# Revit family: STWS_приток
name_source: partatom
category: Воздухораспределители
revit_build: Autodesk Revit 2014 (Build: 20130308_1515(x64)
units: mm (PartAtom-declared; Revit-internal decimal feet)

## types (2484) — shared parameters
A = 52 мм
URL = http://inplast.ru
margins = 10 мм
Изготовитель = INPLAST-SMAY
Описание = Двухрядная решетка с горизонтальными направляющими

## per-type parameters (varying)
| type | Aef | C | C' | D | D' | n1 | n2 | Материал | Тип крепежа |
| STWS-100х100-SL | 0.006 м² | 100 мм | 95 мм | 100 мм | 95 мм | 10 | 10 | Сталь_RAL9016 (INPLAST) | саморезы |
| STWS-125х100-SL | 0.008 м² | 125 мм | 120 мм | 100 мм | 95 мм | 10 | 13 | Сталь_RAL9016 (INPLAST) | саморезы |
| STWS-125х125-SL | 0.009 м² | 125 мм | 120 мм | 125 мм | 120 мм | 13 | 13 | Сталь_RAL9016 (INPLAST) | саморезы |
| STWS-150х100-SL | 0.009 м² | 150 мм | 145 мм | 100 мм | 95 мм | 10 | 15 | Сталь_RAL9016 (INPLAST) | саморезы |
| STWS-150х125-SL | 0.011 м² | 150 мм | 145 мм | 125 мм | 120 мм | 13 | 15 | Сталь_RAL9016 (INPLAST) | саморезы |
| STWS-150х150-SL | 0.014 м² | 150 мм | 145 мм | 150 мм | 145 мм | 15 | 15 | Сталь_RAL9016 (INPLAST) | саморезы |
| STWS-200х100-SL | 0.012 м² | 200 мм | 195 мм | 100 мм | 95 мм | 10 | 20 | Сталь_RAL9016 (INPLAST) | саморезы |
| STWS-200х125-SL | 0.015 м² | 200 мм | 195 мм | 125 мм | 120 мм | 13 | 20 | Сталь_RAL9016 (INPLAST) | саморезы |
| STWS-200х150-SL | 0.018 м² | 200 мм | 195 мм | 150 мм | 145 мм | 15 | 20 | Сталь_RAL9016 (INPLAST) | саморезы |
| STWS-200х200-SL | 0.024 м² | 200 мм | 195 мм | 200 мм | 195 мм | 20 | 20 | Сталь_RAL9016 (INPLAST) | саморезы |
| STWS-225х100-SL | 0.014 м² | 225 мм | 220 мм | 100 мм | 95 мм | 10 | 23 | Сталь_RAL9016 (INPLAST) | саморезы |
| STWS-225х125-SL | 0.017 м² | 225 мм | 220 мм | 125 мм | 120 мм | 13 | 23 | Сталь_RAL9016 (INPLAST) | саморезы |
| STWS-225х150-SL | 0.020 м² | 225 мм | 220 мм | 150 мм | 145 мм | 15 | 23 | Сталь_RAL9016 (INPLAST) | саморезы |
| STWS-225х200-SL | 0.027 м² | 225 мм | 220 мм | 200 мм | 195 мм | 20 | 23 | Сталь_RAL9016 (INPLAST) | саморезы |
| STWS-225х225-SL | 0.030 м² | 225 мм | 220 мм | 225 мм | 220 мм | 23 | 23 | Сталь_RAL9016 (INPLAST) | саморезы |
| STWS-250х100-SL | 0.015 м² | 250 мм | 245 мм | 100 мм | 95 мм | 10 | 25 | Сталь_RAL9016 (INPLAST) | саморезы |
| STWS-250х125-SL | 0.019 м² | 250 мм | 245 мм | 125 мм | 120 мм | 13 | 25 | Сталь_RAL9016 (INPLAST) | саморезы |
| STWS-250х150-SL | 0.023 м² | 250 мм | 245 мм | 150 мм | 145 мм | 15 | 25 | Сталь_RAL9016 (INPLAST) | саморезы |
| STWS-250х200-SL | 0.030 м² | 250 мм | 245 мм | 200 мм | 195 мм | 20 | 25 | Сталь_RAL9016 (INPLAST) | саморезы |
| STWS-250х225-SL | 0.034 м² | 250 мм | 245 мм | 225 мм | 220 мм | 23 | 25 | Сталь_RAL9016 (INPLAST) | саморезы |
| STWS-250х250-SL | 0.038 м² | 250 мм | 245 мм | 250 мм | 245 мм | 25 | 25 | Сталь_RAL9016 (INPLAST) | саморезы |
| STWS-300х100-SL | 0.018 м² | 300 мм | 295 мм | 100 мм | 95 мм | 10 | 30 | Сталь_RAL9016 (INPLAST) | саморезы |
| STWS-300х125-SL | 0.023 м² | 300 мм | 295 мм | 125 мм | 120 мм | 13 | 30 | Сталь_RAL9016 (INPLAST) | саморезы |
| STWS-300х150-SL | 0.027 м² | 300 мм | 295 мм | 150 мм | 145 мм | 15 | 30 | Сталь_RAL9016 (INPLAST) | саморезы |
| STWS-300х200-SL | 0.036 м² | 300 мм | 295 мм | 200 мм | 195 мм | 20 | 30 | Сталь_RAL9016 (INPLAST) | саморезы |
| STWS-300х225-SL | 0.041 м² | 300 мм | 295 мм | 225 мм | 220 мм | 23 | 30 | Сталь_RAL9016 (INPLAST) | саморезы |
| STWS-300х250-SL | 0.045 м² | 300 мм | 295 мм | 250 мм | 245 мм | 25 | 30 | Сталь_RAL9016 (INPLAST) | саморезы |
| STWS-300х300-SL | 0.054 м² | 300 мм | 295 мм | 300 мм | 295 мм | 30 | 30 | Сталь_RAL9016 (INPLAST) | саморезы |
| STWS-325х100-SL | 0.020 м² | 325 мм | 320 мм | 100 мм | 95 мм | 10 | 33 | Сталь_RAL9016 (INPLAST) | саморезы |
| STWS-325х125-SL | 0.024 м² | 325 мм | 320 мм | 125 мм | 120 мм | 13 | 33 | Сталь_RAL9016 (INPLAST) | саморезы |
| STWS-325х150-SL | 0.029 м² | 325 мм | 320 мм | 150 мм | 145 мм | 15 | 33 | Сталь_RAL9016 (INPLAST) | саморезы |
| STWS-325х200-SL | 0.039 м² | 325 мм | 320 мм | 200 мм | 195 мм | 20 | 33 | Сталь_RAL9016 (INPLAST) | саморезы |
| STWS-325х225-SL | 0.044 м² | 325 мм | 320 мм | 225 мм | 220 мм | 23 | 33 | Сталь_RAL9016 (INPLAST) | саморезы |
| STWS-325х250-SL | 0.049 м² | 325 мм | 320 мм | 250 мм | 245 мм | 25 | 33 | Сталь_RAL9016 (INPLAST) | саморезы |
| STWS-325х300-SL | 0.059 м² | 325 мм | 320 мм | 300 мм | 295 мм | 30 | 33 | Сталь_RAL9016 (INPLAST) | саморезы |
| STWS-325х325-SL | 0.064 м² | 325 мм | 320 мм | 325 мм | 320 мм | 33 | 33 | Сталь_RAL9016 (INPLAST) | саморезы |
| STWS-350х100-SL | 0.021 м² | 350 мм | 345 мм | 100 мм | 95 мм | 10 | 35 | Сталь_RAL9016 (INPLAST) | саморезы |
| STWS-350х125-SL | 0.026 м² | 350 мм | 345 мм | 125 мм | 120 мм | 13 | 35 | Сталь_RAL9016 (INPLAST) | саморезы |
| STWS-350х150-SL | 0.032 м² | 350 мм | 345 мм | 150 мм | 145 мм | 15 | 35 | Сталь_RAL9016 (INPLAST) | саморезы |
| STWS-350х200-SL | 0.042 м² | 350 мм | 345 мм | 200 мм | 195 мм | 20 | 35 | Сталь_RAL9016 (INPLAST) | саморезы |
| STWS-350х225-SL | 0.047 м² | 350 мм | 345 мм | 225 мм | 220 мм | 23 | 35 | Сталь_RAL9016 (INPLAST) | саморезы |
| STWS-350х250-SL | 0.053 м² | 350 мм | 345 мм | 250 мм | 245 мм | 25 | 35 | Сталь_RAL9016 (INPLAST) | саморезы |
| STWS-350х300-SL | 0.063 м² | 350 мм | 345 мм | 300 мм | 295 мм | 30 | 35 | Сталь_RAL9016 (INPLAST) | саморезы |
| STWS-350х325-SL | 0.068 м² | 350 мм | 345 мм | 325 мм | 320 мм | 33 | 35 | Сталь_RAL9016 (INPLAST) | саморезы |
| STWS-350х350-SL | 0.074 м² | 350 мм | 345 мм | 350 мм | 345 мм | 35 | 35 | Сталь_RAL9016 (INPLAST) | саморезы |
| STWS-400х100-SL | 0.024 м² | 400 мм | 395 мм | 100 мм | 95 мм | 10 | 40 | Сталь_RAL9016 (INPLAST) | саморезы |
| STWS-400х125-SL | 0.030 м² | 400 мм | 395 мм | 125 мм | 120 мм | 13 | 40 | Сталь_RAL9016 (INPLAST) | саморезы |
| STWS-400х150-SL | 0.036 м² | 400 мм | 395 мм | 150 мм | 145 мм | 15 | 40 | Сталь_RAL9016 (INPLAST) | саморезы |
| STWS-400х200-SL | 0.048 м² | 400 мм | 395 мм | 200 мм | 195 мм | 20 | 40 | Сталь_RAL9016 (INPLAST) | саморезы |
| STWS-400х225-SL | 0.054 м² | 400 мм | 395 мм | 225 мм | 220 мм | 23 | 40 | Сталь_RAL9016 (INPLAST) | саморезы |
| STWS-400х250-SL | 0.060 м² | 400 мм | 395 мм | 250 мм | 245 мм | 25 | 40 | Сталь_RAL9016 (INPLAST) | саморезы |
| STWS-400х300-SL | 0.072 м² | 400 мм | 395 мм | 300 мм | 295 мм | 30 | 40 | Сталь_RAL9016 (INPLAST) | саморезы |
| STWS-400х325-SL | 0.078 м² | 400 мм | 395 мм | 325 мм | 320 мм | 33 | 40 | Сталь_RAL9016 (INPLAST) | саморезы |
| STWS-400х350-SL | 0.084 м² | 400 мм | 395 мм | 350 мм | 345 мм | 35 | 40 | Сталь_RAL9016 (INPLAST) | саморезы |
| STWS-400х400-SL | 0.096 м² | 400 мм | 395 мм | 400 мм | 395 мм | 40 | 40 | Сталь_RAL9016 (INPLAST) | саморезы |
| STWS-425х100-SL | 0.026 м² | 425 мм | 420 мм | 100 мм | 95 мм | 10 | 43 | Сталь_RAL9016 (INPLAST) | саморезы |
| STWS-425х125-SL | 0.032 м² | 425 мм | 420 мм | 125 мм | 120 мм | 13 | 43 | Сталь_RAL9016 (INPLAST) | саморезы |
| STWS-425х150-SL | 0.038 м² | 425 мм | 420 мм | 150 мм | 145 мм | 15 | 43 | Сталь_RAL9016 (INPLAST) | саморезы |
| STWS-425х200-SL | 0.051 м² | 425 мм | 420 мм | 200 мм | 195 мм | 20 | 43 | Сталь_RAL9016 (INPLAST) | саморезы |
| STWS-425х225-SL | 0.058 м² | 425 мм | 420 мм | 225 мм | 220 мм | 23 | 43 | Сталь_RAL9016 (INPLAST) | саморезы |
| STWS-425х250-SL | 0.064 м² | 425 мм | 420 мм | 250 мм | 245 мм | 25 | 43 | Сталь_RAL9016 (INPLAST) | саморезы |
| STWS-425х300-SL | 0.077 м² | 425 мм | 420 мм | 300 мм | 295 мм | 30 | 43 | Сталь_RAL9016 (INPLAST) | саморезы |
| STWS-425х325-SL | 0.083 м² | 425 мм | 420 мм | 325 мм | 320 мм | 33 | 43 | Сталь_RAL9016 (INPLAST) | саморезы |
| STWS-425х350-SL | 0.089 м² | 425 мм | 420 мм | 350 мм | 345 мм | 35 | 43 | Сталь_RAL9016 (INPLAST) | саморезы |
| STWS-425х400-SL | 0.102 м² | 425 мм | 420 мм | 400 мм | 395 мм | 40 | 43 | Сталь_RAL9016 (INPLAST) | саморезы |
| STWS-425х425-SL | 0.109 м² | 425 мм | 420 мм | 425 мм | 420 мм | 43 | 43 | Сталь_RAL9016 (INPLAST) | саморезы |
| STWS-450х100-SL | 0.027 м² | 450 мм | 445 мм | 100 мм | 95 мм | 10 | 45 | Сталь_RAL9016 (INPLAST) | саморезы |
| STWS-450х125-SL | 0.034 м² | 450 мм | 445 мм | 125 мм | 120 мм | 13 | 45 | Сталь_RAL9016 (INPLAST) | саморезы |
| STWS-450х150-SL | 0.041 м² | 450 мм | 445 мм | 150 мм | 145 мм | 15 | 45 | Сталь_RAL9016 (INPLAST) | саморезы |
| STWS-450х200-SL | 0.054 м² | 450 мм | 445 мм | 200 мм | 195 мм | 20 | 45 | Сталь_RAL9016 (INPLAST) | саморезы |
| STWS-450х225-SL | 0.061 м² | 450 мм | 445 мм | 225 мм | 220 мм | 23 | 45 | Сталь_RAL9016 (INPLAST) | саморезы |
| STWS-450х250-SL | 0.068 м² | 450 мм | 445 мм | 250 мм | 245 мм | 25 | 45 | Сталь_RAL9016 (INPLAST) | саморезы |
| STWS-450х300-SL | 0.081 м² | 450 мм | 445 мм | 300 мм | 295 мм | 30 | 45 | Сталь_RAL9016 (INPLAST) | саморезы |
| STWS-450х325-SL | 0.088 м² | 450 мм | 445 мм | 325 мм | 320 мм | 33 | 45 | Сталь_RAL9016 (INPLAST) | саморезы |
| STWS-450х350-SL | 0.095 м² | 450 мм | 445 мм | 350 мм | 345 мм | 35 | 45 | Сталь_RAL9016 (INPLAST) | саморезы |
| STWS-450х400-SL | 0.108 м² | 450 мм | 445 мм | 400 мм | 395 мм | 40 | 45 | Сталь_RAL9016 (INPLAST) | саморезы |
| STWS-450х425-SL | 0.115 м² | 450 мм | 445 мм | 425 мм | 420 мм | 43 | 45 | Сталь_RAL9016 (INPLAST) | саморезы |
| STWS-450х450-SL | 0.122 м² | 450 мм | 445 мм | 450 мм | 445 мм | 45 | 45 | Сталь_RAL9016 (INPLAST) | саморезы |
| STWS-500х100-SL | 0.030 м² | 500 мм | 495 мм | 100 мм | 95 мм | 10 | 50 | Сталь_RAL9016 (INPLAST) | саморезы |
| STWS-500х125-SL | 0.038 м² | 500 мм | 495 мм | 125 мм | 120 мм | 13 | 50 | Сталь_RAL9016 (INPLAST) | саморезы |
| STWS-500х150-SL | 0.045 м² | 500 мм | 495 мм | 150 мм | 145 мм | 15 | 50 | Сталь_RAL9016 (INPLAST) | саморезы |
| STWS-500х200-SL | 0.060 м² | 500 мм | 495 мм | 200 мм | 195 мм | 20 | 50 | Сталь_RAL9016 (INPLAST) | саморезы |
| STWS-500х225-SL | 0.068 м² | 500 мм | 495 мм | 225 мм | 220 мм | 23 | 50 | Сталь_RAL9016 (INPLAST) | саморезы |
| STWS-500х250-SL | 0.075 м² | 500 мм | 495 мм | 250 мм | 245 мм | 25 | 50 | Сталь_RAL9016 (INPLAST) | саморезы |
| STWS-500х300-SL | 0.090 м² | 500 мм | 495 мм | 300 мм | 295 мм | 30 | 50 | Сталь_RAL9016 (INPLAST) | саморезы |
| STWS-500х325-SL | 0.098 м² | 500 мм | 495 мм | 325 мм | 320 мм | 33 | 50 | Сталь_RAL9016 (INPLAST) | саморезы |
| STWS-500х350-SL | 0.105 м² | 500 мм | 495 мм | 350 мм | 345 мм | 35 | 50 | Сталь_RAL9016 (INPLAST) | саморезы |
| STWS-500х400-SL | 0.120 м² | 500 мм | 495 мм | 400 мм | 395 мм | 40 | 50 | Сталь_RAL9016 (INPLAST) | саморезы |
| STWS-500х425-SL | 0.128 м² | 500 мм | 495 мм | 425 мм | 420 мм | 43 | 50 | Сталь_RAL9016 (INPLAST) | саморезы |
| STWS-500х450-SL | 0.135 м² | 500 мм | 495 мм | 450 мм | 445 мм | 45 | 50 | Сталь_RAL9016 (INPLAST) | саморезы |
| STWS-500х500-SL | 0.150 м² | 500 мм | 495 мм | 500 мм | 495 мм | 50 | 50 | Сталь_RAL9016 (INPLAST) | саморезы |
| STWS-525х100-SL | 0.032 м² | 525 мм | 520 мм | 100 мм | 95 мм | 10 | 53 | Сталь_RAL9016 (INPLAST) | саморезы |
| STWS-525х125-SL | 0.039 м² | 525 мм | 520 мм | 125 мм | 120 мм | 13 | 53 | Сталь_RAL9016 (INPLAST) | саморезы |
| STWS-525х150-SL | 0.047 м² | 525 мм | 520 мм | 150 мм | 145 мм | 15 | 53 | Сталь_RAL9016 (INPLAST) | саморезы |
| STWS-525х200-SL | 0.063 м² | 525 мм | 520 мм | 200 мм | 195 мм | 20 | 53 | Сталь_RAL9016 (INPLAST) | саморезы |
| STWS-525х225-SL | 0.071 м² | 525 мм | 520 мм | 225 мм | 220 мм | 23 | 53 | Сталь_RAL9016 (INPLAST) | саморезы |
| STWS-525х250-SL | 0.079 м² | 525 мм | 520 мм | 250 мм | 245 мм | 25 | 53 | Сталь_RAL9016 (INPLAST) | саморезы |
| STWS-525х300-SL | 0.095 м² | 525 мм | 520 мм | 300 мм | 295 мм | 30 | 53 | Сталь_RAL9016 (INPLAST) | саморезы |
| STWS-525х325-SL | 0.103 м² | 525 мм | 520 мм | 325 мм | 320 мм | 33 | 53 | Сталь_RAL9016 (INPLAST) | саморезы |
| STWS-525х350-SL | 0.111 м² | 525 мм | 520 мм | 350 мм | 345 мм | 35 | 53 | Сталь_RAL9016 (INPLAST) | саморезы |
| STWS-525х400-SL | 0.126 м² | 525 мм | 520 мм | 400 мм | 395 мм | 40 | 53 | Сталь_RAL9016 (INPLAST) | саморезы |
| STWS-525х425-SL | 0.134 м² | 525 мм | 520 мм | 425 мм | 420 мм | 43 | 53 | Сталь_RAL9016 (INPLAST) | саморезы |
| STWS-525х450-SL | 0.142 м² | 525 мм | 520 мм | 450 мм | 445 мм | 45 | 53 | Сталь_RAL9016 (INPLAST) | саморезы |
| STWS-525х500-SL | 0.158 м² | 525 мм | 520 мм | 500 мм | 495 мм | 50 | 53 | Сталь_RAL9016 (INPLAST) | саморезы |
| STWS-525х525-SL | 0.166 м² | 525 мм | 520 мм | 525 мм | 520 мм | 53 | 53 | Сталь_RAL9016 (INPLAST) | саморезы |
| STWS-550х100-SL | 0.033 м² | 550 мм | 545 мм | 100 мм | 95 мм | 10 | 55 | Сталь_RAL9016 (INPLAST) | саморезы |
| STWS-550х125-SL | 0.041 м² | 550 мм | 545 мм | 125 мм | 120 мм | 13 | 55 | Сталь_RAL9016 (INPLAST) | саморезы |
| STWS-550х150-SL | 0.050 м² | 550 мм | 545 мм | 150 мм | 145 мм | 15 | 55 | Сталь_RAL9016 (INPLAST) | саморезы |
| STWS-550х200-SL | 0.066 м² | 550 мм | 545 мм | 200 мм | 195 мм | 20 | 55 | Сталь_RAL9016 (INPLAST) | саморезы |
| STWS-550х225-SL | 0.074 м² | 550 мм | 545 мм | 225 мм | 220 мм | 23 | 55 | Сталь_RAL9016 (INPLAST) | саморезы |
| STWS-550х250-SL | 0.083 м² | 550 мм | 545 мм | 250 мм | 245 мм | 25 | 55 | Сталь_RAL9016 (INPLAST) | саморезы |
| STWS-550х300-SL | 0.099 м² | 550 мм | 545 мм | 300 мм | 295 мм | 30 | 55 | Сталь_RAL9016 (INPLAST) | саморезы |
| STWS-550х325-SL | 0.108 м² | 550 мм | 545 мм | 325 мм | 320 мм | 33 | 55 | Сталь_RAL9016 (INPLAST) | саморезы |
| STWS-550х350-SL | 0.116 м² | 550 мм | 545 мм | 350 мм | 345 мм | 35 | 55 | Сталь_RAL9016 (INPLAST) | саморезы |
| STWS-550х400-SL | 0.132 м² | 550 мм | 545 мм | 400 мм | 395 мм | 40 | 55 | Сталь_RAL9016 (INPLAST) | саморезы |
| STWS-550х425-SL | 0.141 м² | 550 мм | 545 мм | 425 мм | 420 мм | 43 | 55 | Сталь_RAL9016 (INPLAST) | саморезы |
| STWS-550х450-SL | 0.149 м² | 550 мм | 545 мм | 450 мм | 445 мм | 45 | 55 | Сталь_RAL9016 (INPLAST) | саморезы |
| STWS-550х500-SL | 0.165 м² | 550 мм | 545 мм | 500 мм | 495 мм | 50 | 55 | Сталь_RAL9016 (INPLAST) | саморезы |
| STWS-550х525-SL | 0.174 м² | 550 мм | 545 мм | 525 мм | 520 мм | 53 | 55 | Сталь_RAL9016 (INPLAST) | саморезы |
| STWS-550х550-SL | 0.182 м² | 550 мм | 545 мм | 550 мм | 545 мм | 55 | 55 | Сталь_RAL9016 (INPLAST) | саморезы |
| STWS-600х100-SL | 0.036 м² | 600 мм | 595 мм | 100 мм | 95 мм | 10 | 60 | Сталь_RAL9016 (INPLAST) | саморезы |
| STWS-600х125-SL | 0.045 м² | 600 мм | 595 мм | 125 мм | 120 мм | 13 | 60 | Сталь_RAL9016 (INPLAST) | саморезы |
| STWS-600х150-SL | 0.054 м² | 600 мм | 595 мм | 150 мм | 145 мм | 15 | 60 | Сталь_RAL9016 (INPLAST) | саморезы |
| STWS-600х200-SL | 0.072 м² | 600 мм | 595 мм | 200 мм | 195 мм | 20 | 60 | Сталь_RAL9016 (INPLAST) | саморезы |
| STWS-600х225-SL | 0.081 м² | 600 мм | 595 мм | 225 мм | 220 мм | 23 | 60 | Сталь_RAL9016 (INPLAST) | саморезы |
| STWS-600х250-SL | 0.090 м² | 600 мм | 595 мм | 250 мм | 245 мм | 25 | 60 | Сталь_RAL9016 (INPLAST) | саморезы |
| STWS-600х300-SL | 0.108 м² | 600 мм | 595 мм | 300 мм | 295 мм | 30 | 60 | Сталь_RAL9016 (INPLAST) | саморезы |
| STWS-600х325-SL | 0.117 м² | 600 мм | 595 мм | 325 мм | 320 мм | 33 | 60 | Сталь_RAL9016 (INPLAST) | саморезы |
| STWS-600х350-SL | 0.126 м² | 600 мм | 595 мм | 350 мм | 345 мм | 35 | 60 | Сталь_RAL9016 (INPLAST) | саморезы |
| STWS-600х400-SL | 0.144 м² | 600 мм | 595 мм | 400 мм | 395 мм | 40 | 60 | Сталь_RAL9016 (INPLAST) | саморезы |
| STWS-600х425-SL | 0.153 м² | 600 мм | 595 мм | 425 мм | 420 мм | 43 | 60 | Сталь_RAL9016 (INPLAST) | саморезы |
| STWS-600х450-SL | 0.162 м² | 600 мм | 595 мм | 450 мм | 445 мм | 45 | 60 | Сталь_RAL9016 (INPLAST) | саморезы |
| STWS-600х500-SL | 0.180 м² | 600 мм | 595 мм | 500 мм | 495 мм | 50 | 60 | Сталь_RAL9016 (INPLAST) | саморезы |
| STWS-600х525-SL | 0.190 м² | 600 мм | 595 мм | 525 мм | 520 мм | 53 | 60 | Сталь_RAL9016 (INPLAST) | саморезы |
| STWS-600х550-SL | 0.199 м² | 600 мм | 595 мм | 550 мм | 545 мм | 55 | 60 | Сталь_RAL9016 (INPLAST) | саморезы |
| STWS-600х600-SL | 0.217 м² | 600 мм | 595 мм | 600 мм | 595 мм | 60 | 60 | Сталь_RAL9016 (INPLAST) | саморезы |
| STWS-625х100-SL | 0.038 м² | 625 мм | 620 мм | 100 мм | 95 мм | 10 | 63 | Сталь_RAL9016 (INPLAST) | саморезы |
| STWS-625х125-SL | 0.047 м² | 625 мм | 620 мм | 125 мм | 120 мм | 13 | 63 | Сталь_RAL9016 (INPLAST) | саморезы |
| STWS-625х150-SL | 0.056 м² | 625 мм | 620 мм | 150 мм | 145 мм | 15 | 63 | Сталь_RAL9016 (INPLAST) | саморезы |
| STWS-625х200-SL | 0.075 м² | 625 мм | 620 мм | 200 мм | 195 мм | 20 | 63 | Сталь_RAL9016 (INPLAST) | саморезы |
| STWS-625х225-SL | 0.085 м² | 625 мм | 620 мм | 225 мм | 220 мм | 23 | 63 | Сталь_RAL9016 (INPLAST) | саморезы |
| STWS-625х250-SL | 0.094 м² | 625 мм | 620 мм | 250 мм | 245 мм | 25 | 63 | Сталь_RAL9016 (INPLAST) | саморезы |
| STWS-625х300-SL | 0.113 м² | 625 мм | 620 мм | 300 мм | 295 мм | 30 | 63 | Сталь_RAL9016 (INPLAST) | саморезы |
| STWS-625х325-SL | 0.122 м² | 625 мм | 620 мм | 325 мм | 320 мм | 33 | 63 | Сталь_RAL9016 (INPLAST) | саморезы |
| STWS-625х350-SL | 0.132 м² | 625 мм | 620 мм | 350 мм | 345 мм | 35 | 63 | Сталь_RAL9016 (INPLAST) | саморезы |
| STWS-625х400-SL | 0.150 м² | 625 мм | 620 мм | 400 мм | 395 мм | 40 | 63 | Сталь_RAL9016 (INPLAST) | саморезы |
| STWS-625х425-SL | 0.160 м² | 625 мм | 620 мм | 425 мм | 420 мм | 43 | 63 | Сталь_RAL9016 (INPLAST) | саморезы |
| STWS-625х450-SL | 0.169 м² | 625 мм | 620 мм | 450 мм | 445 мм | 45 | 63 | Сталь_RAL9016 (INPLAST) | саморезы |
| STWS-625х500-SL | 0.188 м² | 625 мм | 620 мм | 500 мм | 495 мм | 50 | 63 | Сталь_RAL9016 (INPLAST) | саморезы |
| STWS-625х525-SL | 0.197 м² | 625 мм | 620 мм | 525 мм | 520 мм | 53 | 63 | Сталь_RAL9016 (INPLAST) | саморезы |
| STWS-625х550-SL | 0.207 м² | 625 мм | 620 мм | 550 мм | 545 мм | 55 | 63 | Сталь_RAL9016 (INPLAST) | саморезы |
| STWS-625х600-SL | 0.226 м² | 625 мм | 620 мм | 600 мм | 595 мм | 60 | 63 | Сталь_RAL9016 (INPLAST) | саморезы |
| STWS-625х625-SL | 0.235 м² | 625 мм | 620 мм | 625 мм | 620 мм | 63 | 63 | Сталь_RAL9016 (INPLAST) | саморезы |
| STWS-650х100-SL | 0.039 м² | 650 мм | 645 мм | 100 мм | 95 мм | 10 | 65 | Сталь_RAL9016 (INPLAST) | саморезы |
| STWS-650х125-SL | 0.049 м² | 650 мм | 645 мм | 125 мм | 120 мм | 13 | 65 | Сталь_RAL9016 (INPLAST) | саморезы |
| STWS-650х150-SL | 0.059 м² | 650 мм | 645 мм | 150 мм | 145 мм | 15 | 65 | Сталь_RAL9016 (INPLAST) | саморезы |
| STWS-650х200-SL | 0.078 м² | 650 мм | 645 мм | 200 мм | 195 мм | 20 | 65 | Сталь_RAL9016 (INPLAST) | саморезы |
| STWS-650х225-SL | 0.088 м² | 650 мм | 645 мм | 225 мм | 220 мм | 23 | 65 | Сталь_RAL9016 (INPLAST) | саморезы |
| STWS-650х250-SL | 0.098 м² | 650 мм | 645 мм | 250 мм | 245 мм | 25 | 65 | Сталь_RAL9016 (INPLAST) | саморезы |
| STWS-650х300-SL | 0.117 м² | 650 мм | 645 мм | 300 мм | 295 мм | 30 | 65 | Сталь_RAL9016 (INPLAST) | саморезы |
| STWS-650х325-SL | 0.127 м² | 650 мм | 645 мм | 325 мм | 320 мм | 33 | 65 | Сталь_RAL9016 (INPLAST) | саморезы |
| STWS-650х350-SL | 0.137 м² | 650 мм | 645 мм | 350 мм | 345 мм | 35 | 65 | Сталь_RAL9016 (INPLAST) | саморезы |
| STWS-650х400-SL | 0.156 м² | 650 мм | 645 мм | 400 мм | 395 мм | 40 | 65 | Сталь_RAL9016 (INPLAST) | саморезы |
| STWS-650х425-SL | 0.166 м² | 650 мм | 645 мм | 425 мм | 420 мм | 43 | 65 | Сталь_RAL9016 (INPLAST) | саморезы |
| STWS-650х450-SL | 0.176 м² | 650 мм | 645 мм | 450 мм | 445 мм | 45 | 65 | Сталь_RAL9016 (INPLAST) | саморезы |
| STWS-650х500-SL | 0.196 м² | 650 мм | 645 мм | 500 мм | 495 мм | 50 | 65 | Сталь_RAL9016 (INPLAST) | саморезы |
| STWS-650х525-SL | 0.205 м² | 650 мм | 645 мм | 525 мм | 520 мм | 53 | 65 | Сталь_RAL9016 (INPLAST) | саморезы |
| STWS-650х550-SL | 0.215 м² | 650 мм | 645 мм | 550 мм | 545 мм | 55 | 65 | Сталь_RAL9016 (INPLAST) | саморезы |
| STWS-650х600-SL | 0.235 м² | 650 мм | 645 мм | 600 мм | 595 мм | 60 | 65 | Сталь_RAL9016 (INPLAST) | саморезы |
| STWS-650х625-SL | 0.244 м² | 650 мм | 645 мм | 625 мм | 620 мм | 63 | 65 | Сталь_RAL9016 (INPLAST) | саморезы |
| STWS-650х650-SL | 0.254 м² | 650 мм | 645 мм | 650 мм | 645 мм | 65 | 65 | Сталь_RAL9016 (INPLAST) | саморезы |
| STWS-700х100-SL | 0.042 м² | 700 мм | 695 мм | 100 мм | 95 мм | 10 | 70 | Сталь_RAL9016 (INPLAST) | саморезы |
| STWS-700х125-SL | 0.053 м² | 700 мм | 695 мм | 125 мм | 120 мм | 13 | 70 | Сталь_RAL9016 (INPLAST) | саморезы |
| STWS-700х150-SL | 0.063 м² | 700 мм | 695 мм | 150 мм | 145 мм | 15 | 70 | Сталь_RAL9016 (INPLAST) | саморезы |
| STWS-700х200-SL | 0.084 м² | 700 мм | 695 мм | 200 мм | 195 мм | 20 | 70 | Сталь_RAL9016 (INPLAST) | саморезы |
| STWS-700х225-SL | 0.095 м² | 700 мм | 695 мм | 225 мм | 220 мм | 23 | 70 | Сталь_RAL9016 (INPLAST) | саморезы |
| STWS-700х250-SL | 0.105 м² | 700 мм | 695 мм | 250 мм | 245 мм | 25 | 70 | Сталь_RAL9016 (INPLAST) | саморезы |
| STWS-700х300-SL | 0.126 м² | 700 мм | 695 мм | 300 мм | 295 мм | 30 | 70 | Сталь_RAL9016 (INPLAST) | саморезы |
| STWS-700х325-SL | 0.137 м² | 700 мм | 695 мм | 325 мм | 320 мм | 33 | 70 | Сталь_RAL9016 (INPLAST) | саморезы |
| STWS-700х350-SL | 0.147 м² | 700 мм | 695 мм | 350 мм | 345 мм | 35 | 70 | Сталь_RAL9016 (INPLAST) | саморезы |
| STWS-700х400-SL | 0.168 м² | 700 мм | 695 мм | 400 мм | 395 мм | 40 | 70 | Сталь_RAL9016 (INPLAST) | саморезы |
| STWS-700х425-SL | 0.179 м² | 700 мм | 695 мм | 425 мм | 420 мм | 43 | 70 | Сталь_RAL9016 (INPLAST) | саморезы |
| STWS-700х450-SL | 0.190 м² | 700 мм | 695 мм | 450 мм | 445 мм | 45 | 70 | Сталь_RAL9016 (INPLAST) | саморезы |
| STWS-700х500-SL | 0.211 м² | 700 мм | 695 мм | 500 мм | 495 мм | 50 | 70 | Сталь_RAL9016 (INPLAST) | саморезы |
| STWS-700х525-SL | 0.221 м² | 700 мм | 695 мм | 525 мм | 520 мм | 53 | 70 | Сталь_RAL9016 (INPLAST) | саморезы |
| STWS-700х550-SL | 0.232 м² | 700 мм | 695 мм | 550 мм | 545 мм | 55 | 70 | Сталь_RAL9016 (INPLAST) | саморезы |
| STWS-700х600-SL | 0.253 м² | 700 мм | 695 мм | 600 мм | 595 мм | 60 | 70 | Сталь_RAL9016 (INPLAST) | саморезы |
| STWS-700х625-SL | 0.263 м² | 700 мм | 695 мм | 625 мм | 620 мм | 63 | 70 | Сталь_RAL9016 (INPLAST) | саморезы |
| STWS-700х650-SL | 0.274 м² | 700 мм | 695 мм | 650 мм | 645 мм | 65 | 70 | Сталь_RAL9016 (INPLAST) | саморезы |
| STWS-725х100-SL | 0.044 м² | 725 мм | 720 мм | 100 мм | 95 мм | 10 | 73 | Сталь_RAL9016 (INPLAST) | саморезы |
| STWS-725х125-SL | 0.055 м² | 725 мм | 720 мм | 125 мм | 120 мм | 13 | 73 | Сталь_RAL9016 (INPLAST) | саморезы |
| STWS-725х150-SL | 0.065 м² | 725 мм | 720 мм | 150 мм | 145 мм | 15 | 73 | Сталь_RAL9016 (INPLAST) | саморезы |
| STWS-725х200-SL | 0.087 м² | 725 мм | 720 мм | 200 мм | 195 мм | 20 | 73 | Сталь_RAL9016 (INPLAST) | саморезы |
| STWS-725х225-SL | 0.098 м² | 725 мм | 720 мм | 225 мм | 220 мм | 23 | 73 | Сталь_RAL9016 (INPLAST) | саморезы |
| STWS-725х250-SL | 0.109 м² | 725 мм | 720 мм | 250 мм | 245 мм | 25 | 73 | Сталь_RAL9016 (INPLAST) | саморезы |
| STWS-725х300-SL | 0.131 м² | 725 мм | 720 мм | 300 мм | 295 мм | 30 | 73 | Сталь_RAL9016 (INPLAST) | саморезы |
| STWS-725х325-SL | 0.142 м² | 725 мм | 720 мм | 325 мм | 320 мм | 33 | 73 | Сталь_RAL9016 (INPLAST) | саморезы |
| STWS-725х350-SL | 0.153 м² | 725 мм | 720 мм | 350 мм | 345 мм | 35 | 73 | Сталь_RAL9016 (INPLAST) | саморезы |
| STWS-725х400-SL | 0.174 м² | 725 мм | 720 мм | 400 мм | 395 мм | 40 | 73 | Сталь_RAL9016 (INPLAST) | саморезы |
| STWS-725х425-SL | 0.185 м² | 725 мм | 720 мм | 425 мм | 420 мм | 43 | 73 | Сталь_RAL9016 (INPLAST) | саморезы |
| STWS-725х450-SL | 0.196 м² | 725 мм | 720 мм | 450 мм | 445 мм | 45 | 73 | Сталь_RAL9016 (INPLAST) | саморезы |
| STWS-725х500-SL | 0.218 м² | 725 мм | 720 мм | 500 мм | 495 мм | 50 | 73 | Сталь_RAL9016 (INPLAST) | саморезы |
| STWS-725х525-SL | 0.229 м² | 725 мм | 720 мм | 525 мм | 520 мм | 53 | 73 | Сталь_RAL9016 (INPLAST) | саморезы |
| STWS-725х550-SL | 0.240 м² | 725 мм | 720 мм | 550 мм | 545 мм | 55 | 73 | Сталь_RAL9016 (INPLAST) | саморезы |
| STWS-725х600-SL | 0.262 м² | 725 мм | 720 мм | 600 мм | 595 мм | 60 | 73 | Сталь_RAL9016 (INPLAST) | саморезы |
| STWS-725х625-SL | 0.273 м² | 725 мм | 720 мм | 625 мм | 620 мм | 63 | 73 | Сталь_RAL9016 (INPLAST) | саморезы |
| STWS-725х650-SL | 0.284 м² | 725 мм | 720 мм | 650 мм | 645 мм | 65 | 73 | Сталь_RAL9016 (INPLAST) | саморезы |
| STWS-750х100-SL | 0.045 м² | 750 мм | 745 мм | 100 мм | 95 мм | 10 | 75 | Сталь_RAL9016 (INPLAST) | саморезы |
| STWS-750х125-SL | 0.056 м² | 750 мм | 745 мм | 125 мм | 120 мм | 13 | 75 | Сталь_RAL9016 (INPLAST) | саморезы |
| STWS-750х150-SL | 0.068 м² | 750 мм | 745 мм | 150 мм | 145 мм | 15 | 75 | Сталь_RAL9016 (INPLAST) | саморезы |
| STWS-750х200-SL | 0.090 м² | 750 мм | 745 мм | 200 мм | 195 мм | 20 | 75 | Сталь_RAL9016 (INPLAST) | саморезы |
| STWS-750х225-SL | 0.102 м² | 750 мм | 745 мм | 225 мм | 220 мм | 23 | 75 | Сталь_RAL9016 (INPLAST) | саморезы |
| STWS-750х250-SL | 0.113 м² | 750 мм | 745 мм | 250 мм | 245 мм | 25 | 75 | Сталь_RAL9016 (INPLAST) | саморезы |
| STWS-750х300-SL | 0.135 м² | 750 мм | 745 мм | 300 мм | 295 мм | 30 | 75 | Сталь_RAL9016 (INPLAST) | саморезы |
| STWS-750х325-SL | 0.147 м² | 750 мм | 745 мм | 325 мм | 320 мм | 33 | 75 | Сталь_RAL9016 (INPLAST) | саморезы |
| STWS-750х350-SL | 0.158 м² | 750 мм | 745 мм | 350 мм | 345 мм | 35 | 75 | Сталь_RAL9016 (INPLAST) | саморезы |
| STWS-750х400-SL | 0.180 м² | 750 мм | 745 мм | 400 мм | 395 мм | 40 | 75 | Сталь_RAL9016 (INPLAST) | саморезы |
| STWS-750х425-SL | 0.192 м² | 750 мм | 745 мм | 425 мм | 420 мм | 43 | 75 | Сталь_RAL9016 (INPLAST) | саморезы |
| STWS-750х450-SL | 0.203 м² | 750 мм | 745 мм | 450 мм | 445 мм | 45 | 75 | Сталь_RAL9016 (INPLAST) | саморезы |
| STWS-750х500-SL | 0.226 м² | 750 мм | 745 мм | 500 мм | 495 мм | 50 | 75 | Сталь_RAL9016 (INPLAST) | саморезы |
| STWS-750х525-SL | 0.237 м² | 750 мм | 745 мм | 525 мм | 520 мм | 53 | 75 | Сталь_RAL9016 (INPLAST) | саморезы |
| STWS-750х550-SL | 0.248 м² | 750 мм | 745 мм | 550 мм | 545 мм | 55 | 75 | Сталь_RAL9016 (INPLAST) | саморезы |
| STWS-750х600-SL | 0.271 м² | 750 мм | 745 мм | 600 мм | 595 мм | 60 | 75 | Сталь_RAL9016 (INPLAST) | саморезы |
| STWS-750х625-SL | 0.282 м² | 750 мм | 745 мм | 625 мм | 620 мм | 63 | 75 | Сталь_RAL9016 (INPLAST) | саморезы |
| STWS-750х650-SL | 0.293 м² | 750 мм | 745 мм | 650 мм | 645 мм | 65 | 75 | Сталь_RAL9016 (INPLAST) | саморезы |
| STWS-800х100-SL | 0.048 м² | 800 мм | 795 мм | 100 мм | 95 мм | 10 | 80 | Сталь_RAL9016 (INPLAST) | саморезы |
| STWS-800х125-SL | 0.060 м² | 800 мм | 795 мм | 125 мм | 120 мм | 13 | 80 | Сталь_RAL9016 (INPLAST) | саморезы |
| STWS-800х150-SL | 0.072 м² | 800 мм | 795 мм | 150 мм | 145 мм | 15 | 80 | Сталь_RAL9016 (INPLAST) | саморезы |
| STWS-800х200-SL | 0.096 м² | 800 мм | 795 мм | 200 мм | 195 мм | 20 | 80 | Сталь_RAL9016 (INPLAST) | саморезы |
| STWS-800х225-SL | 0.108 м² | 800 мм | 795 мм | 225 мм | 220 мм | 23 | 80 | Сталь_RAL9016 (INPLAST) | саморезы |
| STWS-800х250-SL | 0.120 м² | 800 мм | 795 мм | 250 мм | 245 мм | 25 | 80 | Сталь_RAL9016 (INPLAST) | саморезы |
| STWS-800х300-SL | 0.144 м² | 800 мм | 795 мм | 300 мм | 295 мм | 30 | 80 | Сталь_RAL9016 (INPLAST) | саморезы |
| STWS-800х325-SL | 0.156 м² | 800 мм | 795 мм | 325 мм | 320 мм | 33 | 80 | Сталь_RAL9016 (INPLAST) | саморезы |
| STWS-800х350-SL | 0.168 м² | 800 мм | 795 мм | 350 мм | 345 мм | 35 | 80 | Сталь_RAL9016 (INPLAST) | саморезы |
| STWS-800х400-SL | 0.193 м² | 800 мм | 795 мм | 400 мм | 395 мм | 40 | 80 | Сталь_RAL9016 (INPLAST) | саморезы |
| STWS-800х425-SL | 0.205 м² | 800 мм | 795 мм | 425 мм | 420 мм | 43 | 80 | Сталь_RAL9016 (INPLAST) | саморезы |
| STWS-800х450-SL | 0.217 м² | 800 мм | 795 мм | 450 мм | 445 мм | 45 | 80 | Сталь_RAL9016 (INPLAST) | саморезы |
| STWS-800х500-SL | 0.241 м² | 800 мм | 795 мм | 500 мм | 495 мм | 50 | 80 | Сталь_RAL9016 (INPLAST) | саморезы |
| STWS-800х525-SL | 0.253 м² | 800 мм | 795 мм | 525 мм | 520 мм | 53 | 80 | Сталь_RAL9016 (INPLAST) | саморезы |
| STWS-800х550-SL | 0.265 м² | 800 мм | 795 мм | 550 мм | 545 мм | 55 | 80 | Сталь_RAL9016 (INPLAST) | саморезы |
| STWS-800х600-SL | 0.289 м² | 800 мм | 795 мм | 600 мм | 595 мм | 60 | 80 | Сталь_RAL9016 (INPLAST) | саморезы |
| STWS-800х625-SL | 0.301 м² | 800 мм | 795 мм | 625 мм | 620 мм | 63 | 80 | Сталь_RAL9016 (INPLAST) | саморезы |
| STWS-800х650-SL | 0.313 м² | 800 мм | 795 мм | 650 мм | 645 мм | 65 | 80 | Сталь_RAL9016 (INPLAST) | саморезы |
| STWS-825х100-SL | 0.050 м² | 825 мм | 820 мм | 100 мм | 95 мм | 10 | 83 | Сталь_RAL9016 (INPLAST) | саморезы |
| STWS-825х125-SL | 0.062 м² | 825 мм | 820 мм | 125 мм | 120 мм | 13 | 83 | Сталь_RAL9016 (INPLAST) | саморезы |
| STWS-825х150-SL | 0.074 м² | 825 мм | 820 мм | 150 мм | 145 мм | 15 | 83 | Сталь_RAL9016 (INPLAST) | саморезы |
| STWS-825х200-SL | 0.099 м² | 825 мм | 820 мм | 200 мм | 195 мм | 20 | 83 | Сталь_RAL9016 (INPLAST) | саморезы |
| STWS-825х225-SL | 0.112 м² | 825 мм | 820 мм | 225 мм | 220 мм | 23 | 83 | Сталь_RAL9016 (INPLAST) | саморезы |
| STWS-825х250-SL | 0.124 м² | 825 мм | 820 мм | 250 мм | 245 мм | 25 | 83 | Сталь_RAL9016 (INPLAST) | саморезы |
| STWS-825х300-SL | 0.149 м² | 825 мм | 820 мм | 300 мм | 295 мм | 30 | 83 | Сталь_RAL9016 (INPLAST) | саморезы |
| STWS-825х325-SL | 0.161 м² | 825 мм | 820 мм | 325 мм | 320 мм | 33 | 83 | Сталь_RAL9016 (INPLAST) | саморезы |
| STWS-825х350-SL | 0.174 м² | 825 мм | 820 мм | 350 мм | 345 мм | 35 | 83 | Сталь_RAL9016 (INPLAST) | саморезы |
| STWS-825х400-SL | 0.199 м² | 825 мм | 820 мм | 400 мм | 395 мм | 40 | 83 | Сталь_RAL9016 (INPLAST) | саморезы |
| STWS-825х425-SL | 0.211 м² | 825 мм | 820 мм | 425 мм | 420 мм | 43 | 83 | Сталь_RAL9016 (INPLAST) | саморезы |
| STWS-825х450-SL | 0.223 м² | 825 мм | 820 мм | 450 мм | 445 мм | 45 | 83 | Сталь_RAL9016 (INPLAST) | саморезы |
| STWS-825х500-SL | 0.248 м² | 825 мм | 820 мм | 500 мм | 495 мм | 50 | 83 | Сталь_RAL9016 (INPLAST) | саморезы |
| STWS-825х525-SL | 0.261 м² | 825 мм | 820 мм | 525 мм | 520 мм | 53 | 83 | Сталь_RAL9016 (INPLAST) | саморезы |
| STWS-825х550-SL | 0.273 м² | 825 мм | 820 мм | 550 мм | 545 мм | 55 | 83 | Сталь_RAL9016 (INPLAST) | саморезы |
| STWS-825х600-SL | 0.298 м² | 825 мм | 820 мм | 600 мм | 595 мм | 60 | 83 | Сталь_RAL9016 (INPLAST) | саморезы |
| STWS-825х625-SL | 0.310 м² | 825 мм | 820 мм | 625 мм | 620 мм | 63 | 83 | Сталь_RAL9016 (INPLAST) | саморезы |
| STWS-825х650-SL | 0.323 м² | 825 мм | 820 мм | 650 мм | 645 мм | 65 | 83 | Сталь_RAL9016 (INPLAST) | саморезы |
| STWS-850х100-SL | 0.051 м² | 850 мм | 845 мм | 100 мм | 95 мм | 10 | 85 | Сталь_RAL9016 (INPLAST) | саморезы |
| STWS-850х125-SL | 0.064 м² | 850 мм | 845 мм | 125 мм | 120 мм | 13 | 85 | Сталь_RAL9016 (INPLAST) | саморезы |
| STWS-850х150-SL | 0.077 м² | 850 мм | 845 мм | 150 мм | 145 мм | 15 | 85 | Сталь_RAL9016 (INPLAST) | саморезы |
| STWS-850х200-SL | 0.102 м² | 850 мм | 845 мм | 200 мм | 195 мм | 20 | 85 | Сталь_RAL9016 (INPLAST) | саморезы |
| STWS-850х225-SL | 0.115 м² | 850 мм | 845 мм | 225 мм | 220 мм | 23 | 85 | Сталь_RAL9016 (INPLAST) | саморезы |
| STWS-850х250-SL | 0.128 м² | 850 мм | 845 мм | 250 мм | 245 мм | 25 | 85 | Сталь_RAL9016 (INPLAST) | саморезы |
| STWS-850х300-SL | 0.153 м² | 850 мм | 845 мм | 300 мм | 295 мм | 30 | 85 | Сталь_RAL9016 (INPLAST) | саморезы |
| STWS-850х325-SL | 0.166 м² | 850 мм | 845 мм | 325 мм | 320 мм | 33 | 85 | Сталь_RAL9016 (INPLAST) | саморезы |
| STWS-850х350-SL | 0.179 м² | 850 мм | 845 мм | 350 мм | 345 мм | 35 | 85 | Сталь_RAL9016 (INPLAST) | саморезы |
| STWS-850х400-SL | 0.205 м² | 850 мм | 845 мм | 400 мм | 395 мм | 40 | 85 | Сталь_RAL9016 (INPLAST) | саморезы |
| STWS-850х425-SL | 0.217 м² | 850 мм | 845 мм | 425 мм | 420 мм | 43 | 85 | Сталь_RAL9016 (INPLAST) | саморезы |
| STWS-850х450-SL | 0.230 м² | 850 мм | 845 мм | 450 мм | 445 мм | 45 | 85 | Сталь_RAL9016 (INPLAST) | саморезы |
| STWS-850х500-SL | 0.256 м² | 850 мм | 845 мм | 500 мм | 495 мм | 50 | 85 | Сталь_RAL9016 (INPLAST) | саморезы |
| STWS-850х525-SL | 0.268 м² | 850 мм | 845 мм | 525 мм | 520 мм | 53 | 85 | Сталь_RAL9016 (INPLAST) | саморезы |
| STWS-850х550-SL | 0.281 м² | 850 мм | 845 мм | 550 мм | 545 мм | 55 | 85 | Сталь_RAL9016 (INPLAST) | саморезы |
| STWS-850х600-SL | 0.307 м² | 850 мм | 845 мм | 600 мм | 595 мм | 60 | 85 | Сталь_RAL9016 (INPLAST) | саморезы |
| STWS-850х625-SL | 0.320 м² | 850 мм | 845 мм | 625 мм | 620 мм | 63 | 85 | Сталь_RAL9016 (INPLAST) | саморезы |
| STWS-850х650-SL | 0.332 м² | 850 мм | 845 мм | 650 мм | 645 мм | 65 | 85 | Сталь_RAL9016 (INPLAST) | саморезы |
| STWS-900х100-SL | 0.054 м² | 900 мм | 895 мм | 100 мм | 95 мм | 10 | 90 | Сталь_RAL9016 (INPLAST) | саморезы |
| STWS-900х125-SL | 0.068 м² | 900 мм | 895 мм | 125 мм | 120 мм | 13 | 90 | Сталь_RAL9016 (INPLAST) | саморезы |
| STWS-900х150-SL | 0.081 м² | 900 мм | 895 мм | 150 мм | 145 мм | 15 | 90 | Сталь_RAL9016 (INPLAST) | саморезы |
| STWS-900х200-SL | 0.108 м² | 900 мм | 895 мм | 200 мм | 195 мм | 20 | 90 | Сталь_RAL9016 (INPLAST) | саморезы |
| STWS-900х225-SL | 0.122 м² | 900 мм | 895 мм | 225 мм | 220 мм | 23 | 90 | Сталь_RAL9016 (INPLAST) | саморезы |
| STWS-900х250-SL | 0.135 м² | 900 мм | 895 мм | 250 мм | 245 мм | 25 | 90 | Сталь_RAL9016 (INPLAST) | саморезы |
| STWS-900х300-SL | 0.162 м² | 900 мм | 895 мм | 300 мм | 295 мм | 30 | 90 | Сталь_RAL9016 (INPLAST) | саморезы |
| STWS-900х325-SL | 0.176 м² | 900 мм | 895 мм | 325 мм | 320 мм | 33 | 90 | Сталь_RAL9016 (INPLAST) | саморезы |
| STWS-900х350-SL | 0.190 м² | 900 мм | 895 мм | 350 мм | 345 мм | 35 | 90 | Сталь_RAL9016 (INPLAST) | саморезы |
| STWS-900х400-SL | 0.217 м² | 900 мм | 895 мм | 400 мм | 395 мм | 40 | 90 | Сталь_RAL9016 (INPLAST) | саморезы |
| STWS-900х425-SL | 0.230 м² | 900 мм | 895 мм | 425 мм | 420 мм | 43 | 90 | Сталь_RAL9016 (INPLAST) | саморезы |
| STWS-900х450-SL | 0.244 м² | 900 мм | 895 мм | 450 мм | 445 мм | 45 | 90 | Сталь_RAL9016 (INPLAST) | саморезы |
| STWS-900х500-SL | 0.271 м² | 900 мм | 895 мм | 500 мм | 495 мм | 50 | 90 | Сталь_RAL9016 (INPLAST) | саморезы |
| STWS-900х525-SL | 0.284 м² | 900 мм | 895 мм | 525 мм | 520 мм | 53 | 90 | Сталь_RAL9016 (INPLAST) | саморезы |
| STWS-900х550-SL | 0.298 м² | 900 мм | 895 мм | 550 мм | 545 мм | 55 | 90 | Сталь_RAL9016 (INPLAST) | саморезы |
| STWS-900х600-SL | 0.325 м² | 900 мм | 895 мм | 600 мм | 595 мм | 60 | 90 | Сталь_RAL9016 (INPLAST) | саморезы |
| STWS-900х625-SL | 0.338 м² | 900 мм | 895 мм | 625 мм | 620 мм | 63 | 90 | Сталь_RAL9016 (INPLAST) | саморезы |
| STWS-900х650-SL | 0.352 м² | 900 мм | 895 мм | 650 мм | 645 мм | 65 | 90 | Сталь_RAL9016 (INPLAST) | саморезы |
| STWS-925х100-SL | 0.056 м² | 925 мм | 920 мм | 100 мм | 95 мм | 10 | 93 | Сталь_RAL9016 (INPLAST) | саморезы |
| STWS-925х125-SL | 0.070 м² | 925 мм | 920 мм | 125 мм | 120 мм | 13 | 93 | Сталь_RAL9016 (INPLAST) | саморезы |
| STWS-925х150-SL | 0.083 м² | 925 мм | 920 мм | 150 мм | 145 мм | 15 | 93 | Сталь_RAL9016 (INPLAST) | саморезы |
| STWS-925х200-SL | 0.111 м² | 925 мм | 920 мм | 200 мм | 195 мм | 20 | 93 | Сталь_RAL9016 (INPLAST) | саморезы |
| STWS-925х225-SL | 0.125 м² | 925 мм | 920 мм | 225 мм | 220 мм | 23 | 93 | Сталь_RAL9016 (INPLAST) | саморезы |
| STWS-925х250-SL | 0.139 м² | 925 мм | 920 мм | 250 мм | 245 мм | 25 | 93 | Сталь_RAL9016 (INPLAST) | саморезы |
| STWS-925х300-SL | 0.167 м² | 925 мм | 920 мм | 300 мм | 295 мм | 30 | 93 | Сталь_RAL9016 (INPLAST) | саморезы |
| STWS-925х325-SL | 0.181 м² | 925 мм | 920 мм | 325 мм | 320 мм | 33 | 93 | Сталь_RAL9016 (INPLAST) | саморезы |
| STWS-925х350-SL | 0.195 м² | 925 мм | 920 мм | 350 мм | 345 мм | 35 | 93 | Сталь_RAL9016 (INPLAST) | саморезы |
| STWS-925х400-SL | 0.223 м² | 925 мм | 920 мм | 400 мм | 395 мм | 40 | 93 | Сталь_RAL9016 (INPLAST) | саморезы |
| STWS-925х425-SL | 0.237 м² | 925 мм | 920 мм | 425 мм | 420 мм | 43 | 93 | Сталь_RAL9016 (INPLAST) | саморезы |
| STWS-925х450-SL | 0.250 м² | 925 мм | 920 мм | 450 мм | 445 мм | 45 | 93 | Сталь_RAL9016 (INPLAST) | саморезы |
| STWS-925х500-SL | 0.278 м² | 925 мм | 920 мм | 500 мм | 495 мм | 50 | 93 | Сталь_RAL9016 (INPLAST) | саморезы |
| STWS-925х525-SL | 0.292 м² | 925 мм | 920 мм | 525 мм | 520 мм | 53 | 93 | Сталь_RAL9016 (INPLAST) | саморезы |
| STWS-925х550-SL | 0.306 м² | 925 мм | 920 мм | 550 мм | 545 мм | 55 | 93 | Сталь_RAL9016 (INPLAST) | саморезы |
| STWS-925х600-SL | 0.334 м² | 925 мм | 920 мм | 600 мм | 595 мм | 60 | 93 | Сталь_RAL9016 (INPLAST) | саморезы |
| STWS-925х625-SL | 0.348 м² | 925 мм | 920 мм | 625 мм | 620 мм | 63 | 93 | Сталь_RAL9016 (INPLAST) | саморезы |
| STWS-925х650-SL | 0.362 м² | 925 мм | 920 мм | 650 мм | 645 мм | 65 | 93 | Сталь_RAL9016 (INPLAST) | саморезы |
| STWS-950х100-SL | 0.057 м² | 950 мм | 945 мм | 100 мм | 95 мм | 10 | 95 | Сталь_RAL9016 (INPLAST) | саморезы |
| STWS-950х125-SL | 0.071 м² | 950 мм | 945 мм | 125 мм | 120 мм | 13 | 95 | Сталь_RAL9016 (INPLAST) | саморезы |
| STWS-950х150-SL | 0.086 м² | 950 мм | 945 мм | 150 мм | 145 мм | 15 | 95 | Сталь_RAL9016 (INPLAST) | саморезы |
| STWS-950х200-SL | 0.114 м² | 950 мм | 945 мм | 200 мм | 195 мм | 20 | 95 | Сталь_RAL9016 (INPLAST) | саморезы |
| STWS-950х225-SL | 0.129 м² | 950 мм | 945 мм | 225 мм | 220 мм | 23 | 95 | Сталь_RAL9016 (INPLAST) | саморезы |
| STWS-950х250-SL | 0.143 м² | 950 мм | 945 мм | 250 мм | 245 мм | 25 | 95 | Сталь_RAL9016 (INPLAST) | саморезы |
| STWS-950х300-SL | 0.171 м² | 950 мм | 945 мм | 300 мм | 295 мм | 30 | 95 | Сталь_RAL9016 (INPLAST) | саморезы |
| STWS-950х325-SL | 0.186 м² | 950 мм | 945 мм | 325 мм | 320 мм | 33 | 95 | Сталь_RAL9016 (INPLAST) | саморезы |
| STWS-950х350-SL | 0.200 м² | 950 мм | 945 мм | 350 мм | 345 мм | 35 | 95 | Сталь_RAL9016 (INPLAST) | саморезы |
| STWS-950х400-SL | 0.229 м² | 950 мм | 945 мм | 400 мм | 395 мм | 40 | 95 | Сталь_RAL9016 (INPLAST) | саморезы |
| STWS-950х425-SL | 0.243 м² | 950 мм | 945 мм | 425 мм | 420 мм | 43 | 95 | Сталь_RAL9016 (INPLAST) | саморезы |
| STWS-950х450-SL | 0.257 м² | 950 мм | 945 мм | 450 мм | 445 мм | 45 | 95 | Сталь_RAL9016 (INPLAST) | саморезы |
| STWS-950х500-SL | 0.286 м² | 950 мм | 945 мм | 500 мм | 495 мм | 50 | 95 | Сталь_RAL9016 (INPLAST) | саморезы |
| STWS-950х525-SL | 0.300 м² | 950 мм | 945 мм | 525 мм | 520 мм | 53 | 95 | Сталь_RAL9016 (INPLAST) | саморезы |
| STWS-950х550-SL | 0.314 м² | 950 мм | 945 мм | 550 мм | 545 мм | 55 | 95 | Сталь_RAL9016 (INPLAST) | саморезы |
| STWS-950х600-SL | 0.343 м² | 950 мм | 945 мм | 600 мм | 595 мм | 60 | 95 | Сталь_RAL9016 (INPLAST) | саморезы |
| STWS-950х625-SL | 0.357 м² | 950 мм | 945 мм | 625 мм | 620 мм | 63 | 95 | Сталь_RAL9016 (INPLAST) | саморезы |
| STWS-950х650-SL | 0.371 м² | 950 мм | 945 мм | 650 мм | 645 мм | 65 | 95 | Сталь_RAL9016 (INPLAST) | саморезы |
| STWS-1000х100-SL | 0.060 м² | 1000 мм | 995 мм | 100 мм | 95 мм | 10 | 100 | Сталь_RAL9016 (INPLAST) | саморезы |
| STWS-1000х125-SL | 0.075 м² | 1000 мм | 995 мм | 125 мм | 120 мм | 13 | 100 | Сталь_RAL9016 (INPLAST) | саморезы |
| STWS-1000х150-SL | 0.090 м² | 1000 мм | 995 мм | 150 мм | 145 мм | 15 | 100 | Сталь_RAL9016 (INPLAST) | саморезы |
| STWS-1000х200-SL | 0.120 м² | 1000 мм | 995 мм | 200 мм | 195 мм | 20 | 100 | Сталь_RAL9016 (INPLAST) | саморезы |
| STWS-1000х225-SL | 0.135 м² | 1000 мм | 995 мм | 225 мм | 220 мм | 23 | 100 | Сталь_RAL9016 (INPLAST) | саморезы |
| STWS-1000х250-SL | 0.150 м² | 1000 мм | 995 мм | 250 мм | 245 мм | 25 | 100 | Сталь_RAL9016 (INPLAST) | саморезы |
| STWS-1000х300-SL | 0.180 м² | 1000 мм | 995 мм | 300 мм | 295 мм | 30 | 100 | Сталь_RAL9016 (INPLAST) | саморезы |
| STWS-1000х325-SL | 0.196 м² | 1000 мм | 995 мм | 325 мм | 320 мм | 33 | 100 | Сталь_RAL9016 (INPLAST) | саморезы |
| STWS-1000х350-SL | 0.211 м² | 1000 мм | 995 мм | 350 мм | 345 мм | 35 | 100 | Сталь_RAL9016 (INPLAST) | саморезы |
| STWS-1000х400-SL | 0.241 м² | 1000 мм | 995 мм | 400 мм | 395 мм | 40 | 100 | Сталь_RAL9016 (INPLAST) | саморезы |
| STWS-1000х425-SL | 0.256 м² | 1000 мм | 995 мм | 425 мм | 420 мм | 43 | 100 | Сталь_RAL9016 (INPLAST) | саморезы |
| STWS-1000х450-SL | 0.271 м² | 1000 мм | 995 мм | 450 мм | 445 мм | 45 | 100 | Сталь_RAL9016 (INPLAST) | саморезы |
| STWS-1000х500-SL | 0.301 м² | 1000 мм | 995 мм | 500 мм | 495 мм | 50 | 100 | Сталь_RAL9016 (INPLAST) | саморезы |
| STWS-1000х525-SL | 0.316 м² | 1000 мм | 995 мм | 525 мм | 520 мм | 53 | 100 | Сталь_RAL9016 (INPLAST) | саморезы |
| STWS-1000х550-SL | 0.331 м² | 1000 мм | 995 мм | 550 мм | 545 мм | 55 | 100 | Сталь_RAL9016 (INPLAST) | саморезы |
| STWS-1000х600-SL | 0.361 м² | 1000 мм | 995 мм | 600 мм | 595 мм | 60 | 100 | Сталь_RAL9016 (INPLAST) | саморезы |
| STWS-1000х625-SL | 0.376 м² | 1000 мм | 995 мм | 625 мм | 620 мм | 63 | 100 | Сталь_RAL9016 (INPLAST) | саморезы |
| STWS-1000х650-SL | 0.391 м² | 1000 мм | 995 мм | 650 мм | 645 мм | 65 | 100 | Сталь_RAL9016 (INPLAST) | саморезы |
| STWS-1025х100-SL | 0.062 м² | 1025 мм | 1020 мм | 100 мм | 95 мм | 10 | 103 | Сталь_RAL9016 (INPLAST) | саморезы |
| STWS-1025х125-SL | 0.077 м² | 1025 мм | 1020 мм | 125 мм | 120 мм | 13 | 103 | Сталь_RAL9016 (INPLAST) | саморезы |
| STWS-1025х150-SL | 0.092 м² | 1025 мм | 1020 мм | 150 мм | 145 мм | 15 | 103 | Сталь_RAL9016 (INPLAST) | саморезы |
| STWS-1025х200-SL | 0.123 м² | 1025 мм | 1020 мм | 200 мм | 195 мм | 20 | 103 | Сталь_RAL9016 (INPLAST) | саморезы |
| STWS-1025х225-SL | 0.139 м² | 1025 мм | 1020 мм | 225 мм | 220 мм | 23 | 103 | Сталь_RAL9016 (INPLAST) | саморезы |
| STWS-1025х250-SL | 0.154 м² | 1025 мм | 1020 мм | 250 мм | 245 мм | 25 | 103 | Сталь_RAL9016 (INPLAST) | саморезы |
| STWS-1025х300-SL | 0.185 м² | 1025 мм | 1020 мм | 300 мм | 295 мм | 30 | 103 | Сталь_RAL9016 (INPLAST) | саморезы |
| STWS-1025х325-SL | 0.200 м² | 1025 мм | 1020 мм | 325 мм | 320 мм | 33 | 103 | Сталь_RAL9016 (INPLAST) | саморезы |
| STWS-1025х350-SL | 0.216 м² | 1025 мм | 1020 мм | 350 мм | 345 мм | 35 | 103 | Сталь_RAL9016 (INPLAST) | саморезы |
| STWS-1025х400-SL | 0.247 м² | 1025 мм | 1020 мм | 400 мм | 395 мм | 40 | 103 | Сталь_RAL9016 (INPLAST) | саморезы |
| STWS-1025х425-SL | 0.262 м² | 1025 мм | 1020 мм | 425 мм | 420 мм | 43 | 103 | Сталь_RAL9016 (INPLAST) | саморезы |
| STWS-1025х450-SL | 0.277 м² | 1025 мм | 1020 мм | 450 мм | 445 мм | 45 | 103 | Сталь_RAL9016 (INPLAST) | саморезы |
| STWS-1025х500-SL | 0.308 м² | 1025 мм | 1020 мм | 500 мм | 495 мм | 50 | 103 | Сталь_RAL9016 (INPLAST) | саморезы |
| STWS-1025х525-SL | 0.324 м² | 1025 мм | 1020 мм | 525 мм | 520 мм | 53 | 103 | Сталь_RAL9016 (INPLAST) | саморезы |
| STWS-1025х550-SL | 0.339 м² | 1025 мм | 1020 мм | 550 мм | 545 мм | 55 | 103 | Сталь_RAL9016 (INPLAST) | саморезы |
| STWS-1025х600-SL | 0.370 м² | 1025 мм | 1020 мм | 600 мм | 595 мм | 60 | 103 | Сталь_RAL9016 (INPLAST) | саморезы |
| STWS-1025х625-SL | 0.385 м² | 1025 мм | 1020 мм | 625 мм | 620 мм | 63 | 103 | Сталь_RAL9016 (INPLAST) | саморезы |
| STWS-1025х650-SL | 0.401 м² | 1025 мм | 1020 мм | 650 мм | 645 мм | 65 | 103 | Сталь_RAL9016 (INPLAST) | саморезы |
| STWS-1050х100-SL | 0.063 м² | 1050 мм | 1045 мм | 100 мм | 95 мм | 10 | 105 | Сталь_RAL9016 (INPLAST) | саморезы |
| STWS-1050х125-SL | 0.079 м² | 1050 мм | 1045 мм | 125 мм | 120 мм | 13 | 105 | Сталь_RAL9016 (INPLAST) | саморезы |
| STWS-1050х150-SL | 0.095 м² | 1050 мм | 1045 мм | 150 мм | 145 мм | 15 | 105 | Сталь_RAL9016 (INPLAST) | саморезы |
| STWS-1050х200-SL | 0.126 м² | 1050 мм | 1045 мм | 200 мм | 195 мм | 20 | 105 | Сталь_RAL9016 (INPLAST) | саморезы |
| STWS-1050х225-SL | 0.142 м² | 1050 мм | 1045 мм | 225 мм | 220 мм | 23 | 105 | Сталь_RAL9016 (INPLAST) | саморезы |
| STWS-1050х250-SL | 0.158 м² | 1050 мм | 1045 мм | 250 мм | 245 мм | 25 | 105 | Сталь_RAL9016 (INPLAST) | саморезы |
| STWS-1050х300-SL | 0.190 м² | 1050 мм | 1045 мм | 300 мм | 295 мм | 30 | 105 | Сталь_RAL9016 (INPLAST) | саморезы |
| STWS-1050х325-SL | 0.205 м² | 1050 мм | 1045 мм | 325 мм | 320 мм | 33 | 105 | Сталь_RAL9016 (INPLAST) | саморезы |
| STWS-1050х350-SL | 0.221 м² | 1050 мм | 1045 мм | 350 мм | 345 мм | 35 | 105 | Сталь_RAL9016 (INPLAST) | саморезы |
| STWS-1050х400-SL | 0.253 м² | 1050 мм | 1045 мм | 400 мм | 395 мм | 40 | 105 | Сталь_RAL9016 (INPLAST) | саморезы |
| STWS-1050х425-SL | 0.268 м² | 1050 мм | 1045 мм | 425 мм | 420 мм | 43 | 105 | Сталь_RAL9016 (INPLAST) | саморезы |
| STWS-1050х450-SL | 0.284 м² | 1050 мм | 1045 мм | 450 мм | 445 мм | 45 | 105 | Сталь_RAL9016 (INPLAST) | саморезы |
| STWS-1050х500-SL | 0.316 м² | 1050 мм | 1045 мм | 500 мм | 495 мм | 50 | 105 | Сталь_RAL9016 (INPLAST) | саморезы |
| STWS-1050х525-SL | 0.332 м² | 1050 мм | 1045 мм | 525 мм | 520 мм | 53 | 105 | Сталь_RAL9016 (INPLAST) | саморезы |
| STWS-1050х550-SL | 0.347 м² | 1050 мм | 1045 мм | 550 мм | 545 мм | 55 | 105 | Сталь_RAL9016 (INPLAST) | саморезы |
| STWS-1050х600-SL | 0.379 м² | 1050 мм | 1045 мм | 600 мм | 595 мм | 60 | 105 | Сталь_RAL9016 (INPLAST) | саморезы |
| STWS-1050х625-SL | 0.395 м² | 1050 мм | 1045 мм | 625 мм | 620 мм | 63 | 105 | Сталь_RAL9016 (INPLAST) | саморезы |
| STWS-1050х650-SL | 0.411 м² | 1050 мм | 1045 мм | 650 мм | 645 мм | 65 | 105 | Сталь_RAL9016 (INPLAST) | саморезы |
| STWS-1100х100-SL | 0.066 м² | 1100 мм | 1095 мм | 100 мм | 95 мм | 10 | 110 | Сталь_RAL9016 (INPLAST) | саморезы |
| STWS-1100х125-SL | 0.083 м² | 1100 мм | 1095 мм | 125 мм | 120 мм | 13 | 110 | Сталь_RAL9016 (INPLAST) | саморезы |
| STWS-1100х150-SL | 0.099 м² | 1100 мм | 1095 мм | 150 мм | 145 мм | 15 | 110 | Сталь_RAL9016 (INPLAST) | саморезы |
| STWS-1100х200-SL | 0.132 м² | 1100 мм | 1095 мм | 200 мм | 195 мм | 20 | 110 | Сталь_RAL9016 (INPLAST) | саморезы |
| STWS-1100х225-SL | 0.149 м² | 1100 мм | 1095 мм | 225 мм | 220 мм | 23 | 110 | Сталь_RAL9016 (INPLAST) | саморезы |
| STWS-1100х250-SL | 0.165 м² | 1100 мм | 1095 мм | 250 мм | 245 мм | 25 | 110 | Сталь_RAL9016 (INPLAST) | саморезы |
| STWS-1100х300-SL | 0.199 м² | 1100 мм | 1095 мм | 300 мм | 295 мм | 30 | 110 | Сталь_RAL9016 (INPLAST) | саморезы |
| STWS-1100х325-SL | 0.215 м² | 1100 мм | 1095 мм | 325 мм | 320 мм | 33 | 110 | Сталь_RAL9016 (INPLAST) | саморезы |
| STWS-1100х350-SL | 0.232 м² | 1100 мм | 1095 мм | 350 мм | 345 мм | 35 | 110 | Сталь_RAL9016 (INPLAST) | саморезы |
| STWS-1100х400-SL | 0.265 м² | 1100 мм | 1095 мм | 400 мм | 395 мм | 40 | 110 | Сталь_RAL9016 (INPLAST) | саморезы |
| STWS-1100х425-SL | 0.281 м² | 1100 мм | 1095 мм | 425 мм | 420 мм | 43 | 110 | Сталь_RAL9016 (INPLAST) | саморезы |
| STWS-1100х450-SL | 0.298 м² | 1100 мм | 1095 мм | 450 мм | 445 мм | 45 | 110 | Сталь_RAL9016 (INPLAST) | саморезы |
| STWS-1100х500-SL | 0.331 м² | 1100 мм | 1095 мм | 500 мм | 495 мм | 50 | 110 | Сталь_RAL9016 (INPLAST) | саморезы |
| STWS-1100х525-SL | 0.347 м² | 1100 мм | 1095 мм | 525 мм | 520 мм | 53 | 110 | Сталь_RAL9016 (INPLAST) | саморезы |
| STWS-1100х550-SL | 0.364 м² | 1100 мм | 1095 мм | 550 мм | 545 мм | 55 | 110 | Сталь_RAL9016 (INPLAST) | саморезы |
| STWS-1100х600-SL | 0.397 м² | 1100 мм | 1095 мм | 600 мм | 595 мм | 60 | 110 | Сталь_RAL9016 (INPLAST) | саморезы |
| STWS-1100х625-SL | 0.414 м² | 1100 мм | 1095 мм | 625 мм | 620 мм | 63 | 110 | Сталь_RAL9016 (INPLAST) | саморезы |
| STWS-1100х650-SL | 0.430 м² | 1100 мм | 1095 мм | 650 мм | 645 мм | 65 | 110 | Сталь_RAL9016 (INPLAST) | саморезы |
| STWS-1125х100-SL | 0.068 м² | 1125 мм | 1120 мм | 100 мм | 95 мм | 10 | 113 | Сталь_RAL9016 (INPLAST) | саморезы |
| STWS-1125х125-SL | 0.085 м² | 1125 мм | 1120 мм | 125 мм | 120 мм | 13 | 113 | Сталь_RAL9016 (INPLAST) | саморезы |
| STWS-1125х150-SL | 0.102 м² | 1125 мм | 1120 мм | 150 мм | 145 мм | 15 | 113 | Сталь_RAL9016 (INPLAST) | саморезы |
| STWS-1125х200-SL | 0.135 м² | 1125 мм | 1120 мм | 200 мм | 195 мм | 20 | 113 | Сталь_RAL9016 (INPLAST) | саморезы |
| STWS-1125х225-SL | 0.152 м² | 1125 мм | 1120 мм | 225 мм | 220 мм | 23 | 113 | Сталь_RAL9016 (INPLAST) | саморезы |
| STWS-1125х250-SL | 0.169 м² | 1125 мм | 1120 мм | 250 мм | 245 мм | 25 | 113 | Сталь_RAL9016 (INPLAST) | саморезы |
| STWS-1125х300-SL | 0.203 м² | 1125 мм | 1120 мм | 300 мм | 295 мм | 30 | 113 | Сталь_RAL9016 (INPLAST) | саморезы |
| STWS-1125х325-SL | 0.220 м² | 1125 мм | 1120 мм | 325 мм | 320 мм | 33 | 113 | Сталь_RAL9016 (INPLAST) | саморезы |
| STWS-1125х350-SL | 0.237 м² | 1125 мм | 1120 мм | 350 мм | 345 мм | 35 | 113 | Сталь_RAL9016 (INPLAST) | саморезы |
| STWS-1125х400-SL | 0.271 м² | 1125 мм | 1120 мм | 400 мм | 395 мм | 40 | 113 | Сталь_RAL9016 (INPLAST) | саморезы |
| STWS-1125х425-SL | 0.288 м² | 1125 мм | 1120 мм | 425 мм | 420 мм | 43 | 113 | Сталь_RAL9016 (INPLAST) | саморезы |
| STWS-1125х450-SL | 0.305 м² | 1125 мм | 1120 мм | 450 мм | 445 мм | 45 | 113 | Сталь_RAL9016 (INPLAST) | саморезы |
| STWS-1125х500-SL | 0.338 м² | 1125 мм | 1120 мм | 500 мм | 495 мм | 50 | 113 | Сталь_RAL9016 (INPLAST) | саморезы |
| STWS-1125х525-SL | 0.355 м² | 1125 мм | 1120 мм | 525 мм | 520 мм | 53 | 113 | Сталь_RAL9016 (INPLAST) | саморезы |
| STWS-1125х550-SL | 0.372 м² | 1125 мм | 1120 мм | 550 мм | 545 мм | 55 | 113 | Сталь_RAL9016 (INPLAST) | саморезы |
| STWS-1125х600-SL | 0.406 м² | 1125 мм | 1120 мм | 600 мм | 595 мм | 60 | 113 | Сталь_RAL9016 (INPLAST) | саморезы |
| STWS-1125х625-SL | 0.423 м² | 1125 мм | 1120 мм | 625 мм | 620 мм | 63 | 113 | Сталь_RAL9016 (INPLAST) | саморезы |
| STWS-1125х650-SL | 0.440 м² | 1125 мм | 1120 мм | 650 мм | 645 мм | 65 | 113 | Сталь_RAL9016 (INPLAST) | саморезы |
| STWS-1150х100-SL | 0.069 м² | 1150 мм | 1145 мм | 100 мм | 95 мм | 10 | 115 | Сталь_RAL9016 (INPLAST) | саморезы |
| STWS-1150х125-SL | 0.086 м² | 1150 мм | 1145 мм | 125 мм | 120 мм | 13 | 115 | Сталь_RAL9016 (INPLAST) | саморезы |
| STWS-1150х150-SL | 0.104 м² | 1150 мм | 1145 мм | 150 мм | 145 мм | 15 | 115 | Сталь_RAL9016 (INPLAST) | саморезы |
| STWS-1150х200-SL | 0.138 м² | 1150 мм | 1145 мм | 200 мм | 195 мм | 20 | 115 | Сталь_RAL9016 (INPLAST) | саморезы |
| STWS-1150х225-SL | 0.156 м² | 1150 мм | 1145 мм | 225 мм | 220 мм | 23 | 115 | Сталь_RAL9016 (INPLAST) | саморезы |
| STWS-1150х250-SL | 0.173 м² | 1150 мм | 1145 мм | 250 мм | 245 мм | 25 | 115 | Сталь_RAL9016 (INPLAST) | саморезы |
| STWS-1150х300-SL | 0.208 м² | 1150 мм | 1145 мм | 300 мм | 295 мм | 30 | 115 | Сталь_RAL9016 (INPLAST) | саморезы |
| STWS-1150х325-SL | 0.225 м² | 1150 мм | 1145 мм | 325 мм | 320 мм | 33 | 115 | Сталь_RAL9016 (INPLAST) | саморезы |
| STWS-1150х350-SL | 0.242 м² | 1150 мм | 1145 мм | 350 мм | 345 мм | 35 | 115 | Сталь_RAL9016 (INPLAST) | саморезы |
| STWS-1150х400-SL | 0.277 м² | 1150 мм | 1145 мм | 400 мм | 395 мм | 40 | 115 | Сталь_RAL9016 (INPLAST) | саморезы |
| STWS-1150х425-SL | 0.294 м² | 1150 мм | 1145 мм | 425 мм | 420 мм | 43 | 115 | Сталь_RAL9016 (INPLAST) | саморезы |
| STWS-1150х450-SL | 0.311 м² | 1150 мм | 1145 мм | 450 мм | 445 мм | 45 | 115 | Сталь_RAL9016 (INPLAST) | саморезы |
| STWS-1150х500-SL | 0.346 м² | 1150 мм | 1145 мм | 500 мм | 495 мм | 50 | 115 | Сталь_RAL9016 (INPLAST) | саморезы |
| STWS-1150х525-SL | 0.363 м² | 1150 мм | 1145 мм | 525 мм | 520 мм | 53 | 115 | Сталь_RAL9016 (INPLAST) | саморезы |
| STWS-1150х550-SL | 0.381 м² | 1150 мм | 1145 мм | 550 мм | 545 мм | 55 | 115 | Сталь_RAL9016 (INPLAST) | саморезы |
| STWS-1150х600-SL | 0.415 м² | 1150 мм | 1145 мм | 600 мм | 595 мм | 60 | 115 | Сталь_RAL9016 (INPLAST) | саморезы |
| STWS-1150х625-SL | 0.432 м² | 1150 мм | 1145 мм | 625 мм | 620 мм | 63 | 115 | Сталь_RAL9016 (INPLAST) | саморезы |
| STWS-1150х650-SL | 0.450 м² | 1150 мм | 1145 мм | 650 мм | 645 мм | 65 | 115 | Сталь_RAL9016 (INPLAST) | саморезы |
| STWS-1200х100-SL | 0.072 м² | 1200 мм | 1195 мм | 100 мм | 95 мм | 10 | 120 | Сталь_RAL9016 (INPLAST) | саморезы |
| STWS-1200х125-SL | 0.090 м² | 1200 мм | 1195 мм | 125 мм | 120 мм | 13 | 120 | Сталь_RAL9016 (INPLAST) | саморезы |
| STWS-1200х150-SL | 0.108 м² | 1200 мм | 1195 мм | 150 мм | 145 мм | 15 | 120 | Сталь_RAL9016 (INPLAST) | саморезы |
| STWS-1200х200-SL | 0.144 м² | 1200 мм | 1195 мм | 200 мм | 195 мм | 20 | 120 | Сталь_RAL9016 (INPLAST) | саморезы |
| STWS-1200х225-SL | 0.162 м² | 1200 мм | 1195 мм | 225 мм | 220 мм | 23 | 120 | Сталь_RAL9016 (INPLAST) | саморезы |
| STWS-1200х250-SL | 0.180 м² | 1200 мм | 1195 мм | 250 мм | 245 мм | 25 | 120 | Сталь_RAL9016 (INPLAST) | саморезы |
| STWS-1200х300-SL | 0.217 м² | 1200 мм | 1195 мм | 300 мм | 295 мм | 30 | 120 | Сталь_RAL9016 (INPLAST) | саморезы |
| STWS-1200х325-SL | 0.235 м² | 1200 мм | 1195 мм | 325 мм | 320 мм | 33 | 120 | Сталь_RAL9016 (INPLAST) | саморезы |
| STWS-1200х350-SL | 0.253 м² | 1200 мм | 1195 мм | 350 мм | 345 мм | 35 | 120 | Сталь_RAL9016 (INPLAST) | саморезы |
| STWS-1200х400-SL | 0.289 м² | 1200 мм | 1195 мм | 400 мм | 395 мм | 40 | 120 | Сталь_RAL9016 (INPLAST) | саморезы |
| STWS-1200х425-SL | 0.307 м² | 1200 мм | 1195 мм | 425 мм | 420 мм | 43 | 120 | Сталь_RAL9016 (INPLAST) | саморезы |
| STWS-1200х450-SL | 0.325 м² | 1200 мм | 1195 мм | 450 мм | 445 мм | 45 | 120 | Сталь_RAL9016 (INPLAST) | саморезы |
| STWS-1200х500-SL | 0.361 м² | 1200 мм | 1195 мм | 500 мм | 495 мм | 50 | 120 | Сталь_RAL9016 (INPLAST) | саморезы |
| STWS-1200х525-SL | 0.379 м² | 1200 мм | 1195 мм | 525 мм | 520 мм | 53 | 120 | Сталь_RAL9016 (INPLAST) | саморезы |
| STWS-1200х550-SL | 0.397 м² | 1200 мм | 1195 мм | 550 мм | 545 мм | 55 | 120 | Сталь_RAL9016 (INPLAST) | саморезы |
| STWS-1200х600-SL | 0.433 м² | 1200 мм | 1195 мм | 600 мм | 595 мм | 60 | 120 | Сталь_RAL9016 (INPLAST) | саморезы |
| STWS-1200х625-SL | 0.451 м² | 1200 мм | 1195 мм | 625 мм | 620 мм | 63 | 120 | Сталь_RAL9016 (INPLAST) | саморезы |
| STWS-1200х650-SL | 0.469 м² | 1200 мм | 1195 мм | 650 мм | 645 мм | 65 | 120 | Сталь_RAL9016 (INPLAST) | саморезы |
| STWS-1225х100-SL | 0.074 м² | 1225 мм | 1220 мм | 100 мм | 95 мм | 10 | 123 | Сталь_RAL9016 (INPLAST) | саморезы |
| STWS-1225х125-SL | 0.092 м² | 1225 мм | 1220 мм | 125 мм | 120 мм | 13 | 123 | Сталь_RAL9016 (INPLAST) | саморезы |
| STWS-1225х150-SL | 0.111 м² | 1225 мм | 1220 мм | 150 мм | 145 мм | 15 | 123 | Сталь_RAL9016 (INPLAST) | саморезы |
| STWS-1225х200-SL | 0.147 м² | 1225 мм | 1220 мм | 200 мм | 195 мм | 20 | 123 | Сталь_RAL9016 (INPLAST) | саморезы |
| STWS-1225х225-SL | 0.166 м² | 1225 мм | 1220 мм | 225 мм | 220 мм | 23 | 123 | Сталь_RAL9016 (INPLAST) | саморезы |
| STWS-1225х250-SL | 0.184 м² | 1225 мм | 1220 мм | 250 мм | 245 мм | 25 | 123 | Сталь_RAL9016 (INPLAST) | саморезы |
| STWS-1225х300-SL | 0.221 м² | 1225 мм | 1220 мм | 300 мм | 295 мм | 30 | 123 | Сталь_RAL9016 (INPLAST) | саморезы |
| STWS-1225х325-SL | 0.240 м² | 1225 мм | 1220 мм | 325 мм | 320 мм | 33 | 123 | Сталь_RAL9016 (INPLAST) | саморезы |
| STWS-1225х350-SL | 0.258 м² | 1225 мм | 1220 мм | 350 мм | 345 мм | 35 | 123 | Сталь_RAL9016 (INPLAST) | саморезы |
| STWS-1225х400-SL | 0.295 м² | 1225 мм | 1220 мм | 400 мм | 395 мм | 40 | 123 | Сталь_RAL9016 (INPLAST) | саморезы |
| STWS-1225х425-SL | 0.313 м² | 1225 мм | 1220 мм | 425 мм | 420 мм | 43 | 123 | Сталь_RAL9016 (INPLAST) | саморезы |
| STWS-1225х450-SL | 0.332 м² | 1225 мм | 1220 мм | 450 мм | 445 мм | 45 | 123 | Сталь_RAL9016 (INPLAST) | саморезы |
| STWS-1225х500-SL | 0.368 м² | 1225 мм | 1220 мм | 500 мм | 495 мм | 50 | 123 | Сталь_RAL9016 (INPLAST) | саморезы |
| STWS-1225х525-SL | 0.387 м² | 1225 мм | 1220 мм | 525 мм | 520 мм | 53 | 123 | Сталь_RAL9016 (INPLAST) | саморезы |
| STWS-1225х550-SL | 0.405 м² | 1225 мм | 1220 мм | 550 мм | 545 мм | 55 | 123 | Сталь_RAL9016 (INPLAST) | саморезы |
| STWS-1225х600-SL | 0.442 м² | 1225 мм | 1220 мм | 600 мм | 595 мм | 60 | 123 | Сталь_RAL9016 (INPLAST) | саморезы |
| STWS-1225х625-SL | 0.461 м² | 1225 мм | 1220 мм | 625 мм | 620 мм | 63 | 123 | Сталь_RAL9016 (INPLAST) | саморезы |
| STWS-1225х650-SL | 0.479 м² | 1225 мм | 1220 мм | 650 мм | 645 мм | 65 | 123 | Сталь_RAL9016 (INPLAST) | саморезы |
| STWS-1250х100-SL | 0.075 м² | 1250 мм | 1245 мм | 100 мм | 95 мм | 10 | 125 | Сталь_RAL9016 (INPLAST) | саморезы |
| STWS-1250х125-SL | 0.094 м² | 1250 мм | 1245 мм | 125 мм | 120 мм | 13 | 125 | Сталь_RAL9016 (INPLAST) | саморезы |
| STWS-1250х150-SL | 0.113 м² | 1250 мм | 1245 мм | 150 мм | 145 мм | 15 | 125 | Сталь_RAL9016 (INPLAST) | саморезы |
| STWS-1250х200-SL | 0.150 м² | 1250 мм | 1245 мм | 200 мм | 195 мм | 20 | 125 | Сталь_RAL9016 (INPLAST) | саморезы |
| STWS-1250х225-SL | 0.169 м² | 1250 мм | 1245 мм | 225 мм | 220 мм | 23 | 125 | Сталь_RAL9016 (INPLAST) | саморезы |
| STWS-1250х250-SL | 0.188 м² | 1250 мм | 1245 мм | 250 мм | 245 мм | 25 | 125 | Сталь_RAL9016 (INPLAST) | саморезы |
| STWS-1250х300-SL | 0.226 м² | 1250 мм | 1245 мм | 300 мм | 295 мм | 30 | 125 | Сталь_RAL9016 (INPLAST) | саморезы |
| STWS-1250х325-SL | 0.244 м² | 1250 мм | 1245 мм | 325 мм | 320 мм | 33 | 125 | Сталь_RAL9016 (INPLAST) | саморезы |
| STWS-1250х350-SL | 0.263 м² | 1250 мм | 1245 мм | 350 мм | 345 мм | 35 | 125 | Сталь_RAL9016 (INPLAST) | саморезы |
| STWS-1250х400-SL | 0.301 м² | 1250 мм | 1245 мм | 400 мм | 395 мм | 40 | 125 | Сталь_RAL9016 (INPLAST) | саморезы |
| STWS-1250х425-SL | 0.320 м² | 1250 мм | 1245 мм | 425 мм | 420 мм | 43 | 125 | Сталь_RAL9016 (INPLAST) | саморезы |
| STWS-1250х450-SL | 0.338 м² | 1250 мм | 1245 мм | 450 мм | 445 мм | 45 | 125 | Сталь_RAL9016 (INPLAST) | саморезы |
| STWS-1250х500-SL | 0.376 м² | 1250 мм | 1245 мм | 500 мм | 495 мм | 50 | 125 | Сталь_RAL9016 (INPLAST) | саморезы |
| STWS-1250х525-SL | 0.395 м² | 1250 мм | 1245 мм | 525 мм | 520 мм | 53 | 125 | Сталь_RAL9016 (INPLAST) | саморезы |
| STWS-1250х550-SL | 0.414 м² | 1250 мм | 1245 мм | 550 мм | 545 мм | 55 | 125 | Сталь_RAL9016 (INPLAST) | саморезы |
| STWS-1250х600-SL | 0.451 м² | 1250 мм | 1245 мм | 600 мм | 595 мм | 60 | 125 | Сталь_RAL9016 (INPLAST) | саморезы |
| STWS-1250х625-SL | 0.470 м² | 1250 мм | 1245 мм | 625 мм | 620 мм | 63 | 125 | Сталь_RAL9016 (INPLAST) | саморезы |
| STWS-1250х650-SL | 0.489 м² | 1250 мм | 1245 мм | 650 мм | 645 мм | 65 | 125 | Сталь_RAL9016 (INPLAST) | саморезы |
| STWS-1300х100-SL | 0.078 м² | 1300 мм | 1295 мм | 100 мм | 95 мм | 10 | 130 | Сталь_RAL9016 (INPLAST) | саморезы |
| STWS-1300х125-SL | 0.098 м² | 1300 мм | 1295 мм | 125 мм | 120 мм | 13 | 130 | Сталь_RAL9016 (INPLAST) | саморезы |
| STWS-1300х150-SL | 0.117 м² | 1300 мм | 1295 мм | 150 мм | 145 мм | 15 | 130 | Сталь_RAL9016 (INPLAST) | саморезы |
| STWS-1300х200-SL | 0.156 м² | 1300 мм | 1295 мм | 200 мм | 195 мм | 20 | 130 | Сталь_RAL9016 (INPLAST) | саморезы |
| STWS-1300х225-SL | 0.176 м² | 1300 мм | 1295 мм | 225 мм | 220 мм | 23 | 130 | Сталь_RAL9016 (INPLAST) | саморезы |
| STWS-1300х250-SL | 0.196 м² | 1300 мм | 1295 мм | 250 мм | 245 мм | 25 | 130 | Сталь_RAL9016 (INPLAST) | саморезы |
| STWS-1300х300-SL | 0.235 м² | 1300 мм | 1295 мм | 300 мм | 295 мм | 30 | 130 | Сталь_RAL9016 (INPLAST) | саморезы |
| STWS-1300х325-SL | 0.254 м² | 1300 мм | 1295 мм | 325 мм | 320 мм | 33 | 130 | Сталь_RAL9016 (INPLAST) | саморезы |
| STWS-1300х350-SL | 0.274 м² | 1300 мм | 1295 мм | 350 мм | 345 мм | 35 | 130 | Сталь_RAL9016 (INPLAST) | саморезы |
| STWS-1300х400-SL | 0.313 м² | 1300 мм | 1295 мм | 400 мм | 395 мм | 40 | 130 | Сталь_RAL9016 (INPLAST) | саморезы |
| STWS-1300х425-SL | 0.332 м² | 1300 мм | 1295 мм | 425 мм | 420 мм | 43 | 130 | Сталь_RAL9016 (INPLAST) | саморезы |
| STWS-1300х450-SL | 0.352 м² | 1300 мм | 1295 мм | 450 мм | 445 мм | 45 | 130 | Сталь_RAL9016 (INPLAST) | саморезы |
| STWS-1300х500-SL | 0.391 м² | 1300 мм | 1295 мм | 500 мм | 495 мм | 50 | 130 | Сталь_RAL9016 (INPLAST) | саморезы |
| STWS-1300х525-SL | 0.411 м² | 1300 мм | 1295 мм | 525 мм | 520 мм | 53 | 130 | Сталь_RAL9016 (INPLAST) | саморезы |
| STWS-1300х550-SL | 0.430 м² | 1300 мм | 1295 мм | 550 мм | 545 мм | 55 | 130 | Сталь_RAL9016 (INPLAST) | саморезы |
| STWS-1300х600-SL | 0.469 м² | 1300 мм | 1295 мм | 600 мм | 595 мм | 60 | 130 | Сталь_RAL9016 (INPLAST) | саморезы |
| STWS-1300х625-SL | 0.489 м² | 1300 мм | 1295 мм | 625 мм | 620 мм | 63 | 130 | Сталь_RAL9016 (INPLAST) | саморезы |
| STWS-1300х650-SL | 0.508 м² | 1300 мм | 1295 мм | 650 мм | 645 мм | 65 | 130 | Сталь_RAL9016 (INPLAST) | саморезы |
| STWS-1325х100-SL | 0.080 м² | 1325 мм | 1320 мм | 100 мм | 95 мм | 10 | 133 | Сталь_RAL9016 (INPLAST) | саморезы |
| STWS-1325х125-SL | 0.100 м² | 1325 мм | 1320 мм | 125 мм | 120 мм | 13 | 133 | Сталь_RAL9016 (INPLAST) | саморезы |
| STWS-1325х150-SL | 0.120 м² | 1325 мм | 1320 мм | 150 мм | 145 мм | 15 | 133 | Сталь_RAL9016 (INPLAST) | саморезы |
| STWS-1325х200-SL | 0.159 м² | 1325 мм | 1320 мм | 200 мм | 195 мм | 20 | 133 | Сталь_RAL9016 (INPLAST) | саморезы |
| STWS-1325х225-SL | 0.179 м² | 1325 мм | 1320 мм | 225 мм | 220 мм | 23 | 133 | Сталь_RAL9016 (INPLAST) | саморезы |
| STWS-1325х250-SL | 0.199 м² | 1325 мм | 1320 мм | 250 мм | 245 мм | 25 | 133 | Сталь_RAL9016 (INPLAST) | саморезы |
| STWS-1325х300-SL | 0.239 м² | 1325 мм | 1320 мм | 300 мм | 295 мм | 30 | 133 | Сталь_RAL9016 (INPLAST) | саморезы |
| STWS-1325х325-SL | 0.259 м² | 1325 мм | 1320 мм | 325 мм | 320 мм | 33 | 133 | Сталь_RAL9016 (INPLAST) | саморезы |
| STWS-1325х350-SL | 0.279 м² | 1325 мм | 1320 мм | 350 мм | 345 мм | 35 | 133 | Сталь_RAL9016 (INPLAST) | саморезы |
| STWS-1325х400-SL | 0.319 м² | 1325 мм | 1320 мм | 400 мм | 395 мм | 40 | 133 | Сталь_RAL9016 (INPLAST) | саморезы |
| STWS-1325х425-SL | 0.339 м² | 1325 мм | 1320 мм | 425 мм | 420 мм | 43 | 133 | Сталь_RAL9016 (INPLAST) | саморезы |
| STWS-1325х450-SL | 0.359 м² | 1325 мм | 1320 мм | 450 мм | 445 мм | 45 | 133 | Сталь_RAL9016 (INPLAST) | саморезы |
| STWS-1325х500-SL | 0.399 м² | 1325 мм | 1320 мм | 500 мм | 495 мм | 50 | 133 | Сталь_RAL9016 (INPLAST) | саморезы |
| STWS-1325х525-SL | 0.418 м² | 1325 мм | 1320 мм | 525 мм | 520 мм | 53 | 133 | Сталь_RAL9016 (INPLAST) | саморезы |
| STWS-1325х550-SL | 0.438 м² | 1325 мм | 1320 мм | 550 мм | 545 мм | 55 | 133 | Сталь_RAL9016 (INPLAST) | саморезы |
| STWS-1325х600-SL | 0.478 м² | 1325 мм | 1320 мм | 600 мм | 595 мм | 60 | 133 | Сталь_RAL9016 (INPLAST) | саморезы |
| STWS-1325х625-SL | 0.498 м² | 1325 мм | 1320 мм | 625 мм | 620 мм | 63 | 133 | Сталь_RAL9016 (INPLAST) | саморезы |
| STWS-1325х650-SL | 0.518 м² | 1325 мм | 1320 мм | 650 мм | 645 мм | 65 | 133 | Сталь_RAL9016 (INPLAST) | саморезы |
| STWS-1350х100-SL | 0.081 м² | 1350 мм | 1345 мм | 100 мм | 95 мм | 10 | 135 | Сталь_RAL9016 (INPLAST) | саморезы |
| STWS-1350х125-SL | 0.102 м² | 1350 мм | 1345 мм | 125 мм | 120 мм | 13 | 135 | Сталь_RAL9016 (INPLAST) | саморезы |
| STWS-1350х150-SL | 0.122 м² | 1350 мм | 1345 мм | 150 мм | 145 мм | 15 | 135 | Сталь_RAL9016 (INPLAST) | саморезы |
| STWS-1350х200-SL | 0.162 м² | 1350 мм | 1345 мм | 200 мм | 195 мм | 20 | 135 | Сталь_RAL9016 (INPLAST) | саморезы |
| STWS-1350х225-SL | 0.183 м² | 1350 мм | 1345 мм | 225 мм | 220 мм | 23 | 135 | Сталь_RAL9016 (INPLAST) | саморезы |
| STWS-1350х250-SL | 0.203 м² | 1350 мм | 1345 мм | 250 мм | 245 мм | 25 | 135 | Сталь_RAL9016 (INPLAST) | саморезы |
| STWS-1350х300-SL | 0.244 м² | 1350 мм | 1345 мм | 300 мм | 295 мм | 30 | 135 | Сталь_RAL9016 (INPLAST) | саморезы |
| STWS-1350х325-SL | 0.264 м² | 1350 мм | 1345 мм | 325 мм | 320 мм | 33 | 135 | Сталь_RAL9016 (INPLAST) | саморезы |
| STWS-1350х350-SL | 0.284 м² | 1350 мм | 1345 мм | 350 мм | 345 мм | 35 | 135 | Сталь_RAL9016 (INPLAST) | саморезы |
| STWS-1350х400-SL | 0.325 м² | 1350 мм | 1345 мм | 400 мм | 395 мм | 40 | 135 | Сталь_RAL9016 (INPLAST) | саморезы |
| STWS-1350х425-SL | 0.345 м² | 1350 мм | 1345 мм | 425 мм | 420 мм | 43 | 135 | Сталь_RAL9016 (INPLAST) | саморезы |
| STWS-1350х450-SL | 0.365 м² | 1350 мм | 1345 мм | 450 мм | 445 мм | 45 | 135 | Сталь_RAL9016 (INPLAST) | саморезы |
| STWS-1350х500-SL | 0.406 м² | 1350 мм | 1345 мм | 500 мм | 495 мм | 50 | 135 | Сталь_RAL9016 (INPLAST) | саморезы |
| STWS-1350х525-SL | 0.426 м² | 1350 мм | 1345 мм | 525 мм | 520 мм | 53 | 135 | Сталь_RAL9016 (INPLAST) | саморезы |
| STWS-1350х550-SL | 0.447 м² | 1350 мм | 1345 мм | 550 мм | 545 мм | 55 | 135 | Сталь_RAL9016 (INPLAST) | саморезы |
| STWS-1350х600-SL | 0.487 м² | 1350 мм | 1345 мм | 600 мм | 595 мм | 60 | 135 | Сталь_RAL9016 (INPLAST) | саморезы |
| STWS-1350х625-SL | 0.508 м² | 1350 мм | 1345 мм | 625 мм | 620 мм | 63 | 135 | Сталь_RAL9016 (INPLAST) | саморезы |
| STWS-1350х650-SL | 0.528 м² | 1350 мм | 1345 мм | 650 мм | 645 мм | 65 | 135 | Сталь_RAL9016 (INPLAST) | саморезы |
| STWS-1400х100-SL | 0.084 м² | 1400 мм | 1395 мм | 100 мм | 95 мм | 10 | 140 | Сталь_RAL9016 (INPLAST) | саморезы |
| STWS-1400х125-SL | 0.105 м² | 1400 мм | 1395 мм | 125 мм | 120 мм | 13 | 140 | Сталь_RAL9016 (INPLAST) | саморезы |
| STWS-1400х150-SL | 0.126 м² | 1400 мм | 1395 мм | 150 мм | 145 мм | 15 | 140 | Сталь_RAL9016 (INPLAST) | саморезы |
| STWS-1400х200-SL | 0.168 м² | 1400 мм | 1395 мм | 200 мм | 195 мм | 20 | 140 | Сталь_RAL9016 (INPLAST) | саморезы |
| STWS-1400х225-SL | 0.190 м² | 1400 мм | 1395 мм | 225 мм | 220 мм | 23 | 140 | Сталь_RAL9016 (INPLAST) | саморезы |
| STWS-1400х250-SL | 0.211 м² | 1400 мм | 1395 мм | 250 мм | 245 мм | 25 | 140 | Сталь_RAL9016 (INPLAST) | саморезы |
| STWS-1400х300-SL | 0.253 м² | 1400 мм | 1395 мм | 300 мм | 295 мм | 30 | 140 | Сталь_RAL9016 (INPLAST) | саморезы |
| STWS-1400х325-SL | 0.274 м² | 1400 мм | 1395 мм | 325 мм | 320 мм | 33 | 140 | Сталь_RAL9016 (INPLAST) | саморезы |
| STWS-1400х350-SL | 0.295 м² | 1400 мм | 1395 мм | 350 мм | 345 мм | 35 | 140 | Сталь_RAL9016 (INPLAST) | саморезы |
| STWS-1400х400-SL | 0.337 м² | 1400 мм | 1395 мм | 400 мм | 395 мм | 40 | 140 | Сталь_RAL9016 (INPLAST) | саморезы |
| STWS-1400х425-SL | 0.358 м² | 1400 мм | 1395 мм | 425 мм | 420 мм | 43 | 140 | Сталь_RAL9016 (INPLAST) | саморезы |
| STWS-1400х450-SL | 0.379 м² | 1400 мм | 1395 мм | 450 мм | 445 мм | 45 | 140 | Сталь_RAL9016 (INPLAST) | саморезы |
| STWS-1400х500-SL | 0.421 м² | 1400 мм | 1395 мм | 500 мм | 495 мм | 50 | 140 | Сталь_RAL9016 (INPLAST) | саморезы |
| STWS-1400х525-SL | 0.442 м² | 1400 мм | 1395 мм | 525 мм | 520 мм | 53 | 140 | Сталь_RAL9016 (INPLAST) | саморезы |
| STWS-1400х550-SL | 0.463 м² | 1400 мм | 1395 мм | 550 мм | 545 мм | 55 | 140 | Сталь_RAL9016 (INPLAST) | саморезы |
| STWS-1400х600-SL | 0.505 м² | 1400 мм | 1395 мм | 600 мм | 595 мм | 60 | 140 | Сталь_RAL9016 (INPLAST) | саморезы |
| STWS-1400х625-SL | 0.526 м² | 1400 мм | 1395 мм | 625 мм | 620 мм | 63 | 140 | Сталь_RAL9016 (INPLAST) | саморезы |
| STWS-1400х650-SL | 0.547 м² | 1400 мм | 1395 мм | 650 мм | 645 мм | 65 | 140 | Сталь_RAL9016 (INPLAST) | саморезы |
| STWS-1425х100-SL | 0.086 м² | 1425 мм | 1420 мм | 100 мм | 95 мм | 10 | 143 | Сталь_RAL9016 (INPLAST) | саморезы |
| STWS-1425х125-SL | 0.107 м² | 1425 мм | 1420 мм | 125 мм | 120 мм | 13 | 143 | Сталь_RAL9016 (INPLAST) | саморезы |
| STWS-1425х150-SL | 0.129 м² | 1425 мм | 1420 мм | 150 мм | 145 мм | 15 | 143 | Сталь_RAL9016 (INPLAST) | саморезы |
| STWS-1425х200-SL | 0.171 м² | 1425 мм | 1420 мм | 200 мм | 195 мм | 20 | 143 | Сталь_RAL9016 (INPLAST) | саморезы |
| STWS-1425х225-SL | 0.193 м² | 1425 мм | 1420 мм | 225 мм | 220 мм | 23 | 143 | Сталь_RAL9016 (INPLAST) | саморезы |
| STWS-1425х250-SL | 0.214 м² | 1425 мм | 1420 мм | 250 мм | 245 мм | 25 | 143 | Сталь_RAL9016 (INPLAST) | саморезы |
| STWS-1425х300-SL | 0.257 м² | 1425 мм | 1420 мм | 300 мм | 295 мм | 30 | 143 | Сталь_RAL9016 (INPLAST) | саморезы |
| STWS-1425х325-SL | 0.279 м² | 1425 мм | 1420 мм | 325 мм | 320 мм | 33 | 143 | Сталь_RAL9016 (INPLAST) | саморезы |
| STWS-1425х350-SL | 0.300 м² | 1425 мм | 1420 мм | 350 мм | 345 мм | 35 | 143 | Сталь_RAL9016 (INPLAST) | саморезы |
| STWS-1425х400-SL | 0.343 м² | 1425 мм | 1420 мм | 400 мм | 395 мм | 40 | 143 | Сталь_RAL9016 (INPLAST) | саморезы |
| STWS-1425х425-SL | 0.364 м² | 1425 мм | 1420 мм | 425 мм | 420 мм | 43 | 143 | Сталь_RAL9016 (INPLAST) | саморезы |
| STWS-1425х450-SL | 0.386 м² | 1425 мм | 1420 мм | 450 мм | 445 мм | 45 | 143 | Сталь_RAL9016 (INPLAST) | саморезы |
| STWS-1425х500-SL | 0.429 м² | 1425 мм | 1420 мм | 500 мм | 495 мм | 50 | 143 | Сталь_RAL9016 (INPLAST) | саморезы |
| STWS-1425х525-SL | 0.450 м² | 1425 мм | 1420 мм | 525 мм | 520 мм | 53 | 143 | Сталь_RAL9016 (INPLAST) | саморезы |
| STWS-1425х550-SL | 0.472 м² | 1425 мм | 1420 мм | 550 мм | 545 мм | 55 | 143 | Сталь_RAL9016 (INPLAST) | саморезы |
| STWS-1425х600-SL | 0.514 м² | 1425 мм | 1420 мм | 600 мм | 595 мм | 60 | 143 | Сталь_RAL9016 (INPLAST) | саморезы |
| STWS-1425х625-SL | 0.536 м² | 1425 мм | 1420 мм | 625 мм | 620 мм | 63 | 143 | Сталь_RAL9016 (INPLAST) | саморезы |
| STWS-1425х650-SL | 0.557 м² | 1425 мм | 1420 мм | 650 мм | 645 мм | 65 | 143 | Сталь_RAL9016 (INPLAST) | саморезы |
| STWS-1450х100-SL | 0.087 м² | 1450 мм | 1445 мм | 100 мм | 95 мм | 10 | 145 | Сталь_RAL9016 (INPLAST) | саморезы |
| STWS-1450х125-SL | 0.109 м² | 1450 мм | 1445 мм | 125 мм | 120 мм | 13 | 145 | Сталь_RAL9016 (INPLAST) | саморезы |
| STWS-1450х150-SL | 0.131 м² | 1450 мм | 1445 мм | 150 мм | 145 мм | 15 | 145 | Сталь_RAL9016 (INPLAST) | саморезы |
| STWS-1450х200-SL | 0.174 м² | 1450 мм | 1445 мм | 200 мм | 195 мм | 20 | 145 | Сталь_RAL9016 (INPLAST) | саморезы |
| STWS-1450х225-SL | 0.196 м² | 1450 мм | 1445 мм | 225 мм | 220 мм | 23 | 145 | Сталь_RAL9016 (INPLAST) | саморезы |
| STWS-1450х250-SL | 0.218 м² | 1450 мм | 1445 мм | 250 мм | 245 мм | 25 | 145 | Сталь_RAL9016 (INPLAST) | саморезы |
| STWS-1450х300-SL | 0.262 м² | 1450 мм | 1445 мм | 300 мм | 295 мм | 30 | 145 | Сталь_RAL9016 (INPLAST) | саморезы |
| STWS-1450х325-SL | 0.284 м² | 1450 мм | 1445 мм | 325 мм | 320 мм | 33 | 145 | Сталь_RAL9016 (INPLAST) | саморезы |
| STWS-1450х350-SL | 0.305 м² | 1450 мм | 1445 мм | 350 мм | 345 мм | 35 | 145 | Сталь_RAL9016 (INPLAST) | саморезы |
| STWS-1450х400-SL | 0.349 м² | 1450 мм | 1445 мм | 400 мм | 395 мм | 40 | 145 | Сталь_RAL9016 (INPLAST) | саморезы |
| STWS-1450х425-SL | 0.371 м² | 1450 мм | 1445 мм | 425 мм | 420 мм | 43 | 145 | Сталь_RAL9016 (INPLAST) | саморезы |
| STWS-1450х450-SL | 0.393 м² | 1450 мм | 1445 мм | 450 мм | 445 мм | 45 | 145 | Сталь_RAL9016 (INPLAST) | саморезы |
| STWS-1450х500-SL | 0.436 м² | 1450 мм | 1445 мм | 500 мм | 495 мм | 50 | 145 | Сталь_RAL9016 (INPLAST) | саморезы |
| STWS-1450х525-SL | 0.458 м² | 1450 мм | 1445 мм | 525 мм | 520 мм | 53 | 145 | Сталь_RAL9016 (INPLAST) | саморезы |
| STWS-1450х550-SL | 0.480 м² | 1450 мм | 1445 мм | 550 мм | 545 мм | 55 | 145 | Сталь_RAL9016 (INPLAST) | саморезы |
| STWS-1450х600-SL | 0.523 м² | 1450 мм | 1445 мм | 600 мм | 595 мм | 60 | 145 | Сталь_RAL9016 (INPLAST) | саморезы |
| STWS-1450х625-SL | 0.545 м² | 1450 мм | 1445 мм | 625 мм | 620 мм | 63 | 145 | Сталь_RAL9016 (INPLAST) | саморезы |
| STWS-1450х650-SL | 0.567 м² | 1450 мм | 1445 мм | 650 мм | 645 мм | 65 | 145 | Сталь_RAL9016 (INPLAST) | саморезы |
| STWS-1500х100-SL | 0.090 м² | 1500 мм | 1495 мм | 100 мм | 95 мм | 10 | 150 | Сталь_RAL9016 (INPLAST) | саморезы |
| STWS-1500х125-SL | 0.113 м² | 1500 мм | 1495 мм | 125 мм | 120 мм | 13 | 150 | Сталь_RAL9016 (INPLAST) | саморезы |
| STWS-1500х150-SL | 0.135 м² | 1500 мм | 1495 мм | 150 мм | 145 мм | 15 | 150 | Сталь_RAL9016 (INPLAST) | саморезы |
| STWS-1500х200-SL | 0.180 м² | 1500 мм | 1495 мм | 200 мм | 195 мм | 20 | 150 | Сталь_RAL9016 (INPLAST) | саморезы |
| STWS-1500х225-SL | 0.203 м² | 1500 мм | 1495 мм | 225 мм | 220 мм | 23 | 150 | Сталь_RAL9016 (INPLAST) | саморезы |
| STWS-1500х250-SL | 0.226 м² | 1500 мм | 1495 мм | 250 мм | 245 мм | 25 | 150 | Сталь_RAL9016 (INPLAST) | саморезы |
| STWS-1500х300-SL | 0.271 м² | 1500 мм | 1495 мм | 300 мм | 295 мм | 30 | 150 | Сталь_RAL9016 (INPLAST) | саморезы |
| STWS-1500х325-SL | 0.293 м² | 1500 мм | 1495 мм | 325 мм | 320 мм | 33 | 150 | Сталь_RAL9016 (INPLAST) | саморезы |
| STWS-1500х350-SL | 0.316 м² | 1500 мм | 1495 мм | 350 мм | 345 мм | 35 | 150 | Сталь_RAL9016 (INPLAST) | саморезы |
| STWS-1500х400-SL | 0.361 м² | 1500 мм | 1495 мм | 400 мм | 395 мм | 40 | 150 | Сталь_RAL9016 (INPLAST) | саморезы |
| STWS-1500х425-SL | 0.384 м² | 1500 мм | 1495 мм | 425 мм | 420 мм | 43 | 150 | Сталь_RAL9016 (INPLAST) | саморезы |
| STWS-1500х450-SL | 0.406 м² | 1500 мм | 1495 мм | 450 мм | 445 мм | 45 | 150 | Сталь_RAL9016 (INPLAST) | саморезы |
| STWS-1500х500-SL | 0.451 м² | 1500 мм | 1495 мм | 500 мм | 495 мм | 50 | 150 | Сталь_RAL9016 (INPLAST) | саморезы |
| STWS-1500х525-SL | 0.474 м² | 1500 мм | 1495 мм | 525 мм | 520 мм | 53 | 150 | Сталь_RAL9016 (INPLAST) | саморезы |
| STWS-1500х550-SL | 0.496 м² | 1500 мм | 1495 мм | 550 мм | 545 мм | 55 | 150 | Сталь_RAL9016 (INPLAST) | саморезы |
| STWS-1500х600-SL | 0.541 м² | 1500 мм | 1495 мм | 600 мм | 595 мм | 60 | 150 | Сталь_RAL9016 (INPLAST) | саморезы |
| STWS-1500х625-SL | 0.564 м² | 1500 мм | 1495 мм | 625 мм | 620 мм | 63 | 150 | Сталь_RAL9016 (INPLAST) | саморезы |
| STWS-1500х650-SL | 0.587 м² | 1500 мм | 1495 мм | 650 мм | 645 мм | 65 | 150 | Сталь_RAL9016 (INPLAST) | саморезы |
| STWS-100х100-Z-SL | 0.006 м² | 100 мм | 95 мм | 100 мм | 95 мм | 10 | 10 | Сталь_RAL9016 (INPLAST) | скрытые защелки |
| STWS-125х100-Z-SL | 0.008 м² | 125 мм | 120 мм | 100 мм | 95 мм | 10 | 13 | Сталь_RAL9016 (INPLAST) | скрытые защелки |
| STWS-125х125-Z-SL | 0.009 м² | 125 мм | 120 мм | 125 мм | 120 мм | 13 | 13 | Сталь_RAL9016 (INPLAST) | скрытые защелки |
| STWS-150х100-Z-SL | 0.009 м² | 150 мм | 145 мм | 100 мм | 95 мм | 10 | 15 | Сталь_RAL9016 (INPLAST) | скрытые защелки |
| STWS-150х125-Z-SL | 0.011 м² | 150 мм | 145 мм | 125 мм | 120 мм | 13 | 15 | Сталь_RAL9016 (INPLAST) | скрытые защелки |
| STWS-150х150-Z-SL | 0.014 м² | 150 мм | 145 мм | 150 мм | 145 мм | 15 | 15 | Сталь_RAL9016 (INPLAST) | скрытые защелки |
| STWS-200х100-Z-SL | 0.012 м² | 200 мм | 195 мм | 100 мм | 95 мм | 10 | 20 | Сталь_RAL9016 (INPLAST) | скрытые защелки |
| STWS-200х125-Z-SL | 0.015 м² | 200 мм | 195 мм | 125 мм | 120 мм | 13 | 20 | Сталь_RAL9016 (INPLAST) | скрытые защелки |
| STWS-200х150-Z-SL | 0.018 м² | 200 мм | 195 мм | 150 мм | 145 мм | 15 | 20 | Сталь_RAL9016 (INPLAST) | скрытые защелки |
| STWS-200х200-Z-SL | 0.024 м² | 200 мм | 195 мм | 200 мм | 195 мм | 20 | 20 | Сталь_RAL9016 (INPLAST) | скрытые защелки |
| STWS-225х100-Z-SL | 0.014 м² | 225 мм | 220 мм | 100 мм | 95 мм | 10 | 23 | Сталь_RAL9016 (INPLAST) | скрытые защелки |
| STWS-225х125-Z-SL | 0.017 м² | 225 мм | 220 мм | 125 мм | 120 мм | 13 | 23 | Сталь_RAL9016 (INPLAST) | скрытые защелки |
| STWS-225х150-Z-SL | 0.020 м² | 225 мм | 220 мм | 150 мм | 145 мм | 15 | 23 | Сталь_RAL9016 (INPLAST) | скрытые защелки |
| STWS-225х200-Z-SL | 0.027 м² | 225 мм | 220 мм | 200 мм | 195 мм | 20 | 23 | Сталь_RAL9016 (INPLAST) | скрытые защелки |
| STWS-225х225-Z-SL | 0.030 м² | 225 мм | 220 мм | 225 мм | 220 мм | 23 | 23 | Сталь_RAL9016 (INPLAST) | скрытые защелки |
| STWS-250х100-Z-SL | 0.015 м² | 250 мм | 245 мм | 100 мм | 95 мм | 10 | 25 | Сталь_RAL9016 (INPLAST) | скрытые защелки |
| STWS-250х125-Z-SL | 0.019 м² | 250 мм | 245 мм | 125 мм | 120 мм | 13 | 25 | Сталь_RAL9016 (INPLAST) | скрытые защелки |
| STWS-250х150-Z-SL | 0.023 м² | 250 мм | 245 мм | 150 мм | 145 мм | 15 | 25 | Сталь_RAL9016 (INPLAST) | скрытые защелки |
| STWS-250х200-Z-SL | 0.030 м² | 250 мм | 245 мм | 200 мм | 195 мм | 20 | 25 | Сталь_RAL9016 (INPLAST) | скрытые защелки |
| STWS-250х225-Z-SL | 0.034 м² | 250 мм | 245 мм | 225 мм | 220 мм | 23 | 25 | Сталь_RAL9016 (INPLAST) | скрытые защелки |
| STWS-250х250-Z-SL | 0.038 м² | 250 мм | 245 мм | 250 мм | 245 мм | 25 | 25 | Сталь_RAL9016 (INPLAST) | скрытые защелки |
| STWS-300х100-Z-SL | 0.018 м² | 300 мм | 295 мм | 100 мм | 95 мм | 10 | 30 | Сталь_RAL9016 (INPLAST) | скрытые защелки |
| STWS-300х125-Z-SL | 0.023 м² | 300 мм | 295 мм | 125 мм | 120 мм | 13 | 30 | Сталь_RAL9016 (INPLAST) | скрытые защелки |
| STWS-300х150-Z-SL | 0.027 м² | 300 мм | 295 мм | 150 мм | 145 мм | 15 | 30 | Сталь_RAL9016 (INPLAST) | скрытые защелки |
| STWS-300х200-Z-SL | 0.036 м² | 300 мм | 295 мм | 200 мм | 195 мм | 20 | 30 | Сталь_RAL9016 (INPLAST) | скрытые защелки |
| STWS-300х225-Z-SL | 0.041 м² | 300 мм | 295 мм | 225 мм | 220 мм | 23 | 30 | Сталь_RAL9016 (INPLAST) | скрытые защелки |
| STWS-300х250-Z-SL | 0.045 м² | 300 мм | 295 мм | 250 мм | 245 мм | 25 | 30 | Сталь_RAL9016 (INPLAST) | скрытые защелки |
| STWS-300х300-Z-SL | 0.054 м² | 300 мм | 295 мм | 300 мм | 295 мм | 30 | 30 | Сталь_RAL9016 (INPLAST) | скрытые защелки |
| STWS-325х100-Z-SL | 0.020 м² | 325 мм | 320 мм | 100 мм | 95 мм | 10 | 33 | Сталь_RAL9016 (INPLAST) | скрытые защелки |
| STWS-325х125-Z-SL | 0.024 м² | 325 мм | 320 мм | 125 мм | 120 мм | 13 | 33 | Сталь_RAL9016 (INPLAST) | скрытые защелки |
| STWS-325х150-Z-SL | 0.029 м² | 325 мм | 320 мм | 150 мм | 145 мм | 15 | 33 | Сталь_RAL9016 (INPLAST) | скрытые защелки |
| STWS-325х200-Z-SL | 0.039 м² | 325 мм | 320 мм | 200 мм | 195 мм | 20 | 33 | Сталь_RAL9016 (INPLAST) | скрытые защелки |
| STWS-325х225-Z-SL | 0.044 м² | 325 мм | 320 мм | 225 мм | 220 мм | 23 | 33 | Сталь_RAL9016 (INPLAST) | скрытые защелки |
| STWS-325х250-Z-SL | 0.049 м² | 325 мм | 320 мм | 250 мм | 245 мм | 25 | 33 | Сталь_RAL9016 (INPLAST) | скрытые защелки |
| STWS-325х300-Z-SL | 0.059 м² | 325 мм | 320 мм | 300 мм | 295 мм | 30 | 33 | Сталь_RAL9016 (INPLAST) | скрытые защелки |
| STWS-325х325-Z-SL | 0.064 м² | 325 мм | 320 мм | 325 мм | 320 мм | 33 | 33 | Сталь_RAL9016 (INPLAST) | скрытые защелки |
| STWS-350х100-Z-SL | 0.021 м² | 350 мм | 345 мм | 100 мм | 95 мм | 10 | 35 | Сталь_RAL9016 (INPLAST) | скрытые защелки |
| STWS-350х125-Z-SL | 0.026 м² | 350 мм | 345 мм | 125 мм | 120 мм | 13 | 35 | Сталь_RAL9016 (INPLAST) | скрытые защелки |
| STWS-350х150-Z-SL | 0.032 м² | 350 мм | 345 мм | 150 мм | 145 мм | 15 | 35 | Сталь_RAL9016 (INPLAST) | скрытые защелки |
| STWS-350х200-Z-SL | 0.042 м² | 350 мм | 345 мм | 200 мм | 195 мм | 20 | 35 | Сталь_RAL9016 (INPLAST) | скрытые защелки |
| STWS-350х225-Z-SL | 0.047 м² | 350 мм | 345 мм | 225 мм | 220 мм | 23 | 35 | Сталь_RAL9016 (INPLAST) | скрытые защелки |
| STWS-350х250-Z-SL | 0.053 м² | 350 мм | 345 мм | 250 мм | 245 мм | 25 | 35 | Сталь_RAL9016 (INPLAST) | скрытые защелки |
| STWS-350х300-Z-SL | 0.063 м² | 350 мм | 345 мм | 300 мм | 295 мм | 30 | 35 | Сталь_RAL9016 (INPLAST) | скрытые защелки |
| STWS-350х325-Z-SL | 0.068 м² | 350 мм | 345 мм | 325 мм | 320 мм | 33 | 35 | Сталь_RAL9016 (INPLAST) | скрытые защелки |
| STWS-350х350-Z-SL | 0.074 м² | 350 мм | 345 мм | 350 мм | 345 мм | 35 | 35 | Сталь_RAL9016 (INPLAST) | скрытые защелки |
| STWS-400х100-Z-SL | 0.024 м² | 400 мм | 395 мм | 100 мм | 95 мм | 10 | 40 | Сталь_RAL9016 (INPLAST) | скрытые защелки |
| STWS-400х125-Z-SL | 0.030 м² | 400 мм | 395 мм | 125 мм | 120 мм | 13 | 40 | Сталь_RAL9016 (INPLAST) | скрытые защелки |
| STWS-400х150-Z-SL | 0.036 м² | 400 мм | 395 мм | 150 мм | 145 мм | 15 | 40 | Сталь_RAL9016 (INPLAST) | скрытые защелки |
| STWS-400х200-Z-SL | 0.048 м² | 400 мм | 395 мм | 200 мм | 195 мм | 20 | 40 | Сталь_RAL9016 (INPLAST) | скрытые защелки |
| STWS-400х225-Z-SL | 0.054 м² | 400 мм | 395 мм | 225 мм | 220 мм | 23 | 40 | Сталь_RAL9016 (INPLAST) | скрытые защелки |
| STWS-400х250-Z-SL | 0.060 м² | 400 мм | 395 мм | 250 мм | 245 мм | 25 | 40 | Сталь_RAL9016 (INPLAST) | скрытые защелки |
| STWS-400х300-Z-SL | 0.072 м² | 400 мм | 395 мм | 300 мм | 295 мм | 30 | 40 | Сталь_RAL9016 (INPLAST) | скрытые защелки |
| STWS-400х325-Z-SL | 0.078 м² | 400 мм | 395 мм | 325 мм | 320 мм | 33 | 40 | Сталь_RAL9016 (INPLAST) | скрытые защелки |
| STWS-400х350-Z-SL | 0.084 м² | 400 мм | 395 мм | 350 мм | 345 мм | 35 | 40 | Сталь_RAL9016 (INPLAST) | скрытые защелки |
| STWS-400х400-Z-SL | 0.096 м² | 400 мм | 395 мм | 400 мм | 395 мм | 40 | 40 | Сталь_RAL9016 (INPLAST) | скрытые защелки |
| STWS-425х100-Z-SL | 0.026 м² | 425 мм | 420 мм | 100 мм | 95 мм | 10 | 43 | Сталь_RAL9016 (INPLAST) | скрытые защелки |
| STWS-425х125-Z-SL | 0.032 м² | 425 мм | 420 мм | 125 мм | 120 мм | 13 | 43 | Сталь_RAL9016 (INPLAST) | скрытые защелки |
| STWS-425х150-Z-SL | 0.038 м² | 425 мм | 420 мм | 150 мм | 145 мм | 15 | 43 | Сталь_RAL9016 (INPLAST) | скрытые защелки |
| STWS-425х200-Z-SL | 0.051 м² | 425 мм | 420 мм | 200 мм | 195 мм | 20 | 43 | Сталь_RAL9016 (INPLAST) | скрытые защелки |
| STWS-425х225-Z-SL | 0.058 м² | 425 мм | 420 мм | 225 мм | 220 мм | 23 | 43 | Сталь_RAL9016 (INPLAST) | скрытые защелки |
| STWS-425х250-Z-SL | 0.064 м² | 425 мм | 420 мм | 250 мм | 245 мм | 25 | 43 | Сталь_RAL9016 (INPLAST) | скрытые защелки |
| STWS-425х300-Z-SL | 0.077 м² | 425 мм | 420 мм | 300 мм | 295 мм | 30 | 43 | Сталь_RAL9016 (INPLAST) | скрытые защелки |
| STWS-425х325-Z-SL | 0.083 м² | 425 мм | 420 мм | 325 мм | 320 мм | 33 | 43 | Сталь_RAL9016 (INPLAST) | скрытые защелки |
| STWS-425х350-Z-SL | 0.089 м² | 425 мм | 420 мм | 350 мм | 345 мм | 35 | 43 | Сталь_RAL9016 (INPLAST) | скрытые защелки |
| STWS-425х400-Z-SL | 0.102 м² | 425 мм | 420 мм | 400 мм | 395 мм | 40 | 43 | Сталь_RAL9016 (INPLAST) | скрытые защелки |
| STWS-425х425-Z-SL | 0.109 м² | 425 мм | 420 мм | 425 мм | 420 мм | 43 | 43 | Сталь_RAL9016 (INPLAST) | скрытые защелки |
| STWS-450х100-Z-SL | 0.027 м² | 450 мм | 445 мм | 100 мм | 95 мм | 10 | 45 | Сталь_RAL9016 (INPLAST) | скрытые защелки |
| STWS-450х125-Z-SL | 0.034 м² | 450 мм | 445 мм | 125 мм | 120 мм | 13 | 45 | Сталь_RAL9016 (INPLAST) | скрытые защелки |
| STWS-450х150-Z-SL | 0.041 м² | 450 мм | 445 мм | 150 мм | 145 мм | 15 | 45 | Сталь_RAL9016 (INPLAST) | скрытые защелки |
| STWS-450х200-Z-SL | 0.054 м² | 450 мм | 445 мм | 200 мм | 195 мм | 20 | 45 | Сталь_RAL9016 (INPLAST) | скрытые защелки |
| STWS-450х225-Z-SL | 0.061 м² | 450 мм | 445 мм | 225 мм | 220 мм | 23 | 45 | Сталь_RAL9016 (INPLAST) | скрытые защелки |
| STWS-450х250-Z-SL | 0.068 м² | 450 мм | 445 мм | 250 мм | 245 мм | 25 | 45 | Сталь_RAL9016 (INPLAST) | скрытые защелки |
| STWS-450х300-Z-SL | 0.081 м² | 450 мм | 445 мм | 300 мм | 295 мм | 30 | 45 | Сталь_RAL9016 (INPLAST) | скрытые защелки |
| STWS-450х325-Z-SL | 0.088 м² | 450 мм | 445 мм | 325 мм | 320 мм | 33 | 45 | Сталь_RAL9016 (INPLAST) | скрытые защелки |
| STWS-450х350-Z-SL | 0.095 м² | 450 мм | 445 мм | 350 мм | 345 мм | 35 | 45 | Сталь_RAL9016 (INPLAST) | скрытые защелки |
| STWS-450х400-Z-SL | 0.108 м² | 450 мм | 445 мм | 400 мм | 395 мм | 40 | 45 | Сталь_RAL9016 (INPLAST) | скрытые защелки |
| STWS-450х425-Z-SL | 0.115 м² | 450 мм | 445 мм | 425 мм | 420 мм | 43 | 45 | Сталь_RAL9016 (INPLAST) | скрытые защелки |
| STWS-450х450-Z-SL | 0.122 м² | 450 мм | 445 мм | 450 мм | 445 мм | 45 | 45 | Сталь_RAL9016 (INPLAST) | скрытые защелки |
| STWS-500х100-Z-SL | 0.030 м² | 500 мм | 495 мм | 100 мм | 95 мм | 10 | 50 | Сталь_RAL9016 (INPLAST) | скрытые защелки |
| STWS-500х125-Z-SL | 0.038 м² | 500 мм | 495 мм | 125 мм | 120 мм | 13 | 50 | Сталь_RAL9016 (INPLAST) | скрытые защелки |
| STWS-500х150-Z-SL | 0.045 м² | 500 мм | 495 мм | 150 мм | 145 мм | 15 | 50 | Сталь_RAL9016 (INPLAST) | скрытые защелки |
| STWS-500х200-Z-SL | 0.060 м² | 500 мм | 495 мм | 200 мм | 195 мм | 20 | 50 | Сталь_RAL9016 (INPLAST) | скрытые защелки |
| STWS-500х225-Z-SL | 0.068 м² | 500 мм | 495 мм | 225 мм | 220 мм | 23 | 50 | Сталь_RAL9016 (INPLAST) | скрытые защелки |
| STWS-500х250-Z-SL | 0.075 м² | 500 мм | 495 мм | 250 мм | 245 мм | 25 | 50 | Сталь_RAL9016 (INPLAST) | скрытые защелки |
| STWS-500х300-Z-SL | 0.090 м² | 500 мм | 495 мм | 300 мм | 295 мм | 30 | 50 | Сталь_RAL9016 (INPLAST) | скрытые защелки |
| STWS-500х325-Z-SL | 0.098 м² | 500 мм | 495 мм | 325 мм | 320 мм | 33 | 50 | Сталь_RAL9016 (INPLAST) | скрытые защелки |
| STWS-500х350-Z-SL | 0.105 м² | 500 мм | 495 мм | 350 мм | 345 мм | 35 | 50 | Сталь_RAL9016 (INPLAST) | скрытые защелки |
| STWS-500х400-Z-SL | 0.120 м² | 500 мм | 495 мм | 400 мм | 395 мм | 40 | 50 | Сталь_RAL9016 (INPLAST) | скрытые защелки |
| STWS-500х425-Z-SL | 0.128 м² | 500 мм | 495 мм | 425 мм | 420 мм | 43 | 50 | Сталь_RAL9016 (INPLAST) | скрытые защелки |
| STWS-500х450-Z-SL | 0.135 м² | 500 мм | 495 мм | 450 мм | 445 мм | 45 | 50 | Сталь_RAL9016 (INPLAST) | скрытые защелки |
| STWS-500х500-Z-SL | 0.150 м² | 500 мм | 495 мм | 500 мм | 495 мм | 50 | 50 | Сталь_RAL9016 (INPLAST) | скрытые защелки |
| STWS-525х100-Z-SL | 0.032 м² | 525 мм | 520 мм | 100 мм | 95 мм | 10 | 53 | Сталь_RAL9016 (INPLAST) | скрытые защелки |
| STWS-525х125-Z-SL | 0.039 м² | 525 мм | 520 мм | 125 мм | 120 мм | 13 | 53 | Сталь_RAL9016 (INPLAST) | скрытые защелки |
| STWS-525х150-Z-SL | 0.047 м² | 525 мм | 520 мм | 150 мм | 145 мм | 15 | 53 | Сталь_RAL9016 (INPLAST) | скрытые защелки |
| STWS-525х200-Z-SL | 0.063 м² | 525 мм | 520 мм | 200 мм | 195 мм | 20 | 53 | Сталь_RAL9016 (INPLAST) | скрытые защелки |
| STWS-525х225-Z-SL | 0.071 м² | 525 мм | 520 мм | 225 мм | 220 мм | 23 | 53 | Сталь_RAL9016 (INPLAST) | скрытые защелки |
| STWS-525х250-Z-SL | 0.079 м² | 525 мм | 520 мм | 250 мм | 245 мм | 25 | 53 | Сталь_RAL9016 (INPLAST) | скрытые защелки |
| STWS-525х300-Z-SL | 0.095 м² | 525 мм | 520 мм | 300 мм | 295 мм | 30 | 53 | Сталь_RAL9016 (INPLAST) | скрытые защелки |
| STWS-525х325-Z-SL | 0.103 м² | 525 мм | 520 мм | 325 мм | 320 мм | 33 | 53 | Сталь_RAL9016 (INPLAST) | скрытые защелки |
| STWS-525х350-Z-SL | 0.111 м² | 525 мм | 520 мм | 350 мм | 345 мм | 35 | 53 | Сталь_RAL9016 (INPLAST) | скрытые защелки |
| STWS-525х400-Z-SL | 0.126 м² | 525 мм | 520 мм | 400 мм | 395 мм | 40 | 53 | Сталь_RAL9016 (INPLAST) | скрытые защелки |
| STWS-525х425-Z-SL | 0.134 м² | 525 мм | 520 мм | 425 мм | 420 мм | 43 | 53 | Сталь_RAL9016 (INPLAST) | скрытые защелки |
| STWS-525х450-Z-SL | 0.142 м² | 525 мм | 520 мм | 450 мм | 445 мм | 45 | 53 | Сталь_RAL9016 (INPLAST) | скрытые защелки |
| STWS-525х500-Z-SL | 0.158 м² | 525 мм | 520 мм | 500 мм | 495 мм | 50 | 53 | Сталь_RAL9016 (INPLAST) | скрытые защелки |
| STWS-525х525-Z-SL | 0.166 м² | 525 мм | 520 мм | 525 мм | 520 мм | 53 | 53 | Сталь_RAL9016 (INPLAST) | скрытые защелки |
| STWS-550х100-Z-SL | 0.033 м² | 550 мм | 545 мм | 100 мм | 95 мм | 10 | 55 | Сталь_RAL9016 (INPLAST) | скрытые защелки |
| STWS-550х125-Z-SL | 0.041 м² | 550 мм | 545 мм | 125 мм | 120 мм | 13 | 55 | Сталь_RAL9016 (INPLAST) | скрытые защелки |
| STWS-550х150-Z-SL | 0.050 м² | 550 мм | 545 мм | 150 мм | 145 мм | 15 | 55 | Сталь_RAL9016 (INPLAST) | скрытые защелки |
| STWS-550х200-Z-SL | 0.066 м² | 550 мм | 545 мм | 200 мм | 195 мм | 20 | 55 | Сталь_RAL9016 (INPLAST) | скрытые защелки |
| STWS-550х225-Z-SL | 0.074 м² | 550 мм | 545 мм | 225 мм | 220 мм | 23 | 55 | Сталь_RAL9016 (INPLAST) | скрытые защелки |
| STWS-550х250-Z-SL | 0.083 м² | 550 мм | 545 мм | 250 мм | 245 мм | 25 | 55 | Сталь_RAL9016 (INPLAST) | скрытые защелки |
| STWS-550х300-Z-SL | 0.099 м² | 550 мм | 545 мм | 300 мм | 295 мм | 30 | 55 | Сталь_RAL9016 (INPLAST) | скрытые защелки |
| STWS-550х325-Z-SL | 0.108 м² | 550 мм | 545 мм | 325 мм | 320 мм | 33 | 55 | Сталь_RAL9016 (INPLAST) | скрытые защелки |
| STWS-550х350-Z-SL | 0.116 м² | 550 мм | 545 мм | 350 мм | 345 мм | 35 | 55 | Сталь_RAL9016 (INPLAST) | скрытые защелки |
| STWS-550х400-Z-SL | 0.132 м² | 550 мм | 545 мм | 400 мм | 395 мм | 40 | 55 | Сталь_RAL9016 (INPLAST) | скрытые защелки |
| STWS-550х425-Z-SL | 0.141 м² | 550 мм | 545 мм | 425 мм | 420 мм | 43 | 55 | Сталь_RAL9016 (INPLAST) | скрытые защелки |
| STWS-550х450-Z-SL | 0.149 м² | 550 мм | 545 мм | 450 мм | 445 мм | 45 | 55 | Сталь_RAL9016 (INPLAST) | скрытые защелки |
| STWS-550х500-Z-SL | 0.165 м² | 550 мм | 545 мм | 500 мм | 495 мм | 50 | 55 | Сталь_RAL9016 (INPLAST) | скрытые защелки |
| STWS-550х525-Z-SL | 0.174 м² | 550 мм | 545 мм | 525 мм | 520 мм | 53 | 55 | Сталь_RAL9016 (INPLAST) | скрытые защелки |
| STWS-550х550-Z-SL | 0.182 м² | 550 мм | 545 мм | 550 мм | 545 мм | 55 | 55 | Сталь_RAL9016 (INPLAST) | скрытые защелки |
| STWS-600х100-Z-SL | 0.036 м² | 600 мм | 595 мм | 100 мм | 95 мм | 10 | 60 | Сталь_RAL9016 (INPLAST) | скрытые защелки |
| STWS-600х125-Z-SL | 0.045 м² | 600 мм | 595 мм | 125 мм | 120 мм | 13 | 60 | Сталь_RAL9016 (INPLAST) | скрытые защелки |
| STWS-600х150-Z-SL | 0.054 м² | 600 мм | 595 мм | 150 мм | 145 мм | 15 | 60 | Сталь_RAL9016 (INPLAST) | скрытые защелки |
| STWS-600х200-Z-SL | 0.072 м² | 600 мм | 595 мм | 200 мм | 195 мм | 20 | 60 | Сталь_RAL9016 (INPLAST) | скрытые защелки |
| STWS-600х225-Z-SL | 0.081 м² | 600 мм | 595 мм | 225 мм | 220 мм | 23 | 60 | Сталь_RAL9016 (INPLAST) | скрытые защелки |
| STWS-600х250-Z-SL | 0.090 м² | 600 мм | 595 мм | 250 мм | 245 мм | 25 | 60 | Сталь_RAL9016 (INPLAST) | скрытые защелки |
| STWS-600х300-Z-SL | 0.108 м² | 600 мм | 595 мм | 300 мм | 295 мм | 30 | 60 | Сталь_RAL9016 (INPLAST) | скрытые защелки |
| STWS-600х325-Z-SL | 0.117 м² | 600 мм | 595 мм | 325 мм | 320 мм | 33 | 60 | Сталь_RAL9016 (INPLAST) | скрытые защелки |
| STWS-600х350-Z-SL | 0.126 м² | 600 мм | 595 мм | 350 мм | 345 мм | 35 | 60 | Сталь_RAL9016 (INPLAST) | скрытые защелки |
| STWS-600х400-Z-SL | 0.144 м² | 600 мм | 595 мм | 400 мм | 395 мм | 40 | 60 | Сталь_RAL9016 (INPLAST) | скрытые защелки |
| STWS-600х425-Z-SL | 0.153 м² | 600 мм | 595 мм | 425 мм | 420 мм | 43 | 60 | Сталь_RAL9016 (INPLAST) | скрытые защелки |
| STWS-600х450-Z-SL | 0.162 м² | 600 мм | 595 мм | 450 мм | 445 мм | 45 | 60 | Сталь_RAL9016 (INPLAST) | скрытые защелки |
| STWS-600х500-Z-SL | 0.180 м² | 600 мм | 595 мм | 500 мм | 495 мм | 50 | 60 | Сталь_RAL9016 (INPLAST) | скрытые защелки |
| STWS-600х525-Z-SL | 0.190 м² | 600 мм | 595 мм | 525 мм | 520 мм | 53 | 60 | Сталь_RAL9016 (INPLAST) | скрытые защелки |
| STWS-600х550-Z-SL | 0.199 м² | 600 мм | 595 мм | 550 мм | 545 мм | 55 | 60 | Сталь_RAL9016 (INPLAST) | скрытые защелки |
| STWS-600х600-Z-SL | 0.217 м² | 600 мм | 595 мм | 600 мм | 595 мм | 60 | 60 | Сталь_RAL9016 (INPLAST) | скрытые защелки |
| STWS-625х100-Z-SL | 0.038 м² | 625 мм | 620 мм | 100 мм | 95 мм | 10 | 63 | Сталь_RAL9016 (INPLAST) | скрытые защелки |
| STWS-625х125-Z-SL | 0.047 м² | 625 мм | 620 мм | 125 мм | 120 мм | 13 | 63 | Сталь_RAL9016 (INPLAST) | скрытые защелки |
| STWS-625х150-Z-SL | 0.056 м² | 625 мм | 620 мм | 150 мм | 145 мм | 15 | 63 | Сталь_RAL9016 (INPLAST) | скрытые защелки |
| STWS-625х200-Z-SL | 0.075 м² | 625 мм | 620 мм | 200 мм | 195 мм | 20 | 63 | Сталь_RAL9016 (INPLAST) | скрытые защелки |
| STWS-625х225-Z-SL | 0.085 м² | 625 мм | 620 мм | 225 мм | 220 мм | 23 | 63 | Сталь_RAL9016 (INPLAST) | скрытые защелки |
| STWS-625х250-Z-SL | 0.094 м² | 625 мм | 620 мм | 250 мм | 245 мм | 25 | 63 | Сталь_RAL9016 (INPLAST) | скрытые защелки |
| STWS-625х300-Z-SL | 0.113 м² | 625 мм | 620 мм | 300 мм | 295 мм | 30 | 63 | Сталь_RAL9016 (INPLAST) | скрытые защелки |
| STWS-625х325-Z-SL | 0.122 м² | 625 мм | 620 мм | 325 мм | 320 мм | 33 | 63 | Сталь_RAL9016 (INPLAST) | скрытые защелки |
| STWS-625х350-Z-SL | 0.132 м² | 625 мм | 620 мм | 350 мм | 345 мм | 35 | 63 | Сталь_RAL9016 (INPLAST) | скрытые защелки |
| STWS-625х400-Z-SL | 0.150 м² | 625 мм | 620 мм | 400 мм | 395 мм | 40 | 63 | Сталь_RAL9016 (INPLAST) | скрытые защелки |
| STWS-625х425-Z-SL | 0.160 м² | 625 мм | 620 мм | 425 мм | 420 мм | 43 | 63 | Сталь_RAL9016 (INPLAST) | скрытые защелки |
| STWS-625х450-Z-SL | 0.169 м² | 625 мм | 620 мм | 450 мм | 445 мм | 45 | 63 | Сталь_RAL9016 (INPLAST) | скрытые защелки |
| STWS-625х500-Z-SL | 0.188 м² | 625 мм | 620 мм | 500 мм | 495 мм | 50 | 63 | Сталь_RAL9016 (INPLAST) | скрытые защелки |
| STWS-625х525-Z-SL | 0.197 м² | 625 мм | 620 мм | 525 мм | 520 мм | 53 | 63 | Сталь_RAL9016 (INPLAST) | скрытые защелки |
| STWS-625х550-Z-SL | 0.207 м² | 625 мм | 620 мм | 550 мм | 545 мм | 55 | 63 | Сталь_RAL9016 (INPLAST) | скрытые защелки |
| STWS-625х600-Z-SL | 0.226 м² | 625 мм | 620 мм | 600 мм | 595 мм | 60 | 63 | Сталь_RAL9016 (INPLAST) | скрытые защелки |
| STWS-625х625-Z-SL | 0.235 м² | 625 мм | 620 мм | 625 мм | 620 мм | 63 | 63 | Сталь_RAL9016 (INPLAST) | скрытые защелки |
| STWS-650х100-Z-SL | 0.039 м² | 650 мм | 645 мм | 100 мм | 95 мм | 10 | 65 | Сталь_RAL9016 (INPLAST) | скрытые защелки |
| STWS-650х125-Z-SL | 0.049 м² | 650 мм | 645 мм | 125 мм | 120 мм | 13 | 65 | Сталь_RAL9016 (INPLAST) | скрытые защелки |
| STWS-650х150-Z-SL | 0.059 м² | 650 мм | 645 мм | 150 мм | 145 мм | 15 | 65 | Сталь_RAL9016 (INPLAST) | скрытые защелки |
| STWS-650х200-Z-SL | 0.078 м² | 650 мм | 645 мм | 200 мм | 195 мм | 20 | 65 | Сталь_RAL9016 (INPLAST) | скрытые защелки |
| STWS-650х225-Z-SL | 0.088 м² | 650 мм | 645 мм | 225 мм | 220 мм | 23 | 65 | Сталь_RAL9016 (INPLAST) | скрытые защелки |
| STWS-650х250-Z-SL | 0.098 м² | 650 мм | 645 мм | 250 мм | 245 мм | 25 | 65 | Сталь_RAL9016 (INPLAST) | скрытые защелки |
| STWS-650х300-Z-SL | 0.117 м² | 650 мм | 645 мм | 300 мм | 295 мм | 30 | 65 | Сталь_RAL9016 (INPLAST) | скрытые защелки |
| STWS-650х325-Z-SL | 0.127 м² | 650 мм | 645 мм | 325 мм | 320 мм | 33 | 65 | Сталь_RAL9016 (INPLAST) | скрытые защелки |
| STWS-650х350-Z-SL | 0.137 м² | 650 мм | 645 мм | 350 мм | 345 мм | 35 | 65 | Сталь_RAL9016 (INPLAST) | скрытые защелки |
| STWS-650х400-Z-SL | 0.156 м² | 650 мм | 645 мм | 400 мм | 395 мм | 40 | 65 | Сталь_RAL9016 (INPLAST) | скрытые защелки |
| STWS-650х425-Z-SL | 0.166 м² | 650 мм | 645 мм | 425 мм | 420 мм | 43 | 65 | Сталь_RAL9016 (INPLAST) | скрытые защелки |
| STWS-650х450-Z-SL | 0.176 м² | 650 мм | 645 мм | 450 мм | 445 мм | 45 | 65 | Сталь_RAL9016 (INPLAST) | скрытые защелки |
| STWS-650х500-Z-SL | 0.196 м² | 650 мм | 645 мм | 500 мм | 495 мм | 50 | 65 | Сталь_RAL9016 (INPLAST) | скрытые защелки |
| STWS-650х525-Z-SL | 0.205 м² | 650 мм | 645 мм | 525 мм | 520 мм | 53 | 65 | Сталь_RAL9016 (INPLAST) | скрытые защелки |
| STWS-650х550-Z-SL | 0.215 м² | 650 мм | 645 мм | 550 мм | 545 мм | 55 | 65 | Сталь_RAL9016 (INPLAST) | скрытые защелки |
| STWS-650х600-Z-SL | 0.235 м² | 650 мм | 645 мм | 600 мм | 595 мм | 60 | 65 | Сталь_RAL9016 (INPLAST) | скрытые защелки |
| STWS-650х625-Z-SL | 0.244 м² | 650 мм | 645 мм | 625 мм | 620 мм | 63 | 65 | Сталь_RAL9016 (INPLAST) | скрытые защелки |
| STWS-650х650-Z-SL | 0.254 м² | 650 мм | 645 мм | 650 мм | 645 мм | 65 | 65 | Сталь_RAL9016 (INPLAST) | скрытые защелки |
| STWS-700х100-Z-SL | 0.042 м² | 700 мм | 695 мм | 100 мм | 95 мм | 10 | 70 | Сталь_RAL9016 (INPLAST) | скрытые защелки |
| STWS-700х125-Z-SL | 0.053 м² | 700 мм | 695 мм | 125 мм | 120 мм | 13 | 70 | Сталь_RAL9016 (INPLAST) | скрытые защелки |
| STWS-700х150-Z-SL | 0.063 м² | 700 мм | 695 мм | 150 мм | 145 мм | 15 | 70 | Сталь_RAL9016 (INPLAST) | скрытые защелки |
| STWS-700х200-Z-SL | 0.084 м² | 700 мм | 695 мм | 200 мм | 195 мм | 20 | 70 | Сталь_RAL9016 (INPLAST) | скрытые защелки |
| STWS-700х225-Z-SL | 0.095 м² | 700 мм | 695 мм | 225 мм | 220 мм | 23 | 70 | Сталь_RAL9016 (INPLAST) | скрытые защелки |
| STWS-700х250-Z-SL | 0.105 м² | 700 мм | 695 мм | 250 мм | 245 мм | 25 | 70 | Сталь_RAL9016 (INPLAST) | скрытые защелки |
| STWS-700х300-Z-SL | 0.126 м² | 700 мм | 695 мм | 300 мм | 295 мм | 30 | 70 | Сталь_RAL9016 (INPLAST) | скрытые защелки |
| STWS-700х325-Z-SL | 0.137 м² | 700 мм | 695 мм | 325 мм | 320 мм | 33 | 70 | Сталь_RAL9016 (INPLAST) | скрытые защелки |
| STWS-700х350-Z-SL | 0.147 м² | 700 мм | 695 мм | 350 мм | 345 мм | 35 | 70 | Сталь_RAL9016 (INPLAST) | скрытые защелки |
| STWS-700х400-Z-SL | 0.168 м² | 700 мм | 695 мм | 400 мм | 395 мм | 40 | 70 | Сталь_RAL9016 (INPLAST) | скрытые защелки |
| STWS-700х425-Z-SL | 0.179 м² | 700 мм | 695 мм | 425 мм | 420 мм | 43 | 70 | Сталь_RAL9016 (INPLAST) | скрытые защелки |
| STWS-700х450-Z-SL | 0.190 м² | 700 мм | 695 мм | 450 мм | 445 мм | 45 | 70 | Сталь_RAL9016 (INPLAST) | скрытые защелки |
| STWS-700х500-Z-SL | 0.211 м² | 700 мм | 695 мм | 500 мм | 495 мм | 50 | 70 | Сталь_RAL9016 (INPLAST) | скрытые защелки |
| STWS-700х525-Z-SL | 0.221 м² | 700 мм | 695 мм | 525 мм | 520 мм | 53 | 70 | Сталь_RAL9016 (INPLAST) | скрытые защелки |
| STWS-700х550-Z-SL | 0.232 м² | 700 мм | 695 мм | 550 мм | 545 мм | 55 | 70 | Сталь_RAL9016 (INPLAST) | скрытые защелки |
| STWS-700х600-Z-SL | 0.253 м² | 700 мм | 695 мм | 600 мм | 595 мм | 60 | 70 | Сталь_RAL9016 (INPLAST) | скрытые защелки |
| STWS-700х625-Z-SL | 0.263 м² | 700 мм | 695 мм | 625 мм | 620 мм | 63 | 70 | Сталь_RAL9016 (INPLAST) | скрытые защелки |
| STWS-700х650-Z-SL | 0.274 м² | 700 мм | 695 мм | 650 мм | 645 мм | 65 | 70 | Сталь_RAL9016 (INPLAST) | скрытые защелки |
| STWS-725х100-Z-SL | 0.044 м² | 725 мм | 720 мм | 100 мм | 95 мм | 10 | 73 | Сталь_RAL9016 (INPLAST) | скрытые защелки |
| STWS-725х125-Z-SL | 0.055 м² | 725 мм | 720 мм | 125 мм | 120 мм | 13 | 73 | Сталь_RAL9016 (INPLAST) | скрытые защелки |
| STWS-725х150-Z-SL | 0.065 м² | 725 мм | 720 мм | 150 мм | 145 мм | 15 | 73 | Сталь_RAL9016 (INPLAST) | скрытые защелки |
| STWS-725х200-Z-SL | 0.087 м² | 725 мм | 720 мм | 200 мм | 195 мм | 20 | 73 | Сталь_RAL9016 (INPLAST) | скрытые защелки |
| STWS-725х225-Z-SL | 0.098 м² | 725 мм | 720 мм | 225 мм | 220 мм | 23 | 73 | Сталь_RAL9016 (INPLAST) | скрытые защелки |
| STWS-725х250-Z-SL | 0.109 м² | 725 мм | 720 мм | 250 мм | 245 мм | 25 | 73 | Сталь_RAL9016 (INPLAST) | скрытые защелки |
| STWS-725х300-Z-SL | 0.131 м² | 725 мм | 720 мм | 300 мм | 295 мм | 30 | 73 | Сталь_RAL9016 (INPLAST) | скрытые защелки |
| STWS-725х325-Z-SL | 0.142 м² | 725 мм | 720 мм | 325 мм | 320 мм | 33 | 73 | Сталь_RAL9016 (INPLAST) | скрытые защелки |
| STWS-725х350-Z-SL | 0.153 м² | 725 мм | 720 мм | 350 мм | 345 мм | 35 | 73 | Сталь_RAL9016 (INPLAST) | скрытые защелки |
| STWS-725х400-Z-SL | 0.174 м² | 725 мм | 720 мм | 400 мм | 395 мм | 40 | 73 | Сталь_RAL9016 (INPLAST) | скрытые защелки |
| STWS-725х425-Z-SL | 0.185 м² | 725 мм | 720 мм | 425 мм | 420 мм | 43 | 73 | Сталь_RAL9016 (INPLAST) | скрытые защелки |
| STWS-725х450-Z-SL | 0.196 м² | 725 мм | 720 мм | 450 мм | 445 мм | 45 | 73 | Сталь_RAL9016 (INPLAST) | скрытые защелки |
| STWS-725х500-Z-SL | 0.218 м² | 725 мм | 720 мм | 500 мм | 495 мм | 50 | 73 | Сталь_RAL9016 (INPLAST) | скрытые защелки |
| STWS-725х525-Z-SL | 0.229 м² | 725 мм | 720 мм | 525 мм | 520 мм | 53 | 73 | Сталь_RAL9016 (INPLAST) | скрытые защелки |
| STWS-725х550-Z-SL | 0.240 м² | 725 мм | 720 мм | 550 мм | 545 мм | 55 | 73 | Сталь_RAL9016 (INPLAST) | скрытые защелки |
| STWS-725х600-Z-SL | 0.262 м² | 725 мм | 720 мм | 600 мм | 595 мм | 60 | 73 | Сталь_RAL9016 (INPLAST) | скрытые защелки |
| STWS-725х625-Z-SL | 0.273 м² | 725 мм | 720 мм | 625 мм | 620 мм | 63 | 73 | Сталь_RAL9016 (INPLAST) | скрытые защелки |
| STWS-725х650-Z-SL | 0.284 м² | 725 мм | 720 мм | 650 мм | 645 мм | 65 | 73 | Сталь_RAL9016 (INPLAST) | скрытые защелки |
| STWS-750х100-Z-SL | 0.045 м² | 750 мм | 745 мм | 100 мм | 95 мм | 10 | 75 | Сталь_RAL9016 (INPLAST) | скрытые защелки |
| STWS-750х125-Z-SL | 0.056 м² | 750 мм | 745 мм | 125 мм | 120 мм | 13 | 75 | Сталь_RAL9016 (INPLAST) | скрытые защелки |
| STWS-750х150-Z-SL | 0.068 м² | 750 мм | 745 мм | 150 мм | 145 мм | 15 | 75 | Сталь_RAL9016 (INPLAST) | скрытые защелки |
| STWS-750х200-Z-SL | 0.090 м² | 750 мм | 745 мм | 200 мм | 195 мм | 20 | 75 | Сталь_RAL9016 (INPLAST) | скрытые защелки |
| STWS-750х225-Z-SL | 0.102 м² | 750 мм | 745 мм | 225 мм | 220 мм | 23 | 75 | Сталь_RAL9016 (INPLAST) | скрытые защелки |
| STWS-750х250-Z-SL | 0.113 м² | 750 мм | 745 мм | 250 мм | 245 мм | 25 | 75 | Сталь_RAL9016 (INPLAST) | скрытые защелки |
| STWS-750х300-Z-SL | 0.135 м² | 750 мм | 745 мм | 300 мм | 295 мм | 30 | 75 | Сталь_RAL9016 (INPLAST) | скрытые защелки |
| STWS-750х325-Z-SL | 0.147 м² | 750 мм | 745 мм | 325 мм | 320 мм | 33 | 75 | Сталь_RAL9016 (INPLAST) | скрытые защелки |
| STWS-750х350-Z-SL | 0.158 м² | 750 мм | 745 мм | 350 мм | 345 мм | 35 | 75 | Сталь_RAL9016 (INPLAST) | скрытые защелки |
| STWS-750х400-Z-SL | 0.180 м² | 750 мм | 745 мм | 400 мм | 395 мм | 40 | 75 | Сталь_RAL9016 (INPLAST) | скрытые защелки |
| STWS-750х425-Z-SL | 0.192 м² | 750 мм | 745 мм | 425 мм | 420 мм | 43 | 75 | Сталь_RAL9016 (INPLAST) | скрытые защелки |
| STWS-750х450-Z-SL | 0.203 м² | 750 мм | 745 мм | 450 мм | 445 мм | 45 | 75 | Сталь_RAL9016 (INPLAST) | скрытые защелки |
| STWS-750х500-Z-SL | 0.226 м² | 750 мм | 745 мм | 500 мм | 495 мм | 50 | 75 | Сталь_RAL9016 (INPLAST) | скрытые защелки |
| STWS-750х525-Z-SL | 0.237 м² | 750 мм | 745 мм | 525 мм | 520 мм | 53 | 75 | Сталь_RAL9016 (INPLAST) | скрытые защелки |
| STWS-750х550-Z-SL | 0.248 м² | 750 мм | 745 мм | 550 мм | 545 мм | 55 | 75 | Сталь_RAL9016 (INPLAST) | скрытые защелки |
| STWS-750х600-Z-SL | 0.271 м² | 750 мм | 745 мм | 600 мм | 595 мм | 60 | 75 | Сталь_RAL9016 (INPLAST) | скрытые защелки |
| STWS-750х625-Z-SL | 0.282 м² | 750 мм | 745 мм | 625 мм | 620 мм | 63 | 75 | Сталь_RAL9016 (INPLAST) | скрытые защелки |
| STWS-750х650-Z-SL | 0.293 м² | 750 мм | 745 мм | 650 мм | 645 мм | 65 | 75 | Сталь_RAL9016 (INPLAST) | скрытые защелки |
| STWS-800х100-Z-SL | 0.048 м² | 800 мм | 795 мм | 100 мм | 95 мм | 10 | 80 | Сталь_RAL9016 (INPLAST) | скрытые защелки |
| STWS-800х125-Z-SL | 0.060 м² | 800 мм | 795 мм | 125 мм | 120 мм | 13 | 80 | Сталь_RAL9016 (INPLAST) | скрытые защелки |
| STWS-800х150-Z-SL | 0.072 м² | 800 мм | 795 мм | 150 мм | 145 мм | 15 | 80 | Сталь_RAL9016 (INPLAST) | скрытые защелки |
| STWS-800х200-Z-SL | 0.096 м² | 800 мм | 795 мм | 200 мм | 195 мм | 20 | 80 | Сталь_RAL9016 (INPLAST) | скрытые защелки |
| STWS-800х225-Z-SL | 0.108 м² | 800 мм | 795 мм | 225 мм | 220 мм | 23 | 80 | Сталь_RAL9016 (INPLAST) | скрытые защелки |
| STWS-800х250-Z-SL | 0.120 м² | 800 мм | 795 мм | 250 мм | 245 мм | 25 | 80 | Сталь_RAL9016 (INPLAST) | скрытые защелки |
| STWS-800х300-Z-SL | 0.144 м² | 800 мм | 795 мм | 300 мм | 295 мм | 30 | 80 | Сталь_RAL9016 (INPLAST) | скрытые защелки |
| STWS-800х325-Z-SL | 0.156 м² | 800 мм | 795 мм | 325 мм | 320 мм | 33 | 80 | Сталь_RAL9016 (INPLAST) | скрытые защелки |
| STWS-800х350-Z-SL | 0.168 м² | 800 мм | 795 мм | 350 мм | 345 мм | 35 | 80 | Сталь_RAL9016 (INPLAST) | скрытые защелки |
| STWS-800х400-Z-SL | 0.193 м² | 800 мм | 795 мм | 400 мм | 395 мм | 40 | 80 | Сталь_RAL9016 (INPLAST) | скрытые защелки |
| STWS-800х425-Z-SL | 0.205 м² | 800 мм | 795 мм | 425 мм | 420 мм | 43 | 80 | Сталь_RAL9016 (INPLAST) | скрытые защелки |
| STWS-800х450-Z-SL | 0.217 м² | 800 мм | 795 мм | 450 мм | 445 мм | 45 | 80 | Сталь_RAL9016 (INPLAST) | скрытые защелки |
| STWS-800х500-Z-SL | 0.241 м² | 800 мм | 795 мм | 500 мм | 495 мм | 50 | 80 | Сталь_RAL9016 (INPLAST) | скрытые защелки |
| STWS-800х525-Z-SL | 0.253 м² | 800 мм | 795 мм | 525 мм | 520 мм | 53 | 80 | Сталь_RAL9016 (INPLAST) | скрытые защелки |
| STWS-800х550-Z-SL | 0.265 м² | 800 мм | 795 мм | 550 мм | 545 мм | 55 | 80 | Сталь_RAL9016 (INPLAST) | скрытые защелки |
| STWS-800х600-Z-SL | 0.289 м² | 800 мм | 795 мм | 600 мм | 595 мм | 60 | 80 | Сталь_RAL9016 (INPLAST) | скрытые защелки |
| STWS-800х625-Z-SL | 0.301 м² | 800 мм | 795 мм | 625 мм | 620 мм | 63 | 80 | Сталь_RAL9016 (INPLAST) | скрытые защелки |
| STWS-800х650-Z-SL | 0.313 м² | 800 мм | 795 мм | 650 мм | 645 мм | 65 | 80 | Сталь_RAL9016 (INPLAST) | скрытые защелки |
| STWS-825х100-Z-SL | 0.050 м² | 825 мм | 820 мм | 100 мм | 95 мм | 10 | 83 | Сталь_RAL9016 (INPLAST) | скрытые защелки |
| STWS-825х125-Z-SL | 0.062 м² | 825 мм | 820 мм | 125 мм | 120 мм | 13 | 83 | Сталь_RAL9016 (INPLAST) | скрытые защелки |
| STWS-825х150-Z-SL | 0.074 м² | 825 мм | 820 мм | 150 мм | 145 мм | 15 | 83 | Сталь_RAL9016 (INPLAST) | скрытые защелки |
| STWS-825х200-Z-SL | 0.099 м² | 825 мм | 820 мм | 200 мм | 195 мм | 20 | 83 | Сталь_RAL9016 (INPLAST) | скрытые защелки |
| STWS-825х225-Z-SL | 0.112 м² | 825 мм | 820 мм | 225 мм | 220 мм | 23 | 83 | Сталь_RAL9016 (INPLAST) | скрытые защелки |
| STWS-825х250-Z-SL | 0.124 м² | 825 мм | 820 мм | 250 мм | 245 мм | 25 | 83 | Сталь_RAL9016 (INPLAST) | скрытые защелки |
| STWS-825х300-Z-SL | 0.149 м² | 825 мм | 820 мм | 300 мм | 295 мм | 30 | 83 | Сталь_RAL9016 (INPLAST) | скрытые защелки |
| STWS-825х325-Z-SL | 0.161 м² | 825 мм | 820 мм | 325 мм | 320 мм | 33 | 83 | Сталь_RAL9016 (INPLAST) | скрытые защелки |
| STWS-825х350-Z-SL | 0.174 м² | 825 мм | 820 мм | 350 мм | 345 мм | 35 | 83 | Сталь_RAL9016 (INPLAST) | скрытые защелки |
| STWS-825х400-Z-SL | 0.199 м² | 825 мм | 820 мм | 400 мм | 395 мм | 40 | 83 | Сталь_RAL9016 (INPLAST) | скрытые защелки |
| STWS-825х425-Z-SL | 0.211 м² | 825 мм | 820 мм | 425 мм | 420 мм | 43 | 83 | Сталь_RAL9016 (INPLAST) | скрытые защелки |
| STWS-825х450-Z-SL | 0.223 м² | 825 мм | 820 мм | 450 мм | 445 мм | 45 | 83 | Сталь_RAL9016 (INPLAST) | скрытые защелки |
| STWS-825х500-Z-SL | 0.248 м² | 825 мм | 820 мм | 500 мм | 495 мм | 50 | 83 | Сталь_RAL9016 (INPLAST) | скрытые защелки |
| STWS-825х525-Z-SL | 0.261 м² | 825 мм | 820 мм | 525 мм | 520 мм | 53 | 83 | Сталь_RAL9016 (INPLAST) | скрытые защелки |
| STWS-825х550-Z-SL | 0.273 м² | 825 мм | 820 мм | 550 мм | 545 мм | 55 | 83 | Сталь_RAL9016 (INPLAST) | скрытые защелки |
| STWS-825х600-Z-SL | 0.298 м² | 825 мм | 820 мм | 600 мм | 595 мм | 60 | 83 | Сталь_RAL9016 (INPLAST) | скрытые защелки |
| STWS-825х625-Z-SL | 0.310 м² | 825 мм | 820 мм | 625 мм | 620 мм | 63 | 83 | Сталь_RAL9016 (INPLAST) | скрытые защелки |
| STWS-825х650-Z-SL | 0.323 м² | 825 мм | 820 мм | 650 мм | 645 мм | 65 | 83 | Сталь_RAL9016 (INPLAST) | скрытые защелки |
| STWS-850х100-Z-SL | 0.051 м² | 850 мм | 845 мм | 100 мм | 95 мм | 10 | 85 | Сталь_RAL9016 (INPLAST) | скрытые защелки |
| STWS-850х125-Z-SL | 0.064 м² | 850 мм | 845 мм | 125 мм | 120 мм | 13 | 85 | Сталь_RAL9016 (INPLAST) | скрытые защелки |
| STWS-850х150-Z-SL | 0.077 м² | 850 мм | 845 мм | 150 мм | 145 мм | 15 | 85 | Сталь_RAL9016 (INPLAST) | скрытые защелки |
| STWS-850х200-Z-SL | 0.102 м² | 850 мм | 845 мм | 200 мм | 195 мм | 20 | 85 | Сталь_RAL9016 (INPLAST) | скрытые защелки |
| STWS-850х225-Z-SL | 0.115 м² | 850 мм | 845 мм | 225 мм | 220 мм | 23 | 85 | Сталь_RAL9016 (INPLAST) | скрытые защелки |
| STWS-850х250-Z-SL | 0.128 м² | 850 мм | 845 мм | 250 мм | 245 мм | 25 | 85 | Сталь_RAL9016 (INPLAST) | скрытые защелки |
| STWS-850х300-Z-SL | 0.153 м² | 850 мм | 845 мм | 300 мм | 295 мм | 30 | 85 | Сталь_RAL9016 (INPLAST) | скрытые защелки |
| STWS-850х325-Z-SL | 0.166 м² | 850 мм | 845 мм | 325 мм | 320 мм | 33 | 85 | Сталь_RAL9016 (INPLAST) | скрытые защелки |
| STWS-850х350-Z-SL | 0.179 м² | 850 мм | 845 мм | 350 мм | 345 мм | 35 | 85 | Сталь_RAL9016 (INPLAST) | скрытые защелки |
| STWS-850х400-Z-SL | 0.205 м² | 850 мм | 845 мм | 400 мм | 395 мм | 40 | 85 | Сталь_RAL9016 (INPLAST) | скрытые защелки |
| STWS-850х425-Z-SL | 0.217 м² | 850 мм | 845 мм | 425 мм | 420 мм | 43 | 85 | Сталь_RAL9016 (INPLAST) | скрытые защелки |
| STWS-850х450-Z-SL | 0.230 м² | 850 мм | 845 мм | 450 мм | 445 мм | 45 | 85 | Сталь_RAL9016 (INPLAST) | скрытые защелки |
| STWS-850х500-Z-SL | 0.256 м² | 850 мм | 845 мм | 500 мм | 495 мм | 50 | 85 | Сталь_RAL9016 (INPLAST) | скрытые защелки |
| STWS-850х525-Z-SL | 0.268 м² | 850 мм | 845 мм | 525 мм | 520 мм | 53 | 85 | Сталь_RAL9016 (INPLAST) | скрытые защелки |
| STWS-850х550-Z-SL | 0.281 м² | 850 мм | 845 мм | 550 мм | 545 мм | 55 | 85 | Сталь_RAL9016 (INPLAST) | скрытые защелки |
| STWS-850х600-Z-SL | 0.307 м² | 850 мм | 845 мм | 600 мм | 595 мм | 60 | 85 | Сталь_RAL9016 (INPLAST) | скрытые защелки |
| STWS-850х625-Z-SL | 0.320 м² | 850 мм | 845 мм | 625 мм | 620 мм | 63 | 85 | Сталь_RAL9016 (INPLAST) | скрытые защелки |
| STWS-850х650-Z-SL | 0.332 м² | 850 мм | 845 мм | 650 мм | 645 мм | 65 | 85 | Сталь_RAL9016 (INPLAST) | скрытые защелки |
| STWS-900х100-Z-SL | 0.054 м² | 900 мм | 895 мм | 100 мм | 95 мм | 10 | 90 | Сталь_RAL9016 (INPLAST) | скрытые защелки |
| STWS-900х125-Z-SL | 0.068 м² | 900 мм | 895 мм | 125 мм | 120 мм | 13 | 90 | Сталь_RAL9016 (INPLAST) | скрытые защелки |
| STWS-900х150-Z-SL | 0.081 м² | 900 мм | 895 мм | 150 мм | 145 мм | 15 | 90 | Сталь_RAL9016 (INPLAST) | скрытые защелки |
| STWS-900х200-Z-SL | 0.108 м² | 900 мм | 895 мм | 200 мм | 195 мм | 20 | 90 | Сталь_RAL9016 (INPLAST) | скрытые защелки |
| STWS-900х225-Z-SL | 0.122 м² | 900 мм | 895 мм | 225 мм | 220 мм | 23 | 90 | Сталь_RAL9016 (INPLAST) | скрытые защелки |
| STWS-900х250-Z-SL | 0.135 м² | 900 мм | 895 мм | 250 мм | 245 мм | 25 | 90 | Сталь_RAL9016 (INPLAST) | скрытые защелки |
| STWS-900х300-Z-SL | 0.162 м² | 900 мм | 895 мм | 300 мм | 295 мм | 30 | 90 | Сталь_RAL9016 (INPLAST) | скрытые защелки |
| STWS-900х325-Z-SL | 0.176 м² | 900 мм | 895 мм | 325 мм | 320 мм | 33 | 90 | Сталь_RAL9016 (INPLAST) | скрытые защелки |
| STWS-900х350-Z-SL | 0.190 м² | 900 мм | 895 мм | 350 мм | 345 мм | 35 | 90 | Сталь_RAL9016 (INPLAST) | скрытые защелки |
| STWS-900х400-Z-SL | 0.217 м² | 900 мм | 895 мм | 400 мм | 395 мм | 40 | 90 | Сталь_RAL9016 (INPLAST) | скрытые защелки |
| STWS-900х425-Z-SL | 0.230 м² | 900 мм | 895 мм | 425 мм | 420 мм | 43 | 90 | Сталь_RAL9016 (INPLAST) | скрытые защелки |
| STWS-900х450-Z-SL | 0.244 м² | 900 мм | 895 мм | 450 мм | 445 мм | 45 | 90 | Сталь_RAL9016 (INPLAST) | скрытые защелки |
| STWS-900х500-Z-SL | 0.271 м² | 900 мм | 895 мм | 500 мм | 495 мм | 50 | 90 | Сталь_RAL9016 (INPLAST) | скрытые защелки |
| STWS-900х525-Z-SL | 0.284 м² | 900 мм | 895 мм | 525 мм | 520 мм | 53 | 90 | Сталь_RAL9016 (INPLAST) | скрытые защелки |
| STWS-900х550-Z-SL | 0.298 м² | 900 мм | 895 мм | 550 мм | 545 мм | 55 | 90 | Сталь_RAL9016 (INPLAST) | скрытые защелки |
| STWS-900х600-Z-SL | 0.325 м² | 900 мм | 895 мм | 600 мм | 595 мм | 60 | 90 | Сталь_RAL9016 (INPLAST) | скрытые защелки |
| STWS-900х625-Z-SL | 0.338 м² | 900 мм | 895 мм | 625 мм | 620 мм | 63 | 90 | Сталь_RAL9016 (INPLAST) | скрытые защелки |
| STWS-900х650-Z-SL | 0.352 м² | 900 мм | 895 мм | 650 мм | 645 мм | 65 | 90 | Сталь_RAL9016 (INPLAST) | скрытые защелки |
| STWS-925х100-Z-SL | 0.056 м² | 925 мм | 920 мм | 100 мм | 95 мм | 10 | 93 | Сталь_RAL9016 (INPLAST) | скрытые защелки |
| STWS-925х125-Z-SL | 0.070 м² | 925 мм | 920 мм | 125 мм | 120 мм | 13 | 93 | Сталь_RAL9016 (INPLAST) | скрытые защелки |
| STWS-925х150-Z-SL | 0.083 м² | 925 мм | 920 мм | 150 мм | 145 мм | 15 | 93 | Сталь_RAL9016 (INPLAST) | скрытые защелки |
| STWS-925х200-Z-SL | 0.111 м² | 925 мм | 920 мм | 200 мм | 195 мм | 20 | 93 | Сталь_RAL9016 (INPLAST) | скрытые защелки |
| STWS-925х225-Z-SL | 0.125 м² | 925 мм | 920 мм | 225 мм | 220 мм | 23 | 93 | Сталь_RAL9016 (INPLAST) | скрытые защелки |
| STWS-925х250-Z-SL | 0.139 м² | 925 мм | 920 мм | 250 мм | 245 мм | 25 | 93 | Сталь_RAL9016 (INPLAST) | скрытые защелки |
| STWS-925х300-Z-SL | 0.167 м² | 925 мм | 920 мм | 300 мм | 295 мм | 30 | 93 | Сталь_RAL9016 (INPLAST) | скрытые защелки |
| STWS-925х325-Z-SL | 0.181 м² | 925 мм | 920 мм | 325 мм | 320 мм | 33 | 93 | Сталь_RAL9016 (INPLAST) | скрытые защелки |
| STWS-925х350-Z-SL | 0.195 м² | 925 мм | 920 мм | 350 мм | 345 мм | 35 | 93 | Сталь_RAL9016 (INPLAST) | скрытые защелки |
| STWS-925х400-Z-SL | 0.223 м² | 925 мм | 920 мм | 400 мм | 395 мм | 40 | 93 | Сталь_RAL9016 (INPLAST) | скрытые защелки |
| STWS-925х425-Z-SL | 0.237 м² | 925 мм | 920 мм | 425 мм | 420 мм | 43 | 93 | Сталь_RAL9016 (INPLAST) | скрытые защелки |
| STWS-925х450-Z-SL | 0.250 м² | 925 мм | 920 мм | 450 мм | 445 мм | 45 | 93 | Сталь_RAL9016 (INPLAST) | скрытые защелки |
| STWS-925х500-Z-SL | 0.278 м² | 925 мм | 920 мм | 500 мм | 495 мм | 50 | 93 | Сталь_RAL9016 (INPLAST) | скрытые защелки |
| STWS-925х525-Z-SL | 0.292 м² | 925 мм | 920 мм | 525 мм | 520 мм | 53 | 93 | Сталь_RAL9016 (INPLAST) | скрытые защелки |
| STWS-925х550-Z-SL | 0.306 м² | 925 мм | 920 мм | 550 мм | 545 мм | 55 | 93 | Сталь_RAL9016 (INPLAST) | скрытые защелки |
| STWS-925х600-Z-SL | 0.334 м² | 925 мм | 920 мм | 600 мм | 595 мм | 60 | 93 | Сталь_RAL9016 (INPLAST) | скрытые защелки |
| STWS-925х625-Z-SL | 0.348 м² | 925 мм | 920 мм | 625 мм | 620 мм | 63 | 93 | Сталь_RAL9016 (INPLAST) | скрытые защелки |
| STWS-925х650-Z-SL | 0.362 м² | 925 мм | 920 мм | 650 мм | 645 мм | 65 | 93 | Сталь_RAL9016 (INPLAST) | скрытые защелки |
| STWS-950х100-Z-SL | 0.057 м² | 950 мм | 945 мм | 100 мм | 95 мм | 10 | 95 | Сталь_RAL9016 (INPLAST) | скрытые защелки |
| STWS-950х125-Z-SL | 0.071 м² | 950 мм | 945 мм | 125 мм | 120 мм | 13 | 95 | Сталь_RAL9016 (INPLAST) | скрытые защелки |
| STWS-950х150-Z-SL | 0.086 м² | 950 мм | 945 мм | 150 мм | 145 мм | 15 | 95 | Сталь_RAL9016 (INPLAST) | скрытые защелки |
| STWS-950х200-Z-SL | 0.114 м² | 950 мм | 945 мм | 200 мм | 195 мм | 20 | 95 | Сталь_RAL9016 (INPLAST) | скрытые защелки |
| STWS-950х225-Z-SL | 0.129 м² | 950 мм | 945 мм | 225 мм | 220 мм | 23 | 95 | Сталь_RAL9016 (INPLAST) | скрытые защелки |
| STWS-950х250-Z-SL | 0.143 м² | 950 мм | 945 мм | 250 мм | 245 мм | 25 | 95 | Сталь_RAL9016 (INPLAST) | скрытые защелки |
| STWS-950х300-Z-SL | 0.171 м² | 950 мм | 945 мм | 300 мм | 295 мм | 30 | 95 | Сталь_RAL9016 (INPLAST) | скрытые защелки |
| STWS-950х325-Z-SL | 0.186 м² | 950 мм | 945 мм | 325 мм | 320 мм | 33 | 95 | Сталь_RAL9016 (INPLAST) | скрытые защелки |
| STWS-950х350-Z-SL | 0.200 м² | 950 мм | 945 мм | 350 мм | 345 мм | 35 | 95 | Сталь_RAL9016 (INPLAST) | скрытые защелки |
| STWS-950х400-Z-SL | 0.229 м² | 950 мм | 945 мм | 400 мм | 395 мм | 40 | 95 | Сталь_RAL9016 (INPLAST) | скрытые защелки |
| STWS-950х425-Z-SL | 0.243 м² | 950 мм | 945 мм | 425 мм | 420 мм | 43 | 95 | Сталь_RAL9016 (INPLAST) | скрытые защелки |
| STWS-950х450-Z-SL | 0.257 м² | 950 мм | 945 мм | 450 мм | 445 мм | 45 | 95 | Сталь_RAL9016 (INPLAST) | скрытые защелки |
| STWS-950х500-Z-SL | 0.286 м² | 950 мм | 945 мм | 500 мм | 495 мм | 50 | 95 | Сталь_RAL9016 (INPLAST) | скрытые защелки |
| STWS-950х525-Z-SL | 0.300 м² | 950 мм | 945 мм | 525 мм | 520 мм | 53 | 95 | Сталь_RAL9016 (INPLAST) | скрытые защелки |
| STWS-950х550-Z-SL | 0.314 м² | 950 мм | 945 мм | 550 мм | 545 мм | 55 | 95 | Сталь_RAL9016 (INPLAST) | скрытые защелки |
| STWS-950х600-Z-SL | 0.343 м² | 950 мм | 945 мм | 600 мм | 595 мм | 60 | 95 | Сталь_RAL9016 (INPLAST) | скрытые защелки |
| STWS-950х625-Z-SL | 0.357 м² | 950 мм | 945 мм | 625 мм | 620 мм | 63 | 95 | Сталь_RAL9016 (INPLAST) | скрытые защелки |
| STWS-950х650-Z-SL | 0.371 м² | 950 мм | 945 мм | 650 мм | 645 мм | 65 | 95 | Сталь_RAL9016 (INPLAST) | скрытые защелки |
| STWS-1000х100-Z-SL | 0.060 м² | 1000 мм | 995 мм | 100 мм | 95 мм | 10 | 100 | Сталь_RAL9016 (INPLAST) | скрытые защелки |
| STWS-1000х125-Z-SL | 0.075 м² | 1000 мм | 995 мм | 125 мм | 120 мм | 13 | 100 | Сталь_RAL9016 (INPLAST) | скрытые защелки |
| STWS-1000х150-Z-SL | 0.090 м² | 1000 мм | 995 мм | 150 мм | 145 мм | 15 | 100 | Сталь_RAL9016 (INPLAST) | скрытые защелки |
| STWS-1000х200-Z-SL | 0.120 м² | 1000 мм | 995 мм | 200 мм | 195 мм | 20 | 100 | Сталь_RAL9016 (INPLAST) | скрытые защелки |
| STWS-1000х225-Z-SL | 0.135 м² | 1000 мм | 995 мм | 225 мм | 220 мм | 23 | 100 | Сталь_RAL9016 (INPLAST) | скрытые защелки |
| STWS-1000х250-Z-SL | 0.150 м² | 1000 мм | 995 мм | 250 мм | 245 мм | 25 | 100 | Сталь_RAL9016 (INPLAST) | скрытые защелки |
| STWS-1000х300-Z-SL | 0.180 м² | 1000 мм | 995 мм | 300 мм | 295 мм | 30 | 100 | Сталь_RAL9016 (INPLAST) | скрытые защелки |
| STWS-1000х325-Z-SL | 0.196 м² | 1000 мм | 995 мм | 325 мм | 320 мм | 33 | 100 | Сталь_RAL9016 (INPLAST) | скрытые защелки |
| STWS-1000х350-Z-SL | 0.211 м² | 1000 мм | 995 мм | 350 мм | 345 мм | 35 | 100 | Сталь_RAL9016 (INPLAST) | скрытые защелки |
| STWS-1000х400-Z-SL | 0.241 м² | 1000 мм | 995 мм | 400 мм | 395 мм | 40 | 100 | Сталь_RAL9016 (INPLAST) | скрытые защелки |
| STWS-1000х425-Z-SL | 0.256 м² | 1000 мм | 995 мм | 425 мм | 420 мм | 43 | 100 | Сталь_RAL9016 (INPLAST) | скрытые защелки |
| STWS-1000х450-Z-SL | 0.271 м² | 1000 мм | 995 мм | 450 мм | 445 мм | 45 | 100 | Сталь_RAL9016 (INPLAST) | скрытые защелки |
| STWS-1000х500-Z-SL | 0.301 м² | 1000 мм | 995 мм | 500 мм | 495 мм | 50 | 100 | Сталь_RAL9016 (INPLAST) | скрытые защелки |
| STWS-1000х525-Z-SL | 0.316 м² | 1000 мм | 995 мм | 525 мм | 520 мм | 53 | 100 | Сталь_RAL9016 (INPLAST) | скрытые защелки |
| STWS-1000х550-Z-SL | 0.331 м² | 1000 мм | 995 мм | 550 мм | 545 мм | 55 | 100 | Сталь_RAL9016 (INPLAST) | скрытые защелки |
| STWS-1000х600-Z-SL | 0.361 м² | 1000 мм | 995 мм | 600 мм | 595 мм | 60 | 100 | Сталь_RAL9016 (INPLAST) | скрытые защелки |
| STWS-1000х625-Z-SL | 0.376 м² | 1000 мм | 995 мм | 625 мм | 620 мм | 63 | 100 | Сталь_RAL9016 (INPLAST) | скрытые защелки |
| STWS-1000х650-Z-SL | 0.391 м² | 1000 мм | 995 мм | 650 мм | 645 мм | 65 | 100 | Сталь_RAL9016 (INPLAST) | скрытые защелки |
| STWS-1025х100-Z-SL | 0.062 м² | 1025 мм | 1020 мм | 100 мм | 95 мм | 10 | 103 | Сталь_RAL9016 (INPLAST) | скрытые защелки |
| STWS-1025х125-Z-SL | 0.077 м² | 1025 мм | 1020 мм | 125 мм | 120 мм | 13 | 103 | Сталь_RAL9016 (INPLAST) | скрытые защелки |
| STWS-1025х150-Z-SL | 0.092 м² | 1025 мм | 1020 мм | 150 мм | 145 мм | 15 | 103 | Сталь_RAL9016 (INPLAST) | скрытые защелки |
| STWS-1025х200-Z-SL | 0.123 м² | 1025 мм | 1020 мм | 200 мм | 195 мм | 20 | 103 | Сталь_RAL9016 (INPLAST) | скрытые защелки |
| STWS-1025х225-Z-SL | 0.139 м² | 1025 мм | 1020 мм | 225 мм | 220 мм | 23 | 103 | Сталь_RAL9016 (INPLAST) | скрытые защелки |
| STWS-1025х250-Z-SL | 0.154 м² | 1025 мм | 1020 мм | 250 мм | 245 мм | 25 | 103 | Сталь_RAL9016 (INPLAST) | скрытые защелки |
| STWS-1025х300-Z-SL | 0.185 м² | 1025 мм | 1020 мм | 300 мм | 295 мм | 30 | 103 | Сталь_RAL9016 (INPLAST) | скрытые защелки |
| STWS-1025х325-Z-SL | 0.200 м² | 1025 мм | 1020 мм | 325 мм | 320 мм | 33 | 103 | Сталь_RAL9016 (INPLAST) | скрытые защелки |
| STWS-1025х350-Z-SL | 0.216 м² | 1025 мм | 1020 мм | 350 мм | 345 мм | 35 | 103 | Сталь_RAL9016 (INPLAST) | скрытые защелки |
| STWS-1025х400-Z-SL | 0.247 м² | 1025 мм | 1020 мм | 400 мм | 395 мм | 40 | 103 | Сталь_RAL9016 (INPLAST) | скрытые защелки |
| STWS-1025х425-Z-SL | 0.262 м² | 1025 мм | 1020 мм | 425 мм | 420 мм | 43 | 103 | Сталь_RAL9016 (INPLAST) | скрытые защелки |
| STWS-1025х450-Z-SL | 0.277 м² | 1025 мм | 1020 мм | 450 мм | 445 мм | 45 | 103 | Сталь_RAL9016 (INPLAST) | скрытые защелки |
| STWS-1025х500-Z-SL | 0.308 м² | 1025 мм | 1020 мм | 500 мм | 495 мм | 50 | 103 | Сталь_RAL9016 (INPLAST) | скрытые защелки |
| STWS-1025х525-Z-SL | 0.324 м² | 1025 мм | 1020 мм | 525 мм | 520 мм | 53 | 103 | Сталь_RAL9016 (INPLAST) | скрытые защелки |
| STWS-1025х550-Z-SL | 0.339 м² | 1025 мм | 1020 мм | 550 мм | 545 мм | 55 | 103 | Сталь_RAL9016 (INPLAST) | скрытые защелки |
| STWS-1025х600-Z-SL | 0.370 м² | 1025 мм | 1020 мм | 600 мм | 595 мм | 60 | 103 | Сталь_RAL9016 (INPLAST) | скрытые защелки |
| STWS-1025х625-Z-SL | 0.385 м² | 1025 мм | 1020 мм | 625 мм | 620 мм | 63 | 103 | Сталь_RAL9016 (INPLAST) | скрытые защелки |
| STWS-1025х650-Z-SL | 0.401 м² | 1025 мм | 1020 мм | 650 мм | 645 мм | 65 | 103 | Сталь_RAL9016 (INPLAST) | скрытые защелки |
| STWS-1050х100-Z-SL | 0.063 м² | 1050 мм | 1045 мм | 100 мм | 95 мм | 10 | 105 | Сталь_RAL9016 (INPLAST) | скрытые защелки |
| STWS-1050х125-Z-SL | 0.079 м² | 1050 мм | 1045 мм | 125 мм | 120 мм | 13 | 105 | Сталь_RAL9016 (INPLAST) | скрытые защелки |
| STWS-1050х150-Z-SL | 0.095 м² | 1050 мм | 1045 мм | 150 мм | 145 мм | 15 | 105 | Сталь_RAL9016 (INPLAST) | скрытые защелки |
| STWS-1050х200-Z-SL | 0.126 м² | 1050 мм | 1045 мм | 200 мм | 195 мм | 20 | 105 | Сталь_RAL9016 (INPLAST) | скрытые защелки |
| STWS-1050х225-Z-SL | 0.142 м² | 1050 мм | 1045 мм | 225 мм | 220 мм | 23 | 105 | Сталь_RAL9016 (INPLAST) | скрытые защелки |
| STWS-1050х250-Z-SL | 0.158 м² | 1050 мм | 1045 мм | 250 мм | 245 мм | 25 | 105 | Сталь_RAL9016 (INPLAST) | скрытые защелки |
| STWS-1050х300-Z-SL | 0.190 м² | 1050 мм | 1045 мм | 300 мм | 295 мм | 30 | 105 | Сталь_RAL9016 (INPLAST) | скрытые защелки |
| STWS-1050х325-Z-SL | 0.205 м² | 1050 мм | 1045 мм | 325 мм | 320 мм | 33 | 105 | Сталь_RAL9016 (INPLAST) | скрытые защелки |
| STWS-1050х350-Z-SL | 0.221 м² | 1050 мм | 1045 мм | 350 мм | 345 мм | 35 | 105 | Сталь_RAL9016 (INPLAST) | скрытые защелки |
| STWS-1050х400-Z-SL | 0.253 м² | 1050 мм | 1045 мм | 400 мм | 395 мм | 40 | 105 | Сталь_RAL9016 (INPLAST) | скрытые защелки |
| STWS-1050х425-Z-SL | 0.268 м² | 1050 мм | 1045 мм | 425 мм | 420 мм | 43 | 105 | Сталь_RAL9016 (INPLAST) | скрытые защелки |
| STWS-1050х450-Z-SL | 0.284 м² | 1050 мм | 1045 мм | 450 мм | 445 мм | 45 | 105 | Сталь_RAL9016 (INPLAST) | скрытые защелки |
| STWS-1050х500-Z-SL | 0.316 м² | 1050 мм | 1045 мм | 500 мм | 495 мм | 50 | 105 | Сталь_RAL9016 (INPLAST) | скрытые защелки |
| STWS-1050х525-Z-SL | 0.332 м² | 1050 мм | 1045 мм | 525 мм | 520 мм | 53 | 105 | Сталь_RAL9016 (INPLAST) | скрытые защелки |
| STWS-1050х550-Z-SL | 0.347 м² | 1050 мм | 1045 мм | 550 мм | 545 мм | 55 | 105 | Сталь_RAL9016 (INPLAST) | скрытые защелки |
| STWS-1050х600-Z-SL | 0.379 м² | 1050 мм | 1045 мм | 600 мм | 595 мм | 60 | 105 | Сталь_RAL9016 (INPLAST) | скрытые защелки |
| STWS-1050х625-Z-SL | 0.395 м² | 1050 мм | 1045 мм | 625 мм | 620 мм | 63 | 105 | Сталь_RAL9016 (INPLAST) | скрытые защелки |
| STWS-1050х650-Z-SL | 0.411 м² | 1050 мм | 1045 мм | 650 мм | 645 мм | 65 | 105 | Сталь_RAL9016 (INPLAST) | скрытые защелки |
| STWS-1100х100-Z-SL | 0.066 м² | 1100 мм | 1095 мм | 100 мм | 95 мм | 10 | 110 | Сталь_RAL9016 (INPLAST) | скрытые защелки |
| STWS-1100х125-Z-SL | 0.083 м² | 1100 мм | 1095 мм | 125 мм | 120 мм | 13 | 110 | Сталь_RAL9016 (INPLAST) | скрытые защелки |
| STWS-1100х150-Z-SL | 0.099 м² | 1100 мм | 1095 мм | 150 мм | 145 мм | 15 | 110 | Сталь_RAL9016 (INPLAST) | скрытые защелки |
| STWS-1100х200-Z-SL | 0.132 м² | 1100 мм | 1095 мм | 200 мм | 195 мм | 20 | 110 | Сталь_RAL9016 (INPLAST) | скрытые защелки |
| STWS-1100х225-Z-SL | 0.149 м² | 1100 мм | 1095 мм | 225 мм | 220 мм | 23 | 110 | Сталь_RAL9016 (INPLAST) | скрытые защелки |
| STWS-1100х250-Z-SL | 0.165 м² | 1100 мм | 1095 мм | 250 мм | 245 мм | 25 | 110 | Сталь_RAL9016 (INPLAST) | скрытые защелки |
| STWS-1100х300-Z-SL | 0.199 м² | 1100 мм | 1095 мм | 300 мм | 295 мм | 30 | 110 | Сталь_RAL9016 (INPLAST) | скрытые защелки |
| STWS-1100х325-Z-SL | 0.215 м² | 1100 мм | 1095 мм | 325 мм | 320 мм | 33 | 110 | Сталь_RAL9016 (INPLAST) | скрытые защелки |
| STWS-1100х350-Z-SL | 0.232 м² | 1100 мм | 1095 мм | 350 мм | 345 мм | 35 | 110 | Сталь_RAL9016 (INPLAST) | скрытые защелки |
| STWS-1100х400-Z-SL | 0.265 м² | 1100 мм | 1095 мм | 400 мм | 395 мм | 40 | 110 | Сталь_RAL9016 (INPLAST) | скрытые защелки |
| STWS-1100х425-Z-SL | 0.281 м² | 1100 мм | 1095 мм | 425 мм | 420 мм | 43 | 110 | Сталь_RAL9016 (INPLAST) | скрытые защелки |
| STWS-1100х450-Z-SL | 0.298 м² | 1100 мм | 1095 мм | 450 мм | 445 мм | 45 | 110 | Сталь_RAL9016 (INPLAST) | скрытые защелки |
| STWS-1100х500-Z-SL | 0.331 м² | 1100 мм | 1095 мм | 500 мм | 495 мм | 50 | 110 | Сталь_RAL9016 (INPLAST) | скрытые защелки |
| STWS-1100х525-Z-SL | 0.347 м² | 1100 мм | 1095 мм | 525 мм | 520 мм | 53 | 110 | Сталь_RAL9016 (INPLAST) | скрытые защелки |
| STWS-1100х550-Z-SL | 0.364 м² | 1100 мм | 1095 мм | 550 мм | 545 мм | 55 | 110 | Сталь_RAL9016 (INPLAST) | скрытые защелки |
| STWS-1100х600-Z-SL | 0.397 м² | 1100 мм | 1095 мм | 600 мм | 595 мм | 60 | 110 | Сталь_RAL9016 (INPLAST) | скрытые защелки |
| STWS-1100х625-Z-SL | 0.414 м² | 1100 мм | 1095 мм | 625 мм | 620 мм | 63 | 110 | Сталь_RAL9016 (INPLAST) | скрытые защелки |
| STWS-1100х650-Z-SL | 0.430 м² | 1100 мм | 1095 мм | 650 мм | 645 мм | 65 | 110 | Сталь_RAL9016 (INPLAST) | скрытые защелки |
| STWS-1125х100-Z-SL | 0.068 м² | 1125 мм | 1120 мм | 100 мм | 95 мм | 10 | 113 | Сталь_RAL9016 (INPLAST) | скрытые защелки |
| STWS-1125х125-Z-SL | 0.085 м² | 1125 мм | 1120 мм | 125 мм | 120 мм | 13 | 113 | Сталь_RAL9016 (INPLAST) | скрытые защелки |
| STWS-1125х150-Z-SL | 0.102 м² | 1125 мм | 1120 мм | 150 мм | 145 мм | 15 | 113 | Сталь_RAL9016 (INPLAST) | скрытые защелки |
| STWS-1125х200-Z-SL | 0.135 м² | 1125 мм | 1120 мм | 200 мм | 195 мм | 20 | 113 | Сталь_RAL9016 (INPLAST) | скрытые защелки |
| STWS-1125х225-Z-SL | 0.152 м² | 1125 мм | 1120 мм | 225 мм | 220 мм | 23 | 113 | Сталь_RAL9016 (INPLAST) | скрытые защелки |
| STWS-1125х250-Z-SL | 0.169 м² | 1125 мм | 1120 мм | 250 мм | 245 мм | 25 | 113 | Сталь_RAL9016 (INPLAST) | скрытые защелки |
| STWS-1125х300-Z-SL | 0.203 м² | 1125 мм | 1120 мм | 300 мм | 295 мм | 30 | 113 | Сталь_RAL9016 (INPLAST) | скрытые защелки |
| STWS-1125х325-Z-SL | 0.220 м² | 1125 мм | 1120 мм | 325 мм | 320 мм | 33 | 113 | Сталь_RAL9016 (INPLAST) | скрытые защелки |
| STWS-1125х350-Z-SL | 0.237 м² | 1125 мм | 1120 мм | 350 мм | 345 мм | 35 | 113 | Сталь_RAL9016 (INPLAST) | скрытые защелки |
| STWS-1125х400-Z-SL | 0.271 м² | 1125 мм | 1120 мм | 400 мм | 395 мм | 40 | 113 | Сталь_RAL9016 (INPLAST) | скрытые защелки |
| STWS-1125х425-Z-SL | 0.288 м² | 1125 мм | 1120 мм | 425 мм | 420 мм | 43 | 113 | Сталь_RAL9016 (INPLAST) | скрытые защелки |
| STWS-1125х450-Z-SL | 0.305 м² | 1125 мм | 1120 мм | 450 мм | 445 мм | 45 | 113 | Сталь_RAL9016 (INPLAST) | скрытые защелки |
| STWS-1125х500-Z-SL | 0.338 м² | 1125 мм | 1120 мм | 500 мм | 495 мм | 50 | 113 | Сталь_RAL9016 (INPLAST) | скрытые защелки |
| STWS-1125х525-Z-SL | 0.355 м² | 1125 мм | 1120 мм | 525 мм | 520 мм | 53 | 113 | Сталь_RAL9016 (INPLAST) | скрытые защелки |
| STWS-1125х550-Z-SL | 0.372 м² | 1125 мм | 1120 мм | 550 мм | 545 мм | 55 | 113 | Сталь_RAL9016 (INPLAST) | скрытые защелки |
| STWS-1125х600-Z-SL | 0.406 м² | 1125 мм | 1120 мм | 600 мм | 595 мм | 60 | 113 | Сталь_RAL9016 (INPLAST) | скрытые защелки |
| STWS-1125х625-Z-SL | 0.423 м² | 1125 мм | 1120 мм | 625 мм | 620 мм | 63 | 113 | Сталь_RAL9016 (INPLAST) | скрытые защелки |
| STWS-1125х650-Z-SL | 0.440 м² | 1125 мм | 1120 мм | 650 мм | 645 мм | 65 | 113 | Сталь_RAL9016 (INPLAST) | скрытые защелки |
| STWS-1150х100-Z-SL | 0.069 м² | 1150 мм | 1145 мм | 100 мм | 95 мм | 10 | 115 | Сталь_RAL9016 (INPLAST) | скрытые защелки |
| STWS-1150х125-Z-SL | 0.086 м² | 1150 мм | 1145 мм | 125 мм | 120 мм | 13 | 115 | Сталь_RAL9016 (INPLAST) | скрытые защелки |
| STWS-1150х150-Z-SL | 0.104 м² | 1150 мм | 1145 мм | 150 мм | 145 мм | 15 | 115 | Сталь_RAL9016 (INPLAST) | скрытые защелки |
| STWS-1150х200-Z-SL | 0.138 м² | 1150 мм | 1145 мм | 200 мм | 195 мм | 20 | 115 | Сталь_RAL9016 (INPLAST) | скрытые защелки |
| STWS-1150х225-Z-SL | 0.156 м² | 1150 мм | 1145 мм | 225 мм | 220 мм | 23 | 115 | Сталь_RAL9016 (INPLAST) | скрытые защелки |
| STWS-1150х250-Z-SL | 0.173 м² | 1150 мм | 1145 мм | 250 мм | 245 мм | 25 | 115 | Сталь_RAL9016 (INPLAST) | скрытые защелки |
| STWS-1150х300-Z-SL | 0.208 м² | 1150 мм | 1145 мм | 300 мм | 295 мм | 30 | 115 | Сталь_RAL9016 (INPLAST) | скрытые защелки |
| STWS-1150х325-Z-SL | 0.225 м² | 1150 мм | 1145 мм | 325 мм | 320 мм | 33 | 115 | Сталь_RAL9016 (INPLAST) | скрытые защелки |
| STWS-1150х350-Z-SL | 0.242 м² | 1150 мм | 1145 мм | 350 мм | 345 мм | 35 | 115 | Сталь_RAL9016 (INPLAST) | скрытые защелки |
| STWS-1150х400-Z-SL | 0.277 м² | 1150 мм | 1145 мм | 400 мм | 395 мм | 40 | 115 | Сталь_RAL9016 (INPLAST) | скрытые защелки |
| STWS-1150х425-Z-SL | 0.294 м² | 1150 мм | 1145 мм | 425 мм | 420 мм | 43 | 115 | Сталь_RAL9016 (INPLAST) | скрытые защелки |
| STWS-1150х450-Z-SL | 0.311 м² | 1150 мм | 1145 мм | 450 мм | 445 мм | 45 | 115 | Сталь_RAL9016 (INPLAST) | скрытые защелки |
| STWS-1150х500-Z-SL | 0.346 м² | 1150 мм | 1145 мм | 500 мм | 495 мм | 50 | 115 | Сталь_RAL9016 (INPLAST) | скрытые защелки |
| STWS-1150х525-Z-SL | 0.363 м² | 1150 мм | 1145 мм | 525 мм | 520 мм | 53 | 115 | Сталь_RAL9016 (INPLAST) | скрытые защелки |
| STWS-1150х550-Z-SL | 0.381 м² | 1150 мм | 1145 мм | 550 мм | 545 мм | 55 | 115 | Сталь_RAL9016 (INPLAST) | скрытые защелки |
| STWS-1150х600-Z-SL | 0.415 м² | 1150 мм | 1145 мм | 600 мм | 595 мм | 60 | 115 | Сталь_RAL9016 (INPLAST) | скрытые защелки |
| STWS-1150х625-Z-SL | 0.432 м² | 1150 мм | 1145 мм | 625 мм | 620 мм | 63 | 115 | Сталь_RAL9016 (INPLAST) | скрытые защелки |
| STWS-1150х650-Z-SL | 0.450 м² | 1150 мм | 1145 мм | 650 мм | 645 мм | 65 | 115 | Сталь_RAL9016 (INPLAST) | скрытые защелки |
| STWS-1200х100-Z-SL | 0.072 м² | 1200 мм | 1195 мм | 100 мм | 95 мм | 10 | 120 | Сталь_RAL9016 (INPLAST) | скрытые защелки |
| STWS-1200х125-Z-SL | 0.090 м² | 1200 мм | 1195 мм | 125 мм | 120 мм | 13 | 120 | Сталь_RAL9016 (INPLAST) | скрытые защелки |
| STWS-1200х150-Z-SL | 0.108 м² | 1200 мм | 1195 мм | 150 мм | 145 мм | 15 | 120 | Сталь_RAL9016 (INPLAST) | скрытые защелки |
| STWS-1200х200-Z-SL | 0.144 м² | 1200 мм | 1195 мм | 200 мм | 195 мм | 20 | 120 | Сталь_RAL9016 (INPLAST) | скрытые защелки |
| STWS-1200х225-Z-SL | 0.162 м² | 1200 мм | 1195 мм | 225 мм | 220 мм | 23 | 120 | Сталь_RAL9016 (INPLAST) | скрытые защелки |
| STWS-1200х250-Z-SL | 0.180 м² | 1200 мм | 1195 мм | 250 мм | 245 мм | 25 | 120 | Сталь_RAL9016 (INPLAST) | скрытые защелки |
| STWS-1200х300-Z-SL | 0.217 м² | 1200 мм | 1195 мм | 300 мм | 295 мм | 30 | 120 | Сталь_RAL9016 (INPLAST) | скрытые защелки |
| STWS-1200х325-Z-SL | 0.235 м² | 1200 мм | 1195 мм | 325 мм | 320 мм | 33 | 120 | Сталь_RAL9016 (INPLAST) | скрытые защелки |
| STWS-1200х350-Z-SL | 0.253 м² | 1200 мм | 1195 мм | 350 мм | 345 мм | 35 | 120 | Сталь_RAL9016 (INPLAST) | скрытые защелки |
| STWS-1200х400-Z-SL | 0.289 м² | 1200 мм | 1195 мм | 400 мм | 395 мм | 40 | 120 | Сталь_RAL9016 (INPLAST) | скрытые защелки |
| STWS-1200х425-Z-SL | 0.307 м² | 1200 мм | 1195 мм | 425 мм | 420 мм | 43 | 120 | Сталь_RAL9016 (INPLAST) | скрытые защелки |
| STWS-1200х450-Z-SL | 0.325 м² | 1200 мм | 1195 мм | 450 мм | 445 мм | 45 | 120 | Сталь_RAL9016 (INPLAST) | скрытые защелки |
| STWS-1200х500-Z-SL | 0.361 м² | 1200 мм | 1195 мм | 500 мм | 495 мм | 50 | 120 | Сталь_RAL9016 (INPLAST) | скрытые защелки |
| STWS-1200х525-Z-SL | 0.379 м² | 1200 мм | 1195 мм | 525 мм | 520 мм | 53 | 120 | Сталь_RAL9016 (INPLAST) | скрытые защелки |
| STWS-1200х550-Z-SL | 0.397 м² | 1200 мм | 1195 мм | 550 мм | 545 мм | 55 | 120 | Сталь_RAL9016 (INPLAST) | скрытые защелки |
| STWS-1200х600-Z-SL | 0.433 м² | 1200 мм | 1195 мм | 600 мм | 595 мм | 60 | 120 | Сталь_RAL9016 (INPLAST) | скрытые защелки |
| STWS-1200х625-Z-SL | 0.451 м² | 1200 мм | 1195 мм | 625 мм | 620 мм | 63 | 120 | Сталь_RAL9016 (INPLAST) | скрытые защелки |
| STWS-1200х650-Z-SL | 0.469 м² | 1200 мм | 1195 мм | 650 мм | 645 мм | 65 | 120 | Сталь_RAL9016 (INPLAST) | скрытые защелки |
| STWS-1225х100-Z-SL | 0.074 м² | 1225 мм | 1220 мм | 100 мм | 95 мм | 10 | 123 | Сталь_RAL9016 (INPLAST) | скрытые защелки |
| STWS-1225х125-Z-SL | 0.092 м² | 1225 мм | 1220 мм | 125 мм | 120 мм | 13 | 123 | Сталь_RAL9016 (INPLAST) | скрытые защелки |
| STWS-1225х150-Z-SL | 0.111 м² | 1225 мм | 1220 мм | 150 мм | 145 мм | 15 | 123 | Сталь_RAL9016 (INPLAST) | скрытые защелки |
| STWS-1225х200-Z-SL | 0.147 м² | 1225 мм | 1220 мм | 200 мм | 195 мм | 20 | 123 | Сталь_RAL9016 (INPLAST) | скрытые защелки |
| STWS-1225х225-Z-SL | 0.166 м² | 1225 мм | 1220 мм | 225 мм | 220 мм | 23 | 123 | Сталь_RAL9016 (INPLAST) | скрытые защелки |
| STWS-1225х250-Z-SL | 0.184 м² | 1225 мм | 1220 мм | 250 мм | 245 мм | 25 | 123 | Сталь_RAL9016 (INPLAST) | скрытые защелки |
| STWS-1225х300-Z-SL | 0.221 м² | 1225 мм | 1220 мм | 300 мм | 295 мм | 30 | 123 | Сталь_RAL9016 (INPLAST) | скрытые защелки |
| STWS-1225х325-Z-SL | 0.240 м² | 1225 мм | 1220 мм | 325 мм | 320 мм | 33 | 123 | Сталь_RAL9016 (INPLAST) | скрытые защелки |
| STWS-1225х350-Z-SL | 0.258 м² | 1225 мм | 1220 мм | 350 мм | 345 мм | 35 | 123 | Сталь_RAL9016 (INPLAST) | скрытые защелки |
| STWS-1225х400-Z-SL | 0.295 м² | 1225 мм | 1220 мм | 400 мм | 395 мм | 40 | 123 | Сталь_RAL9016 (INPLAST) | скрытые защелки |
| STWS-1225х425-Z-SL | 0.313 м² | 1225 мм | 1220 мм | 425 мм | 420 мм | 43 | 123 | Сталь_RAL9016 (INPLAST) | скрытые защелки |
| STWS-1225х450-Z-SL | 0.332 м² | 1225 мм | 1220 мм | 450 мм | 445 мм | 45 | 123 | Сталь_RAL9016 (INPLAST) | скрытые защелки |
| STWS-1225х500-Z-SL | 0.368 м² | 1225 мм | 1220 мм | 500 мм | 495 мм | 50 | 123 | Сталь_RAL9016 (INPLAST) | скрытые защелки |
| STWS-1225х525-Z-SL | 0.387 м² | 1225 мм | 1220 мм | 525 мм | 520 мм | 53 | 123 | Сталь_RAL9016 (INPLAST) | скрытые защелки |
| STWS-1225х550-Z-SL | 0.405 м² | 1225 мм | 1220 мм | 550 мм | 545 мм | 55 | 123 | Сталь_RAL9016 (INPLAST) | скрытые защелки |
| STWS-1225х600-Z-SL | 0.442 м² | 1225 мм | 1220 мм | 600 мм | 595 мм | 60 | 123 | Сталь_RAL9016 (INPLAST) | скрытые защелки |
| STWS-1225х625-Z-SL | 0.461 м² | 1225 мм | 1220 мм | 625 мм | 620 мм | 63 | 123 | Сталь_RAL9016 (INPLAST) | скрытые защелки |
| STWS-1225х650-Z-SL | 0.479 м² | 1225 мм | 1220 мм | 650 мм | 645 мм | 65 | 123 | Сталь_RAL9016 (INPLAST) | скрытые защелки |
| STWS-1250х100-Z-SL | 0.075 м² | 1250 мм | 1245 мм | 100 мм | 95 мм | 10 | 125 | Сталь_RAL9016 (INPLAST) | скрытые защелки |
| STWS-1250х125-Z-SL | 0.094 м² | 1250 мм | 1245 мм | 125 мм | 120 мм | 13 | 125 | Сталь_RAL9016 (INPLAST) | скрытые защелки |
| STWS-1250х150-Z-SL | 0.113 м² | 1250 мм | 1245 мм | 150 мм | 145 мм | 15 | 125 | Сталь_RAL9016 (INPLAST) | скрытые защелки |
| STWS-1250х200-Z-SL | 0.150 м² | 1250 мм | 1245 мм | 200 мм | 195 мм | 20 | 125 | Сталь_RAL9016 (INPLAST) | скрытые защелки |
| STWS-1250х225-Z-SL | 0.169 м² | 1250 мм | 1245 мм | 225 мм | 220 мм | 23 | 125 | Сталь_RAL9016 (INPLAST) | скрытые защелки |
| STWS-1250х250-Z-SL | 0.188 м² | 1250 мм | 1245 мм | 250 мм | 245 мм | 25 | 125 | Сталь_RAL9016 (INPLAST) | скрытые защелки |
| STWS-1250х300-Z-SL | 0.226 м² | 1250 мм | 1245 мм | 300 мм | 295 мм | 30 | 125 | Сталь_RAL9016 (INPLAST) | скрытые защелки |
| STWS-1250х325-Z-SL | 0.244 м² | 1250 мм | 1245 мм | 325 мм | 320 мм | 33 | 125 | Сталь_RAL9016 (INPLAST) | скрытые защелки |
| STWS-1250х350-Z-SL | 0.263 м² | 1250 мм | 1245 мм | 350 мм | 345 мм | 35 | 125 | Сталь_RAL9016 (INPLAST) | скрытые защелки |
| STWS-1250х400-Z-SL | 0.301 м² | 1250 мм | 1245 мм | 400 мм | 395 мм | 40 | 125 | Сталь_RAL9016 (INPLAST) | скрытые защелки |
| STWS-1250х425-Z-SL | 0.320 м² | 1250 мм | 1245 мм | 425 мм | 420 мм | 43 | 125 | Сталь_RAL9016 (INPLAST) | скрытые защелки |
| STWS-1250х450-Z-SL | 0.338 м² | 1250 мм | 1245 мм | 450 мм | 445 мм | 45 | 125 | Сталь_RAL9016 (INPLAST) | скрытые защелки |
| STWS-1250х500-Z-SL | 0.376 м² | 1250 мм | 1245 мм | 500 мм | 495 мм | 50 | 125 | Сталь_RAL9016 (INPLAST) | скрытые защелки |
| STWS-1250х525-Z-SL | 0.395 м² | 1250 мм | 1245 мм | 525 мм | 520 мм | 53 | 125 | Сталь_RAL9016 (INPLAST) | скрытые защелки |
| STWS-1250х550-Z-SL | 0.414 м² | 1250 мм | 1245 мм | 550 мм | 545 мм | 55 | 125 | Сталь_RAL9016 (INPLAST) | скрытые защелки |
| STWS-1250х600-Z-SL | 0.451 м² | 1250 мм | 1245 мм | 600 мм | 595 мм | 60 | 125 | Сталь_RAL9016 (INPLAST) | скрытые защелки |
| STWS-1250х625-Z-SL | 0.470 м² | 1250 мм | 1245 мм | 625 мм | 620 мм | 63 | 125 | Сталь_RAL9016 (INPLAST) | скрытые защелки |
| STWS-1250х650-Z-SL | 0.489 м² | 1250 мм | 1245 мм | 650 мм | 645 мм | 65 | 125 | Сталь_RAL9016 (INPLAST) | скрытые защелки |
| STWS-1300х100-Z-SL | 0.078 м² | 1300 мм | 1295 мм | 100 мм | 95 мм | 10 | 130 | Сталь_RAL9016 (INPLAST) | скрытые защелки |
| STWS-1300х125-Z-SL | 0.098 м² | 1300 мм | 1295 мм | 125 мм | 120 мм | 13 | 130 | Сталь_RAL9016 (INPLAST) | скрытые защелки |
| STWS-1300х150-Z-SL | 0.117 м² | 1300 мм | 1295 мм | 150 мм | 145 мм | 15 | 130 | Сталь_RAL9016 (INPLAST) | скрытые защелки |
| STWS-1300х200-Z-SL | 0.156 м² | 1300 мм | 1295 мм | 200 мм | 195 мм | 20 | 130 | Сталь_RAL9016 (INPLAST) | скрытые защелки |
| STWS-1300х225-Z-SL | 0.176 м² | 1300 мм | 1295 мм | 225 мм | 220 мм | 23 | 130 | Сталь_RAL9016 (INPLAST) | скрытые защелки |
| STWS-1300х250-Z-SL | 0.196 м² | 1300 мм | 1295 мм | 250 мм | 245 мм | 25 | 130 | Сталь_RAL9016 (INPLAST) | скрытые защелки |
| STWS-1300х300-Z-SL | 0.235 м² | 1300 мм | 1295 мм | 300 мм | 295 мм | 30 | 130 | Сталь_RAL9016 (INPLAST) | скрытые защелки |
| STWS-1300х325-Z-SL | 0.254 м² | 1300 мм | 1295 мм | 325 мм | 320 мм | 33 | 130 | Сталь_RAL9016 (INPLAST) | скрытые защелки |
| STWS-1300х350-Z-SL | 0.274 м² | 1300 мм | 1295 мм | 350 мм | 345 мм | 35 | 130 | Сталь_RAL9016 (INPLAST) | скрытые защелки |
| STWS-1300х400-Z-SL | 0.313 м² | 1300 мм | 1295 мм | 400 мм | 395 мм | 40 | 130 | Сталь_RAL9016 (INPLAST) | скрытые защелки |
| STWS-1300х425-Z-SL | 0.332 м² | 1300 мм | 1295 мм | 425 мм | 420 мм | 43 | 130 | Сталь_RAL9016 (INPLAST) | скрытые защелки |
| STWS-1300х450-Z-SL | 0.352 м² | 1300 мм | 1295 мм | 450 мм | 445 мм | 45 | 130 | Сталь_RAL9016 (INPLAST) | скрытые защелки |
| STWS-1300х500-Z-SL | 0.391 м² | 1300 мм | 1295 мм | 500 мм | 495 мм | 50 | 130 | Сталь_RAL9016 (INPLAST) | скрытые защелки |
| STWS-1300х525-Z-SL | 0.411 м² | 1300 мм | 1295 мм | 525 мм | 520 мм | 53 | 130 | Сталь_RAL9016 (INPLAST) | скрытые защелки |
| STWS-1300х550-Z-SL | 0.430 м² | 1300 мм | 1295 мм | 550 мм | 545 мм | 55 | 130 | Сталь_RAL9016 (INPLAST) | скрытые защелки |
| STWS-1300х600-Z-SL | 0.469 м² | 1300 мм | 1295 мм | 600 мм | 595 мм | 60 | 130 | Сталь_RAL9016 (INPLAST) | скрытые защелки |
| STWS-1300х625-Z-SL | 0.489 м² | 1300 мм | 1295 мм | 625 мм | 620 мм | 63 | 130 | Сталь_RAL9016 (INPLAST) | скрытые защелки |
| STWS-1300х650-Z-SL | 0.508 м² | 1300 мм | 1295 мм | 650 мм | 645 мм | 65 | 130 | Сталь_RAL9016 (INPLAST) | скрытые защелки |
| STWS-1325х100-Z-SL | 0.080 м² | 1325 мм | 1320 мм | 100 мм | 95 мм | 10 | 133 | Сталь_RAL9016 (INPLAST) | скрытые защелки |
| STWS-1325х125-Z-SL | 0.100 м² | 1325 мм | 1320 мм | 125 мм | 120 мм | 13 | 133 | Сталь_RAL9016 (INPLAST) | скрытые защелки |
| STWS-1325х150-Z-SL | 0.120 м² | 1325 мм | 1320 мм | 150 мм | 145 мм | 15 | 133 | Сталь_RAL9016 (INPLAST) | скрытые защелки |
| STWS-1325х200-Z-SL | 0.159 м² | 1325 мм | 1320 мм | 200 мм | 195 мм | 20 | 133 | Сталь_RAL9016 (INPLAST) | скрытые защелки |
| STWS-1325х225-Z-SL | 0.179 м² | 1325 мм | 1320 мм | 225 мм | 220 мм | 23 | 133 | Сталь_RAL9016 (INPLAST) | скрытые защелки |
| STWS-1325х250-Z-SL | 0.199 м² | 1325 мм | 1320 мм | 250 мм | 245 мм | 25 | 133 | Сталь_RAL9016 (INPLAST) | скрытые защелки |
| STWS-1325х300-Z-SL | 0.239 м² | 1325 мм | 1320 мм | 300 мм | 295 мм | 30 | 133 | Сталь_RAL9016 (INPLAST) | скрытые защелки |
| STWS-1325х325-Z-SL | 0.259 м² | 1325 мм | 1320 мм | 325 мм | 320 мм | 33 | 133 | Сталь_RAL9016 (INPLAST) | скрытые защелки |
| STWS-1325х350-Z-SL | 0.279 м² | 1325 мм | 1320 мм | 350 мм | 345 мм | 35 | 133 | Сталь_RAL9016 (INPLAST) | скрытые защелки |
| STWS-1325х400-Z-SL | 0.319 м² | 1325 мм | 1320 мм | 400 мм | 395 мм | 40 | 133 | Сталь_RAL9016 (INPLAST) | скрытые защелки |
| STWS-1325х425-Z-SL | 0.339 м² | 1325 мм | 1320 мм | 425 мм | 420 мм | 43 | 133 | Сталь_RAL9016 (INPLAST) | скрытые защелки |
| STWS-1325х450-Z-SL | 0.359 м² | 1325 мм | 1320 мм | 450 мм | 445 мм | 45 | 133 | Сталь_RAL9016 (INPLAST) | скрытые защелки |
| STWS-1325х500-Z-SL | 0.399 м² | 1325 мм | 1320 мм | 500 мм | 495 мм | 50 | 133 | Сталь_RAL9016 (INPLAST) | скрытые защелки |
| STWS-1325х525-Z-SL | 0.418 м² | 1325 мм | 1320 мм | 525 мм | 520 мм | 53 | 133 | Сталь_RAL9016 (INPLAST) | скрытые защелки |
| STWS-1325х550-Z-SL | 0.438 м² | 1325 мм | 1320 мм | 550 мм | 545 мм | 55 | 133 | Сталь_RAL9016 (INPLAST) | скрытые защелки |
| STWS-1325х600-Z-SL | 0.478 м² | 1325 мм | 1320 мм | 600 мм | 595 мм | 60 | 133 | Сталь_RAL9016 (INPLAST) | скрытые защелки |
| STWS-1325х625-Z-SL | 0.498 м² | 1325 мм | 1320 мм | 625 мм | 620 мм | 63 | 133 | Сталь_RAL9016 (INPLAST) | скрытые защелки |
| STWS-1325х650-Z-SL | 0.518 м² | 1325 мм | 1320 мм | 650 мм | 645 мм | 65 | 133 | Сталь_RAL9016 (INPLAST) | скрытые защелки |
| STWS-1350х100-Z-SL | 0.081 м² | 1350 мм | 1345 мм | 100 мм | 95 мм | 10 | 135 | Сталь_RAL9016 (INPLAST) | скрытые защелки |
| STWS-1350х125-Z-SL | 0.102 м² | 1350 мм | 1345 мм | 125 мм | 120 мм | 13 | 135 | Сталь_RAL9016 (INPLAST) | скрытые защелки |
| STWS-1350х150-Z-SL | 0.122 м² | 1350 мм | 1345 мм | 150 мм | 145 мм | 15 | 135 | Сталь_RAL9016 (INPLAST) | скрытые защелки |
| STWS-1350х200-Z-SL | 0.162 м² | 1350 мм | 1345 мм | 200 мм | 195 мм | 20 | 135 | Сталь_RAL9016 (INPLAST) | скрытые защелки |
| STWS-1350х225-Z-SL | 0.183 м² | 1350 мм | 1345 мм | 225 мм | 220 мм | 23 | 135 | Сталь_RAL9016 (INPLAST) | скрытые защелки |
| STWS-1350х250-Z-SL | 0.203 м² | 1350 мм | 1345 мм | 250 мм | 245 мм | 25 | 135 | Сталь_RAL9016 (INPLAST) | скрытые защелки |
| STWS-1350х300-Z-SL | 0.244 м² | 1350 мм | 1345 мм | 300 мм | 295 мм | 30 | 135 | Сталь_RAL9016 (INPLAST) | скрытые защелки |
| STWS-1350х325-Z-SL | 0.264 м² | 1350 мм | 1345 мм | 325 мм | 320 мм | 33 | 135 | Сталь_RAL9016 (INPLAST) | скрытые защелки |
| STWS-1350х350-Z-SL | 0.284 м² | 1350 мм | 1345 мм | 350 мм | 345 мм | 35 | 135 | Сталь_RAL9016 (INPLAST) | скрытые защелки |
| STWS-1350х400-Z-SL | 0.325 м² | 1350 мм | 1345 мм | 400 мм | 395 мм | 40 | 135 | Сталь_RAL9016 (INPLAST) | скрытые защелки |
| STWS-1350х425-Z-SL | 0.345 м² | 1350 мм | 1345 мм | 425 мм | 420 мм | 43 | 135 | Сталь_RAL9016 (INPLAST) | скрытые защелки |
| STWS-1350х450-Z-SL | 0.365 м² | 1350 мм | 1345 мм | 450 мм | 445 мм | 45 | 135 | Сталь_RAL9016 (INPLAST) | скрытые защелки |
| STWS-1350х500-Z-SL | 0.406 м² | 1350 мм | 1345 мм | 500 мм | 495 мм | 50 | 135 | Сталь_RAL9016 (INPLAST) | скрытые защелки |
| STWS-1350х525-Z-SL | 0.426 м² | 1350 мм | 1345 мм | 525 мм | 520 мм | 53 | 135 | Сталь_RAL9016 (INPLAST) | скрытые защелки |
| STWS-1350х550-Z-SL | 0.447 м² | 1350 мм | 1345 мм | 550 мм | 545 мм | 55 | 135 | Сталь_RAL9016 (INPLAST) | скрытые защелки |
| STWS-1350х600-Z-SL | 0.487 м² | 1350 мм | 1345 мм | 600 мм | 595 мм | 60 | 135 | Сталь_RAL9016 (INPLAST) | скрытые защелки |
| STWS-1350х625-Z-SL | 0.508 м² | 1350 мм | 1345 мм | 625 мм | 620 мм | 63 | 135 | Сталь_RAL9016 (INPLAST) | скрытые защелки |
| STWS-1350х650-Z-SL | 0.528 м² | 1350 мм | 1345 мм | 650 мм | 645 мм | 65 | 135 | Сталь_RAL9016 (INPLAST) | скрытые защелки |
| STWS-1400х100-Z-SL | 0.084 м² | 1400 мм | 1395 мм | 100 мм | 95 мм | 10 | 140 | Сталь_RAL9016 (INPLAST) | скрытые защелки |
| STWS-1400х125-Z-SL | 0.105 м² | 1400 мм | 1395 мм | 125 мм | 120 мм | 13 | 140 | Сталь_RAL9016 (INPLAST) | скрытые защелки |
| STWS-1400х150-Z-SL | 0.126 м² | 1400 мм | 1395 мм | 150 мм | 145 мм | 15 | 140 | Сталь_RAL9016 (INPLAST) | скрытые защелки |
| STWS-1400х200-Z-SL | 0.168 м² | 1400 мм | 1395 мм | 200 мм | 195 мм | 20 | 140 | Сталь_RAL9016 (INPLAST) | скрытые защелки |
| STWS-1400х225-Z-SL | 0.190 м² | 1400 мм | 1395 мм | 225 мм | 220 мм | 23 | 140 | Сталь_RAL9016 (INPLAST) | скрытые защелки |
| STWS-1400х250-Z-SL | 0.211 м² | 1400 мм | 1395 мм | 250 мм | 245 мм | 25 | 140 | Сталь_RAL9016 (INPLAST) | скрытые защелки |
| STWS-1400х300-Z-SL | 0.253 м² | 1400 мм | 1395 мм | 300 мм | 295 мм | 30 | 140 | Сталь_RAL9016 (INPLAST) | скрытые защелки |
| STWS-1400х325-Z-SL | 0.274 м² | 1400 мм | 1395 мм | 325 мм | 320 мм | 33 | 140 | Сталь_RAL9016 (INPLAST) | скрытые защелки |
| STWS-1400х350-Z-SL | 0.295 м² | 1400 мм | 1395 мм | 350 мм | 345 мм | 35 | 140 | Сталь_RAL9016 (INPLAST) | скрытые защелки |
| STWS-1400х400-Z-SL | 0.337 м² | 1400 мм | 1395 мм | 400 мм | 395 мм | 40 | 140 | Сталь_RAL9016 (INPLAST) | скрытые защелки |
| STWS-1400х425-Z-SL | 0.358 м² | 1400 мм | 1395 мм | 425 мм | 420 мм | 43 | 140 | Сталь_RAL9016 (INPLAST) | скрытые защелки |
| STWS-1400х450-Z-SL | 0.379 м² | 1400 мм | 1395 мм | 450 мм | 445 мм | 45 | 140 | Сталь_RAL9016 (INPLAST) | скрытые защелки |
| STWS-1400х500-Z-SL | 0.421 м² | 1400 мм | 1395 мм | 500 мм | 495 мм | 50 | 140 | Сталь_RAL9016 (INPLAST) | скрытые защелки |
| STWS-1400х525-Z-SL | 0.442 м² | 1400 мм | 1395 мм | 525 мм | 520 мм | 53 | 140 | Сталь_RAL9016 (INPLAST) | скрытые защелки |
| STWS-1400х550-Z-SL | 0.463 м² | 1400 мм | 1395 мм | 550 мм | 545 мм | 55 | 140 | Сталь_RAL9016 (INPLAST) | скрытые защелки |
| STWS-1400х600-Z-SL | 0.505 м² | 1400 мм | 1395 мм | 600 мм | 595 мм | 60 | 140 | Сталь_RAL9016 (INPLAST) | скрытые защелки |
| STWS-1400х625-Z-SL | 0.526 м² | 1400 мм | 1395 мм | 625 мм | 620 мм | 63 | 140 | Сталь_RAL9016 (INPLAST) | скрытые защелки |
| STWS-1400х650-Z-SL | 0.547 м² | 1400 мм | 1395 мм | 650 мм | 645 мм | 65 | 140 | Сталь_RAL9016 (INPLAST) | скрытые защелки |
| STWS-1425х100-Z-SL | 0.086 м² | 1425 мм | 1420 мм | 100 мм | 95 мм | 10 | 143 | Сталь_RAL9016 (INPLAST) | скрытые защелки |
| STWS-1425х125-Z-SL | 0.107 м² | 1425 мм | 1420 мм | 125 мм | 120 мм | 13 | 143 | Сталь_RAL9016 (INPLAST) | скрытые защелки |
| STWS-1425х150-Z-SL | 0.129 м² | 1425 мм | 1420 мм | 150 мм | 145 мм | 15 | 143 | Сталь_RAL9016 (INPLAST) | скрытые защелки |
| STWS-1425х200-Z-SL | 0.171 м² | 1425 мм | 1420 мм | 200 мм | 195 мм | 20 | 143 | Сталь_RAL9016 (INPLAST) | скрытые защелки |
| STWS-1425х225-Z-SL | 0.193 м² | 1425 мм | 1420 мм | 225 мм | 220 мм | 23 | 143 | Сталь_RAL9016 (INPLAST) | скрытые защелки |
| STWS-1425х250-Z-SL | 0.214 м² | 1425 мм | 1420 мм | 250 мм | 245 мм | 25 | 143 | Сталь_RAL9016 (INPLAST) | скрытые защелки |
| STWS-1425х300-Z-SL | 0.257 м² | 1425 мм | 1420 мм | 300 мм | 295 мм | 30 | 143 | Сталь_RAL9016 (INPLAST) | скрытые защелки |
| STWS-1425х325-Z-SL | 0.279 м² | 1425 мм | 1420 мм | 325 мм | 320 мм | 33 | 143 | Сталь_RAL9016 (INPLAST) | скрытые защелки |
| STWS-1425х350-Z-SL | 0.300 м² | 1425 мм | 1420 мм | 350 мм | 345 мм | 35 | 143 | Сталь_RAL9016 (INPLAST) | скрытые защелки |
| STWS-1425х400-Z-SL | 0.343 м² | 1425 мм | 1420 мм | 400 мм | 395 мм | 40 | 143 | Сталь_RAL9016 (INPLAST) | скрытые защелки |
| STWS-1425х425-Z-SL | 0.364 м² | 1425 мм | 1420 мм | 425 мм | 420 мм | 43 | 143 | Сталь_RAL9016 (INPLAST) | скрытые защелки |
| STWS-1425х450-Z-SL | 0.386 м² | 1425 мм | 1420 мм | 450 мм | 445 мм | 45 | 143 | Сталь_RAL9016 (INPLAST) | скрытые защелки |
| STWS-1425х500-Z-SL | 0.429 м² | 1425 мм | 1420 мм | 500 мм | 495 мм | 50 | 143 | Сталь_RAL9016 (INPLAST) | скрытые защелки |
| STWS-1425х525-Z-SL | 0.450 м² | 1425 мм | 1420 мм | 525 мм | 520 мм | 53 | 143 | Сталь_RAL9016 (INPLAST) | скрытые защелки |
| STWS-1425х550-Z-SL | 0.472 м² | 1425 мм | 1420 мм | 550 мм | 545 мм | 55 | 143 | Сталь_RAL9016 (INPLAST) | скрытые защелки |
| STWS-1425х600-Z-SL | 0.514 м² | 1425 мм | 1420 мм | 600 мм | 595 мм | 60 | 143 | Сталь_RAL9016 (INPLAST) | скрытые защелки |
| STWS-1425х625-Z-SL | 0.536 м² | 1425 мм | 1420 мм | 625 мм | 620 мм | 63 | 143 | Сталь_RAL9016 (INPLAST) | скрытые защелки |
| STWS-1425х650-Z-SL | 0.557 м² | 1425 мм | 1420 мм | 650 мм | 645 мм | 65 | 143 | Сталь_RAL9016 (INPLAST) | скрытые защелки |
| STWS-1450х100-Z-SL | 0.087 м² | 1450 мм | 1445 мм | 100 мм | 95 мм | 10 | 145 | Сталь_RAL9016 (INPLAST) | скрытые защелки |
| STWS-1450х125-Z-SL | 0.109 м² | 1450 мм | 1445 мм | 125 мм | 120 мм | 13 | 145 | Сталь_RAL9016 (INPLAST) | скрытые защелки |
| STWS-1450х150-Z-SL | 0.131 м² | 1450 мм | 1445 мм | 150 мм | 145 мм | 15 | 145 | Сталь_RAL9016 (INPLAST) | скрытые защелки |
| STWS-1450х200-Z-SL | 0.174 м² | 1450 мм | 1445 мм | 200 мм | 195 мм | 20 | 145 | Сталь_RAL9016 (INPLAST) | скрытые защелки |
| STWS-1450х225-Z-SL | 0.196 м² | 1450 мм | 1445 мм | 225 мм | 220 мм | 23 | 145 | Сталь_RAL9016 (INPLAST) | скрытые защелки |
| STWS-1450х250-Z-SL | 0.218 м² | 1450 мм | 1445 мм | 250 мм | 245 мм | 25 | 145 | Сталь_RAL9016 (INPLAST) | скрытые защелки |
| STWS-1450х300-Z-SL | 0.262 м² | 1450 мм | 1445 мм | 300 мм | 295 мм | 30 | 145 | Сталь_RAL9016 (INPLAST) | скрытые защелки |
| STWS-1450х325-Z-SL | 0.284 м² | 1450 мм | 1445 мм | 325 мм | 320 мм | 33 | 145 | Сталь_RAL9016 (INPLAST) | скрытые защелки |
| STWS-1450х350-Z-SL | 0.305 м² | 1450 мм | 1445 мм | 350 мм | 345 мм | 35 | 145 | Сталь_RAL9016 (INPLAST) | скрытые защелки |
| STWS-1450х400-Z-SL | 0.349 м² | 1450 мм | 1445 мм | 400 мм | 395 мм | 40 | 145 | Сталь_RAL9016 (INPLAST) | скрытые защелки |
| STWS-1450х425-Z-SL | 0.371 м² | 1450 мм | 1445 мм | 425 мм | 420 мм | 43 | 145 | Сталь_RAL9016 (INPLAST) | скрытые защелки |
| STWS-1450х450-Z-SL | 0.393 м² | 1450 мм | 1445 мм | 450 мм | 445 мм | 45 | 145 | Сталь_RAL9016 (INPLAST) | скрытые защелки |
| STWS-1450х500-Z-SL | 0.436 м² | 1450 мм | 1445 мм | 500 мм | 495 мм | 50 | 145 | Сталь_RAL9016 (INPLAST) | скрытые защелки |
| STWS-1450х525-Z-SL | 0.458 м² | 1450 мм | 1445 мм | 525 мм | 520 мм | 53 | 145 | Сталь_RAL9016 (INPLAST) | скрытые защелки |
| STWS-1450х550-Z-SL | 0.480 м² | 1450 мм | 1445 мм | 550 мм | 545 мм | 55 | 145 | Сталь_RAL9016 (INPLAST) | скрытые защелки |
| STWS-1450х600-Z-SL | 0.523 м² | 1450 мм | 1445 мм | 600 мм | 595 мм | 60 | 145 | Сталь_RAL9016 (INPLAST) | скрытые защелки |
| STWS-1450х625-Z-SL | 0.545 м² | 1450 мм | 1445 мм | 625 мм | 620 мм | 63 | 145 | Сталь_RAL9016 (INPLAST) | скрытые защелки |
| STWS-1450х650-Z-SL | 0.567 м² | 1450 мм | 1445 мм | 650 мм | 645 мм | 65 | 145 | Сталь_RAL9016 (INPLAST) | скрытые защелки |
| STWS-1500х100-Z-SL | 0.090 м² | 1500 мм | 1495 мм | 100 мм | 95 мм | 10 | 150 | Сталь_RAL9016 (INPLAST) | скрытые защелки |
| STWS-1500х125-Z-SL | 0.113 м² | 1500 мм | 1495 мм | 125 мм | 120 мм | 13 | 150 | Сталь_RAL9016 (INPLAST) | скрытые защелки |
| STWS-1500х150-Z-SL | 0.135 м² | 1500 мм | 1495 мм | 150 мм | 145 мм | 15 | 150 | Сталь_RAL9016 (INPLAST) | скрытые защелки |
| STWS-1500х200-Z-SL | 0.180 м² | 1500 мм | 1495 мм | 200 мм | 195 мм | 20 | 150 | Сталь_RAL9016 (INPLAST) | скрытые защелки |
| STWS-1500х225-Z-SL | 0.203 м² | 1500 мм | 1495 мм | 225 мм | 220 мм | 23 | 150 | Сталь_RAL9016 (INPLAST) | скрытые защелки |
| STWS-1500х250-Z-SL | 0.226 м² | 1500 мм | 1495 мм | 250 мм | 245 мм | 25 | 150 | Сталь_RAL9016 (INPLAST) | скрытые защелки |
| STWS-1500х300-Z-SL | 0.271 м² | 1500 мм | 1495 мм | 300 мм | 295 мм | 30 | 150 | Сталь_RAL9016 (INPLAST) | скрытые защелки |
| STWS-1500х325-Z-SL | 0.293 м² | 1500 мм | 1495 мм | 325 мм | 320 мм | 33 | 150 | Сталь_RAL9016 (INPLAST) | скрытые защелки |
| STWS-1500х350-Z-SL | 0.316 м² | 1500 мм | 1495 мм | 350 мм | 345 мм | 35 | 150 | Сталь_RAL9016 (INPLAST) | скрытые защелки |
| STWS-1500х400-Z-SL | 0.361 м² | 1500 мм | 1495 мм | 400 мм | 395 мм | 40 | 150 | Сталь_RAL9016 (INPLAST) | скрытые защелки |
| STWS-1500х425-Z-SL | 0.384 м² | 1500 мм | 1495 мм | 425 мм | 420 мм | 43 | 150 | Сталь_RAL9016 (INPLAST) | скрытые защелки |
| STWS-1500х450-Z-SL | 0.406 м² | 1500 мм | 1495 мм | 450 мм | 445 мм | 45 | 150 | Сталь_RAL9016 (INPLAST) | скрытые защелки |
| STWS-1500х500-Z-SL | 0.451 м² | 1500 мм | 1495 мм | 500 мм | 495 мм | 50 | 150 | Сталь_RAL9016 (INPLAST) | скрытые защелки |
| STWS-1500х525-Z-SL | 0.474 м² | 1500 мм | 1495 мм | 525 мм | 520 мм | 53 | 150 | Сталь_RAL9016 (INPLAST) | скрытые защелки |
| STWS-1500х550-Z-SL | 0.496 м² | 1500 мм | 1495 мм | 550 мм | 545 мм | 55 | 150 | Сталь_RAL9016 (INPLAST) | скрытые защелки |
| STWS-1500х600-Z-SL | 0.541 м² | 1500 мм | 1495 мм | 600 мм | 595 мм | 60 | 150 | Сталь_RAL9016 (INPLAST) | скрытые защелки |
| STWS-1500х625-Z-SL | 0.564 м² | 1500 мм | 1495 мм | 625 мм | 620 мм | 63 | 150 | Сталь_RAL9016 (INPLAST) | скрытые защелки |
| STWS-1500х650-Z-SL | 0.587 м² | 1500 мм | 1495 мм | 650 мм | 645 мм | 65 | 150 | Сталь_RAL9016 (INPLAST) | скрытые защелки |
| STWS-100х100-SO | 0.006 м² | 100 мм | 95 мм | 100 мм | 95 мм | 10 | 10 | Оцинкованная сталь (INPLAST) | саморезы |
| STWS-125х100-SO | 0.008 м² | 125 мм | 120 мм | 100 мм | 95 мм | 10 | 13 | Оцинкованная сталь (INPLAST) | саморезы |
| STWS-125х125-SO | 0.009 м² | 125 мм | 120 мм | 125 мм | 120 мм | 13 | 13 | Оцинкованная сталь (INPLAST) | саморезы |
| STWS-150х100-SO | 0.009 м² | 150 мм | 145 мм | 100 мм | 95 мм | 10 | 15 | Оцинкованная сталь (INPLAST) | саморезы |
| STWS-150х125-SO | 0.011 м² | 150 мм | 145 мм | 125 мм | 120 мм | 13 | 15 | Оцинкованная сталь (INPLAST) | саморезы |
| STWS-150х150-SO | 0.014 м² | 150 мм | 145 мм | 150 мм | 145 мм | 15 | 15 | Оцинкованная сталь (INPLAST) | саморезы |
| STWS-200х100-SO | 0.012 м² | 200 мм | 195 мм | 100 мм | 95 мм | 10 | 20 | Оцинкованная сталь (INPLAST) | саморезы |
| STWS-200х125-SO | 0.015 м² | 200 мм | 195 мм | 125 мм | 120 мм | 13 | 20 | Оцинкованная сталь (INPLAST) | саморезы |
| STWS-200х150-SO | 0.018 м² | 200 мм | 195 мм | 150 мм | 145 мм | 15 | 20 | Оцинкованная сталь (INPLAST) | саморезы |
| STWS-200х200-SO | 0.024 м² | 200 мм | 195 мм | 200 мм | 195 мм | 20 | 20 | Оцинкованная сталь (INPLAST) | саморезы |
| STWS-225х100-SO | 0.014 м² | 225 мм | 220 мм | 100 мм | 95 мм | 10 | 23 | Оцинкованная сталь (INPLAST) | саморезы |
| STWS-225х125-SO | 0.017 м² | 225 мм | 220 мм | 125 мм | 120 мм | 13 | 23 | Оцинкованная сталь (INPLAST) | саморезы |
| STWS-225х150-SO | 0.020 м² | 225 мм | 220 мм | 150 мм | 145 мм | 15 | 23 | Оцинкованная сталь (INPLAST) | саморезы |
| STWS-225х200-SO | 0.027 м² | 225 мм | 220 мм | 200 мм | 195 мм | 20 | 23 | Оцинкованная сталь (INPLAST) | саморезы |
| STWS-225х225-SO | 0.030 м² | 225 мм | 220 мм | 225 мм | 220 мм | 23 | 23 | Оцинкованная сталь (INPLAST) | саморезы |
| STWS-250х100-SO | 0.015 м² | 250 мм | 245 мм | 100 мм | 95 мм | 10 | 25 | Оцинкованная сталь (INPLAST) | саморезы |
| STWS-250х125-SO | 0.019 м² | 250 мм | 245 мм | 125 мм | 120 мм | 13 | 25 | Оцинкованная сталь (INPLAST) | саморезы |
| STWS-250х150-SO | 0.023 м² | 250 мм | 245 мм | 150 мм | 145 мм | 15 | 25 | Оцинкованная сталь (INPLAST) | саморезы |
| STWS-250х200-SO | 0.030 м² | 250 мм | 245 мм | 200 мм | 195 мм | 20 | 25 | Оцинкованная сталь (INPLAST) | саморезы |
| STWS-250х225-SO | 0.034 м² | 250 мм | 245 мм | 225 мм | 220 мм | 23 | 25 | Оцинкованная сталь (INPLAST) | саморезы |
| STWS-250х250-SO | 0.038 м² | 250 мм | 245 мм | 250 мм | 245 мм | 25 | 25 | Оцинкованная сталь (INPLAST) | саморезы |
| STWS-300х100-SO | 0.018 м² | 300 мм | 295 мм | 100 мм | 95 мм | 10 | 30 | Оцинкованная сталь (INPLAST) | саморезы |
| STWS-300х125-SO | 0.023 м² | 300 мм | 295 мм | 125 мм | 120 мм | 13 | 30 | Оцинкованная сталь (INPLAST) | саморезы |
| STWS-300х150-SO | 0.027 м² | 300 мм | 295 мм | 150 мм | 145 мм | 15 | 30 | Оцинкованная сталь (INPLAST) | саморезы |
| STWS-300х200-SO | 0.036 м² | 300 мм | 295 мм | 200 мм | 195 мм | 20 | 30 | Оцинкованная сталь (INPLAST) | саморезы |
| STWS-300х225-SO | 0.041 м² | 300 мм | 295 мм | 225 мм | 220 мм | 23 | 30 | Оцинкованная сталь (INPLAST) | саморезы |
| STWS-300х250-SO | 0.045 м² | 300 мм | 295 мм | 250 мм | 245 мм | 25 | 30 | Оцинкованная сталь (INPLAST) | саморезы |
| STWS-300х300-SO | 0.054 м² | 300 мм | 295 мм | 300 мм | 295 мм | 30 | 30 | Оцинкованная сталь (INPLAST) | саморезы |
| STWS-325х100-SO | 0.020 м² | 325 мм | 320 мм | 100 мм | 95 мм | 10 | 33 | Оцинкованная сталь (INPLAST) | саморезы |
| STWS-325х125-SO | 0.024 м² | 325 мм | 320 мм | 125 мм | 120 мм | 13 | 33 | Оцинкованная сталь (INPLAST) | саморезы |
| STWS-325х150-SO | 0.029 м² | 325 мм | 320 мм | 150 мм | 145 мм | 15 | 33 | Оцинкованная сталь (INPLAST) | саморезы |
| STWS-325х200-SO | 0.039 м² | 325 мм | 320 мм | 200 мм | 195 мм | 20 | 33 | Оцинкованная сталь (INPLAST) | саморезы |
| STWS-325х225-SO | 0.044 м² | 325 мм | 320 мм | 225 мм | 220 мм | 23 | 33 | Оцинкованная сталь (INPLAST) | саморезы |
| STWS-325х250-SO | 0.049 м² | 325 мм | 320 мм | 250 мм | 245 мм | 25 | 33 | Оцинкованная сталь (INPLAST) | саморезы |
| STWS-325х300-SO | 0.059 м² | 325 мм | 320 мм | 300 мм | 295 мм | 30 | 33 | Оцинкованная сталь (INPLAST) | саморезы |
| STWS-325х325-SO | 0.064 м² | 325 мм | 320 мм | 325 мм | 320 мм | 33 | 33 | Оцинкованная сталь (INPLAST) | саморезы |
| STWS-350х100-SO | 0.021 м² | 350 мм | 345 мм | 100 мм | 95 мм | 10 | 35 | Оцинкованная сталь (INPLAST) | саморезы |
| STWS-350х125-SO | 0.026 м² | 350 мм | 345 мм | 125 мм | 120 мм | 13 | 35 | Оцинкованная сталь (INPLAST) | саморезы |
| STWS-350х150-SO | 0.032 м² | 350 мм | 345 мм | 150 мм | 145 мм | 15 | 35 | Оцинкованная сталь (INPLAST) | саморезы |
| STWS-350х200-SO | 0.042 м² | 350 мм | 345 мм | 200 мм | 195 мм | 20 | 35 | Оцинкованная сталь (INPLAST) | саморезы |
| STWS-350х225-SO | 0.047 м² | 350 мм | 345 мм | 225 мм | 220 мм | 23 | 35 | Оцинкованная сталь (INPLAST) | саморезы |
| STWS-350х250-SO | 0.053 м² | 350 мм | 345 мм | 250 мм | 245 мм | 25 | 35 | Оцинкованная сталь (INPLAST) | саморезы |
| STWS-350х300-SO | 0.063 м² | 350 мм | 345 мм | 300 мм | 295 мм | 30 | 35 | Оцинкованная сталь (INPLAST) | саморезы |
| STWS-350х325-SO | 0.068 м² | 350 мм | 345 мм | 325 мм | 320 мм | 33 | 35 | Оцинкованная сталь (INPLAST) | саморезы |
| STWS-350х350-SO | 0.074 м² | 350 мм | 345 мм | 350 мм | 345 мм | 35 | 35 | Оцинкованная сталь (INPLAST) | саморезы |
| STWS-400х100-SO | 0.024 м² | 400 мм | 395 мм | 100 мм | 95 мм | 10 | 40 | Оцинкованная сталь (INPLAST) | саморезы |
| STWS-400х125-SO | 0.030 м² | 400 мм | 395 мм | 125 мм | 120 мм | 13 | 40 | Оцинкованная сталь (INPLAST) | саморезы |
| STWS-400х150-SO | 0.036 м² | 400 мм | 395 мм | 150 мм | 145 мм | 15 | 40 | Оцинкованная сталь (INPLAST) | саморезы |
| STWS-400х200-SO | 0.048 м² | 400 мм | 395 мм | 200 мм | 195 мм | 20 | 40 | Оцинкованная сталь (INPLAST) | саморезы |
| STWS-400х225-SO | 0.054 м² | 400 мм | 395 мм | 225 мм | 220 мм | 23 | 40 | Оцинкованная сталь (INPLAST) | саморезы |
| STWS-400х250-SO | 0.060 м² | 400 мм | 395 мм | 250 мм | 245 мм | 25 | 40 | Оцинкованная сталь (INPLAST) | саморезы |
| STWS-400х300-SO | 0.072 м² | 400 мм | 395 мм | 300 мм | 295 мм | 30 | 40 | Оцинкованная сталь (INPLAST) | саморезы |
| STWS-400х325-SO | 0.078 м² | 400 мм | 395 мм | 325 мм | 320 мм | 33 | 40 | Оцинкованная сталь (INPLAST) | саморезы |
| STWS-400х350-SO | 0.084 м² | 400 мм | 395 мм | 350 мм | 345 мм | 35 | 40 | Оцинкованная сталь (INPLAST) | саморезы |
| STWS-400х400-SO | 0.096 м² | 400 мм | 395 мм | 400 мм | 395 мм | 40 | 40 | Оцинкованная сталь (INPLAST) | саморезы |
| STWS-425х100-SO | 0.026 м² | 425 мм | 420 мм | 100 мм | 95 мм | 10 | 43 | Оцинкованная сталь (INPLAST) | саморезы |
| STWS-425х125-SO | 0.032 м² | 425 мм | 420 мм | 125 мм | 120 мм | 13 | 43 | Оцинкованная сталь (INPLAST) | саморезы |
| STWS-425х150-SO | 0.038 м² | 425 мм | 420 мм | 150 мм | 145 мм | 15 | 43 | Оцинкованная сталь (INPLAST) | саморезы |
| STWS-425х200-SO | 0.051 м² | 425 мм | 420 мм | 200 мм | 195 мм | 20 | 43 | Оцинкованная сталь (INPLAST) | саморезы |
| STWS-425х225-SO | 0.058 м² | 425 мм | 420 мм | 225 мм | 220 мм | 23 | 43 | Оцинкованная сталь (INPLAST) | саморезы |
| STWS-425х250-SO | 0.064 м² | 425 мм | 420 мм | 250 мм | 245 мм | 25 | 43 | Оцинкованная сталь (INPLAST) | саморезы |
| STWS-425х300-SO | 0.077 м² | 425 мм | 420 мм | 300 мм | 295 мм | 30 | 43 | Оцинкованная сталь (INPLAST) | саморезы |
| STWS-425х325-SO | 0.083 м² | 425 мм | 420 мм | 325 мм | 320 мм | 33 | 43 | Оцинкованная сталь (INPLAST) | саморезы |
| STWS-425х350-SO | 0.089 м² | 425 мм | 420 мм | 350 мм | 345 мм | 35 | 43 | Оцинкованная сталь (INPLAST) | саморезы |
| STWS-425х400-SO | 0.102 м² | 425 мм | 420 мм | 400 мм | 395 мм | 40 | 43 | Оцинкованная сталь (INPLAST) | саморезы |
| STWS-425х425-SO | 0.109 м² | 425 мм | 420 мм | 425 мм | 420 мм | 43 | 43 | Оцинкованная сталь (INPLAST) | саморезы |
| STWS-450х100-SO | 0.027 м² | 450 мм | 445 мм | 100 мм | 95 мм | 10 | 45 | Оцинкованная сталь (INPLAST) | саморезы |
| STWS-450х125-SO | 0.034 м² | 450 мм | 445 мм | 125 мм | 120 мм | 13 | 45 | Оцинкованная сталь (INPLAST) | саморезы |
| STWS-450х150-SO | 0.041 м² | 450 мм | 445 мм | 150 мм | 145 мм | 15 | 45 | Оцинкованная сталь (INPLAST) | саморезы |
| STWS-450х200-SO | 0.054 м² | 450 мм | 445 мм | 200 мм | 195 мм | 20 | 45 | Оцинкованная сталь (INPLAST) | саморезы |
| STWS-450х225-SO | 0.061 м² | 450 мм | 445 мм | 225 мм | 220 мм | 23 | 45 | Оцинкованная сталь (INPLAST) | саморезы |
| STWS-450х250-SO | 0.068 м² | 450 мм | 445 мм | 250 мм | 245 мм | 25 | 45 | Оцинкованная сталь (INPLAST) | саморезы |
| STWS-450х300-SO | 0.081 м² | 450 мм | 445 мм | 300 мм | 295 мм | 30 | 45 | Оцинкованная сталь (INPLAST) | саморезы |
| STWS-450х325-SO | 0.088 м² | 450 мм | 445 мм | 325 мм | 320 мм | 33 | 45 | Оцинкованная сталь (INPLAST) | саморезы |
| STWS-450х350-SO | 0.095 м² | 450 мм | 445 мм | 350 мм | 345 мм | 35 | 45 | Оцинкованная сталь (INPLAST) | саморезы |
| STWS-450х400-SO | 0.108 м² | 450 мм | 445 мм | 400 мм | 395 мм | 40 | 45 | Оцинкованная сталь (INPLAST) | саморезы |
| STWS-450х425-SO | 0.115 м² | 450 мм | 445 мм | 425 мм | 420 мм | 43 | 45 | Оцинкованная сталь (INPLAST) | саморезы |
| STWS-450х450-SO | 0.122 м² | 450 мм | 445 мм | 450 мм | 445 мм | 45 | 45 | Оцинкованная сталь (INPLAST) | саморезы |
| STWS-500х100-SO | 0.030 м² | 500 мм | 495 мм | 100 мм | 95 мм | 10 | 50 | Оцинкованная сталь (INPLAST) | саморезы |
| STWS-500х125-SO | 0.038 м² | 500 мм | 495 мм | 125 мм | 120 мм | 13 | 50 | Оцинкованная сталь (INPLAST) | саморезы |
| STWS-500х150-SO | 0.045 м² | 500 мм | 495 мм | 150 мм | 145 мм | 15 | 50 | Оцинкованная сталь (INPLAST) | саморезы |
| STWS-500х200-SO | 0.060 м² | 500 мм | 495 мм | 200 мм | 195 мм | 20 | 50 | Оцинкованная сталь (INPLAST) | саморезы |
| STWS-500х225-SO | 0.068 м² | 500 мм | 495 мм | 225 мм | 220 мм | 23 | 50 | Оцинкованная сталь (INPLAST) | саморезы |
| STWS-500х250-SO | 0.075 м² | 500 мм | 495 мм | 250 мм | 245 мм | 25 | 50 | Оцинкованная сталь (INPLAST) | саморезы |
| STWS-500х300-SO | 0.090 м² | 500 мм | 495 мм | 300 мм | 295 мм | 30 | 50 | Оцинкованная сталь (INPLAST) | саморезы |
| STWS-500х325-SO | 0.098 м² | 500 мм | 495 мм | 325 мм | 320 мм | 33 | 50 | Оцинкованная сталь (INPLAST) | саморезы |
| STWS-500х350-SO | 0.105 м² | 500 мм | 495 мм | 350 мм | 345 мм | 35 | 50 | Оцинкованная сталь (INPLAST) | саморезы |
| STWS-500х400-SO | 0.120 м² | 500 мм | 495 мм | 400 мм | 395 мм | 40 | 50 | Оцинкованная сталь (INPLAST) | саморезы |
| STWS-500х425-SO | 0.128 м² | 500 мм | 495 мм | 425 мм | 420 мм | 43 | 50 | Оцинкованная сталь (INPLAST) | саморезы |
| STWS-500х450-SO | 0.135 м² | 500 мм | 495 мм | 450 мм | 445 мм | 45 | 50 | Оцинкованная сталь (INPLAST) | саморезы |
| STWS-500х500-SO | 0.150 м² | 500 мм | 495 мм | 500 мм | 495 мм | 50 | 50 | Оцинкованная сталь (INPLAST) | саморезы |
| STWS-525х100-SO | 0.032 м² | 525 мм | 520 мм | 100 мм | 95 мм | 10 | 53 | Оцинкованная сталь (INPLAST) | саморезы |
| STWS-525х125-SO | 0.039 м² | 525 мм | 520 мм | 125 мм | 120 мм | 13 | 53 | Оцинкованная сталь (INPLAST) | саморезы |
| STWS-525х150-SO | 0.047 м² | 525 мм | 520 мм | 150 мм | 145 мм | 15 | 53 | Оцинкованная сталь (INPLAST) | саморезы |
| STWS-525х200-SO | 0.063 м² | 525 мм | 520 мм | 200 мм | 195 мм | 20 | 53 | Оцинкованная сталь (INPLAST) | саморезы |
| STWS-525х225-SO | 0.071 м² | 525 мм | 520 мм | 225 мм | 220 мм | 23 | 53 | Оцинкованная сталь (INPLAST) | саморезы |
| STWS-525х250-SO | 0.079 м² | 525 мм | 520 мм | 250 мм | 245 мм | 25 | 53 | Оцинкованная сталь (INPLAST) | саморезы |
| STWS-525х300-SO | 0.095 м² | 525 мм | 520 мм | 300 мм | 295 мм | 30 | 53 | Оцинкованная сталь (INPLAST) | саморезы |
| STWS-525х325-SO | 0.103 м² | 525 мм | 520 мм | 325 мм | 320 мм | 33 | 53 | Оцинкованная сталь (INPLAST) | саморезы |
| STWS-525х350-SO | 0.111 м² | 525 мм | 520 мм | 350 мм | 345 мм | 35 | 53 | Оцинкованная сталь (INPLAST) | саморезы |
| STWS-525х400-SO | 0.126 м² | 525 мм | 520 мм | 400 мм | 395 мм | 40 | 53 | Оцинкованная сталь (INPLAST) | саморезы |
| STWS-525х425-SO | 0.134 м² | 525 мм | 520 мм | 425 мм | 420 мм | 43 | 53 | Оцинкованная сталь (INPLAST) | саморезы |
| STWS-525х450-SO | 0.142 м² | 525 мм | 520 мм | 450 мм | 445 мм | 45 | 53 | Оцинкованная сталь (INPLAST) | саморезы |
| STWS-525х500-SO | 0.158 м² | 525 мм | 520 мм | 500 мм | 495 мм | 50 | 53 | Оцинкованная сталь (INPLAST) | саморезы |
| STWS-525х525-SO | 0.166 м² | 525 мм | 520 мм | 525 мм | 520 мм | 53 | 53 | Оцинкованная сталь (INPLAST) | саморезы |
| STWS-550х100-SO | 0.033 м² | 550 мм | 545 мм | 100 мм | 95 мм | 10 | 55 | Оцинкованная сталь (INPLAST) | саморезы |
| STWS-550х125-SO | 0.041 м² | 550 мм | 545 мм | 125 мм | 120 мм | 13 | 55 | Оцинкованная сталь (INPLAST) | саморезы |
| STWS-550х150-SO | 0.050 м² | 550 мм | 545 мм | 150 мм | 145 мм | 15 | 55 | Оцинкованная сталь (INPLAST) | саморезы |
| STWS-550х200-SO | 0.066 м² | 550 мм | 545 мм | 200 мм | 195 мм | 20 | 55 | Оцинкованная сталь (INPLAST) | саморезы |
| STWS-550х225-SO | 0.074 м² | 550 мм | 545 мм | 225 мм | 220 мм | 23 | 55 | Оцинкованная сталь (INPLAST) | саморезы |
| STWS-550х250-SO | 0.083 м² | 550 мм | 545 мм | 250 мм | 245 мм | 25 | 55 | Оцинкованная сталь (INPLAST) | саморезы |
| STWS-550х300-SO | 0.099 м² | 550 мм | 545 мм | 300 мм | 295 мм | 30 | 55 | Оцинкованная сталь (INPLAST) | саморезы |
| STWS-550х325-SO | 0.108 м² | 550 мм | 545 мм | 325 мм | 320 мм | 33 | 55 | Оцинкованная сталь (INPLAST) | саморезы |
| STWS-550х350-SO | 0.116 м² | 550 мм | 545 мм | 350 мм | 345 мм | 35 | 55 | Оцинкованная сталь (INPLAST) | саморезы |
| STWS-550х400-SO | 0.132 м² | 550 мм | 545 мм | 400 мм | 395 мм | 40 | 55 | Оцинкованная сталь (INPLAST) | саморезы |
| STWS-550х425-SO | 0.141 м² | 550 мм | 545 мм | 425 мм | 420 мм | 43 | 55 | Оцинкованная сталь (INPLAST) | саморезы |
| STWS-550х450-SO | 0.149 м² | 550 мм | 545 мм | 450 мм | 445 мм | 45 | 55 | Оцинкованная сталь (INPLAST) | саморезы |
| STWS-550х500-SO | 0.165 м² | 550 мм | 545 мм | 500 мм | 495 мм | 50 | 55 | Оцинкованная сталь (INPLAST) | саморезы |
| STWS-550х525-SO | 0.174 м² | 550 мм | 545 мм | 525 мм | 520 мм | 53 | 55 | Оцинкованная сталь (INPLAST) | саморезы |
| STWS-550х550-SO | 0.182 м² | 550 мм | 545 мм | 550 мм | 545 мм | 55 | 55 | Оцинкованная сталь (INPLAST) | саморезы |
| STWS-600х100-SO | 0.036 м² | 600 мм | 595 мм | 100 мм | 95 мм | 10 | 60 | Оцинкованная сталь (INPLAST) | саморезы |
| STWS-600х125-SO | 0.045 м² | 600 мм | 595 мм | 125 мм | 120 мм | 13 | 60 | Оцинкованная сталь (INPLAST) | саморезы |
| STWS-600х150-SO | 0.054 м² | 600 мм | 595 мм | 150 мм | 145 мм | 15 | 60 | Оцинкованная сталь (INPLAST) | саморезы |
| STWS-600х200-SO | 0.072 м² | 600 мм | 595 мм | 200 мм | 195 мм | 20 | 60 | Оцинкованная сталь (INPLAST) | саморезы |
| STWS-600х225-SO | 0.081 м² | 600 мм | 595 мм | 225 мм | 220 мм | 23 | 60 | Оцинкованная сталь (INPLAST) | саморезы |
| STWS-600х250-SO | 0.090 м² | 600 мм | 595 мм | 250 мм | 245 мм | 25 | 60 | Оцинкованная сталь (INPLAST) | саморезы |
| STWS-600х300-SO | 0.108 м² | 600 мм | 595 мм | 300 мм | 295 мм | 30 | 60 | Оцинкованная сталь (INPLAST) | саморезы |
| STWS-600х325-SO | 0.117 м² | 600 мм | 595 мм | 325 мм | 320 мм | 33 | 60 | Оцинкованная сталь (INPLAST) | саморезы |
| STWS-600х350-SO | 0.126 м² | 600 мм | 595 мм | 350 мм | 345 мм | 35 | 60 | Оцинкованная сталь (INPLAST) | саморезы |
| STWS-600х400-SO | 0.144 м² | 600 мм | 595 мм | 400 мм | 395 мм | 40 | 60 | Оцинкованная сталь (INPLAST) | саморезы |
| STWS-600х425-SO | 0.153 м² | 600 мм | 595 мм | 425 мм | 420 мм | 43 | 60 | Оцинкованная сталь (INPLAST) | саморезы |
| STWS-600х450-SO | 0.162 м² | 600 мм | 595 мм | 450 мм | 445 мм | 45 | 60 | Оцинкованная сталь (INPLAST) | саморезы |
| STWS-600х500-SO | 0.180 м² | 600 мм | 595 мм | 500 мм | 495 мм | 50 | 60 | Оцинкованная сталь (INPLAST) | саморезы |
| STWS-600х525-SO | 0.190 м² | 600 мм | 595 мм | 525 мм | 520 мм | 53 | 60 | Оцинкованная сталь (INPLAST) | саморезы |
| STWS-600х550-SO | 0.199 м² | 600 мм | 595 мм | 550 мм | 545 мм | 55 | 60 | Оцинкованная сталь (INPLAST) | саморезы |
| STWS-600х600-SO | 0.217 м² | 600 мм | 595 мм | 600 мм | 595 мм | 60 | 60 | Оцинкованная сталь (INPLAST) | саморезы |
| STWS-625х100-SO | 0.038 м² | 625 мм | 620 мм | 100 мм | 95 мм | 10 | 63 | Оцинкованная сталь (INPLAST) | саморезы |
| STWS-625х125-SO | 0.047 м² | 625 мм | 620 мм | 125 мм | 120 мм | 13 | 63 | Оцинкованная сталь (INPLAST) | саморезы |
| STWS-625х150-SO | 0.056 м² | 625 мм | 620 мм | 150 мм | 145 мм | 15 | 63 | Оцинкованная сталь (INPLAST) | саморезы |
| STWS-625х200-SO | 0.075 м² | 625 мм | 620 мм | 200 мм | 195 мм | 20 | 63 | Оцинкованная сталь (INPLAST) | саморезы |
| STWS-625х225-SO | 0.085 м² | 625 мм | 620 мм | 225 мм | 220 мм | 23 | 63 | Оцинкованная сталь (INPLAST) | саморезы |
| STWS-625х250-SO | 0.094 м² | 625 мм | 620 мм | 250 мм | 245 мм | 25 | 63 | Оцинкованная сталь (INPLAST) | саморезы |
| STWS-625х300-SO | 0.113 м² | 625 мм | 620 мм | 300 мм | 295 мм | 30 | 63 | Оцинкованная сталь (INPLAST) | саморезы |
| STWS-625х325-SO | 0.122 м² | 625 мм | 620 мм | 325 мм | 320 мм | 33 | 63 | Оцинкованная сталь (INPLAST) | саморезы |
| STWS-625х350-SO | 0.132 м² | 625 мм | 620 мм | 350 мм | 345 мм | 35 | 63 | Оцинкованная сталь (INPLAST) | саморезы |
| STWS-625х400-SO | 0.150 м² | 625 мм | 620 мм | 400 мм | 395 мм | 40 | 63 | Оцинкованная сталь (INPLAST) | саморезы |
| STWS-625х425-SO | 0.160 м² | 625 мм | 620 мм | 425 мм | 420 мм | 43 | 63 | Оцинкованная сталь (INPLAST) | саморезы |
| STWS-625х450-SO | 0.169 м² | 625 мм | 620 мм | 450 мм | 445 мм | 45 | 63 | Оцинкованная сталь (INPLAST) | саморезы |
| STWS-625х500-SO | 0.188 м² | 625 мм | 620 мм | 500 мм | 495 мм | 50 | 63 | Оцинкованная сталь (INPLAST) | саморезы |
| STWS-625х525-SO | 0.197 м² | 625 мм | 620 мм | 525 мм | 520 мм | 53 | 63 | Оцинкованная сталь (INPLAST) | саморезы |
| STWS-625х550-SO | 0.207 м² | 625 мм | 620 мм | 550 мм | 545 мм | 55 | 63 | Оцинкованная сталь (INPLAST) | саморезы |
| STWS-625х600-SO | 0.226 м² | 625 мм | 620 мм | 600 мм | 595 мм | 60 | 63 | Оцинкованная сталь (INPLAST) | саморезы |
| STWS-625х625-SO | 0.235 м² | 625 мм | 620 мм | 625 мм | 620 мм | 63 | 63 | Оцинкованная сталь (INPLAST) | саморезы |
| STWS-650х100-SO | 0.039 м² | 650 мм | 645 мм | 100 мм | 95 мм | 10 | 65 | Оцинкованная сталь (INPLAST) | саморезы |
| STWS-650х125-SO | 0.049 м² | 650 мм | 645 мм | 125 мм | 120 мм | 13 | 65 | Оцинкованная сталь (INPLAST) | саморезы |
| STWS-650х150-SO | 0.059 м² | 650 мм | 645 мм | 150 мм | 145 мм | 15 | 65 | Оцинкованная сталь (INPLAST) | саморезы |
| STWS-650х200-SO | 0.078 м² | 650 мм | 645 мм | 200 мм | 195 мм | 20 | 65 | Оцинкованная сталь (INPLAST) | саморезы |
| STWS-650х225-SO | 0.088 м² | 650 мм | 645 мм | 225 мм | 220 мм | 23 | 65 | Оцинкованная сталь (INPLAST) | саморезы |
| STWS-650х250-SO | 0.098 м² | 650 мм | 645 мм | 250 мм | 245 мм | 25 | 65 | Оцинкованная сталь (INPLAST) | саморезы |
| STWS-650х300-SO | 0.117 м² | 650 мм | 645 мм | 300 мм | 295 мм | 30 | 65 | Оцинкованная сталь (INPLAST) | саморезы |
| STWS-650х325-SO | 0.127 м² | 650 мм | 645 мм | 325 мм | 320 мм | 33 | 65 | Оцинкованная сталь (INPLAST) | саморезы |
| STWS-650х350-SO | 0.137 м² | 650 мм | 645 мм | 350 мм | 345 мм | 35 | 65 | Оцинкованная сталь (INPLAST) | саморезы |
| STWS-650х400-SO | 0.156 м² | 650 мм | 645 мм | 400 мм | 395 мм | 40 | 65 | Оцинкованная сталь (INPLAST) | саморезы |
| STWS-650х425-SO | 0.166 м² | 650 мм | 645 мм | 425 мм | 420 мм | 43 | 65 | Оцинкованная сталь (INPLAST) | саморезы |
| STWS-650х450-SO | 0.176 м² | 650 мм | 645 мм | 450 мм | 445 мм | 45 | 65 | Оцинкованная сталь (INPLAST) | саморезы |
| STWS-650х500-SO | 0.196 м² | 650 мм | 645 мм | 500 мм | 495 мм | 50 | 65 | Оцинкованная сталь (INPLAST) | саморезы |
| STWS-650х525-SO | 0.205 м² | 650 мм | 645 мм | 525 мм | 520 мм | 53 | 65 | Оцинкованная сталь (INPLAST) | саморезы |
| STWS-650х550-SO | 0.215 м² | 650 мм | 645 мм | 550 мм | 545 мм | 55 | 65 | Оцинкованная сталь (INPLAST) | саморезы |
| STWS-650х600-SO | 0.235 м² | 650 мм | 645 мм | 600 мм | 595 мм | 60 | 65 | Оцинкованная сталь (INPLAST) | саморезы |
| STWS-650х625-SO | 0.244 м² | 650 мм | 645 мм | 625 мм | 620 мм | 63 | 65 | Оцинкованная сталь (INPLAST) | саморезы |
| STWS-650х650-SO | 0.254 м² | 650 мм | 645 мм | 650 мм | 645 мм | 65 | 65 | Оцинкованная сталь (INPLAST) | саморезы |
| STWS-700х100-SO | 0.042 м² | 700 мм | 695 мм | 100 мм | 95 мм | 10 | 70 | Оцинкованная сталь (INPLAST) | саморезы |
| STWS-700х125-SO | 0.053 м² | 700 мм | 695 мм | 125 мм | 120 мм | 13 | 70 | Оцинкованная сталь (INPLAST) | саморезы |
| STWS-700х150-SO | 0.063 м² | 700 мм | 695 мм | 150 мм | 145 мм | 15 | 70 | Оцинкованная сталь (INPLAST) | саморезы |
| STWS-700х200-SO | 0.084 м² | 700 мм | 695 мм | 200 мм | 195 мм | 20 | 70 | Оцинкованная сталь (INPLAST) | саморезы |
| STWS-700х225-SO | 0.095 м² | 700 мм | 695 мм | 225 мм | 220 мм | 23 | 70 | Оцинкованная сталь (INPLAST) | саморезы |
| STWS-700х250-SO | 0.105 м² | 700 мм | 695 мм | 250 мм | 245 мм | 25 | 70 | Оцинкованная сталь (INPLAST) | саморезы |
| STWS-700х300-SO | 0.126 м² | 700 мм | 695 мм | 300 мм | 295 мм | 30 | 70 | Оцинкованная сталь (INPLAST) | саморезы |
| STWS-700х325-SO | 0.137 м² | 700 мм | 695 мм | 325 мм | 320 мм | 33 | 70 | Оцинкованная сталь (INPLAST) | саморезы |
| STWS-700х350-SO | 0.147 м² | 700 мм | 695 мм | 350 мм | 345 мм | 35 | 70 | Оцинкованная сталь (INPLAST) | саморезы |
| STWS-700х400-SO | 0.168 м² | 700 мм | 695 мм | 400 мм | 395 мм | 40 | 70 | Оцинкованная сталь (INPLAST) | саморезы |
| STWS-700х425-SO | 0.179 м² | 700 мм | 695 мм | 425 мм | 420 мм | 43 | 70 | Оцинкованная сталь (INPLAST) | саморезы |
| STWS-700х450-SO | 0.190 м² | 700 мм | 695 мм | 450 мм | 445 мм | 45 | 70 | Оцинкованная сталь (INPLAST) | саморезы |
| STWS-700х500-SO | 0.211 м² | 700 мм | 695 мм | 500 мм | 495 мм | 50 | 70 | Оцинкованная сталь (INPLAST) | саморезы |
| STWS-700х525-SO | 0.221 м² | 700 мм | 695 мм | 525 мм | 520 мм | 53 | 70 | Оцинкованная сталь (INPLAST) | саморезы |
| STWS-700х550-SO | 0.232 м² | 700 мм | 695 мм | 550 мм | 545 мм | 55 | 70 | Оцинкованная сталь (INPLAST) | саморезы |
| STWS-700х600-SO | 0.253 м² | 700 мм | 695 мм | 600 мм | 595 мм | 60 | 70 | Оцинкованная сталь (INPLAST) | саморезы |
| STWS-700х625-SO | 0.263 м² | 700 мм | 695 мм | 625 мм | 620 мм | 63 | 70 | Оцинкованная сталь (INPLAST) | саморезы |
| STWS-700х650-SO | 0.274 м² | 700 мм | 695 мм | 650 мм | 645 мм | 65 | 70 | Оцинкованная сталь (INPLAST) | саморезы |
| STWS-725х100-SO | 0.044 м² | 725 мм | 720 мм | 100 мм | 95 мм | 10 | 73 | Оцинкованная сталь (INPLAST) | саморезы |
| STWS-725х125-SO | 0.055 м² | 725 мм | 720 мм | 125 мм | 120 мм | 13 | 73 | Оцинкованная сталь (INPLAST) | саморезы |
| STWS-725х150-SO | 0.065 м² | 725 мм | 720 мм | 150 мм | 145 мм | 15 | 73 | Оцинкованная сталь (INPLAST) | саморезы |
| STWS-725х200-SO | 0.087 м² | 725 мм | 720 мм | 200 мм | 195 мм | 20 | 73 | Оцинкованная сталь (INPLAST) | саморезы |
| STWS-725х225-SO | 0.098 м² | 725 мм | 720 мм | 225 мм | 220 мм | 23 | 73 | Оцинкованная сталь (INPLAST) | саморезы |
| STWS-725х250-SO | 0.109 м² | 725 мм | 720 мм | 250 мм | 245 мм | 25 | 73 | Оцинкованная сталь (INPLAST) | саморезы |
| STWS-725х300-SO | 0.131 м² | 725 мм | 720 мм | 300 мм | 295 мм | 30 | 73 | Оцинкованная сталь (INPLAST) | саморезы |
| STWS-725х325-SO | 0.142 м² | 725 мм | 720 мм | 325 мм | 320 мм | 33 | 73 | Оцинкованная сталь (INPLAST) | саморезы |
| STWS-725х350-SO | 0.153 м² | 725 мм | 720 мм | 350 мм | 345 мм | 35 | 73 | Оцинкованная сталь (INPLAST) | саморезы |
| STWS-725х400-SO | 0.174 м² | 725 мм | 720 мм | 400 мм | 395 мм | 40 | 73 | Оцинкованная сталь (INPLAST) | саморезы |
| STWS-725х425-SO | 0.185 м² | 725 мм | 720 мм | 425 мм | 420 мм | 43 | 73 | Оцинкованная сталь (INPLAST) | саморезы |
| STWS-725х450-SO | 0.196 м² | 725 мм | 720 мм | 450 мм | 445 мм | 45 | 73 | Оцинкованная сталь (INPLAST) | саморезы |
| STWS-725х500-SO | 0.218 м² | 725 мм | 720 мм | 500 мм | 495 мм | 50 | 73 | Оцинкованная сталь (INPLAST) | саморезы |
| STWS-725х525-SO | 0.229 м² | 725 мм | 720 мм | 525 мм | 520 мм | 53 | 73 | Оцинкованная сталь (INPLAST) | саморезы |
| STWS-725х550-SO | 0.240 м² | 725 мм | 720 мм | 550 мм | 545 мм | 55 | 73 | Оцинкованная сталь (INPLAST) | саморезы |
| STWS-725х600-SO | 0.262 м² | 725 мм | 720 мм | 600 мм | 595 мм | 60 | 73 | Оцинкованная сталь (INPLAST) | саморезы |
| STWS-725х625-SO | 0.273 м² | 725 мм | 720 мм | 625 мм | 620 мм | 63 | 73 | Оцинкованная сталь (INPLAST) | саморезы |
| STWS-725х650-SO | 0.284 м² | 725 мм | 720 мм | 650 мм | 645 мм | 65 | 73 | Оцинкованная сталь (INPLAST) | саморезы |
| STWS-750х100-SO | 0.045 м² | 750 мм | 745 мм | 100 мм | 95 мм | 10 | 75 | Оцинкованная сталь (INPLAST) | саморезы |
| STWS-750х125-SO | 0.056 м² | 750 мм | 745 мм | 125 мм | 120 мм | 13 | 75 | Оцинкованная сталь (INPLAST) | саморезы |
| STWS-750х150-SO | 0.068 м² | 750 мм | 745 мм | 150 мм | 145 мм | 15 | 75 | Оцинкованная сталь (INPLAST) | саморезы |
| STWS-750х200-SO | 0.090 м² | 750 мм | 745 мм | 200 мм | 195 мм | 20 | 75 | Оцинкованная сталь (INPLAST) | саморезы |
| STWS-750х225-SO | 0.102 м² | 750 мм | 745 мм | 225 мм | 220 мм | 23 | 75 | Оцинкованная сталь (INPLAST) | саморезы |
| STWS-750х250-SO | 0.113 м² | 750 мм | 745 мм | 250 мм | 245 мм | 25 | 75 | Оцинкованная сталь (INPLAST) | саморезы |
| STWS-750х300-SO | 0.135 м² | 750 мм | 745 мм | 300 мм | 295 мм | 30 | 75 | Оцинкованная сталь (INPLAST) | саморезы |
| STWS-750х325-SO | 0.147 м² | 750 мм | 745 мм | 325 мм | 320 мм | 33 | 75 | Оцинкованная сталь (INPLAST) | саморезы |
| STWS-750х350-SO | 0.158 м² | 750 мм | 745 мм | 350 мм | 345 мм | 35 | 75 | Оцинкованная сталь (INPLAST) | саморезы |
| STWS-750х400-SO | 0.180 м² | 750 мм | 745 мм | 400 мм | 395 мм | 40 | 75 | Оцинкованная сталь (INPLAST) | саморезы |
| STWS-750х425-SO | 0.192 м² | 750 мм | 745 мм | 425 мм | 420 мм | 43 | 75 | Оцинкованная сталь (INPLAST) | саморезы |
| STWS-750х450-SO | 0.203 м² | 750 мм | 745 мм | 450 мм | 445 мм | 45 | 75 | Оцинкованная сталь (INPLAST) | саморезы |
| STWS-750х500-SO | 0.226 м² | 750 мм | 745 мм | 500 мм | 495 мм | 50 | 75 | Оцинкованная сталь (INPLAST) | саморезы |
| STWS-750х525-SO | 0.237 м² | 750 мм | 745 мм | 525 мм | 520 мм | 53 | 75 | Оцинкованная сталь (INPLAST) | саморезы |
| STWS-750х550-SO | 0.248 м² | 750 мм | 745 мм | 550 мм | 545 мм | 55 | 75 | Оцинкованная сталь (INPLAST) | саморезы |
| STWS-750х600-SO | 0.271 м² | 750 мм | 745 мм | 600 мм | 595 мм | 60 | 75 | Оцинкованная сталь (INPLAST) | саморезы |
| STWS-750х625-SO | 0.282 м² | 750 мм | 745 мм | 625 мм | 620 мм | 63 | 75 | Оцинкованная сталь (INPLAST) | саморезы |
| STWS-750х650-SO | 0.293 м² | 750 мм | 745 мм | 650 мм | 645 мм | 65 | 75 | Оцинкованная сталь (INPLAST) | саморезы |
| STWS-800х100-SO | 0.048 м² | 800 мм | 795 мм | 100 мм | 95 мм | 10 | 80 | Оцинкованная сталь (INPLAST) | саморезы |
| STWS-800х125-SO | 0.060 м² | 800 мм | 795 мм | 125 мм | 120 мм | 13 | 80 | Оцинкованная сталь (INPLAST) | саморезы |
| STWS-800х150-SO | 0.072 м² | 800 мм | 795 мм | 150 мм | 145 мм | 15 | 80 | Оцинкованная сталь (INPLAST) | саморезы |
| STWS-800х200-SO | 0.096 м² | 800 мм | 795 мм | 200 мм | 195 мм | 20 | 80 | Оцинкованная сталь (INPLAST) | саморезы |
| STWS-800х225-SO | 0.108 м² | 800 мм | 795 мм | 225 мм | 220 мм | 23 | 80 | Оцинкованная сталь (INPLAST) | саморезы |
| STWS-800х250-SO | 0.120 м² | 800 мм | 795 мм | 250 мм | 245 мм | 25 | 80 | Оцинкованная сталь (INPLAST) | саморезы |
| STWS-800х300-SO | 0.144 м² | 800 мм | 795 мм | 300 мм | 295 мм | 30 | 80 | Оцинкованная сталь (INPLAST) | саморезы |
| STWS-800х325-SO | 0.156 м² | 800 мм | 795 мм | 325 мм | 320 мм | 33 | 80 | Оцинкованная сталь (INPLAST) | саморезы |
| STWS-800х350-SO | 0.168 м² | 800 мм | 795 мм | 350 мм | 345 мм | 35 | 80 | Оцинкованная сталь (INPLAST) | саморезы |
| STWS-800х400-SO | 0.193 м² | 800 мм | 795 мм | 400 мм | 395 мм | 40 | 80 | Оцинкованная сталь (INPLAST) | саморезы |
| STWS-800х425-SO | 0.205 м² | 800 мм | 795 мм | 425 мм | 420 мм | 43 | 80 | Оцинкованная сталь (INPLAST) | саморезы |
| STWS-800х450-SO | 0.217 м² | 800 мм | 795 мм | 450 мм | 445 мм | 45 | 80 | Оцинкованная сталь (INPLAST) | саморезы |
| STWS-800х500-SO | 0.241 м² | 800 мм | 795 мм | 500 мм | 495 мм | 50 | 80 | Оцинкованная сталь (INPLAST) | саморезы |
| STWS-800х525-SO | 0.253 м² | 800 мм | 795 мм | 525 мм | 520 мм | 53 | 80 | Оцинкованная сталь (INPLAST) | саморезы |
| STWS-800х550-SO | 0.265 м² | 800 мм | 795 мм | 550 мм | 545 мм | 55 | 80 | Оцинкованная сталь (INPLAST) | саморезы |
| STWS-800х600-SO | 0.289 м² | 800 мм | 795 мм | 600 мм | 595 мм | 60 | 80 | Оцинкованная сталь (INPLAST) | саморезы |
| STWS-800х625-SO | 0.301 м² | 800 мм | 795 мм | 625 мм | 620 мм | 63 | 80 | Оцинкованная сталь (INPLAST) | саморезы |
| STWS-800х650-SO | 0.313 м² | 800 мм | 795 мм | 650 мм | 645 мм | 65 | 80 | Оцинкованная сталь (INPLAST) | саморезы |
| STWS-825х100-SO | 0.050 м² | 825 мм | 820 мм | 100 мм | 95 мм | 10 | 83 | Оцинкованная сталь (INPLAST) | саморезы |
| STWS-825х125-SO | 0.062 м² | 825 мм | 820 мм | 125 мм | 120 мм | 13 | 83 | Оцинкованная сталь (INPLAST) | саморезы |
| STWS-825х150-SO | 0.074 м² | 825 мм | 820 мм | 150 мм | 145 мм | 15 | 83 | Оцинкованная сталь (INPLAST) | саморезы |
| STWS-825х200-SO | 0.099 м² | 825 мм | 820 мм | 200 мм | 195 мм | 20 | 83 | Оцинкованная сталь (INPLAST) | саморезы |
| STWS-825х225-SO | 0.112 м² | 825 мм | 820 мм | 225 мм | 220 мм | 23 | 83 | Оцинкованная сталь (INPLAST) | саморезы |
| STWS-825х250-SO | 0.124 м² | 825 мм | 820 мм | 250 мм | 245 мм | 25 | 83 | Оцинкованная сталь (INPLAST) | саморезы |
| STWS-825х300-SO | 0.149 м² | 825 мм | 820 мм | 300 мм | 295 мм | 30 | 83 | Оцинкованная сталь (INPLAST) | саморезы |
| STWS-825х325-SO | 0.161 м² | 825 мм | 820 мм | 325 мм | 320 мм | 33 | 83 | Оцинкованная сталь (INPLAST) | саморезы |
| STWS-825х350-SO | 0.174 м² | 825 мм | 820 мм | 350 мм | 345 мм | 35 | 83 | Оцинкованная сталь (INPLAST) | саморезы |
| STWS-825х400-SO | 0.199 м² | 825 мм | 820 мм | 400 мм | 395 мм | 40 | 83 | Оцинкованная сталь (INPLAST) | саморезы |
| STWS-825х425-SO | 0.211 м² | 825 мм | 820 мм | 425 мм | 420 мм | 43 | 83 | Оцинкованная сталь (INPLAST) | саморезы |
| STWS-825х450-SO | 0.223 м² | 825 мм | 820 мм | 450 мм | 445 мм | 45 | 83 | Оцинкованная сталь (INPLAST) | саморезы |
| STWS-825х500-SO | 0.248 м² | 825 мм | 820 мм | 500 мм | 495 мм | 50 | 83 | Оцинкованная сталь (INPLAST) | саморезы |
| STWS-825х525-SO | 0.261 м² | 825 мм | 820 мм | 525 мм | 520 мм | 53 | 83 | Оцинкованная сталь (INPLAST) | саморезы |
| STWS-825х550-SO | 0.273 м² | 825 мм | 820 мм | 550 мм | 545 мм | 55 | 83 | Оцинкованная сталь (INPLAST) | саморезы |
| STWS-825х600-SO | 0.298 м² | 825 мм | 820 мм | 600 мм | 595 мм | 60 | 83 | Оцинкованная сталь (INPLAST) | саморезы |
| STWS-825х625-SO | 0.310 м² | 825 мм | 820 мм | 625 мм | 620 мм | 63 | 83 | Оцинкованная сталь (INPLAST) | саморезы |
| STWS-825х650-SO | 0.323 м² | 825 мм | 820 мм | 650 мм | 645 мм | 65 | 83 | Оцинкованная сталь (INPLAST) | саморезы |
| STWS-850х100-SO | 0.051 м² | 850 мм | 845 мм | 100 мм | 95 мм | 10 | 85 | Оцинкованная сталь (INPLAST) | саморезы |
| STWS-850х125-SO | 0.064 м² | 850 мм | 845 мм | 125 мм | 120 мм | 13 | 85 | Оцинкованная сталь (INPLAST) | саморезы |
| STWS-850х150-SO | 0.077 м² | 850 мм | 845 мм | 150 мм | 145 мм | 15 | 85 | Оцинкованная сталь (INPLAST) | саморезы |
| STWS-850х200-SO | 0.102 м² | 850 мм | 845 мм | 200 мм | 195 мм | 20 | 85 | Оцинкованная сталь (INPLAST) | саморезы |
| STWS-850х225-SO | 0.115 м² | 850 мм | 845 мм | 225 мм | 220 мм | 23 | 85 | Оцинкованная сталь (INPLAST) | саморезы |
| STWS-850х250-SO | 0.128 м² | 850 мм | 845 мм | 250 мм | 245 мм | 25 | 85 | Оцинкованная сталь (INPLAST) | саморезы |
| STWS-850х300-SO | 0.153 м² | 850 мм | 845 мм | 300 мм | 295 мм | 30 | 85 | Оцинкованная сталь (INPLAST) | саморезы |
| STWS-850х325-SO | 0.166 м² | 850 мм | 845 мм | 325 мм | 320 мм | 33 | 85 | Оцинкованная сталь (INPLAST) | саморезы |
| STWS-850х350-SO | 0.179 м² | 850 мм | 845 мм | 350 мм | 345 мм | 35 | 85 | Оцинкованная сталь (INPLAST) | саморезы |
| STWS-850х400-SO | 0.205 м² | 850 мм | 845 мм | 400 мм | 395 мм | 40 | 85 | Оцинкованная сталь (INPLAST) | саморезы |
| STWS-850х425-SO | 0.217 м² | 850 мм | 845 мм | 425 мм | 420 мм | 43 | 85 | Оцинкованная сталь (INPLAST) | саморезы |
| STWS-850х450-SO | 0.230 м² | 850 мм | 845 мм | 450 мм | 445 мм | 45 | 85 | Оцинкованная сталь (INPLAST) | саморезы |
| STWS-850х500-SO | 0.256 м² | 850 мм | 845 мм | 500 мм | 495 мм | 50 | 85 | Оцинкованная сталь (INPLAST) | саморезы |
| STWS-850х525-SO | 0.268 м² | 850 мм | 845 мм | 525 мм | 520 мм | 53 | 85 | Оцинкованная сталь (INPLAST) | саморезы |
| STWS-850х550-SO | 0.281 м² | 850 мм | 845 мм | 550 мм | 545 мм | 55 | 85 | Оцинкованная сталь (INPLAST) | саморезы |
| STWS-850х600-SO | 0.307 м² | 850 мм | 845 мм | 600 мм | 595 мм | 60 | 85 | Оцинкованная сталь (INPLAST) | саморезы |
| STWS-850х625-SO | 0.320 м² | 850 мм | 845 мм | 625 мм | 620 мм | 63 | 85 | Оцинкованная сталь (INPLAST) | саморезы |
| STWS-850х650-SO | 0.332 м² | 850 мм | 845 мм | 650 мм | 645 мм | 65 | 85 | Оцинкованная сталь (INPLAST) | саморезы |
| STWS-900х100-SO | 0.054 м² | 900 мм | 895 мм | 100 мм | 95 мм | 10 | 90 | Оцинкованная сталь (INPLAST) | саморезы |
| STWS-900х125-SO | 0.068 м² | 900 мм | 895 мм | 125 мм | 120 мм | 13 | 90 | Оцинкованная сталь (INPLAST) | саморезы |
| STWS-900х150-SO | 0.081 м² | 900 мм | 895 мм | 150 мм | 145 мм | 15 | 90 | Оцинкованная сталь (INPLAST) | саморезы |
| STWS-900х200-SO | 0.108 м² | 900 мм | 895 мм | 200 мм | 195 мм | 20 | 90 | Оцинкованная сталь (INPLAST) | саморезы |
| STWS-900х225-SO | 0.122 м² | 900 мм | 895 мм | 225 мм | 220 мм | 23 | 90 | Оцинкованная сталь (INPLAST) | саморезы |
| STWS-900х250-SO | 0.135 м² | 900 мм | 895 мм | 250 мм | 245 мм | 25 | 90 | Оцинкованная сталь (INPLAST) | саморезы |
| STWS-900х300-SO | 0.162 м² | 900 мм | 895 мм | 300 мм | 295 мм | 30 | 90 | Оцинкованная сталь (INPLAST) | саморезы |
| STWS-900х325-SO | 0.176 м² | 900 мм | 895 мм | 325 мм | 320 мм | 33 | 90 | Оцинкованная сталь (INPLAST) | саморезы |
| STWS-900х350-SO | 0.190 м² | 900 мм | 895 мм | 350 мм | 345 мм | 35 | 90 | Оцинкованная сталь (INPLAST) | саморезы |
| STWS-900х400-SO | 0.217 м² | 900 мм | 895 мм | 400 мм | 395 мм | 40 | 90 | Оцинкованная сталь (INPLAST) | саморезы |
| STWS-900х425-SO | 0.230 м² | 900 мм | 895 мм | 425 мм | 420 мм | 43 | 90 | Оцинкованная сталь (INPLAST) | саморезы |
| STWS-900х450-SO | 0.244 м² | 900 мм | 895 мм | 450 мм | 445 мм | 45 | 90 | Оцинкованная сталь (INPLAST) | саморезы |
| STWS-900х500-SO | 0.271 м² | 900 мм | 895 мм | 500 мм | 495 мм | 50 | 90 | Оцинкованная сталь (INPLAST) | саморезы |
| STWS-900х525-SO | 0.284 м² | 900 мм | 895 мм | 525 мм | 520 мм | 53 | 90 | Оцинкованная сталь (INPLAST) | саморезы |
| STWS-900х550-SO | 0.298 м² | 900 мм | 895 мм | 550 мм | 545 мм | 55 | 90 | Оцинкованная сталь (INPLAST) | саморезы |
| STWS-900х600-SO | 0.325 м² | 900 мм | 895 мм | 600 мм | 595 мм | 60 | 90 | Оцинкованная сталь (INPLAST) | саморезы |
| STWS-900х625-SO | 0.338 м² | 900 мм | 895 мм | 625 мм | 620 мм | 63 | 90 | Оцинкованная сталь (INPLAST) | саморезы |
| STWS-900х650-SO | 0.352 м² | 900 мм | 895 мм | 650 мм | 645 мм | 65 | 90 | Оцинкованная сталь (INPLAST) | саморезы |
| STWS-925х100-SO | 0.056 м² | 925 мм | 920 мм | 100 мм | 95 мм | 10 | 93 | Оцинкованная сталь (INPLAST) | саморезы |
| STWS-925х125-SO | 0.070 м² | 925 мм | 920 мм | 125 мм | 120 мм | 13 | 93 | Оцинкованная сталь (INPLAST) | саморезы |
| STWS-925х150-SO | 0.083 м² | 925 мм | 920 мм | 150 мм | 145 мм | 15 | 93 | Оцинкованная сталь (INPLAST) | саморезы |
| STWS-925х200-SO | 0.111 м² | 925 мм | 920 мм | 200 мм | 195 мм | 20 | 93 | Оцинкованная сталь (INPLAST) | саморезы |
| STWS-925х225-SO | 0.125 м² | 925 мм | 920 мм | 225 мм | 220 мм | 23 | 93 | Оцинкованная сталь (INPLAST) | саморезы |
| STWS-925х250-SO | 0.139 м² | 925 мм | 920 мм | 250 мм | 245 мм | 25 | 93 | Оцинкованная сталь (INPLAST) | саморезы |
| STWS-925х300-SO | 0.167 м² | 925 мм | 920 мм | 300 мм | 295 мм | 30 | 93 | Оцинкованная сталь (INPLAST) | саморезы |
| STWS-925х325-SO | 0.181 м² | 925 мм | 920 мм | 325 мм | 320 мм | 33 | 93 | Оцинкованная сталь (INPLAST) | саморезы |
| STWS-925х350-SO | 0.195 м² | 925 мм | 920 мм | 350 мм | 345 мм | 35 | 93 | Оцинкованная сталь (INPLAST) | саморезы |
| STWS-925х400-SO | 0.223 м² | 925 мм | 920 мм | 400 мм | 395 мм | 40 | 93 | Оцинкованная сталь (INPLAST) | саморезы |
| STWS-925х425-SO | 0.237 м² | 925 мм | 920 мм | 425 мм | 420 мм | 43 | 93 | Оцинкованная сталь (INPLAST) | саморезы |
| STWS-925х450-SO | 0.250 м² | 925 мм | 920 мм | 450 мм | 445 мм | 45 | 93 | Оцинкованная сталь (INPLAST) | саморезы |
| STWS-925х500-SO | 0.278 м² | 925 мм | 920 мм | 500 мм | 495 мм | 50 | 93 | Оцинкованная сталь (INPLAST) | саморезы |
| STWS-925х525-SO | 0.292 м² | 925 мм | 920 мм | 525 мм | 520 мм | 53 | 93 | Оцинкованная сталь (INPLAST) | саморезы |
| STWS-925х550-SO | 0.306 м² | 925 мм | 920 мм | 550 мм | 545 мм | 55 | 93 | Оцинкованная сталь (INPLAST) | саморезы |
| STWS-925х600-SO | 0.334 м² | 925 мм | 920 мм | 600 мм | 595 мм | 60 | 93 | Оцинкованная сталь (INPLAST) | саморезы |
| STWS-925х625-SO | 0.348 м² | 925 мм | 920 мм | 625 мм | 620 мм | 63 | 93 | Оцинкованная сталь (INPLAST) | саморезы |
| STWS-925х650-SO | 0.362 м² | 925 мм | 920 мм | 650 мм | 645 мм | 65 | 93 | Оцинкованная сталь (INPLAST) | саморезы |
| STWS-950х100-SO | 0.057 м² | 950 мм | 945 мм | 100 мм | 95 мм | 10 | 95 | Оцинкованная сталь (INPLAST) | саморезы |
| STWS-950х125-SO | 0.071 м² | 950 мм | 945 мм | 125 мм | 120 мм | 13 | 95 | Оцинкованная сталь (INPLAST) | саморезы |
| STWS-950х150-SO | 0.086 м² | 950 мм | 945 мм | 150 мм | 145 мм | 15 | 95 | Оцинкованная сталь (INPLAST) | саморезы |
| STWS-950х200-SO | 0.114 м² | 950 мм | 945 мм | 200 мм | 195 мм | 20 | 95 | Оцинкованная сталь (INPLAST) | саморезы |
| STWS-950х225-SO | 0.129 м² | 950 мм | 945 мм | 225 мм | 220 мм | 23 | 95 | Оцинкованная сталь (INPLAST) | саморезы |
| STWS-950х250-SO | 0.143 м² | 950 мм | 945 мм | 250 мм | 245 мм | 25 | 95 | Оцинкованная сталь (INPLAST) | саморезы |
| STWS-950х300-SO | 0.171 м² | 950 мм | 945 мм | 300 мм | 295 мм | 30 | 95 | Оцинкованная сталь (INPLAST) | саморезы |
| STWS-950х325-SO | 0.186 м² | 950 мм | 945 мм | 325 мм | 320 мм | 33 | 95 | Оцинкованная сталь (INPLAST) | саморезы |
| STWS-950х350-SO | 0.200 м² | 950 мм | 945 мм | 350 мм | 345 мм | 35 | 95 | Оцинкованная сталь (INPLAST) | саморезы |
| STWS-950х400-SO | 0.229 м² | 950 мм | 945 мм | 400 мм | 395 мм | 40 | 95 | Оцинкованная сталь (INPLAST) | саморезы |
| STWS-950х425-SO | 0.243 м² | 950 мм | 945 мм | 425 мм | 420 мм | 43 | 95 | Оцинкованная сталь (INPLAST) | саморезы |
| STWS-950х450-SO | 0.257 м² | 950 мм | 945 мм | 450 мм | 445 мм | 45 | 95 | Оцинкованная сталь (INPLAST) | саморезы |
| STWS-950х500-SO | 0.286 м² | 950 мм | 945 мм | 500 мм | 495 мм | 50 | 95 | Оцинкованная сталь (INPLAST) | саморезы |
| STWS-950х525-SO | 0.300 м² | 950 мм | 945 мм | 525 мм | 520 мм | 53 | 95 | Оцинкованная сталь (INPLAST) | саморезы |
| STWS-950х550-SO | 0.314 м² | 950 мм | 945 мм | 550 мм | 545 мм | 55 | 95 | Оцинкованная сталь (INPLAST) | саморезы |
| STWS-950х600-SO | 0.343 м² | 950 мм | 945 мм | 600 мм | 595 мм | 60 | 95 | Оцинкованная сталь (INPLAST) | саморезы |
| STWS-950х625-SO | 0.357 м² | 950 мм | 945 мм | 625 мм | 620 мм | 63 | 95 | Оцинкованная сталь (INPLAST) | саморезы |
| STWS-950х650-SO | 0.371 м² | 950 мм | 945 мм | 650 мм | 645 мм | 65 | 95 | Оцинкованная сталь (INPLAST) | саморезы |
| STWS-1000х100-SO | 0.060 м² | 1000 мм | 995 мм | 100 мм | 95 мм | 10 | 100 | Оцинкованная сталь (INPLAST) | саморезы |
| STWS-1000х125-SO | 0.075 м² | 1000 мм | 995 мм | 125 мм | 120 мм | 13 | 100 | Оцинкованная сталь (INPLAST) | саморезы |
| STWS-1000х150-SO | 0.090 м² | 1000 мм | 995 мм | 150 мм | 145 мм | 15 | 100 | Оцинкованная сталь (INPLAST) | саморезы |
| STWS-1000х200-SO | 0.120 м² | 1000 мм | 995 мм | 200 мм | 195 мм | 20 | 100 | Оцинкованная сталь (INPLAST) | саморезы |
| STWS-1000х225-SO | 0.135 м² | 1000 мм | 995 мм | 225 мм | 220 мм | 23 | 100 | Оцинкованная сталь (INPLAST) | саморезы |
| STWS-1000х250-SO | 0.150 м² | 1000 мм | 995 мм | 250 мм | 245 мм | 25 | 100 | Оцинкованная сталь (INPLAST) | саморезы |
| STWS-1000х300-SO | 0.180 м² | 1000 мм | 995 мм | 300 мм | 295 мм | 30 | 100 | Оцинкованная сталь (INPLAST) | саморезы |
| STWS-1000х325-SO | 0.196 м² | 1000 мм | 995 мм | 325 мм | 320 мм | 33 | 100 | Оцинкованная сталь (INPLAST) | саморезы |
| STWS-1000х350-SO | 0.211 м² | 1000 мм | 995 мм | 350 мм | 345 мм | 35 | 100 | Оцинкованная сталь (INPLAST) | саморезы |
| STWS-1000х400-SO | 0.241 м² | 1000 мм | 995 мм | 400 мм | 395 мм | 40 | 100 | Оцинкованная сталь (INPLAST) | саморезы |
| STWS-1000х425-SO | 0.256 м² | 1000 мм | 995 мм | 425 мм | 420 мм | 43 | 100 | Оцинкованная сталь (INPLAST) | саморезы |
| STWS-1000х450-SO | 0.271 м² | 1000 мм | 995 мм | 450 мм | 445 мм | 45 | 100 | Оцинкованная сталь (INPLAST) | саморезы |
| STWS-1000х500-SO | 0.301 м² | 1000 мм | 995 мм | 500 мм | 495 мм | 50 | 100 | Оцинкованная сталь (INPLAST) | саморезы |
| STWS-1000х525-SO | 0.316 м² | 1000 мм | 995 мм | 525 мм | 520 мм | 53 | 100 | Оцинкованная сталь (INPLAST) | саморезы |
| STWS-1000х550-SO | 0.331 м² | 1000 мм | 995 мм | 550 мм | 545 мм | 55 | 100 | Оцинкованная сталь (INPLAST) | саморезы |
| STWS-1000х600-SO | 0.361 м² | 1000 мм | 995 мм | 600 мм | 595 мм | 60 | 100 | Оцинкованная сталь (INPLAST) | саморезы |
| STWS-1000х625-SO | 0.376 м² | 1000 мм | 995 мм | 625 мм | 620 мм | 63 | 100 | Оцинкованная сталь (INPLAST) | саморезы |
| STWS-1000х650-SO | 0.391 м² | 1000 мм | 995 мм | 650 мм | 645 мм | 65 | 100 | Оцинкованная сталь (INPLAST) | саморезы |
| STWS-1025х100-SO | 0.062 м² | 1025 мм | 1020 мм | 100 мм | 95 мм | 10 | 103 | Оцинкованная сталь (INPLAST) | саморезы |
| STWS-1025х125-SO | 0.077 м² | 1025 мм | 1020 мм | 125 мм | 120 мм | 13 | 103 | Оцинкованная сталь (INPLAST) | саморезы |
| STWS-1025х150-SO | 0.092 м² | 1025 мм | 1020 мм | 150 мм | 145 мм | 15 | 103 | Оцинкованная сталь (INPLAST) | саморезы |
| STWS-1025х200-SO | 0.123 м² | 1025 мм | 1020 мм | 200 мм | 195 мм | 20 | 103 | Оцинкованная сталь (INPLAST) | саморезы |
| STWS-1025х225-SO | 0.139 м² | 1025 мм | 1020 мм | 225 мм | 220 мм | 23 | 103 | Оцинкованная сталь (INPLAST) | саморезы |
| STWS-1025х250-SO | 0.154 м² | 1025 мм | 1020 мм | 250 мм | 245 мм | 25 | 103 | Оцинкованная сталь (INPLAST) | саморезы |
| STWS-1025х300-SO | 0.185 м² | 1025 мм | 1020 мм | 300 мм | 295 мм | 30 | 103 | Оцинкованная сталь (INPLAST) | саморезы |
| STWS-1025х325-SO | 0.200 м² | 1025 мм | 1020 мм | 325 мм | 320 мм | 33 | 103 | Оцинкованная сталь (INPLAST) | саморезы |
| STWS-1025х350-SO | 0.216 м² | 1025 мм | 1020 мм | 350 мм | 345 мм | 35 | 103 | Оцинкованная сталь (INPLAST) | саморезы |
| STWS-1025х400-SO | 0.247 м² | 1025 мм | 1020 мм | 400 мм | 395 мм | 40 | 103 | Оцинкованная сталь (INPLAST) | саморезы |
| STWS-1025х425-SO | 0.262 м² | 1025 мм | 1020 мм | 425 мм | 420 мм | 43 | 103 | Оцинкованная сталь (INPLAST) | саморезы |
| STWS-1025х450-SO | 0.277 м² | 1025 мм | 1020 мм | 450 мм | 445 мм | 45 | 103 | Оцинкованная сталь (INPLAST) | саморезы |
| STWS-1025х500-SO | 0.308 м² | 1025 мм | 1020 мм | 500 мм | 495 мм | 50 | 103 | Оцинкованная сталь (INPLAST) | саморезы |
| STWS-1025х525-SO | 0.324 м² | 1025 мм | 1020 мм | 525 мм | 520 мм | 53 | 103 | Оцинкованная сталь (INPLAST) | саморезы |
| STWS-1025х550-SO | 0.339 м² | 1025 мм | 1020 мм | 550 мм | 545 мм | 55 | 103 | Оцинкованная сталь (INPLAST) | саморезы |
| STWS-1025х600-SO | 0.370 м² | 1025 мм | 1020 мм | 600 мм | 595 мм | 60 | 103 | Оцинкованная сталь (INPLAST) | саморезы |
| STWS-1025х625-SO | 0.385 м² | 1025 мм | 1020 мм | 625 мм | 620 мм | 63 | 103 | Оцинкованная сталь (INPLAST) | саморезы |
| STWS-1025х650-SO | 0.401 м² | 1025 мм | 1020 мм | 650 мм | 645 мм | 65 | 103 | Оцинкованная сталь (INPLAST) | саморезы |
| STWS-1050х100-SO | 0.063 м² | 1050 мм | 1045 мм | 100 мм | 95 мм | 10 | 105 | Оцинкованная сталь (INPLAST) | саморезы |
| STWS-1050х125-SO | 0.079 м² | 1050 мм | 1045 мм | 125 мм | 120 мм | 13 | 105 | Оцинкованная сталь (INPLAST) | саморезы |
| STWS-1050х150-SO | 0.095 м² | 1050 мм | 1045 мм | 150 мм | 145 мм | 15 | 105 | Оцинкованная сталь (INPLAST) | саморезы |
| STWS-1050х200-SO | 0.126 м² | 1050 мм | 1045 мм | 200 мм | 195 мм | 20 | 105 | Оцинкованная сталь (INPLAST) | саморезы |
| STWS-1050х225-SO | 0.142 м² | 1050 мм | 1045 мм | 225 мм | 220 мм | 23 | 105 | Оцинкованная сталь (INPLAST) | саморезы |
| STWS-1050х250-SO | 0.158 м² | 1050 мм | 1045 мм | 250 мм | 245 мм | 25 | 105 | Оцинкованная сталь (INPLAST) | саморезы |
| STWS-1050х300-SO | 0.190 м² | 1050 мм | 1045 мм | 300 мм | 295 мм | 30 | 105 | Оцинкованная сталь (INPLAST) | саморезы |
| STWS-1050х325-SO | 0.205 м² | 1050 мм | 1045 мм | 325 мм | 320 мм | 33 | 105 | Оцинкованная сталь (INPLAST) | саморезы |
| STWS-1050х350-SO | 0.221 м² | 1050 мм | 1045 мм | 350 мм | 345 мм | 35 | 105 | Оцинкованная сталь (INPLAST) | саморезы |
| STWS-1050х400-SO | 0.253 м² | 1050 мм | 1045 мм | 400 мм | 395 мм | 40 | 105 | Оцинкованная сталь (INPLAST) | саморезы |
| STWS-1050х425-SO | 0.268 м² | 1050 мм | 1045 мм | 425 мм | 420 мм | 43 | 105 | Оцинкованная сталь (INPLAST) | саморезы |
| STWS-1050х450-SO | 0.284 м² | 1050 мм | 1045 мм | 450 мм | 445 мм | 45 | 105 | Оцинкованная сталь (INPLAST) | саморезы |
| STWS-1050х500-SO | 0.316 м² | 1050 мм | 1045 мм | 500 мм | 495 мм | 50 | 105 | Оцинкованная сталь (INPLAST) | саморезы |
| STWS-1050х525-SO | 0.332 м² | 1050 мм | 1045 мм | 525 мм | 520 мм | 53 | 105 | Оцинкованная сталь (INPLAST) | саморезы |
| STWS-1050х550-SO | 0.347 м² | 1050 мм | 1045 мм | 550 мм | 545 мм | 55 | 105 | Оцинкованная сталь (INPLAST) | саморезы |
| STWS-1050х600-SO | 0.379 м² | 1050 мм | 1045 мм | 600 мм | 595 мм | 60 | 105 | Оцинкованная сталь (INPLAST) | саморезы |
| STWS-1050х625-SO | 0.395 м² | 1050 мм | 1045 мм | 625 мм | 620 мм | 63 | 105 | Оцинкованная сталь (INPLAST) | саморезы |
| STWS-1050х650-SO | 0.411 м² | 1050 мм | 1045 мм | 650 мм | 645 мм | 65 | 105 | Оцинкованная сталь (INPLAST) | саморезы |
| STWS-1100х100-SO | 0.066 м² | 1100 мм | 1095 мм | 100 мм | 95 мм | 10 | 110 | Оцинкованная сталь (INPLAST) | саморезы |
| STWS-1100х125-SO | 0.083 м² | 1100 мм | 1095 мм | 125 мм | 120 мм | 13 | 110 | Оцинкованная сталь (INPLAST) | саморезы |
| STWS-1100х150-SO | 0.099 м² | 1100 мм | 1095 мм | 150 мм | 145 мм | 15 | 110 | Оцинкованная сталь (INPLAST) | саморезы |
| STWS-1100х200-SO | 0.132 м² | 1100 мм | 1095 мм | 200 мм | 195 мм | 20 | 110 | Оцинкованная сталь (INPLAST) | саморезы |
| STWS-1100х225-SO | 0.149 м² | 1100 мм | 1095 мм | 225 мм | 220 мм | 23 | 110 | Оцинкованная сталь (INPLAST) | саморезы |
| STWS-1100х250-SO | 0.165 м² | 1100 мм | 1095 мм | 250 мм | 245 мм | 25 | 110 | Оцинкованная сталь (INPLAST) | саморезы |
| STWS-1100х300-SO | 0.199 м² | 1100 мм | 1095 мм | 300 мм | 295 мм | 30 | 110 | Оцинкованная сталь (INPLAST) | саморезы |
| STWS-1100х325-SO | 0.215 м² | 1100 мм | 1095 мм | 325 мм | 320 мм | 33 | 110 | Оцинкованная сталь (INPLAST) | саморезы |
| STWS-1100х350-SO | 0.232 м² | 1100 мм | 1095 мм | 350 мм | 345 мм | 35 | 110 | Оцинкованная сталь (INPLAST) | саморезы |
| STWS-1100х400-SO | 0.265 м² | 1100 мм | 1095 мм | 400 мм | 395 мм | 40 | 110 | Оцинкованная сталь (INPLAST) | саморезы |
| STWS-1100х425-SO | 0.281 м² | 1100 мм | 1095 мм | 425 мм | 420 мм | 43 | 110 | Оцинкованная сталь (INPLAST) | саморезы |
| STWS-1100х450-SO | 0.298 м² | 1100 мм | 1095 мм | 450 мм | 445 мм | 45 | 110 | Оцинкованная сталь (INPLAST) | саморезы |
| STWS-1100х500-SO | 0.331 м² | 1100 мм | 1095 мм | 500 мм | 495 мм | 50 | 110 | Оцинкованная сталь (INPLAST) | саморезы |
| STWS-1100х525-SO | 0.347 м² | 1100 мм | 1095 мм | 525 мм | 520 мм | 53 | 110 | Оцинкованная сталь (INPLAST) | саморезы |
| STWS-1100х550-SO | 0.364 м² | 1100 мм | 1095 мм | 550 мм | 545 мм | 55 | 110 | Оцинкованная сталь (INPLAST) | саморезы |
| STWS-1100х600-SO | 0.397 м² | 1100 мм | 1095 мм | 600 мм | 595 мм | 60 | 110 | Оцинкованная сталь (INPLAST) | саморезы |
| STWS-1100х625-SO | 0.414 м² | 1100 мм | 1095 мм | 625 мм | 620 мм | 63 | 110 | Оцинкованная сталь (INPLAST) | саморезы |
| STWS-1100х650-SO | 0.430 м² | 1100 мм | 1095 мм | 650 мм | 645 мм | 65 | 110 | Оцинкованная сталь (INPLAST) | саморезы |
| STWS-1125х100-SO | 0.068 м² | 1125 мм | 1120 мм | 100 мм | 95 мм | 10 | 113 | Оцинкованная сталь (INPLAST) | саморезы |
| STWS-1125х125-SO | 0.085 м² | 1125 мм | 1120 мм | 125 мм | 120 мм | 13 | 113 | Оцинкованная сталь (INPLAST) | саморезы |
| STWS-1125х150-SO | 0.102 м² | 1125 мм | 1120 мм | 150 мм | 145 мм | 15 | 113 | Оцинкованная сталь (INPLAST) | саморезы |
| STWS-1125х200-SO | 0.135 м² | 1125 мм | 1120 мм | 200 мм | 195 мм | 20 | 113 | Оцинкованная сталь (INPLAST) | саморезы |
| STWS-1125х225-SO | 0.152 м² | 1125 мм | 1120 мм | 225 мм | 220 мм | 23 | 113 | Оцинкованная сталь (INPLAST) | саморезы |
| STWS-1125х250-SO | 0.169 м² | 1125 мм | 1120 мм | 250 мм | 245 мм | 25 | 113 | Оцинкованная сталь (INPLAST) | саморезы |
| STWS-1125х300-SO | 0.203 м² | 1125 мм | 1120 мм | 300 мм | 295 мм | 30 | 113 | Оцинкованная сталь (INPLAST) | саморезы |
| STWS-1125х325-SO | 0.220 м² | 1125 мм | 1120 мм | 325 мм | 320 мм | 33 | 113 | Оцинкованная сталь (INPLAST) | саморезы |
| STWS-1125х350-SO | 0.237 м² | 1125 мм | 1120 мм | 350 мм | 345 мм | 35 | 113 | Оцинкованная сталь (INPLAST) | саморезы |
| STWS-1125х400-SO | 0.271 м² | 1125 мм | 1120 мм | 400 мм | 395 мм | 40 | 113 | Оцинкованная сталь (INPLAST) | саморезы |
| STWS-1125х425-SO | 0.288 м² | 1125 мм | 1120 мм | 425 мм | 420 мм | 43 | 113 | Оцинкованная сталь (INPLAST) | саморезы |
| STWS-1125х450-SO | 0.305 м² | 1125 мм | 1120 мм | 450 мм | 445 мм | 45 | 113 | Оцинкованная сталь (INPLAST) | саморезы |
| STWS-1125х500-SO | 0.338 м² | 1125 мм | 1120 мм | 500 мм | 495 мм | 50 | 113 | Оцинкованная сталь (INPLAST) | саморезы |
| STWS-1125х525-SO | 0.355 м² | 1125 мм | 1120 мм | 525 мм | 520 мм | 53 | 113 | Оцинкованная сталь (INPLAST) | саморезы |
| STWS-1125х550-SO | 0.372 м² | 1125 мм | 1120 мм | 550 мм | 545 мм | 55 | 113 | Оцинкованная сталь (INPLAST) | саморезы |
| STWS-1125х600-SO | 0.406 м² | 1125 мм | 1120 мм | 600 мм | 595 мм | 60 | 113 | Оцинкованная сталь (INPLAST) | саморезы |
| STWS-1125х625-SO | 0.423 м² | 1125 мм | 1120 мм | 625 мм | 620 мм | 63 | 113 | Оцинкованная сталь (INPLAST) | саморезы |
| STWS-1125х650-SO | 0.440 м² | 1125 мм | 1120 мм | 650 мм | 645 мм | 65 | 113 | Оцинкованная сталь (INPLAST) | саморезы |
| STWS-1150х100-SO | 0.069 м² | 1150 мм | 1145 мм | 100 мм | 95 мм | 10 | 115 | Оцинкованная сталь (INPLAST) | саморезы |
| STWS-1150х125-SO | 0.086 м² | 1150 мм | 1145 мм | 125 мм | 120 мм | 13 | 115 | Оцинкованная сталь (INPLAST) | саморезы |
| STWS-1150х150-SO | 0.104 м² | 1150 мм | 1145 мм | 150 мм | 145 мм | 15 | 115 | Оцинкованная сталь (INPLAST) | саморезы |
| STWS-1150х200-SO | 0.138 м² | 1150 мм | 1145 мм | 200 мм | 195 мм | 20 | 115 | Оцинкованная сталь (INPLAST) | саморезы |
| STWS-1150х225-SO | 0.156 м² | 1150 мм | 1145 мм | 225 мм | 220 мм | 23 | 115 | Оцинкованная сталь (INPLAST) | саморезы |
| STWS-1150х250-SO | 0.173 м² | 1150 мм | 1145 мм | 250 мм | 245 мм | 25 | 115 | Оцинкованная сталь (INPLAST) | саморезы |
| STWS-1150х300-SO | 0.208 м² | 1150 мм | 1145 мм | 300 мм | 295 мм | 30 | 115 | Оцинкованная сталь (INPLAST) | саморезы |
| STWS-1150х325-SO | 0.225 м² | 1150 мм | 1145 мм | 325 мм | 320 мм | 33 | 115 | Оцинкованная сталь (INPLAST) | саморезы |
| STWS-1150х350-SO | 0.242 м² | 1150 мм | 1145 мм | 350 мм | 345 мм | 35 | 115 | Оцинкованная сталь (INPLAST) | саморезы |
| STWS-1150х400-SO | 0.277 м² | 1150 мм | 1145 мм | 400 мм | 395 мм | 40 | 115 | Оцинкованная сталь (INPLAST) | саморезы |
| STWS-1150х425-SO | 0.294 м² | 1150 мм | 1145 мм | 425 мм | 420 мм | 43 | 115 | Оцинкованная сталь (INPLAST) | саморезы |
| STWS-1150х450-SO | 0.311 м² | 1150 мм | 1145 мм | 450 мм | 445 мм | 45 | 115 | Оцинкованная сталь (INPLAST) | саморезы |
| STWS-1150х500-SO | 0.346 м² | 1150 мм | 1145 мм | 500 мм | 495 мм | 50 | 115 | Оцинкованная сталь (INPLAST) | саморезы |
| STWS-1150х525-SO | 0.363 м² | 1150 мм | 1145 мм | 525 мм | 520 мм | 53 | 115 | Оцинкованная сталь (INPLAST) | саморезы |
| STWS-1150х550-SO | 0.381 м² | 1150 мм | 1145 мм | 550 мм | 545 мм | 55 | 115 | Оцинкованная сталь (INPLAST) | саморезы |
| STWS-1150х600-SO | 0.415 м² | 1150 мм | 1145 мм | 600 мм | 595 мм | 60 | 115 | Оцинкованная сталь (INPLAST) | саморезы |
| STWS-1150х625-SO | 0.432 м² | 1150 мм | 1145 мм | 625 мм | 620 мм | 63 | 115 | Оцинкованная сталь (INPLAST) | саморезы |
| STWS-1150х650-SO | 0.450 м² | 1150 мм | 1145 мм | 650 мм | 645 мм | 65 | 115 | Оцинкованная сталь (INPLAST) | саморезы |
| STWS-1200х100-SO | 0.072 м² | 1200 мм | 1195 мм | 100 мм | 95 мм | 10 | 120 | Оцинкованная сталь (INPLAST) | саморезы |
| STWS-1200х125-SO | 0.090 м² | 1200 мм | 1195 мм | 125 мм | 120 мм | 13 | 120 | Оцинкованная сталь (INPLAST) | саморезы |
| STWS-1200х150-SO | 0.108 м² | 1200 мм | 1195 мм | 150 мм | 145 мм | 15 | 120 | Оцинкованная сталь (INPLAST) | саморезы |
| STWS-1200х200-SO | 0.144 м² | 1200 мм | 1195 мм | 200 мм | 195 мм | 20 | 120 | Оцинкованная сталь (INPLAST) | саморезы |
| STWS-1200х225-SO | 0.162 м² | 1200 мм | 1195 мм | 225 мм | 220 мм | 23 | 120 | Оцинкованная сталь (INPLAST) | саморезы |
| STWS-1200х250-SO | 0.180 м² | 1200 мм | 1195 мм | 250 мм | 245 мм | 25 | 120 | Оцинкованная сталь (INPLAST) | саморезы |
| STWS-1200х300-SO | 0.217 м² | 1200 мм | 1195 мм | 300 мм | 295 мм | 30 | 120 | Оцинкованная сталь (INPLAST) | саморезы |
| STWS-1200х325-SO | 0.235 м² | 1200 мм | 1195 мм | 325 мм | 320 мм | 33 | 120 | Оцинкованная сталь (INPLAST) | саморезы |
| STWS-1200х350-SO | 0.253 м² | 1200 мм | 1195 мм | 350 мм | 345 мм | 35 | 120 | Оцинкованная сталь (INPLAST) | саморезы |
| STWS-1200х400-SO | 0.289 м² | 1200 мм | 1195 мм | 400 мм | 395 мм | 40 | 120 | Оцинкованная сталь (INPLAST) | саморезы |
| STWS-1200х425-SO | 0.307 м² | 1200 мм | 1195 мм | 425 мм | 420 мм | 43 | 120 | Оцинкованная сталь (INPLAST) | саморезы |
| STWS-1200х450-SO | 0.325 м² | 1200 мм | 1195 мм | 450 мм | 445 мм | 45 | 120 | Оцинкованная сталь (INPLAST) | саморезы |
| STWS-1200х500-SO | 0.361 м² | 1200 мм | 1195 мм | 500 мм | 495 мм | 50 | 120 | Оцинкованная сталь (INPLAST) | саморезы |
| STWS-1200х525-SO | 0.379 м² | 1200 мм | 1195 мм | 525 мм | 520 мм | 53 | 120 | Оцинкованная сталь (INPLAST) | саморезы |
| STWS-1200х550-SO | 0.397 м² | 1200 мм | 1195 мм | 550 мм | 545 мм | 55 | 120 | Оцинкованная сталь (INPLAST) | саморезы |
| STWS-1200х600-SO | 0.433 м² | 1200 мм | 1195 мм | 600 мм | 595 мм | 60 | 120 | Оцинкованная сталь (INPLAST) | саморезы |
| STWS-1200х625-SO | 0.451 м² | 1200 мм | 1195 мм | 625 мм | 620 мм | 63 | 120 | Оцинкованная сталь (INPLAST) | саморезы |
| STWS-1200х650-SO | 0.469 м² | 1200 мм | 1195 мм | 650 мм | 645 мм | 65 | 120 | Оцинкованная сталь (INPLAST) | саморезы |
| STWS-1225х100-SO | 0.074 м² | 1225 мм | 1220 мм | 100 мм | 95 мм | 10 | 123 | Оцинкованная сталь (INPLAST) | саморезы |
| STWS-1225х125-SO | 0.092 м² | 1225 мм | 1220 мм | 125 мм | 120 мм | 13 | 123 | Оцинкованная сталь (INPLAST) | саморезы |
| STWS-1225х150-SO | 0.111 м² | 1225 мм | 1220 мм | 150 мм | 145 мм | 15 | 123 | Оцинкованная сталь (INPLAST) | саморезы |
| STWS-1225х200-SO | 0.147 м² | 1225 мм | 1220 мм | 200 мм | 195 мм | 20 | 123 | Оцинкованная сталь (INPLAST) | саморезы |
| STWS-1225х225-SO | 0.166 м² | 1225 мм | 1220 мм | 225 мм | 220 мм | 23 | 123 | Оцинкованная сталь (INPLAST) | саморезы |
| STWS-1225х250-SO | 0.184 м² | 1225 мм | 1220 мм | 250 мм | 245 мм | 25 | 123 | Оцинкованная сталь (INPLAST) | саморезы |
| STWS-1225х300-SO | 0.221 м² | 1225 мм | 1220 мм | 300 мм | 295 мм | 30 | 123 | Оцинкованная сталь (INPLAST) | саморезы |
| STWS-1225х325-SO | 0.240 м² | 1225 мм | 1220 мм | 325 мм | 320 мм | 33 | 123 | Оцинкованная сталь (INPLAST) | саморезы |
| STWS-1225х350-SO | 0.258 м² | 1225 мм | 1220 мм | 350 мм | 345 мм | 35 | 123 | Оцинкованная сталь (INPLAST) | саморезы |
| STWS-1225х400-SO | 0.295 м² | 1225 мм | 1220 мм | 400 мм | 395 мм | 40 | 123 | Оцинкованная сталь (INPLAST) | саморезы |
| STWS-1225х425-SO | 0.313 м² | 1225 мм | 1220 мм | 425 мм | 420 мм | 43 | 123 | Оцинкованная сталь (INPLAST) | саморезы |
| STWS-1225х450-SO | 0.332 м² | 1225 мм | 1220 мм | 450 мм | 445 мм | 45 | 123 | Оцинкованная сталь (INPLAST) | саморезы |
| STWS-1225х500-SO | 0.368 м² | 1225 мм | 1220 мм | 500 мм | 495 мм | 50 | 123 | Оцинкованная сталь (INPLAST) | саморезы |
| STWS-1225х525-SO | 0.387 м² | 1225 мм | 1220 мм | 525 мм | 520 мм | 53 | 123 | Оцинкованная сталь (INPLAST) | саморезы |
| STWS-1225х550-SO | 0.405 м² | 1225 мм | 1220 мм | 550 мм | 545 мм | 55 | 123 | Оцинкованная сталь (INPLAST) | саморезы |
| STWS-1225х600-SO | 0.442 м² | 1225 мм | 1220 мм | 600 мм | 595 мм | 60 | 123 | Оцинкованная сталь (INPLAST) | саморезы |
| STWS-1225х625-SO | 0.461 м² | 1225 мм | 1220 мм | 625 мм | 620 мм | 63 | 123 | Оцинкованная сталь (INPLAST) | саморезы |
| STWS-1225х650-SO | 0.479 м² | 1225 мм | 1220 мм | 650 мм | 645 мм | 65 | 123 | Оцинкованная сталь (INPLAST) | саморезы |
| STWS-1250х100-SO | 0.075 м² | 1250 мм | 1245 мм | 100 мм | 95 мм | 10 | 125 | Оцинкованная сталь (INPLAST) | саморезы |
| STWS-1250х125-SO | 0.094 м² | 1250 мм | 1245 мм | 125 мм | 120 мм | 13 | 125 | Оцинкованная сталь (INPLAST) | саморезы |
| STWS-1250х150-SO | 0.113 м² | 1250 мм | 1245 мм | 150 мм | 145 мм | 15 | 125 | Оцинкованная сталь (INPLAST) | саморезы |
| STWS-1250х200-SO | 0.150 м² | 1250 мм | 1245 мм | 200 мм | 195 мм | 20 | 125 | Оцинкованная сталь (INPLAST) | саморезы |
| STWS-1250х225-SO | 0.169 м² | 1250 мм | 1245 мм | 225 мм | 220 мм | 23 | 125 | Оцинкованная сталь (INPLAST) | саморезы |
| STWS-1250х250-SO | 0.188 м² | 1250 мм | 1245 мм | 250 мм | 245 мм | 25 | 125 | Оцинкованная сталь (INPLAST) | саморезы |
| STWS-1250х300-SO | 0.226 м² | 1250 мм | 1245 мм | 300 мм | 295 мм | 30 | 125 | Оцинкованная сталь (INPLAST) | саморезы |
| STWS-1250х325-SO | 0.244 м² | 1250 мм | 1245 мм | 325 мм | 320 мм | 33 | 125 | Оцинкованная сталь (INPLAST) | саморезы |
| STWS-1250х350-SO | 0.263 м² | 1250 мм | 1245 мм | 350 мм | 345 мм | 35 | 125 | Оцинкованная сталь (INPLAST) | саморезы |
| STWS-1250х400-SO | 0.301 м² | 1250 мм | 1245 мм | 400 мм | 395 мм | 40 | 125 | Оцинкованная сталь (INPLAST) | саморезы |
| STWS-1250х425-SO | 0.320 м² | 1250 мм | 1245 мм | 425 мм | 420 мм | 43 | 125 | Оцинкованная сталь (INPLAST) | саморезы |
| STWS-1250х450-SO | 0.338 м² | 1250 мм | 1245 мм | 450 мм | 445 мм | 45 | 125 | Оцинкованная сталь (INPLAST) | саморезы |
| STWS-1250х500-SO | 0.376 м² | 1250 мм | 1245 мм | 500 мм | 495 мм | 50 | 125 | Оцинкованная сталь (INPLAST) | саморезы |
| STWS-1250х525-SO | 0.395 м² | 1250 мм | 1245 мм | 525 мм | 520 мм | 53 | 125 | Оцинкованная сталь (INPLAST) | саморезы |
| STWS-1250х550-SO | 0.414 м² | 1250 мм | 1245 мм | 550 мм | 545 мм | 55 | 125 | Оцинкованная сталь (INPLAST) | саморезы |
| STWS-1250х600-SO | 0.451 м² | 1250 мм | 1245 мм | 600 мм | 595 мм | 60 | 125 | Оцинкованная сталь (INPLAST) | саморезы |
| STWS-1250х625-SO | 0.470 м² | 1250 мм | 1245 мм | 625 мм | 620 мм | 63 | 125 | Оцинкованная сталь (INPLAST) | саморезы |
| STWS-1250х650-SO | 0.489 м² | 1250 мм | 1245 мм | 650 мм | 645 мм | 65 | 125 | Оцинкованная сталь (INPLAST) | саморезы |
| STWS-1300х100-SO | 0.078 м² | 1300 мм | 1295 мм | 100 мм | 95 мм | 10 | 130 | Оцинкованная сталь (INPLAST) | саморезы |
| STWS-1300х125-SO | 0.098 м² | 1300 мм | 1295 мм | 125 мм | 120 мм | 13 | 130 | Оцинкованная сталь (INPLAST) | саморезы |
| STWS-1300х150-SO | 0.117 м² | 1300 мм | 1295 мм | 150 мм | 145 мм | 15 | 130 | Оцинкованная сталь (INPLAST) | саморезы |
| STWS-1300х200-SO | 0.156 м² | 1300 мм | 1295 мм | 200 мм | 195 мм | 20 | 130 | Оцинкованная сталь (INPLAST) | саморезы |
| STWS-1300х225-SO | 0.176 м² | 1300 мм | 1295 мм | 225 мм | 220 мм | 23 | 130 | Оцинкованная сталь (INPLAST) | саморезы |
| STWS-1300х250-SO | 0.196 м² | 1300 мм | 1295 мм | 250 мм | 245 мм | 25 | 130 | Оцинкованная сталь (INPLAST) | саморезы |
| STWS-1300х300-SO | 0.235 м² | 1300 мм | 1295 мм | 300 мм | 295 мм | 30 | 130 | Оцинкованная сталь (INPLAST) | саморезы |
| STWS-1300х325-SO | 0.254 м² | 1300 мм | 1295 мм | 325 мм | 320 мм | 33 | 130 | Оцинкованная сталь (INPLAST) | саморезы |
| STWS-1300х350-SO | 0.274 м² | 1300 мм | 1295 мм | 350 мм | 345 мм | 35 | 130 | Оцинкованная сталь (INPLAST) | саморезы |
| STWS-1300х400-SO | 0.313 м² | 1300 мм | 1295 мм | 400 мм | 395 мм | 40 | 130 | Оцинкованная сталь (INPLAST) | саморезы |
| STWS-1300х425-SO | 0.332 м² | 1300 мм | 1295 мм | 425 мм | 420 мм | 43 | 130 | Оцинкованная сталь (INPLAST) | саморезы |
| STWS-1300х450-SO | 0.352 м² | 1300 мм | 1295 мм | 450 мм | 445 мм | 45 | 130 | Оцинкованная сталь (INPLAST) | саморезы |
| STWS-1300х500-SO | 0.391 м² | 1300 мм | 1295 мм | 500 мм | 495 мм | 50 | 130 | Оцинкованная сталь (INPLAST) | саморезы |
| STWS-1300х525-SO | 0.411 м² | 1300 мм | 1295 мм | 525 мм | 520 мм | 53 | 130 | Оцинкованная сталь (INPLAST) | саморезы |
| STWS-1300х550-SO | 0.430 м² | 1300 мм | 1295 мм | 550 мм | 545 мм | 55 | 130 | Оцинкованная сталь (INPLAST) | саморезы |
| STWS-1300х600-SO | 0.469 м² | 1300 мм | 1295 мм | 600 мм | 595 мм | 60 | 130 | Оцинкованная сталь (INPLAST) | саморезы |
| STWS-1300х625-SO | 0.489 м² | 1300 мм | 1295 мм | 625 мм | 620 мм | 63 | 130 | Оцинкованная сталь (INPLAST) | саморезы |
| STWS-1300х650-SO | 0.508 м² | 1300 мм | 1295 мм | 650 мм | 645 мм | 65 | 130 | Оцинкованная сталь (INPLAST) | саморезы |
| STWS-1325х100-SO | 0.080 м² | 1325 мм | 1320 мм | 100 мм | 95 мм | 10 | 133 | Оцинкованная сталь (INPLAST) | саморезы |
| STWS-1325х125-SO | 0.100 м² | 1325 мм | 1320 мм | 125 мм | 120 мм | 13 | 133 | Оцинкованная сталь (INPLAST) | саморезы |
| STWS-1325х150-SO | 0.120 м² | 1325 мм | 1320 мм | 150 мм | 145 мм | 15 | 133 | Оцинкованная сталь (INPLAST) | саморезы |
| STWS-1325х200-SO | 0.159 м² | 1325 мм | 1320 мм | 200 мм | 195 мм | 20 | 133 | Оцинкованная сталь (INPLAST) | саморезы |
| STWS-1325х225-SO | 0.179 м² | 1325 мм | 1320 мм | 225 мм | 220 мм | 23 | 133 | Оцинкованная сталь (INPLAST) | саморезы |
| STWS-1325х250-SO | 0.199 м² | 1325 мм | 1320 мм | 250 мм | 245 мм | 25 | 133 | Оцинкованная сталь (INPLAST) | саморезы |
| STWS-1325х300-SO | 0.239 м² | 1325 мм | 1320 мм | 300 мм | 295 мм | 30 | 133 | Оцинкованная сталь (INPLAST) | саморезы |
| STWS-1325х325-SO | 0.259 м² | 1325 мм | 1320 мм | 325 мм | 320 мм | 33 | 133 | Оцинкованная сталь (INPLAST) | саморезы |
| STWS-1325х350-SO | 0.279 м² | 1325 мм | 1320 мм | 350 мм | 345 мм | 35 | 133 | Оцинкованная сталь (INPLAST) | саморезы |
| STWS-1325х400-SO | 0.319 м² | 1325 мм | 1320 мм | 400 мм | 395 мм | 40 | 133 | Оцинкованная сталь (INPLAST) | саморезы |
| STWS-1325х425-SO | 0.339 м² | 1325 мм | 1320 мм | 425 мм | 420 мм | 43 | 133 | Оцинкованная сталь (INPLAST) | саморезы |
| STWS-1325х450-SO | 0.359 м² | 1325 мм | 1320 мм | 450 мм | 445 мм | 45 | 133 | Оцинкованная сталь (INPLAST) | саморезы |
| STWS-1325х500-SO | 0.399 м² | 1325 мм | 1320 мм | 500 мм | 495 мм | 50 | 133 | Оцинкованная сталь (INPLAST) | саморезы |
| STWS-1325х525-SO | 0.418 м² | 1325 мм | 1320 мм | 525 мм | 520 мм | 53 | 133 | Оцинкованная сталь (INPLAST) | саморезы |
| STWS-1325х550-SO | 0.438 м² | 1325 мм | 1320 мм | 550 мм | 545 мм | 55 | 133 | Оцинкованная сталь (INPLAST) | саморезы |
| STWS-1325х600-SO | 0.478 м² | 1325 мм | 1320 мм | 600 мм | 595 мм | 60 | 133 | Оцинкованная сталь (INPLAST) | саморезы |
| STWS-1325х625-SO | 0.498 м² | 1325 мм | 1320 мм | 625 мм | 620 мм | 63 | 133 | Оцинкованная сталь (INPLAST) | саморезы |
| STWS-1325х650-SO | 0.518 м² | 1325 мм | 1320 мм | 650 мм | 645 мм | 65 | 133 | Оцинкованная сталь (INPLAST) | саморезы |
| STWS-1350х100-SO | 0.081 м² | 1350 мм | 1345 мм | 100 мм | 95 мм | 10 | 135 | Оцинкованная сталь (INPLAST) | саморезы |
| STWS-1350х125-SO | 0.102 м² | 1350 мм | 1345 мм | 125 мм | 120 мм | 13 | 135 | Оцинкованная сталь (INPLAST) | саморезы |
| STWS-1350х150-SO | 0.122 м² | 1350 мм | 1345 мм | 150 мм | 145 мм | 15 | 135 | Оцинкованная сталь (INPLAST) | саморезы |
| STWS-1350х200-SO | 0.162 м² | 1350 мм | 1345 мм | 200 мм | 195 мм | 20 | 135 | Оцинкованная сталь (INPLAST) | саморезы |
| STWS-1350х225-SO | 0.183 м² | 1350 мм | 1345 мм | 225 мм | 220 мм | 23 | 135 | Оцинкованная сталь (INPLAST) | саморезы |
| STWS-1350х250-SO | 0.203 м² | 1350 мм | 1345 мм | 250 мм | 245 мм | 25 | 135 | Оцинкованная сталь (INPLAST) | саморезы |
| STWS-1350х300-SO | 0.244 м² | 1350 мм | 1345 мм | 300 мм | 295 мм | 30 | 135 | Оцинкованная сталь (INPLAST) | саморезы |
| STWS-1350х325-SO | 0.264 м² | 1350 мм | 1345 мм | 325 мм | 320 мм | 33 | 135 | Оцинкованная сталь (INPLAST) | саморезы |
| STWS-1350х350-SO | 0.284 м² | 1350 мм | 1345 мм | 350 мм | 345 мм | 35 | 135 | Оцинкованная сталь (INPLAST) | саморезы |
| STWS-1350х400-SO | 0.325 м² | 1350 мм | 1345 мм | 400 мм | 395 мм | 40 | 135 | Оцинкованная сталь (INPLAST) | саморезы |
| STWS-1350х425-SO | 0.345 м² | 1350 мм | 1345 мм | 425 мм | 420 мм | 43 | 135 | Оцинкованная сталь (INPLAST) | саморезы |
| STWS-1350х450-SO | 0.365 м² | 1350 мм | 1345 мм | 450 мм | 445 мм | 45 | 135 | Оцинкованная сталь (INPLAST) | саморезы |
| STWS-1350х500-SO | 0.406 м² | 1350 мм | 1345 мм | 500 мм | 495 мм | 50 | 135 | Оцинкованная сталь (INPLAST) | саморезы |
| STWS-1350х525-SO | 0.426 м² | 1350 мм | 1345 мм | 525 мм | 520 мм | 53 | 135 | Оцинкованная сталь (INPLAST) | саморезы |
| STWS-1350х550-SO | 0.447 м² | 1350 мм | 1345 мм | 550 мм | 545 мм | 55 | 135 | Оцинкованная сталь (INPLAST) | саморезы |
| STWS-1350х600-SO | 0.487 м² | 1350 мм | 1345 мм | 600 мм | 595 мм | 60 | 135 | Оцинкованная сталь (INPLAST) | саморезы |
| STWS-1350х625-SO | 0.508 м² | 1350 мм | 1345 мм | 625 мм | 620 мм | 63 | 135 | Оцинкованная сталь (INPLAST) | саморезы |
| STWS-1350х650-SO | 0.528 м² | 1350 мм | 1345 мм | 650 мм | 645 мм | 65 | 135 | Оцинкованная сталь (INPLAST) | саморезы |
| STWS-1400х100-SO | 0.084 м² | 1400 мм | 1395 мм | 100 мм | 95 мм | 10 | 140 | Оцинкованная сталь (INPLAST) | саморезы |
| STWS-1400х125-SO | 0.105 м² | 1400 мм | 1395 мм | 125 мм | 120 мм | 13 | 140 | Оцинкованная сталь (INPLAST) | саморезы |
| STWS-1400х150-SO | 0.126 м² | 1400 мм | 1395 мм | 150 мм | 145 мм | 15 | 140 | Оцинкованная сталь (INPLAST) | саморезы |
| STWS-1400х200-SO | 0.168 м² | 1400 мм | 1395 мм | 200 мм | 195 мм | 20 | 140 | Оцинкованная сталь (INPLAST) | саморезы |
| STWS-1400х225-SO | 0.190 м² | 1400 мм | 1395 мм | 225 мм | 220 мм | 23 | 140 | Оцинкованная сталь (INPLAST) | саморезы |
| STWS-1400х250-SO | 0.211 м² | 1400 мм | 1395 мм | 250 мм | 245 мм | 25 | 140 | Оцинкованная сталь (INPLAST) | саморезы |
| STWS-1400х300-SO | 0.253 м² | 1400 мм | 1395 мм | 300 мм | 295 мм | 30 | 140 | Оцинкованная сталь (INPLAST) | саморезы |
| STWS-1400х325-SO | 0.274 м² | 1400 мм | 1395 мм | 325 мм | 320 мм | 33 | 140 | Оцинкованная сталь (INPLAST) | саморезы |
| STWS-1400х350-SO | 0.295 м² | 1400 мм | 1395 мм | 350 мм | 345 мм | 35 | 140 | Оцинкованная сталь (INPLAST) | саморезы |
| STWS-1400х400-SO | 0.337 м² | 1400 мм | 1395 мм | 400 мм | 395 мм | 40 | 140 | Оцинкованная сталь (INPLAST) | саморезы |
| STWS-1400х425-SO | 0.358 м² | 1400 мм | 1395 мм | 425 мм | 420 мм | 43 | 140 | Оцинкованная сталь (INPLAST) | саморезы |
| STWS-1400х450-SO | 0.379 м² | 1400 мм | 1395 мм | 450 мм | 445 мм | 45 | 140 | Оцинкованная сталь (INPLAST) | саморезы |
| STWS-1400х500-SO | 0.421 м² | 1400 мм | 1395 мм | 500 мм | 495 мм | 50 | 140 | Оцинкованная сталь (INPLAST) | саморезы |
| STWS-1400х525-SO | 0.442 м² | 1400 мм | 1395 мм | 525 мм | 520 мм | 53 | 140 | Оцинкованная сталь (INPLAST) | саморезы |
| STWS-1400х550-SO | 0.463 м² | 1400 мм | 1395 мм | 550 мм | 545 мм | 55 | 140 | Оцинкованная сталь (INPLAST) | саморезы |
| STWS-1400х600-SO | 0.505 м² | 1400 мм | 1395 мм | 600 мм | 595 мм | 60 | 140 | Оцинкованная сталь (INPLAST) | саморезы |
| STWS-1400х625-SO | 0.526 м² | 1400 мм | 1395 мм | 625 мм | 620 мм | 63 | 140 | Оцинкованная сталь (INPLAST) | саморезы |
| STWS-1400х650-SO | 0.547 м² | 1400 мм | 1395 мм | 650 мм | 645 мм | 65 | 140 | Оцинкованная сталь (INPLAST) | саморезы |
| STWS-1425х100-SO | 0.086 м² | 1425 мм | 1420 мм | 100 мм | 95 мм | 10 | 143 | Оцинкованная сталь (INPLAST) | саморезы |
| STWS-1425х125-SO | 0.107 м² | 1425 мм | 1420 мм | 125 мм | 120 мм | 13 | 143 | Оцинкованная сталь (INPLAST) | саморезы |
| STWS-1425х150-SO | 0.129 м² | 1425 мм | 1420 мм | 150 мм | 145 мм | 15 | 143 | Оцинкованная сталь (INPLAST) | саморезы |
| STWS-1425х200-SO | 0.171 м² | 1425 мм | 1420 мм | 200 мм | 195 мм | 20 | 143 | Оцинкованная сталь (INPLAST) | саморезы |
| STWS-1425х225-SO | 0.193 м² | 1425 мм | 1420 мм | 225 мм | 220 мм | 23 | 143 | Оцинкованная сталь (INPLAST) | саморезы |
| STWS-1425х250-SO | 0.214 м² | 1425 мм | 1420 мм | 250 мм | 245 мм | 25 | 143 | Оцинкованная сталь (INPLAST) | саморезы |
| STWS-1425х300-SO | 0.257 м² | 1425 мм | 1420 мм | 300 мм | 295 мм | 30 | 143 | Оцинкованная сталь (INPLAST) | саморезы |
| STWS-1425х325-SO | 0.279 м² | 1425 мм | 1420 мм | 325 мм | 320 мм | 33 | 143 | Оцинкованная сталь (INPLAST) | саморезы |
| STWS-1425х350-SO | 0.300 м² | 1425 мм | 1420 мм | 350 мм | 345 мм | 35 | 143 | Оцинкованная сталь (INPLAST) | саморезы |
| STWS-1425х400-SO | 0.343 м² | 1425 мм | 1420 мм | 400 мм | 395 мм | 40 | 143 | Оцинкованная сталь (INPLAST) | саморезы |
| STWS-1425х425-SO | 0.364 м² | 1425 мм | 1420 мм | 425 мм | 420 мм | 43 | 143 | Оцинкованная сталь (INPLAST) | саморезы |
| STWS-1425х450-SO | 0.386 м² | 1425 мм | 1420 мм | 450 мм | 445 мм | 45 | 143 | Оцинкованная сталь (INPLAST) | саморезы |
| STWS-1425х500-SO | 0.429 м² | 1425 мм | 1420 мм | 500 мм | 495 мм | 50 | 143 | Оцинкованная сталь (INPLAST) | саморезы |
| STWS-1425х525-SO | 0.450 м² | 1425 мм | 1420 мм | 525 мм | 520 мм | 53 | 143 | Оцинкованная сталь (INPLAST) | саморезы |
| STWS-1425х550-SO | 0.472 м² | 1425 мм | 1420 мм | 550 мм | 545 мм | 55 | 143 | Оцинкованная сталь (INPLAST) | саморезы |
| STWS-1425х600-SO | 0.514 м² | 1425 мм | 1420 мм | 600 мм | 595 мм | 60 | 143 | Оцинкованная сталь (INPLAST) | саморезы |
| STWS-1425х625-SO | 0.536 м² | 1425 мм | 1420 мм | 625 мм | 620 мм | 63 | 143 | Оцинкованная сталь (INPLAST) | саморезы |
| STWS-1425х650-SO | 0.557 м² | 1425 мм | 1420 мм | 650 мм | 645 мм | 65 | 143 | Оцинкованная сталь (INPLAST) | саморезы |
| STWS-1450х100-SO | 0.087 м² | 1450 мм | 1445 мм | 100 мм | 95 мм | 10 | 145 | Оцинкованная сталь (INPLAST) | саморезы |
| STWS-1450х125-SO | 0.109 м² | 1450 мм | 1445 мм | 125 мм | 120 мм | 13 | 145 | Оцинкованная сталь (INPLAST) | саморезы |
| STWS-1450х150-SO | 0.131 м² | 1450 мм | 1445 мм | 150 мм | 145 мм | 15 | 145 | Оцинкованная сталь (INPLAST) | саморезы |
| STWS-1450х200-SO | 0.174 м² | 1450 мм | 1445 мм | 200 мм | 195 мм | 20 | 145 | Оцинкованная сталь (INPLAST) | саморезы |
| STWS-1450х225-SO | 0.196 м² | 1450 мм | 1445 мм | 225 мм | 220 мм | 23 | 145 | Оцинкованная сталь (INPLAST) | саморезы |
| STWS-1450х250-SO | 0.218 м² | 1450 мм | 1445 мм | 250 мм | 245 мм | 25 | 145 | Оцинкованная сталь (INPLAST) | саморезы |
| STWS-1450х300-SO | 0.262 м² | 1450 мм | 1445 мм | 300 мм | 295 мм | 30 | 145 | Оцинкованная сталь (INPLAST) | саморезы |
| STWS-1450х325-SO | 0.284 м² | 1450 мм | 1445 мм | 325 мм | 320 мм | 33 | 145 | Оцинкованная сталь (INPLAST) | саморезы |
| STWS-1450х350-SO | 0.305 м² | 1450 мм | 1445 мм | 350 мм | 345 мм | 35 | 145 | Оцинкованная сталь (INPLAST) | саморезы |
| STWS-1450х400-SO | 0.349 м² | 1450 мм | 1445 мм | 400 мм | 395 мм | 40 | 145 | Оцинкованная сталь (INPLAST) | саморезы |
| STWS-1450х425-SO | 0.371 м² | 1450 мм | 1445 мм | 425 мм | 420 мм | 43 | 145 | Оцинкованная сталь (INPLAST) | саморезы |
| STWS-1450х450-SO | 0.393 м² | 1450 мм | 1445 мм | 450 мм | 445 мм | 45 | 145 | Оцинкованная сталь (INPLAST) | саморезы |
| STWS-1450х500-SO | 0.436 м² | 1450 мм | 1445 мм | 500 мм | 495 мм | 50 | 145 | Оцинкованная сталь (INPLAST) | саморезы |
| STWS-1450х525-SO | 0.458 м² | 1450 мм | 1445 мм | 525 мм | 520 мм | 53 | 145 | Оцинкованная сталь (INPLAST) | саморезы |
| STWS-1450х550-SO | 0.480 м² | 1450 мм | 1445 мм | 550 мм | 545 мм | 55 | 145 | Оцинкованная сталь (INPLAST) | саморезы |
| STWS-1450х600-SO | 0.523 м² | 1450 мм | 1445 мм | 600 мм | 595 мм | 60 | 145 | Оцинкованная сталь (INPLAST) | саморезы |
| STWS-1450х625-SO | 0.545 м² | 1450 мм | 1445 мм | 625 мм | 620 мм | 63 | 145 | Оцинкованная сталь (INPLAST) | саморезы |
| STWS-1450х650-SO | 0.567 м² | 1450 мм | 1445 мм | 650 мм | 645 мм | 65 | 145 | Оцинкованная сталь (INPLAST) | саморезы |
| STWS-1500х100-SO | 0.090 м² | 1500 мм | 1495 мм | 100 мм | 95 мм | 10 | 150 | Оцинкованная сталь (INPLAST) | саморезы |
| STWS-1500х125-SO | 0.113 м² | 1500 мм | 1495 мм | 125 мм | 120 мм | 13 | 150 | Оцинкованная сталь (INPLAST) | саморезы |
| STWS-1500х150-SO | 0.135 м² | 1500 мм | 1495 мм | 150 мм | 145 мм | 15 | 150 | Оцинкованная сталь (INPLAST) | саморезы |
| STWS-1500х200-SO | 0.180 м² | 1500 мм | 1495 мм | 200 мм | 195 мм | 20 | 150 | Оцинкованная сталь (INPLAST) | саморезы |
| STWS-1500х225-SO | 0.203 м² | 1500 мм | 1495 мм | 225 мм | 220 мм | 23 | 150 | Оцинкованная сталь (INPLAST) | саморезы |
| STWS-1500х250-SO | 0.226 м² | 1500 мм | 1495 мм | 250 мм | 245 мм | 25 | 150 | Оцинкованная сталь (INPLAST) | саморезы |
| STWS-1500х300-SO | 0.271 м² | 1500 мм | 1495 мм | 300 мм | 295 мм | 30 | 150 | Оцинкованная сталь (INPLAST) | саморезы |
| STWS-1500х325-SO | 0.293 м² | 1500 мм | 1495 мм | 325 мм | 320 мм | 33 | 150 | Оцинкованная сталь (INPLAST) | саморезы |
| STWS-1500х350-SO | 0.316 м² | 1500 мм | 1495 мм | 350 мм | 345 мм | 35 | 150 | Оцинкованная сталь (INPLAST) | саморезы |
| STWS-1500х400-SO | 0.361 м² | 1500 мм | 1495 мм | 400 мм | 395 мм | 40 | 150 | Оцинкованная сталь (INPLAST) | саморезы |
| STWS-1500х425-SO | 0.384 м² | 1500 мм | 1495 мм | 425 мм | 420 мм | 43 | 150 | Оцинкованная сталь (INPLAST) | саморезы |
| STWS-1500х450-SO | 0.406 м² | 1500 мм | 1495 мм | 450 мм | 445 мм | 45 | 150 | Оцинкованная сталь (INPLAST) | саморезы |
| STWS-1500х500-SO | 0.451 м² | 1500 мм | 1495 мм | 500 мм | 495 мм | 50 | 150 | Оцинкованная сталь (INPLAST) | саморезы |
| STWS-1500х525-SO | 0.474 м² | 1500 мм | 1495 мм | 525 мм | 520 мм | 53 | 150 | Оцинкованная сталь (INPLAST) | саморезы |
| STWS-1500х550-SO | 0.496 м² | 1500 мм | 1495 мм | 550 мм | 545 мм | 55 | 150 | Оцинкованная сталь (INPLAST) | саморезы |
| STWS-1500х600-SO | 0.541 м² | 1500 мм | 1495 мм | 600 мм | 595 мм | 60 | 150 | Оцинкованная сталь (INPLAST) | саморезы |
| STWS-1500х625-SO | 0.564 м² | 1500 мм | 1495 мм | 625 мм | 620 мм | 63 | 150 | Оцинкованная сталь (INPLAST) | саморезы |
| STWS-1500х650-SO | 0.587 м² | 1500 мм | 1495 мм | 650 мм | 645 мм | 65 | 150 | Оцинкованная сталь (INPLAST) | саморезы |
| STWS-100х100-Z-SO | 0.006 м² | 100 мм | 95 мм | 100 мм | 95 мм | 10 | 10 | Оцинкованная сталь (INPLAST) | скрытые защелки |
| STWS-125х100-Z-SO | 0.008 м² | 125 мм | 120 мм | 100 мм | 95 мм | 10 | 13 | Оцинкованная сталь (INPLAST) | скрытые защелки |
| STWS-125х125-Z-SO | 0.009 м² | 125 мм | 120 мм | 125 мм | 120 мм | 13 | 13 | Оцинкованная сталь (INPLAST) | скрытые защелки |
| STWS-150х100-Z-SO | 0.009 м² | 150 мм | 145 мм | 100 мм | 95 мм | 10 | 15 | Оцинкованная сталь (INPLAST) | скрытые защелки |
| STWS-150х125-Z-SO | 0.011 м² | 150 мм | 145 мм | 125 мм | 120 мм | 13 | 15 | Оцинкованная сталь (INPLAST) | скрытые защелки |
| STWS-150х150-Z-SO | 0.014 м² | 150 мм | 145 мм | 150 мм | 145 мм | 15 | 15 | Оцинкованная сталь (INPLAST) | скрытые защелки |
| STWS-200х100-Z-SO | 0.012 м² | 200 мм | 195 мм | 100 мм | 95 мм | 10 | 20 | Оцинкованная сталь (INPLAST) | скрытые защелки |
| STWS-200х125-Z-SO | 0.015 м² | 200 мм | 195 мм | 125 мм | 120 мм | 13 | 20 | Оцинкованная сталь (INPLAST) | скрытые защелки |
| STWS-200х150-Z-SO | 0.018 м² | 200 мм | 195 мм | 150 мм | 145 мм | 15 | 20 | Оцинкованная сталь (INPLAST) | скрытые защелки |
| STWS-200х200-Z-SO | 0.024 м² | 200 мм | 195 мм | 200 мм | 195 мм | 20 | 20 | Оцинкованная сталь (INPLAST) | скрытые защелки |
| STWS-225х100-Z-SO | 0.014 м² | 225 мм | 220 мм | 100 мм | 95 мм | 10 | 23 | Оцинкованная сталь (INPLAST) | скрытые защелки |
| STWS-225х125-Z-SO | 0.017 м² | 225 мм | 220 мм | 125 мм | 120 мм | 13 | 23 | Оцинкованная сталь (INPLAST) | скрытые защелки |
| STWS-225х150-Z-SO | 0.020 м² | 225 мм | 220 мм | 150 мм | 145 мм | 15 | 23 | Оцинкованная сталь (INPLAST) | скрытые защелки |
| STWS-225х200-Z-SO | 0.027 м² | 225 мм | 220 мм | 200 мм | 195 мм | 20 | 23 | Оцинкованная сталь (INPLAST) | скрытые защелки |
| STWS-225х225-Z-SO | 0.030 м² | 225 мм | 220 мм | 225 мм | 220 мм | 23 | 23 | Оцинкованная сталь (INPLAST) | скрытые защелки |
| STWS-250х100-Z-SO | 0.015 м² | 250 мм | 245 мм | 100 мм | 95 мм | 10 | 25 | Оцинкованная сталь (INPLAST) | скрытые защелки |
| STWS-250х125-Z-SO | 0.019 м² | 250 мм | 245 мм | 125 мм | 120 мм | 13 | 25 | Оцинкованная сталь (INPLAST) | скрытые защелки |
| STWS-250х150-Z-SO | 0.023 м² | 250 мм | 245 мм | 150 мм | 145 мм | 15 | 25 | Оцинкованная сталь (INPLAST) | скрытые защелки |
| STWS-250х200-Z-SO | 0.030 м² | 250 мм | 245 мм | 200 мм | 195 мм | 20 | 25 | Оцинкованная сталь (INPLAST) | скрытые защелки |
| STWS-250х225-Z-SO | 0.034 м² | 250 мм | 245 мм | 225 мм | 220 мм | 23 | 25 | Оцинкованная сталь (INPLAST) | скрытые защелки |
| STWS-250х250-Z-SO | 0.038 м² | 250 мм | 245 мм | 250 мм | 245 мм | 25 | 25 | Оцинкованная сталь (INPLAST) | скрытые защелки |
| STWS-300х100-Z-SO | 0.018 м² | 300 мм | 295 мм | 100 мм | 95 мм | 10 | 30 | Оцинкованная сталь (INPLAST) | скрытые защелки |
| STWS-300х125-Z-SO | 0.023 м² | 300 мм | 295 мм | 125 мм | 120 мм | 13 | 30 | Оцинкованная сталь (INPLAST) | скрытые защелки |
| STWS-300х150-Z-SO | 0.027 м² | 300 мм | 295 мм | 150 мм | 145 мм | 15 | 30 | Оцинкованная сталь (INPLAST) | скрытые защелки |
| STWS-300х200-Z-SO | 0.036 м² | 300 мм | 295 мм | 200 мм | 195 мм | 20 | 30 | Оцинкованная сталь (INPLAST) | скрытые защелки |
| STWS-300х225-Z-SO | 0.041 м² | 300 мм | 295 мм | 225 мм | 220 мм | 23 | 30 | Оцинкованная сталь (INPLAST) | скрытые защелки |
| STWS-300х250-Z-SO | 0.045 м² | 300 мм | 295 мм | 250 мм | 245 мм | 25 | 30 | Оцинкованная сталь (INPLAST) | скрытые защелки |
| STWS-300х300-Z-SO | 0.054 м² | 300 мм | 295 мм | 300 мм | 295 мм | 30 | 30 | Оцинкованная сталь (INPLAST) | скрытые защелки |
| STWS-325х100-Z-SO | 0.020 м² | 325 мм | 320 мм | 100 мм | 95 мм | 10 | 33 | Оцинкованная сталь (INPLAST) | скрытые защелки |
| STWS-325х125-Z-SO | 0.024 м² | 325 мм | 320 мм | 125 мм | 120 мм | 13 | 33 | Оцинкованная сталь (INPLAST) | скрытые защелки |
| STWS-325х150-Z-SO | 0.029 м² | 325 мм | 320 мм | 150 мм | 145 мм | 15 | 33 | Оцинкованная сталь (INPLAST) | скрытые защелки |
| STWS-325х200-Z-SO | 0.039 м² | 325 мм | 320 мм | 200 мм | 195 мм | 20 | 33 | Оцинкованная сталь (INPLAST) | скрытые защелки |
| STWS-325х225-Z-SO | 0.044 м² | 325 мм | 320 мм | 225 мм | 220 мм | 23 | 33 | Оцинкованная сталь (INPLAST) | скрытые защелки |
| STWS-325х250-Z-SO | 0.049 м² | 325 мм | 320 мм | 250 мм | 245 мм | 25 | 33 | Оцинкованная сталь (INPLAST) | скрытые защелки |
| STWS-325х300-Z-SO | 0.059 м² | 325 мм | 320 мм | 300 мм | 295 мм | 30 | 33 | Оцинкованная сталь (INPLAST) | скрытые защелки |
| STWS-325х325-Z-SO | 0.064 м² | 325 мм | 320 мм | 325 мм | 320 мм | 33 | 33 | Оцинкованная сталь (INPLAST) | скрытые защелки |
| STWS-350х100-Z-SO | 0.021 м² | 350 мм | 345 мм | 100 мм | 95 мм | 10 | 35 | Оцинкованная сталь (INPLAST) | скрытые защелки |
| STWS-350х125-Z-SO | 0.026 м² | 350 мм | 345 мм | 125 мм | 120 мм | 13 | 35 | Оцинкованная сталь (INPLAST) | скрытые защелки |
| STWS-350х150-Z-SO | 0.032 м² | 350 мм | 345 мм | 150 мм | 145 мм | 15 | 35 | Оцинкованная сталь (INPLAST) | скрытые защелки |
| STWS-350х200-Z-SO | 0.042 м² | 350 мм | 345 мм | 200 мм | 195 мм | 20 | 35 | Оцинкованная сталь (INPLAST) | скрытые защелки |
| STWS-350х225-Z-SO | 0.047 м² | 350 мм | 345 мм | 225 мм | 220 мм | 23 | 35 | Оцинкованная сталь (INPLAST) | скрытые защелки |
| STWS-350х250-Z-SO | 0.053 м² | 350 мм | 345 мм | 250 мм | 245 мм | 25 | 35 | Оцинкованная сталь (INPLAST) | скрытые защелки |
| STWS-350х300-Z-SO | 0.063 м² | 350 мм | 345 мм | 300 мм | 295 мм | 30 | 35 | Оцинкованная сталь (INPLAST) | скрытые защелки |
| STWS-350х325-Z-SO | 0.068 м² | 350 мм | 345 мм | 325 мм | 320 мм | 33 | 35 | Оцинкованная сталь (INPLAST) | скрытые защелки |
| STWS-350х350-Z-SO | 0.074 м² | 350 мм | 345 мм | 350 мм | 345 мм | 35 | 35 | Оцинкованная сталь (INPLAST) | скрытые защелки |
| STWS-400х100-Z-SO | 0.024 м² | 400 мм | 395 мм | 100 мм | 95 мм | 10 | 40 | Оцинкованная сталь (INPLAST) | скрытые защелки |
| STWS-400х125-Z-SO | 0.030 м² | 400 мм | 395 мм | 125 мм | 120 мм | 13 | 40 | Оцинкованная сталь (INPLAST) | скрытые защелки |
| STWS-400х150-Z-SO | 0.036 м² | 400 мм | 395 мм | 150 мм | 145 мм | 15 | 40 | Оцинкованная сталь (INPLAST) | скрытые защелки |
| STWS-400х200-Z-SO | 0.048 м² | 400 мм | 395 мм | 200 мм | 195 мм | 20 | 40 | Оцинкованная сталь (INPLAST) | скрытые защелки |
| STWS-400х225-Z-SO | 0.054 м² | 400 мм | 395 мм | 225 мм | 220 мм | 23 | 40 | Оцинкованная сталь (INPLAST) | скрытые защелки |
| STWS-400х250-Z-SO | 0.060 м² | 400 мм | 395 мм | 250 мм | 245 мм | 25 | 40 | Оцинкованная сталь (INPLAST) | скрытые защелки |
| STWS-400х300-Z-SO | 0.072 м² | 400 мм | 395 мм | 300 мм | 295 мм | 30 | 40 | Оцинкованная сталь (INPLAST) | скрытые защелки |
| STWS-400х325-Z-SO | 0.078 м² | 400 мм | 395 мм | 325 мм | 320 мм | 33 | 40 | Оцинкованная сталь (INPLAST) | скрытые защелки |
| STWS-400х350-Z-SO | 0.084 м² | 400 мм | 395 мм | 350 мм | 345 мм | 35 | 40 | Оцинкованная сталь (INPLAST) | скрытые защелки |
| STWS-400х400-Z-SO | 0.096 м² | 400 мм | 395 мм | 400 мм | 395 мм | 40 | 40 | Оцинкованная сталь (INPLAST) | скрытые защелки |
| STWS-425х100-Z-SO | 0.026 м² | 425 мм | 420 мм | 100 мм | 95 мм | 10 | 43 | Оцинкованная сталь (INPLAST) | скрытые защелки |
| STWS-425х125-Z-SO | 0.032 м² | 425 мм | 420 мм | 125 мм | 120 мм | 13 | 43 | Оцинкованная сталь (INPLAST) | скрытые защелки |
| STWS-425х150-Z-SO | 0.038 м² | 425 мм | 420 мм | 150 мм | 145 мм | 15 | 43 | Оцинкованная сталь (INPLAST) | скрытые защелки |
| STWS-425х200-Z-SO | 0.051 м² | 425 мм | 420 мм | 200 мм | 195 мм | 20 | 43 | Оцинкованная сталь (INPLAST) | скрытые защелки |
| STWS-425х225-Z-SO | 0.058 м² | 425 мм | 420 мм | 225 мм | 220 мм | 23 | 43 | Оцинкованная сталь (INPLAST) | скрытые защелки |
| STWS-425х250-Z-SO | 0.064 м² | 425 мм | 420 мм | 250 мм | 245 мм | 25 | 43 | Оцинкованная сталь (INPLAST) | скрытые защелки |
| STWS-425х300-Z-SO | 0.077 м² | 425 мм | 420 мм | 300 мм | 295 мм | 30 | 43 | Оцинкованная сталь (INPLAST) | скрытые защелки |
| STWS-425х325-Z-SO | 0.083 м² | 425 мм | 420 мм | 325 мм | 320 мм | 33 | 43 | Оцинкованная сталь (INPLAST) | скрытые защелки |
| STWS-425х350-Z-SO | 0.089 м² | 425 мм | 420 мм | 350 мм | 345 мм | 35 | 43 | Оцинкованная сталь (INPLAST) | скрытые защелки |
| STWS-425х400-Z-SO | 0.102 м² | 425 мм | 420 мм | 400 мм | 395 мм | 40 | 43 | Оцинкованная сталь (INPLAST) | скрытые защелки |
| STWS-425х425-Z-SO | 0.109 м² | 425 мм | 420 мм | 425 мм | 420 мм | 43 | 43 | Оцинкованная сталь (INPLAST) | скрытые защелки |
| STWS-450х100-Z-SO | 0.027 м² | 450 мм | 445 мм | 100 мм | 95 мм | 10 | 45 | Оцинкованная сталь (INPLAST) | скрытые защелки |
| STWS-450х125-Z-SO | 0.034 м² | 450 мм | 445 мм | 125 мм | 120 мм | 13 | 45 | Оцинкованная сталь (INPLAST) | скрытые защелки |
| STWS-450х150-Z-SO | 0.041 м² | 450 мм | 445 мм | 150 мм | 145 мм | 15 | 45 | Оцинкованная сталь (INPLAST) | скрытые защелки |
| STWS-450х200-Z-SO | 0.054 м² | 450 мм | 445 мм | 200 мм | 195 мм | 20 | 45 | Оцинкованная сталь (INPLAST) | скрытые защелки |
| STWS-450х225-Z-SO | 0.061 м² | 450 мм | 445 мм | 225 мм | 220 мм | 23 | 45 | Оцинкованная сталь (INPLAST) | скрытые защелки |
| STWS-450х250-Z-SO | 0.068 м² | 450 мм | 445 мм | 250 мм | 245 мм | 25 | 45 | Оцинкованная сталь (INPLAST) | скрытые защелки |
| STWS-450х300-Z-SO | 0.081 м² | 450 мм | 445 мм | 300 мм | 295 мм | 30 | 45 | Оцинкованная сталь (INPLAST) | скрытые защелки |
| STWS-450х325-Z-SO | 0.088 м² | 450 мм | 445 мм | 325 мм | 320 мм | 33 | 45 | Оцинкованная сталь (INPLAST) | скрытые защелки |
| STWS-450х350-Z-SO | 0.095 м² | 450 мм | 445 мм | 350 мм | 345 мм | 35 | 45 | Оцинкованная сталь (INPLAST) | скрытые защелки |
| STWS-450х400-Z-SO | 0.108 м² | 450 мм | 445 мм | 400 мм | 395 мм | 40 | 45 | Оцинкованная сталь (INPLAST) | скрытые защелки |
| STWS-450х425-Z-SO | 0.115 м² | 450 мм | 445 мм | 425 мм | 420 мм | 43 | 45 | Оцинкованная сталь (INPLAST) | скрытые защелки |
| STWS-450х450-Z-SO | 0.122 м² | 450 мм | 445 мм | 450 мм | 445 мм | 45 | 45 | Оцинкованная сталь (INPLAST) | скрытые защелки |
| STWS-500х100-Z-SO | 0.030 м² | 500 мм | 495 мм | 100 мм | 95 мм | 10 | 50 | Оцинкованная сталь (INPLAST) | скрытые защелки |
| STWS-500х125-Z-SO | 0.038 м² | 500 мм | 495 мм | 125 мм | 120 мм | 13 | 50 | Оцинкованная сталь (INPLAST) | скрытые защелки |
| STWS-500х150-Z-SO | 0.045 м² | 500 мм | 495 мм | 150 мм | 145 мм | 15 | 50 | Оцинкованная сталь (INPLAST) | скрытые защелки |
| STWS-500х200-Z-SO | 0.060 м² | 500 мм | 495 мм | 200 мм | 195 мм | 20 | 50 | Оцинкованная сталь (INPLAST) | скрытые защелки |
| STWS-500х225-Z-SO | 0.068 м² | 500 мм | 495 мм | 225 мм | 220 мм | 23 | 50 | Оцинкованная сталь (INPLAST) | скрытые защелки |
| STWS-500х250-Z-SO | 0.075 м² | 500 мм | 495 мм | 250 мм | 245 мм | 25 | 50 | Оцинкованная сталь (INPLAST) | скрытые защелки |
| STWS-500х300-Z-SO | 0.090 м² | 500 мм | 495 мм | 300 мм | 295 мм | 30 | 50 | Оцинкованная сталь (INPLAST) | скрытые защелки |
| STWS-500х325-Z-SO | 0.098 м² | 500 мм | 495 мм | 325 мм | 320 мм | 33 | 50 | Оцинкованная сталь (INPLAST) | скрытые защелки |
| STWS-500х350-Z-SO | 0.105 м² | 500 мм | 495 мм | 350 мм | 345 мм | 35 | 50 | Оцинкованная сталь (INPLAST) | скрытые защелки |
| STWS-500х400-Z-SO | 0.120 м² | 500 мм | 495 мм | 400 мм | 395 мм | 40 | 50 | Оцинкованная сталь (INPLAST) | скрытые защелки |
| STWS-500х425-Z-SO | 0.128 м² | 500 мм | 495 мм | 425 мм | 420 мм | 43 | 50 | Оцинкованная сталь (INPLAST) | скрытые защелки |
| STWS-500х450-Z-SO | 0.135 м² | 500 мм | 495 мм | 450 мм | 445 мм | 45 | 50 | Оцинкованная сталь (INPLAST) | скрытые защелки |
| STWS-500х500-Z-SO | 0.150 м² | 500 мм | 495 мм | 500 мм | 495 мм | 50 | 50 | Оцинкованная сталь (INPLAST) | скрытые защелки |
| STWS-525х100-Z-SO | 0.032 м² | 525 мм | 520 мм | 100 мм | 95 мм | 10 | 53 | Оцинкованная сталь (INPLAST) | скрытые защелки |
| STWS-525х125-Z-SO | 0.039 м² | 525 мм | 520 мм | 125 мм | 120 мм | 13 | 53 | Оцинкованная сталь (INPLAST) | скрытые защелки |
| STWS-525х150-Z-SO | 0.047 м² | 525 мм | 520 мм | 150 мм | 145 мм | 15 | 53 | Оцинкованная сталь (INPLAST) | скрытые защелки |
| STWS-525х200-Z-SO | 0.063 м² | 525 мм | 520 мм | 200 мм | 195 мм | 20 | 53 | Оцинкованная сталь (INPLAST) | скрытые защелки |
| STWS-525х225-Z-SO | 0.071 м² | 525 мм | 520 мм | 225 мм | 220 мм | 23 | 53 | Оцинкованная сталь (INPLAST) | скрытые защелки |
| STWS-525х250-Z-SO | 0.079 м² | 525 мм | 520 мм | 250 мм | 245 мм | 25 | 53 | Оцинкованная сталь (INPLAST) | скрытые защелки |
| STWS-525х300-Z-SO | 0.095 м² | 525 мм | 520 мм | 300 мм | 295 мм | 30 | 53 | Оцинкованная сталь (INPLAST) | скрытые защелки |
| STWS-525х325-Z-SO | 0.103 м² | 525 мм | 520 мм | 325 мм | 320 мм | 33 | 53 | Оцинкованная сталь (INPLAST) | скрытые защелки |
| STWS-525х350-Z-SO | 0.111 м² | 525 мм | 520 мм | 350 мм | 345 мм | 35 | 53 | Оцинкованная сталь (INPLAST) | скрытые защелки |
| STWS-525х400-Z-SO | 0.126 м² | 525 мм | 520 мм | 400 мм | 395 мм | 40 | 53 | Оцинкованная сталь (INPLAST) | скрытые защелки |
| STWS-525х425-Z-SO | 0.134 м² | 525 мм | 520 мм | 425 мм | 420 мм | 43 | 53 | Оцинкованная сталь (INPLAST) | скрытые защелки |
| STWS-525х450-Z-SO | 0.142 м² | 525 мм | 520 мм | 450 мм | 445 мм | 45 | 53 | Оцинкованная сталь (INPLAST) | скрытые защелки |
| STWS-525х500-Z-SO | 0.158 м² | 525 мм | 520 мм | 500 мм | 495 мм | 50 | 53 | Оцинкованная сталь (INPLAST) | скрытые защелки |
| STWS-525х525-Z-SO | 0.166 м² | 525 мм | 520 мм | 525 мм | 520 мм | 53 | 53 | Оцинкованная сталь (INPLAST) | скрытые защелки |
| STWS-550х100-Z-SO | 0.033 м² | 550 мм | 545 мм | 100 мм | 95 мм | 10 | 55 | Оцинкованная сталь (INPLAST) | скрытые защелки |
| STWS-550х125-Z-SO | 0.041 м² | 550 мм | 545 мм | 125 мм | 120 мм | 13 | 55 | Оцинкованная сталь (INPLAST) | скрытые защелки |
| STWS-550х150-Z-SO | 0.050 м² | 550 мм | 545 мм | 150 мм | 145 мм | 15 | 55 | Оцинкованная сталь (INPLAST) | скрытые защелки |
| STWS-550х200-Z-SO | 0.066 м² | 550 мм | 545 мм | 200 мм | 195 мм | 20 | 55 | Оцинкованная сталь (INPLAST) | скрытые защелки |
| STWS-550х225-Z-SO | 0.074 м² | 550 мм | 545 мм | 225 мм | 220 мм | 23 | 55 | Оцинкованная сталь (INPLAST) | скрытые защелки |
| STWS-550х250-Z-SO | 0.083 м² | 550 мм | 545 мм | 250 мм | 245 мм | 25 | 55 | Оцинкованная сталь (INPLAST) | скрытые защелки |
| STWS-550х300-Z-SO | 0.099 м² | 550 мм | 545 мм | 300 мм | 295 мм | 30 | 55 | Оцинкованная сталь (INPLAST) | скрытые защелки |
| STWS-550х325-Z-SO | 0.108 м² | 550 мм | 545 мм | 325 мм | 320 мм | 33 | 55 | Оцинкованная сталь (INPLAST) | скрытые защелки |
| STWS-550х350-Z-SO | 0.116 м² | 550 мм | 545 мм | 350 мм | 345 мм | 35 | 55 | Оцинкованная сталь (INPLAST) | скрытые защелки |
| STWS-550х400-Z-SO | 0.132 м² | 550 мм | 545 мм | 400 мм | 395 мм | 40 | 55 | Оцинкованная сталь (INPLAST) | скрытые защелки |
| STWS-550х425-Z-SO | 0.141 м² | 550 мм | 545 мм | 425 мм | 420 мм | 43 | 55 | Оцинкованная сталь (INPLAST) | скрытые защелки |
| STWS-550х450-Z-SO | 0.149 м² | 550 мм | 545 мм | 450 мм | 445 мм | 45 | 55 | Оцинкованная сталь (INPLAST) | скрытые защелки |
| STWS-550х500-Z-SO | 0.165 м² | 550 мм | 545 мм | 500 мм | 495 мм | 50 | 55 | Оцинкованная сталь (INPLAST) | скрытые защелки |
| STWS-550х525-Z-SO | 0.174 м² | 550 мм | 545 мм | 525 мм | 520 мм | 53 | 55 | Оцинкованная сталь (INPLAST) | скрытые защелки |
| STWS-550х550-Z-SO | 0.182 м² | 550 мм | 545 мм | 550 мм | 545 мм | 55 | 55 | Оцинкованная сталь (INPLAST) | скрытые защелки |
| STWS-600х100-Z-SO | 0.036 м² | 600 мм | 595 мм | 100 мм | 95 мм | 10 | 60 | Оцинкованная сталь (INPLAST) | скрытые защелки |
| STWS-600х125-Z-SO | 0.045 м² | 600 мм | 595 мм | 125 мм | 120 мм | 13 | 60 | Оцинкованная сталь (INPLAST) | скрытые защелки |
| STWS-600х150-Z-SO | 0.054 м² | 600 мм | 595 мм | 150 мм | 145 мм | 15 | 60 | Оцинкованная сталь (INPLAST) | скрытые защелки |
| STWS-600х200-Z-SO | 0.072 м² | 600 мм | 595 мм | 200 мм | 195 мм | 20 | 60 | Оцинкованная сталь (INPLAST) | скрытые защелки |
| STWS-600х225-Z-SO | 0.081 м² | 600 мм | 595 мм | 225 мм | 220 мм | 23 | 60 | Оцинкованная сталь (INPLAST) | скрытые защелки |
| STWS-600х250-Z-SO | 0.090 м² | 600 мм | 595 мм | 250 мм | 245 мм | 25 | 60 | Оцинкованная сталь (INPLAST) | скрытые защелки |
| STWS-600х300-Z-SO | 0.108 м² | 600 мм | 595 мм | 300 мм | 295 мм | 30 | 60 | Оцинкованная сталь (INPLAST) | скрытые защелки |
| STWS-600х325-Z-SO | 0.117 м² | 600 мм | 595 мм | 325 мм | 320 мм | 33 | 60 | Оцинкованная сталь (INPLAST) | скрытые защелки |
| STWS-600х350-Z-SO | 0.126 м² | 600 мм | 595 мм | 350 мм | 345 мм | 35 | 60 | Оцинкованная сталь (INPLAST) | скрытые защелки |
| STWS-600х400-Z-SO | 0.144 м² | 600 мм | 595 мм | 400 мм | 395 мм | 40 | 60 | Оцинкованная сталь (INPLAST) | скрытые защелки |
| STWS-600х425-Z-SO | 0.153 м² | 600 мм | 595 мм | 425 мм | 420 мм | 43 | 60 | Оцинкованная сталь (INPLAST) | скрытые защелки |
| STWS-600х450-Z-SO | 0.162 м² | 600 мм | 595 мм | 450 мм | 445 мм | 45 | 60 | Оцинкованная сталь (INPLAST) | скрытые защелки |
| STWS-600х500-Z-SO | 0.180 м² | 600 мм | 595 мм | 500 мм | 495 мм | 50 | 60 | Оцинкованная сталь (INPLAST) | скрытые защелки |
| STWS-600х525-Z-SO | 0.190 м² | 600 мм | 595 мм | 525 мм | 520 мм | 53 | 60 | Оцинкованная сталь (INPLAST) | скрытые защелки |
| STWS-600х550-Z-SO | 0.199 м² | 600 мм | 595 мм | 550 мм | 545 мм | 55 | 60 | Оцинкованная сталь (INPLAST) | скрытые защелки |
| STWS-600х600-Z-SO | 0.217 м² | 600 мм | 595 мм | 600 мм | 595 мм | 60 | 60 | Оцинкованная сталь (INPLAST) | скрытые защелки |
| STWS-625х100-Z-SO | 0.038 м² | 625 мм | 620 мм | 100 мм | 95 мм | 10 | 63 | Оцинкованная сталь (INPLAST) | скрытые защелки |
| STWS-625х125-Z-SO | 0.047 м² | 625 мм | 620 мм | 125 мм | 120 мм | 13 | 63 | Оцинкованная сталь (INPLAST) | скрытые защелки |
| STWS-625х150-Z-SO | 0.056 м² | 625 мм | 620 мм | 150 мм | 145 мм | 15 | 63 | Оцинкованная сталь (INPLAST) | скрытые защелки |
| STWS-625х200-Z-SO | 0.075 м² | 625 мм | 620 мм | 200 мм | 195 мм | 20 | 63 | Оцинкованная сталь (INPLAST) | скрытые защелки |
| STWS-625х225-Z-SO | 0.085 м² | 625 мм | 620 мм | 225 мм | 220 мм | 23 | 63 | Оцинкованная сталь (INPLAST) | скрытые защелки |
| STWS-625х250-Z-SO | 0.094 м² | 625 мм | 620 мм | 250 мм | 245 мм | 25 | 63 | Оцинкованная сталь (INPLAST) | скрытые защелки |
| STWS-625х300-Z-SO | 0.113 м² | 625 мм | 620 мм | 300 мм | 295 мм | 30 | 63 | Оцинкованная сталь (INPLAST) | скрытые защелки |
| STWS-625х325-Z-SO | 0.122 м² | 625 мм | 620 мм | 325 мм | 320 мм | 33 | 63 | Оцинкованная сталь (INPLAST) | скрытые защелки |
| STWS-625х350-Z-SO | 0.132 м² | 625 мм | 620 мм | 350 мм | 345 мм | 35 | 63 | Оцинкованная сталь (INPLAST) | скрытые защелки |
| STWS-625х400-Z-SO | 0.150 м² | 625 мм | 620 мм | 400 мм | 395 мм | 40 | 63 | Оцинкованная сталь (INPLAST) | скрытые защелки |
| STWS-625х425-Z-SO | 0.160 м² | 625 мм | 620 мм | 425 мм | 420 мм | 43 | 63 | Оцинкованная сталь (INPLAST) | скрытые защелки |
| STWS-625х450-Z-SO | 0.169 м² | 625 мм | 620 мм | 450 мм | 445 мм | 45 | 63 | Оцинкованная сталь (INPLAST) | скрытые защелки |
| STWS-625х500-Z-SO | 0.188 м² | 625 мм | 620 мм | 500 мм | 495 мм | 50 | 63 | Оцинкованная сталь (INPLAST) | скрытые защелки |
| STWS-625х525-Z-SO | 0.197 м² | 625 мм | 620 мм | 525 мм | 520 мм | 53 | 63 | Оцинкованная сталь (INPLAST) | скрытые защелки |
| STWS-625х550-Z-SO | 0.207 м² | 625 мм | 620 мм | 550 мм | 545 мм | 55 | 63 | Оцинкованная сталь (INPLAST) | скрытые защелки |
| STWS-625х600-Z-SO | 0.226 м² | 625 мм | 620 мм | 600 мм | 595 мм | 60 | 63 | Оцинкованная сталь (INPLAST) | скрытые защелки |
| STWS-625х625-Z-SO | 0.235 м² | 625 мм | 620 мм | 625 мм | 620 мм | 63 | 63 | Оцинкованная сталь (INPLAST) | скрытые защелки |
| STWS-650х100-Z-SO | 0.039 м² | 650 мм | 645 мм | 100 мм | 95 мм | 10 | 65 | Оцинкованная сталь (INPLAST) | скрытые защелки |
| STWS-650х125-Z-SO | 0.049 м² | 650 мм | 645 мм | 125 мм | 120 мм | 13 | 65 | Оцинкованная сталь (INPLAST) | скрытые защелки |
| STWS-650х150-Z-SO | 0.059 м² | 650 мм | 645 мм | 150 мм | 145 мм | 15 | 65 | Оцинкованная сталь (INPLAST) | скрытые защелки |
| STWS-650х200-Z-SO | 0.078 м² | 650 мм | 645 мм | 200 мм | 195 мм | 20 | 65 | Оцинкованная сталь (INPLAST) | скрытые защелки |
| STWS-650х225-Z-SO | 0.088 м² | 650 мм | 645 мм | 225 мм | 220 мм | 23 | 65 | Оцинкованная сталь (INPLAST) | скрытые защелки |
| STWS-650х250-Z-SO | 0.098 м² | 650 мм | 645 мм | 250 мм | 245 мм | 25 | 65 | Оцинкованная сталь (INPLAST) | скрытые защелки |
| STWS-650х300-Z-SO | 0.117 м² | 650 мм | 645 мм | 300 мм | 295 мм | 30 | 65 | Оцинкованная сталь (INPLAST) | скрытые защелки |
| STWS-650х325-Z-SO | 0.127 м² | 650 мм | 645 мм | 325 мм | 320 мм | 33 | 65 | Оцинкованная сталь (INPLAST) | скрытые защелки |
| STWS-650х350-Z-SO | 0.137 м² | 650 мм | 645 мм | 350 мм | 345 мм | 35 | 65 | Оцинкованная сталь (INPLAST) | скрытые защелки |
| STWS-650х400-Z-SO | 0.156 м² | 650 мм | 645 мм | 400 мм | 395 мм | 40 | 65 | Оцинкованная сталь (INPLAST) | скрытые защелки |
| STWS-650х425-Z-SO | 0.166 м² | 650 мм | 645 мм | 425 мм | 420 мм | 43 | 65 | Оцинкованная сталь (INPLAST) | скрытые защелки |
| STWS-650х450-Z-SO | 0.176 м² | 650 мм | 645 мм | 450 мм | 445 мм | 45 | 65 | Оцинкованная сталь (INPLAST) | скрытые защелки |
| STWS-650х500-Z-SO | 0.196 м² | 650 мм | 645 мм | 500 мм | 495 мм | 50 | 65 | Оцинкованная сталь (INPLAST) | скрытые защелки |
| STWS-650х525-Z-SO | 0.205 м² | 650 мм | 645 мм | 525 мм | 520 мм | 53 | 65 | Оцинкованная сталь (INPLAST) | скрытые защелки |
| STWS-650х550-Z-SO | 0.215 м² | 650 мм | 645 мм | 550 мм | 545 мм | 55 | 65 | Оцинкованная сталь (INPLAST) | скрытые защелки |
| STWS-650х600-Z-SO | 0.235 м² | 650 мм | 645 мм | 600 мм | 595 мм | 60 | 65 | Оцинкованная сталь (INPLAST) | скрытые защелки |
| STWS-650х625-Z-SO | 0.244 м² | 650 мм | 645 мм | 625 мм | 620 мм | 63 | 65 | Оцинкованная сталь (INPLAST) | скрытые защелки |
| STWS-650х650-Z-SO | 0.254 м² | 650 мм | 645 мм | 650 мм | 645 мм | 65 | 65 | Оцинкованная сталь (INPLAST) | скрытые защелки |
| STWS-700х100-Z-SO | 0.042 м² | 700 мм | 695 мм | 100 мм | 95 мм | 10 | 70 | Оцинкованная сталь (INPLAST) | скрытые защелки |
| STWS-700х125-Z-SO | 0.053 м² | 700 мм | 695 мм | 125 мм | 120 мм | 13 | 70 | Оцинкованная сталь (INPLAST) | скрытые защелки |
| STWS-700х150-Z-SO | 0.063 м² | 700 мм | 695 мм | 150 мм | 145 мм | 15 | 70 | Оцинкованная сталь (INPLAST) | скрытые защелки |
| STWS-700х200-Z-SO | 0.084 м² | 700 мм | 695 мм | 200 мм | 195 мм | 20 | 70 | Оцинкованная сталь (INPLAST) | скрытые защелки |
| STWS-700х225-Z-SO | 0.095 м² | 700 мм | 695 мм | 225 мм | 220 мм | 23 | 70 | Оцинкованная сталь (INPLAST) | скрытые защелки |
| STWS-700х250-Z-SO | 0.105 м² | 700 мм | 695 мм | 250 мм | 245 мм | 25 | 70 | Оцинкованная сталь (INPLAST) | скрытые защелки |
| STWS-700х300-Z-SO | 0.126 м² | 700 мм | 695 мм | 300 мм | 295 мм | 30 | 70 | Оцинкованная сталь (INPLAST) | скрытые защелки |
| STWS-700х325-Z-SO | 0.137 м² | 700 мм | 695 мм | 325 мм | 320 мм | 33 | 70 | Оцинкованная сталь (INPLAST) | скрытые защелки |
| STWS-700х350-Z-SO | 0.147 м² | 700 мм | 695 мм | 350 мм | 345 мм | 35 | 70 | Оцинкованная сталь (INPLAST) | скрытые защелки |
| STWS-700х400-Z-SO | 0.168 м² | 700 мм | 695 мм | 400 мм | 395 мм | 40 | 70 | Оцинкованная сталь (INPLAST) | скрытые защелки |
| STWS-700х425-Z-SO | 0.179 м² | 700 мм | 695 мм | 425 мм | 420 мм | 43 | 70 | Оцинкованная сталь (INPLAST) | скрытые защелки |
| STWS-700х450-Z-SO | 0.190 м² | 700 мм | 695 мм | 450 мм | 445 мм | 45 | 70 | Оцинкованная сталь (INPLAST) | скрытые защелки |
| STWS-700х500-Z-SO | 0.211 м² | 700 мм | 695 мм | 500 мм | 495 мм | 50 | 70 | Оцинкованная сталь (INPLAST) | скрытые защелки |
| STWS-700х525-Z-SO | 0.221 м² | 700 мм | 695 мм | 525 мм | 520 мм | 53 | 70 | Оцинкованная сталь (INPLAST) | скрытые защелки |
| STWS-700х550-Z-SO | 0.232 м² | 700 мм | 695 мм | 550 мм | 545 мм | 55 | 70 | Оцинкованная сталь (INPLAST) | скрытые защелки |
| STWS-700х600-Z-SO | 0.253 м² | 700 мм | 695 мм | 600 мм | 595 мм | 60 | 70 | Оцинкованная сталь (INPLAST) | скрытые защелки |
| STWS-700х625-Z-SO | 0.263 м² | 700 мм | 695 мм | 625 мм | 620 мм | 63 | 70 | Оцинкованная сталь (INPLAST) | скрытые защелки |
| STWS-700х650-Z-SO | 0.274 м² | 700 мм | 695 мм | 650 мм | 645 мм | 65 | 70 | Оцинкованная сталь (INPLAST) | скрытые защелки |
| STWS-725х100-Z-SO | 0.044 м² | 725 мм | 720 мм | 100 мм | 95 мм | 10 | 73 | Оцинкованная сталь (INPLAST) | скрытые защелки |
| STWS-725х125-Z-SO | 0.055 м² | 725 мм | 720 мм | 125 мм | 120 мм | 13 | 73 | Оцинкованная сталь (INPLAST) | скрытые защелки |
| STWS-725х150-Z-SO | 0.065 м² | 725 мм | 720 мм | 150 мм | 145 мм | 15 | 73 | Оцинкованная сталь (INPLAST) | скрытые защелки |
| STWS-725х200-Z-SO | 0.087 м² | 725 мм | 720 мм | 200 мм | 195 мм | 20 | 73 | Оцинкованная сталь (INPLAST) | скрытые защелки |
| STWS-725х225-Z-SO | 0.098 м² | 725 мм | 720 мм | 225 мм | 220 мм | 23 | 73 | Оцинкованная сталь (INPLAST) | скрытые защелки |
| STWS-725х250-Z-SO | 0.109 м² | 725 мм | 720 мм | 250 мм | 245 мм | 25 | 73 | Оцинкованная сталь (INPLAST) | скрытые защелки |
| STWS-725х300-Z-SO | 0.131 м² | 725 мм | 720 мм | 300 мм | 295 мм | 30 | 73 | Оцинкованная сталь (INPLAST) | скрытые защелки |
| STWS-725х325-Z-SO | 0.142 м² | 725 мм | 720 мм | 325 мм | 320 мм | 33 | 73 | Оцинкованная сталь (INPLAST) | скрытые защелки |
| STWS-725х350-Z-SO | 0.153 м² | 725 мм | 720 мм | 350 мм | 345 мм | 35 | 73 | Оцинкованная сталь (INPLAST) | скрытые защелки |
| STWS-725х400-Z-SO | 0.174 м² | 725 мм | 720 мм | 400 мм | 395 мм | 40 | 73 | Оцинкованная сталь (INPLAST) | скрытые защелки |
| STWS-725х425-Z-SO | 0.185 м² | 725 мм | 720 мм | 425 мм | 420 мм | 43 | 73 | Оцинкованная сталь (INPLAST) | скрытые защелки |
| STWS-725х450-Z-SO | 0.196 м² | 725 мм | 720 мм | 450 мм | 445 мм | 45 | 73 | Оцинкованная сталь (INPLAST) | скрытые защелки |
| STWS-725х500-Z-SO | 0.218 м² | 725 мм | 720 мм | 500 мм | 495 мм | 50 | 73 | Оцинкованная сталь (INPLAST) | скрытые защелки |
| STWS-725х525-Z-SO | 0.229 м² | 725 мм | 720 мм | 525 мм | 520 мм | 53 | 73 | Оцинкованная сталь (INPLAST) | скрытые защелки |
| STWS-725х550-Z-SO | 0.240 м² | 725 мм | 720 мм | 550 мм | 545 мм | 55 | 73 | Оцинкованная сталь (INPLAST) | скрытые защелки |
| STWS-725х600-Z-SO | 0.262 м² | 725 мм | 720 мм | 600 мм | 595 мм | 60 | 73 | Оцинкованная сталь (INPLAST) | скрытые защелки |
| STWS-725х625-Z-SO | 0.273 м² | 725 мм | 720 мм | 625 мм | 620 мм | 63 | 73 | Оцинкованная сталь (INPLAST) | скрытые защелки |
| STWS-725х650-Z-SO | 0.284 м² | 725 мм | 720 мм | 650 мм | 645 мм | 65 | 73 | Оцинкованная сталь (INPLAST) | скрытые защелки |
| STWS-750х100-Z-SO | 0.045 м² | 750 мм | 745 мм | 100 мм | 95 мм | 10 | 75 | Оцинкованная сталь (INPLAST) | скрытые защелки |
| STWS-750х125-Z-SO | 0.056 м² | 750 мм | 745 мм | 125 мм | 120 мм | 13 | 75 | Оцинкованная сталь (INPLAST) | скрытые защелки |
| STWS-750х150-Z-SO | 0.068 м² | 750 мм | 745 мм | 150 мм | 145 мм | 15 | 75 | Оцинкованная сталь (INPLAST) | скрытые защелки |
| STWS-750х200-Z-SO | 0.090 м² | 750 мм | 745 мм | 200 мм | 195 мм | 20 | 75 | Оцинкованная сталь (INPLAST) | скрытые защелки |
| STWS-750х225-Z-SO | 0.102 м² | 750 мм | 745 мм | 225 мм | 220 мм | 23 | 75 | Оцинкованная сталь (INPLAST) | скрытые защелки |
| STWS-750х250-Z-SO | 0.113 м² | 750 мм | 745 мм | 250 мм | 245 мм | 25 | 75 | Оцинкованная сталь (INPLAST) | скрытые защелки |
| STWS-750х300-Z-SO | 0.135 м² | 750 мм | 745 мм | 300 мм | 295 мм | 30 | 75 | Оцинкованная сталь (INPLAST) | скрытые защелки |
| STWS-750х325-Z-SO | 0.147 м² | 750 мм | 745 мм | 325 мм | 320 мм | 33 | 75 | Оцинкованная сталь (INPLAST) | скрытые защелки |
| STWS-750х350-Z-SO | 0.158 м² | 750 мм | 745 мм | 350 мм | 345 мм | 35 | 75 | Оцинкованная сталь (INPLAST) | скрытые защелки |
| STWS-750х400-Z-SO | 0.180 м² | 750 мм | 745 мм | 400 мм | 395 мм | 40 | 75 | Оцинкованная сталь (INPLAST) | скрытые защелки |
| STWS-750х425-Z-SO | 0.192 м² | 750 мм | 745 мм | 425 мм | 420 мм | 43 | 75 | Оцинкованная сталь (INPLAST) | скрытые защелки |
| STWS-750х450-Z-SO | 0.203 м² | 750 мм | 745 мм | 450 мм | 445 мм | 45 | 75 | Оцинкованная сталь (INPLAST) | скрытые защелки |
| STWS-750х500-Z-SO | 0.226 м² | 750 мм | 745 мм | 500 мм | 495 мм | 50 | 75 | Оцинкованная сталь (INPLAST) | скрытые защелки |
| STWS-750х525-Z-SO | 0.237 м² | 750 мм | 745 мм | 525 мм | 520 мм | 53 | 75 | Оцинкованная сталь (INPLAST) | скрытые защелки |
| STWS-750х550-Z-SO | 0.248 м² | 750 мм | 745 мм | 550 мм | 545 мм | 55 | 75 | Оцинкованная сталь (INPLAST) | скрытые защелки |
| STWS-750х600-Z-SO | 0.271 м² | 750 мм | 745 мм | 600 мм | 595 мм | 60 | 75 | Оцинкованная сталь (INPLAST) | скрытые защелки |
| STWS-750х625-Z-SO | 0.282 м² | 750 мм | 745 мм | 625 мм | 620 мм | 63 | 75 | Оцинкованная сталь (INPLAST) | скрытые защелки |
| STWS-750х650-Z-SO | 0.293 м² | 750 мм | 745 мм | 650 мм | 645 мм | 65 | 75 | Оцинкованная сталь (INPLAST) | скрытые защелки |
| STWS-800х100-Z-SO | 0.048 м² | 800 мм | 795 мм | 100 мм | 95 мм | 10 | 80 | Оцинкованная сталь (INPLAST) | скрытые защелки |
| STWS-800х125-Z-SO | 0.060 м² | 800 мм | 795 мм | 125 мм | 120 мм | 13 | 80 | Оцинкованная сталь (INPLAST) | скрытые защелки |
| STWS-800х150-Z-SO | 0.072 м² | 800 мм | 795 мм | 150 мм | 145 мм | 15 | 80 | Оцинкованная сталь (INPLAST) | скрытые защелки |
| STWS-800х200-Z-SO | 0.096 м² | 800 мм | 795 мм | 200 мм | 195 мм | 20 | 80 | Оцинкованная сталь (INPLAST) | скрытые защелки |
| STWS-800х225-Z-SO | 0.108 м² | 800 мм | 795 мм | 225 мм | 220 мм | 23 | 80 | Оцинкованная сталь (INPLAST) | скрытые защелки |
| STWS-800х250-Z-SO | 0.120 м² | 800 мм | 795 мм | 250 мм | 245 мм | 25 | 80 | Оцинкованная сталь (INPLAST) | скрытые защелки |
| STWS-800х300-Z-SO | 0.144 м² | 800 мм | 795 мм | 300 мм | 295 мм | 30 | 80 | Оцинкованная сталь (INPLAST) | скрытые защелки |
| STWS-800х325-Z-SO | 0.156 м² | 800 мм | 795 мм | 325 мм | 320 мм | 33 | 80 | Оцинкованная сталь (INPLAST) | скрытые защелки |
| STWS-800х350-Z-SO | 0.168 м² | 800 мм | 795 мм | 350 мм | 345 мм | 35 | 80 | Оцинкованная сталь (INPLAST) | скрытые защелки |
| STWS-800х400-Z-SO | 0.193 м² | 800 мм | 795 мм | 400 мм | 395 мм | 40 | 80 | Оцинкованная сталь (INPLAST) | скрытые защелки |
| STWS-800х425-Z-SO | 0.205 м² | 800 мм | 795 мм | 425 мм | 420 мм | 43 | 80 | Оцинкованная сталь (INPLAST) | скрытые защелки |
| STWS-800х450-Z-SO | 0.217 м² | 800 мм | 795 мм | 450 мм | 445 мм | 45 | 80 | Оцинкованная сталь (INPLAST) | скрытые защелки |
| STWS-800х500-Z-SO | 0.241 м² | 800 мм | 795 мм | 500 мм | 495 мм | 50 | 80 | Оцинкованная сталь (INPLAST) | скрытые защелки |
| STWS-800х525-Z-SO | 0.253 м² | 800 мм | 795 мм | 525 мм | 520 мм | 53 | 80 | Оцинкованная сталь (INPLAST) | скрытые защелки |
| STWS-800х550-Z-SO | 0.265 м² | 800 мм | 795 мм | 550 мм | 545 мм | 55 | 80 | Оцинкованная сталь (INPLAST) | скрытые защелки |
| STWS-800х600-Z-SO | 0.289 м² | 800 мм | 795 мм | 600 мм | 595 мм | 60 | 80 | Оцинкованная сталь (INPLAST) | скрытые защелки |
| STWS-800х625-Z-SO | 0.301 м² | 800 мм | 795 мм | 625 мм | 620 мм | 63 | 80 | Оцинкованная сталь (INPLAST) | скрытые защелки |
| STWS-800х650-Z-SO | 0.313 м² | 800 мм | 795 мм | 650 мм | 645 мм | 65 | 80 | Оцинкованная сталь (INPLAST) | скрытые защелки |
| STWS-825х100-Z-SO | 0.050 м² | 825 мм | 820 мм | 100 мм | 95 мм | 10 | 83 | Оцинкованная сталь (INPLAST) | скрытые защелки |
| STWS-825х125-Z-SO | 0.062 м² | 825 мм | 820 мм | 125 мм | 120 мм | 13 | 83 | Оцинкованная сталь (INPLAST) | скрытые защелки |
| STWS-825х150-Z-SO | 0.074 м² | 825 мм | 820 мм | 150 мм | 145 мм | 15 | 83 | Оцинкованная сталь (INPLAST) | скрытые защелки |
| STWS-825х200-Z-SO | 0.099 м² | 825 мм | 820 мм | 200 мм | 195 мм | 20 | 83 | Оцинкованная сталь (INPLAST) | скрытые защелки |
| STWS-825х225-Z-SO | 0.112 м² | 825 мм | 820 мм | 225 мм | 220 мм | 23 | 83 | Оцинкованная сталь (INPLAST) | скрытые защелки |
| STWS-825х250-Z-SO | 0.124 м² | 825 мм | 820 мм | 250 мм | 245 мм | 25 | 83 | Оцинкованная сталь (INPLAST) | скрытые защелки |
| STWS-825х300-Z-SO | 0.149 м² | 825 мм | 820 мм | 300 мм | 295 мм | 30 | 83 | Оцинкованная сталь (INPLAST) | скрытые защелки |
| STWS-825х325-Z-SO | 0.161 м² | 825 мм | 820 мм | 325 мм | 320 мм | 33 | 83 | Оцинкованная сталь (INPLAST) | скрытые защелки |
| STWS-825х350-Z-SO | 0.174 м² | 825 мм | 820 мм | 350 мм | 345 мм | 35 | 83 | Оцинкованная сталь (INPLAST) | скрытые защелки |
| STWS-825х400-Z-SO | 0.199 м² | 825 мм | 820 мм | 400 мм | 395 мм | 40 | 83 | Оцинкованная сталь (INPLAST) | скрытые защелки |
| STWS-825х425-Z-SO | 0.211 м² | 825 мм | 820 мм | 425 мм | 420 мм | 43 | 83 | Оцинкованная сталь (INPLAST) | скрытые защелки |
| STWS-825х450-Z-SO | 0.223 м² | 825 мм | 820 мм | 450 мм | 445 мм | 45 | 83 | Оцинкованная сталь (INPLAST) | скрытые защелки |
| STWS-825х500-Z-SO | 0.248 м² | 825 мм | 820 мм | 500 мм | 495 мм | 50 | 83 | Оцинкованная сталь (INPLAST) | скрытые защелки |
| STWS-825х525-Z-SO | 0.261 м² | 825 мм | 820 мм | 525 мм | 520 мм | 53 | 83 | Оцинкованная сталь (INPLAST) | скрытые защелки |
| STWS-825х550-Z-SO | 0.273 м² | 825 мм | 820 мм | 550 мм | 545 мм | 55 | 83 | Оцинкованная сталь (INPLAST) | скрытые защелки |
| STWS-825х600-Z-SO | 0.298 м² | 825 мм | 820 мм | 600 мм | 595 мм | 60 | 83 | Оцинкованная сталь (INPLAST) | скрытые защелки |
| STWS-825х625-Z-SO | 0.310 м² | 825 мм | 820 мм | 625 мм | 620 мм | 63 | 83 | Оцинкованная сталь (INPLAST) | скрытые защелки |
| STWS-825х650-Z-SO | 0.323 м² | 825 мм | 820 мм | 650 мм | 645 мм | 65 | 83 | Оцинкованная сталь (INPLAST) | скрытые защелки |
| STWS-850х100-Z-SO | 0.051 м² | 850 мм | 845 мм | 100 мм | 95 мм | 10 | 85 | Оцинкованная сталь (INPLAST) | скрытые защелки |
| STWS-850х125-Z-SO | 0.064 м² | 850 мм | 845 мм | 125 мм | 120 мм | 13 | 85 | Оцинкованная сталь (INPLAST) | скрытые защелки |
| STWS-850х150-Z-SO | 0.077 м² | 850 мм | 845 мм | 150 мм | 145 мм | 15 | 85 | Оцинкованная сталь (INPLAST) | скрытые защелки |
| STWS-850х200-Z-SO | 0.102 м² | 850 мм | 845 мм | 200 мм | 195 мм | 20 | 85 | Оцинкованная сталь (INPLAST) | скрытые защелки |
| STWS-850х225-Z-SO | 0.115 м² | 850 мм | 845 мм | 225 мм | 220 мм | 23 | 85 | Оцинкованная сталь (INPLAST) | скрытые защелки |
| STWS-850х250-Z-SO | 0.128 м² | 850 мм | 845 мм | 250 мм | 245 мм | 25 | 85 | Оцинкованная сталь (INPLAST) | скрытые защелки |
| STWS-850х300-Z-SO | 0.153 м² | 850 мм | 845 мм | 300 мм | 295 мм | 30 | 85 | Оцинкованная сталь (INPLAST) | скрытые защелки |
| STWS-850х325-Z-SO | 0.166 м² | 850 мм | 845 мм | 325 мм | 320 мм | 33 | 85 | Оцинкованная сталь (INPLAST) | скрытые защелки |
| STWS-850х350-Z-SO | 0.179 м² | 850 мм | 845 мм | 350 мм | 345 мм | 35 | 85 | Оцинкованная сталь (INPLAST) | скрытые защелки |
| STWS-850х400-Z-SO | 0.205 м² | 850 мм | 845 мм | 400 мм | 395 мм | 40 | 85 | Оцинкованная сталь (INPLAST) | скрытые защелки |
| STWS-850х425-Z-SO | 0.217 м² | 850 мм | 845 мм | 425 мм | 420 мм | 43 | 85 | Оцинкованная сталь (INPLAST) | скрытые защелки |
| STWS-850х450-Z-SO | 0.230 м² | 850 мм | 845 мм | 450 мм | 445 мм | 45 | 85 | Оцинкованная сталь (INPLAST) | скрытые защелки |
| STWS-850х500-Z-SO | 0.256 м² | 850 мм | 845 мм | 500 мм | 495 мм | 50 | 85 | Оцинкованная сталь (INPLAST) | скрытые защелки |
| STWS-850х525-Z-SO | 0.268 м² | 850 мм | 845 мм | 525 мм | 520 мм | 53 | 85 | Оцинкованная сталь (INPLAST) | скрытые защелки |
| STWS-850х550-Z-SO | 0.281 м² | 850 мм | 845 мм | 550 мм | 545 мм | 55 | 85 | Оцинкованная сталь (INPLAST) | скрытые защелки |
| STWS-850х600-Z-SO | 0.307 м² | 850 мм | 845 мм | 600 мм | 595 мм | 60 | 85 | Оцинкованная сталь (INPLAST) | скрытые защелки |
| STWS-850х625-Z-SO | 0.320 м² | 850 мм | 845 мм | 625 мм | 620 мм | 63 | 85 | Оцинкованная сталь (INPLAST) | скрытые защелки |
| STWS-850х650-Z-SO | 0.332 м² | 850 мм | 845 мм | 650 мм | 645 мм | 65 | 85 | Оцинкованная сталь (INPLAST) | скрытые защелки |
| STWS-900х100-Z-SO | 0.054 м² | 900 мм | 895 мм | 100 мм | 95 мм | 10 | 90 | Оцинкованная сталь (INPLAST) | скрытые защелки |
| STWS-900х125-Z-SO | 0.068 м² | 900 мм | 895 мм | 125 мм | 120 мм | 13 | 90 | Оцинкованная сталь (INPLAST) | скрытые защелки |
| STWS-900х150-Z-SO | 0.081 м² | 900 мм | 895 мм | 150 мм | 145 мм | 15 | 90 | Оцинкованная сталь (INPLAST) | скрытые защелки |
| STWS-900х200-Z-SO | 0.108 м² | 900 мм | 895 мм | 200 мм | 195 мм | 20 | 90 | Оцинкованная сталь (INPLAST) | скрытые защелки |
| STWS-900х225-Z-SO | 0.122 м² | 900 мм | 895 мм | 225 мм | 220 мм | 23 | 90 | Оцинкованная сталь (INPLAST) | скрытые защелки |
| STWS-900х250-Z-SO | 0.135 м² | 900 мм | 895 мм | 250 мм | 245 мм | 25 | 90 | Оцинкованная сталь (INPLAST) | скрытые защелки |
| STWS-900х300-Z-SO | 0.162 м² | 900 мм | 895 мм | 300 мм | 295 мм | 30 | 90 | Оцинкованная сталь (INPLAST) | скрытые защелки |
| STWS-900х325-Z-SO | 0.176 м² | 900 мм | 895 мм | 325 мм | 320 мм | 33 | 90 | Оцинкованная сталь (INPLAST) | скрытые защелки |
| STWS-900х350-Z-SO | 0.190 м² | 900 мм | 895 мм | 350 мм | 345 мм | 35 | 90 | Оцинкованная сталь (INPLAST) | скрытые защелки |
| STWS-900х400-Z-SO | 0.217 м² | 900 мм | 895 мм | 400 мм | 395 мм | 40 | 90 | Оцинкованная сталь (INPLAST) | скрытые защелки |
| STWS-900х425-Z-SO | 0.230 м² | 900 мм | 895 мм | 425 мм | 420 мм | 43 | 90 | Оцинкованная сталь (INPLAST) | скрытые защелки |
| STWS-900х450-Z-SO | 0.244 м² | 900 мм | 895 мм | 450 мм | 445 мм | 45 | 90 | Оцинкованная сталь (INPLAST) | скрытые защелки |
| STWS-900х500-Z-SO | 0.271 м² | 900 мм | 895 мм | 500 мм | 495 мм | 50 | 90 | Оцинкованная сталь (INPLAST) | скрытые защелки |
| STWS-900х525-Z-SO | 0.284 м² | 900 мм | 895 мм | 525 мм | 520 мм | 53 | 90 | Оцинкованная сталь (INPLAST) | скрытые защелки |
| STWS-900х550-Z-SO | 0.298 м² | 900 мм | 895 мм | 550 мм | 545 мм | 55 | 90 | Оцинкованная сталь (INPLAST) | скрытые защелки |
| STWS-900х600-Z-SO | 0.325 м² | 900 мм | 895 мм | 600 мм | 595 мм | 60 | 90 | Оцинкованная сталь (INPLAST) | скрытые защелки |
| STWS-900х625-Z-SO | 0.338 м² | 900 мм | 895 мм | 625 мм | 620 мм | 63 | 90 | Оцинкованная сталь (INPLAST) | скрытые защелки |
| STWS-900х650-Z-SO | 0.352 м² | 900 мм | 895 мм | 650 мм | 645 мм | 65 | 90 | Оцинкованная сталь (INPLAST) | скрытые защелки |
| STWS-925х100-Z-SO | 0.056 м² | 925 мм | 920 мм | 100 мм | 95 мм | 10 | 93 | Оцинкованная сталь (INPLAST) | скрытые защелки |
| STWS-925х125-Z-SO | 0.070 м² | 925 мм | 920 мм | 125 мм | 120 мм | 13 | 93 | Оцинкованная сталь (INPLAST) | скрытые защелки |
| STWS-925х150-Z-SO | 0.083 м² | 925 мм | 920 мм | 150 мм | 145 мм | 15 | 93 | Оцинкованная сталь (INPLAST) | скрытые защелки |
| STWS-925х200-Z-SO | 0.111 м² | 925 мм | 920 мм | 200 мм | 195 мм | 20 | 93 | Оцинкованная сталь (INPLAST) | скрытые защелки |
| STWS-925х225-Z-SO | 0.125 м² | 925 мм | 920 мм | 225 мм | 220 мм | 23 | 93 | Оцинкованная сталь (INPLAST) | скрытые защелки |
| STWS-925х250-Z-SO | 0.139 м² | 925 мм | 920 мм | 250 мм | 245 мм | 25 | 93 | Оцинкованная сталь (INPLAST) | скрытые защелки |
| STWS-925х300-Z-SO | 0.167 м² | 925 мм | 920 мм | 300 мм | 295 мм | 30 | 93 | Оцинкованная сталь (INPLAST) | скрытые защелки |
| STWS-925х325-Z-SO | 0.181 м² | 925 мм | 920 мм | 325 мм | 320 мм | 33 | 93 | Оцинкованная сталь (INPLAST) | скрытые защелки |
| STWS-925х350-Z-SO | 0.195 м² | 925 мм | 920 мм | 350 мм | 345 мм | 35 | 93 | Оцинкованная сталь (INPLAST) | скрытые защелки |
| STWS-925х400-Z-SO | 0.223 м² | 925 мм | 920 мм | 400 мм | 395 мм | 40 | 93 | Оцинкованная сталь (INPLAST) | скрытые защелки |
| STWS-925х425-Z-SO | 0.237 м² | 925 мм | 920 мм | 425 мм | 420 мм | 43 | 93 | Оцинкованная сталь (INPLAST) | скрытые защелки |
| STWS-925х450-Z-SO | 0.250 м² | 925 мм | 920 мм | 450 мм | 445 мм | 45 | 93 | Оцинкованная сталь (INPLAST) | скрытые защелки |
| STWS-925х500-Z-SO | 0.278 м² | 925 мм | 920 мм | 500 мм | 495 мм | 50 | 93 | Оцинкованная сталь (INPLAST) | скрытые защелки |
| STWS-925х525-Z-SO | 0.292 м² | 925 мм | 920 мм | 525 мм | 520 мм | 53 | 93 | Оцинкованная сталь (INPLAST) | скрытые защелки |
| STWS-925х550-Z-SO | 0.306 м² | 925 мм | 920 мм | 550 мм | 545 мм | 55 | 93 | Оцинкованная сталь (INPLAST) | скрытые защелки |
| STWS-925х600-Z-SO | 0.334 м² | 925 мм | 920 мм | 600 мм | 595 мм | 60 | 93 | Оцинкованная сталь (INPLAST) | скрытые защелки |
| STWS-925х625-Z-SO | 0.348 м² | 925 мм | 920 мм | 625 мм | 620 мм | 63 | 93 | Оцинкованная сталь (INPLAST) | скрытые защелки |
| STWS-925х650-Z-SO | 0.362 м² | 925 мм | 920 мм | 650 мм | 645 мм | 65 | 93 | Оцинкованная сталь (INPLAST) | скрытые защелки |
| STWS-950х100-Z-SO | 0.057 м² | 950 мм | 945 мм | 100 мм | 95 мм | 10 | 95 | Оцинкованная сталь (INPLAST) | скрытые защелки |
| STWS-950х125-Z-SO | 0.071 м² | 950 мм | 945 мм | 125 мм | 120 мм | 13 | 95 | Оцинкованная сталь (INPLAST) | скрытые защелки |
| STWS-950х150-Z-SO | 0.086 м² | 950 мм | 945 мм | 150 мм | 145 мм | 15 | 95 | Оцинкованная сталь (INPLAST) | скрытые защелки |
| STWS-950х200-Z-SO | 0.114 м² | 950 мм | 945 мм | 200 мм | 195 мм | 20 | 95 | Оцинкованная сталь (INPLAST) | скрытые защелки |
| STWS-950х225-Z-SO | 0.129 м² | 950 мм | 945 мм | 225 мм | 220 мм | 23 | 95 | Оцинкованная сталь (INPLAST) | скрытые защелки |
| STWS-950х250-Z-SO | 0.143 м² | 950 мм | 945 мм | 250 мм | 245 мм | 25 | 95 | Оцинкованная сталь (INPLAST) | скрытые защелки |
| STWS-950х300-Z-SO | 0.171 м² | 950 мм | 945 мм | 300 мм | 295 мм | 30 | 95 | Оцинкованная сталь (INPLAST) | скрытые защелки |
| STWS-950х325-Z-SO | 0.186 м² | 950 мм | 945 мм | 325 мм | 320 мм | 33 | 95 | Оцинкованная сталь (INPLAST) | скрытые защелки |
| STWS-950х350-Z-SO | 0.200 м² | 950 мм | 945 мм | 350 мм | 345 мм | 35 | 95 | Оцинкованная сталь (INPLAST) | скрытые защелки |
| STWS-950х400-Z-SO | 0.229 м² | 950 мм | 945 мм | 400 мм | 395 мм | 40 | 95 | Оцинкованная сталь (INPLAST) | скрытые защелки |
| STWS-950х425-Z-SO | 0.243 м² | 950 мм | 945 мм | 425 мм | 420 мм | 43 | 95 | Оцинкованная сталь (INPLAST) | скрытые защелки |
| STWS-950х450-Z-SO | 0.257 м² | 950 мм | 945 мм | 450 мм | 445 мм | 45 | 95 | Оцинкованная сталь (INPLAST) | скрытые защелки |
| STWS-950х500-Z-SO | 0.286 м² | 950 мм | 945 мм | 500 мм | 495 мм | 50 | 95 | Оцинкованная сталь (INPLAST) | скрытые защелки |
| STWS-950х525-Z-SO | 0.300 м² | 950 мм | 945 мм | 525 мм | 520 мм | 53 | 95 | Оцинкованная сталь (INPLAST) | скрытые защелки |
| STWS-950х550-Z-SO | 0.314 м² | 950 мм | 945 мм | 550 мм | 545 мм | 55 | 95 | Оцинкованная сталь (INPLAST) | скрытые защелки |
| STWS-950х600-Z-SO | 0.343 м² | 950 мм | 945 мм | 600 мм | 595 мм | 60 | 95 | Оцинкованная сталь (INPLAST) | скрытые защелки |
| STWS-950х625-Z-SO | 0.357 м² | 950 мм | 945 мм | 625 мм | 620 мм | 63 | 95 | Оцинкованная сталь (INPLAST) | скрытые защелки |
| STWS-950х650-Z-SO | 0.371 м² | 950 мм | 945 мм | 650 мм | 645 мм | 65 | 95 | Оцинкованная сталь (INPLAST) | скрытые защелки |
| STWS-1000х100-Z-SO | 0.060 м² | 1000 мм | 995 мм | 100 мм | 95 мм | 10 | 100 | Оцинкованная сталь (INPLAST) | скрытые защелки |
| STWS-1000х125-Z-SO | 0.075 м² | 1000 мм | 995 мм | 125 мм | 120 мм | 13 | 100 | Оцинкованная сталь (INPLAST) | скрытые защелки |
| STWS-1000х150-Z-SO | 0.090 м² | 1000 мм | 995 мм | 150 мм | 145 мм | 15 | 100 | Оцинкованная сталь (INPLAST) | скрытые защелки |
| STWS-1000х200-Z-SO | 0.120 м² | 1000 мм | 995 мм | 200 мм | 195 мм | 20 | 100 | Оцинкованная сталь (INPLAST) | скрытые защелки |
| STWS-1000х225-Z-SO | 0.135 м² | 1000 мм | 995 мм | 225 мм | 220 мм | 23 | 100 | Оцинкованная сталь (INPLAST) | скрытые защелки |
| STWS-1000х250-Z-SO | 0.150 м² | 1000 мм | 995 мм | 250 мм | 245 мм | 25 | 100 | Оцинкованная сталь (INPLAST) | скрытые защелки |
| STWS-1000х300-Z-SO | 0.180 м² | 1000 мм | 995 мм | 300 мм | 295 мм | 30 | 100 | Оцинкованная сталь (INPLAST) | скрытые защелки |
| STWS-1000х325-Z-SO | 0.196 м² | 1000 мм | 995 мм | 325 мм | 320 мм | 33 | 100 | Оцинкованная сталь (INPLAST) | скрытые защелки |
| STWS-1000х350-Z-SO | 0.211 м² | 1000 мм | 995 мм | 350 мм | 345 мм | 35 | 100 | Оцинкованная сталь (INPLAST) | скрытые защелки |
| STWS-1000х400-Z-SO | 0.241 м² | 1000 мм | 995 мм | 400 мм | 395 мм | 40 | 100 | Оцинкованная сталь (INPLAST) | скрытые защелки |
| STWS-1000х425-Z-SO | 0.256 м² | 1000 мм | 995 мм | 425 мм | 420 мм | 43 | 100 | Оцинкованная сталь (INPLAST) | скрытые защелки |
| STWS-1000х450-Z-SO | 0.271 м² | 1000 мм | 995 мм | 450 мм | 445 мм | 45 | 100 | Оцинкованная сталь (INPLAST) | скрытые защелки |
| STWS-1000х500-Z-SO | 0.301 м² | 1000 мм | 995 мм | 500 мм | 495 мм | 50 | 100 | Оцинкованная сталь (INPLAST) | скрытые защелки |
| STWS-1000х525-Z-SO | 0.316 м² | 1000 мм | 995 мм | 525 мм | 520 мм | 53 | 100 | Оцинкованная сталь (INPLAST) | скрытые защелки |
| STWS-1000х550-Z-SO | 0.331 м² | 1000 мм | 995 мм | 550 мм | 545 мм | 55 | 100 | Оцинкованная сталь (INPLAST) | скрытые защелки |
| STWS-1000х600-Z-SO | 0.361 м² | 1000 мм | 995 мм | 600 мм | 595 мм | 60 | 100 | Оцинкованная сталь (INPLAST) | скрытые защелки |
| STWS-1000х625-Z-SO | 0.376 м² | 1000 мм | 995 мм | 625 мм | 620 мм | 63 | 100 | Оцинкованная сталь (INPLAST) | скрытые защелки |
| STWS-1000х650-Z-SO | 0.391 м² | 1000 мм | 995 мм | 650 мм | 645 мм | 65 | 100 | Оцинкованная сталь (INPLAST) | скрытые защелки |
| STWS-1025х100-Z-SO | 0.062 м² | 1025 мм | 1020 мм | 100 мм | 95 мм | 10 | 103 | Оцинкованная сталь (INPLAST) | скрытые защелки |
| STWS-1025х125-Z-SO | 0.077 м² | 1025 мм | 1020 мм | 125 мм | 120 мм | 13 | 103 | Оцинкованная сталь (INPLAST) | скрытые защелки |
| STWS-1025х150-Z-SO | 0.092 м² | 1025 мм | 1020 мм | 150 мм | 145 мм | 15 | 103 | Оцинкованная сталь (INPLAST) | скрытые защелки |
| STWS-1025х200-Z-SO | 0.123 м² | 1025 мм | 1020 мм | 200 мм | 195 мм | 20 | 103 | Оцинкованная сталь (INPLAST) | скрытые защелки |
| STWS-1025х225-Z-SO | 0.139 м² | 1025 мм | 1020 мм | 225 мм | 220 мм | 23 | 103 | Оцинкованная сталь (INPLAST) | скрытые защелки |
| STWS-1025х250-Z-SO | 0.154 м² | 1025 мм | 1020 мм | 250 мм | 245 мм | 25 | 103 | Оцинкованная сталь (INPLAST) | скрытые защелки |
| STWS-1025х300-Z-SO | 0.185 м² | 1025 мм | 1020 мм | 300 мм | 295 мм | 30 | 103 | Оцинкованная сталь (INPLAST) | скрытые защелки |
| STWS-1025х325-Z-SO | 0.200 м² | 1025 мм | 1020 мм | 325 мм | 320 мм | 33 | 103 | Оцинкованная сталь (INPLAST) | скрытые защелки |
| STWS-1025х350-Z-SO | 0.216 м² | 1025 мм | 1020 мм | 350 мм | 345 мм | 35 | 103 | Оцинкованная сталь (INPLAST) | скрытые защелки |
| STWS-1025х400-Z-SO | 0.247 м² | 1025 мм | 1020 мм | 400 мм | 395 мм | 40 | 103 | Оцинкованная сталь (INPLAST) | скрытые защелки |
| STWS-1025х425-Z-SO | 0.262 м² | 1025 мм | 1020 мм | 425 мм | 420 мм | 43 | 103 | Оцинкованная сталь (INPLAST) | скрытые защелки |
| STWS-1025х450-Z-SO | 0.277 м² | 1025 мм | 1020 мм | 450 мм | 445 мм | 45 | 103 | Оцинкованная сталь (INPLAST) | скрытые защелки |
| STWS-1025х500-Z-SO | 0.308 м² | 1025 мм | 1020 мм | 500 мм | 495 мм | 50 | 103 | Оцинкованная сталь (INPLAST) | скрытые защелки |
| STWS-1025х525-Z-SO | 0.324 м² | 1025 мм | 1020 мм | 525 мм | 520 мм | 53 | 103 | Оцинкованная сталь (INPLAST) | скрытые защелки |
| STWS-1025х550-Z-SO | 0.339 м² | 1025 мм | 1020 мм | 550 мм | 545 мм | 55 | 103 | Оцинкованная сталь (INPLAST) | скрытые защелки |
| STWS-1025х600-Z-SO | 0.370 м² | 1025 мм | 1020 мм | 600 мм | 595 мм | 60 | 103 | Оцинкованная сталь (INPLAST) | скрытые защелки |
| STWS-1025х625-Z-SO | 0.385 м² | 1025 мм | 1020 мм | 625 мм | 620 мм | 63 | 103 | Оцинкованная сталь (INPLAST) | скрытые защелки |
| STWS-1025х650-Z-SO | 0.401 м² | 1025 мм | 1020 мм | 650 мм | 645 мм | 65 | 103 | Оцинкованная сталь (INPLAST) | скрытые защелки |
| STWS-1050х100-Z-SO | 0.063 м² | 1050 мм | 1045 мм | 100 мм | 95 мм | 10 | 105 | Оцинкованная сталь (INPLAST) | скрытые защелки |
| STWS-1050х125-Z-SO | 0.079 м² | 1050 мм | 1045 мм | 125 мм | 120 мм | 13 | 105 | Оцинкованная сталь (INPLAST) | скрытые защелки |
| STWS-1050х150-Z-SO | 0.095 м² | 1050 мм | 1045 мм | 150 мм | 145 мм | 15 | 105 | Оцинкованная сталь (INPLAST) | скрытые защелки |
| STWS-1050х200-Z-SO | 0.126 м² | 1050 мм | 1045 мм | 200 мм | 195 мм | 20 | 105 | Оцинкованная сталь (INPLAST) | скрытые защелки |
| STWS-1050х225-Z-SO | 0.142 м² | 1050 мм | 1045 мм | 225 мм | 220 мм | 23 | 105 | Оцинкованная сталь (INPLAST) | скрытые защелки |
| STWS-1050х250-Z-SO | 0.158 м² | 1050 мм | 1045 мм | 250 мм | 245 мм | 25 | 105 | Оцинкованная сталь (INPLAST) | скрытые защелки |
| STWS-1050х300-Z-SO | 0.190 м² | 1050 мм | 1045 мм | 300 мм | 295 мм | 30 | 105 | Оцинкованная сталь (INPLAST) | скрытые защелки |
| STWS-1050х325-Z-SO | 0.205 м² | 1050 мм | 1045 мм | 325 мм | 320 мм | 33 | 105 | Оцинкованная сталь (INPLAST) | скрытые защелки |
| STWS-1050х350-Z-SO | 0.221 м² | 1050 мм | 1045 мм | 350 мм | 345 мм | 35 | 105 | Оцинкованная сталь (INPLAST) | скрытые защелки |
| STWS-1050х400-Z-SO | 0.253 м² | 1050 мм | 1045 мм | 400 мм | 395 мм | 40 | 105 | Оцинкованная сталь (INPLAST) | скрытые защелки |
| STWS-1050х425-Z-SO | 0.268 м² | 1050 мм | 1045 мм | 425 мм | 420 мм | 43 | 105 | Оцинкованная сталь (INPLAST) | скрытые защелки |
| STWS-1050х450-Z-SO | 0.284 м² | 1050 мм | 1045 мм | 450 мм | 445 мм | 45 | 105 | Оцинкованная сталь (INPLAST) | скрытые защелки |
| STWS-1050х500-Z-SO | 0.316 м² | 1050 мм | 1045 мм | 500 мм | 495 мм | 50 | 105 | Оцинкованная сталь (INPLAST) | скрытые защелки |
| STWS-1050х525-Z-SO | 0.332 м² | 1050 мм | 1045 мм | 525 мм | 520 мм | 53 | 105 | Оцинкованная сталь (INPLAST) | скрытые защелки |
| STWS-1050х550-Z-SO | 0.347 м² | 1050 мм | 1045 мм | 550 мм | 545 мм | 55 | 105 | Оцинкованная сталь (INPLAST) | скрытые защелки |
| STWS-1050х600-Z-SO | 0.379 м² | 1050 мм | 1045 мм | 600 мм | 595 мм | 60 | 105 | Оцинкованная сталь (INPLAST) | скрытые защелки |
| STWS-1050х625-Z-SO | 0.395 м² | 1050 мм | 1045 мм | 625 мм | 620 мм | 63 | 105 | Оцинкованная сталь (INPLAST) | скрытые защелки |
| STWS-1050х650-Z-SO | 0.411 м² | 1050 мм | 1045 мм | 650 мм | 645 мм | 65 | 105 | Оцинкованная сталь (INPLAST) | скрытые защелки |
| STWS-1100х100-Z-SO | 0.066 м² | 1100 мм | 1095 мм | 100 мм | 95 мм | 10 | 110 | Оцинкованная сталь (INPLAST) | скрытые защелки |
| STWS-1100х125-Z-SO | 0.083 м² | 1100 мм | 1095 мм | 125 мм | 120 мм | 13 | 110 | Оцинкованная сталь (INPLAST) | скрытые защелки |
| STWS-1100х150-Z-SO | 0.099 м² | 1100 мм | 1095 мм | 150 мм | 145 мм | 15 | 110 | Оцинкованная сталь (INPLAST) | скрытые защелки |
| STWS-1100х200-Z-SO | 0.132 м² | 1100 мм | 1095 мм | 200 мм | 195 мм | 20 | 110 | Оцинкованная сталь (INPLAST) | скрытые защелки |
| STWS-1100х225-Z-SO | 0.149 м² | 1100 мм | 1095 мм | 225 мм | 220 мм | 23 | 110 | Оцинкованная сталь (INPLAST) | скрытые защелки |
| STWS-1100х250-Z-SO | 0.165 м² | 1100 мм | 1095 мм | 250 мм | 245 мм | 25 | 110 | Оцинкованная сталь (INPLAST) | скрытые защелки |
| STWS-1100х300-Z-SO | 0.199 м² | 1100 мм | 1095 мм | 300 мм | 295 мм | 30 | 110 | Оцинкованная сталь (INPLAST) | скрытые защелки |
| STWS-1100х325-Z-SO | 0.215 м² | 1100 мм | 1095 мм | 325 мм | 320 мм | 33 | 110 | Оцинкованная сталь (INPLAST) | скрытые защелки |
| STWS-1100х350-Z-SO | 0.232 м² | 1100 мм | 1095 мм | 350 мм | 345 мм | 35 | 110 | Оцинкованная сталь (INPLAST) | скрытые защелки |
| STWS-1100х400-Z-SO | 0.265 м² | 1100 мм | 1095 мм | 400 мм | 395 мм | 40 | 110 | Оцинкованная сталь (INPLAST) | скрытые защелки |
| STWS-1100х425-Z-SO | 0.281 м² | 1100 мм | 1095 мм | 425 мм | 420 мм | 43 | 110 | Оцинкованная сталь (INPLAST) | скрытые защелки |
| STWS-1100х450-Z-SO | 0.298 м² | 1100 мм | 1095 мм | 450 мм | 445 мм | 45 | 110 | Оцинкованная сталь (INPLAST) | скрытые защелки |
| STWS-1100х500-Z-SO | 0.331 м² | 1100 мм | 1095 мм | 500 мм | 495 мм | 50 | 110 | Оцинкованная сталь (INPLAST) | скрытые защелки |
| STWS-1100х525-Z-SO | 0.347 м² | 1100 мм | 1095 мм | 525 мм | 520 мм | 53 | 110 | Оцинкованная сталь (INPLAST) | скрытые защелки |
| STWS-1100х550-Z-SO | 0.364 м² | 1100 мм | 1095 мм | 550 мм | 545 мм | 55 | 110 | Оцинкованная сталь (INPLAST) | скрытые защелки |
| STWS-1100х600-Z-SO | 0.397 м² | 1100 мм | 1095 мм | 600 мм | 595 мм | 60 | 110 | Оцинкованная сталь (INPLAST) | скрытые защелки |
| STWS-1100х625-Z-SO | 0.414 м² | 1100 мм | 1095 мм | 625 мм | 620 мм | 63 | 110 | Оцинкованная сталь (INPLAST) | скрытые защелки |
| STWS-1100х650-Z-SO | 0.430 м² | 1100 мм | 1095 мм | 650 мм | 645 мм | 65 | 110 | Оцинкованная сталь (INPLAST) | скрытые защелки |
| STWS-1125х100-Z-SO | 0.068 м² | 1125 мм | 1120 мм | 100 мм | 95 мм | 10 | 113 | Оцинкованная сталь (INPLAST) | скрытые защелки |
| STWS-1125х125-Z-SO | 0.085 м² | 1125 мм | 1120 мм | 125 мм | 120 мм | 13 | 113 | Оцинкованная сталь (INPLAST) | скрытые защелки |
| STWS-1125х150-Z-SO | 0.102 м² | 1125 мм | 1120 мм | 150 мм | 145 мм | 15 | 113 | Оцинкованная сталь (INPLAST) | скрытые защелки |
| STWS-1125х200-Z-SO | 0.135 м² | 1125 мм | 1120 мм | 200 мм | 195 мм | 20 | 113 | Оцинкованная сталь (INPLAST) | скрытые защелки |
| STWS-1125х225-Z-SO | 0.152 м² | 1125 мм | 1120 мм | 225 мм | 220 мм | 23 | 113 | Оцинкованная сталь (INPLAST) | скрытые защелки |
| STWS-1125х250-Z-SO | 0.169 м² | 1125 мм | 1120 мм | 250 мм | 245 мм | 25 | 113 | Оцинкованная сталь (INPLAST) | скрытые защелки |
| STWS-1125х300-Z-SO | 0.203 м² | 1125 мм | 1120 мм | 300 мм | 295 мм | 30 | 113 | Оцинкованная сталь (INPLAST) | скрытые защелки |
| STWS-1125х325-Z-SO | 0.220 м² | 1125 мм | 1120 мм | 325 мм | 320 мм | 33 | 113 | Оцинкованная сталь (INPLAST) | скрытые защелки |
| STWS-1125х350-Z-SO | 0.237 м² | 1125 мм | 1120 мм | 350 мм | 345 мм | 35 | 113 | Оцинкованная сталь (INPLAST) | скрытые защелки |
| STWS-1125х400-Z-SO | 0.271 м² | 1125 мм | 1120 мм | 400 мм | 395 мм | 40 | 113 | Оцинкованная сталь (INPLAST) | скрытые защелки |
| STWS-1125х425-Z-SO | 0.288 м² | 1125 мм | 1120 мм | 425 мм | 420 мм | 43 | 113 | Оцинкованная сталь (INPLAST) | скрытые защелки |
| STWS-1125х450-Z-SO | 0.305 м² | 1125 мм | 1120 мм | 450 мм | 445 мм | 45 | 113 | Оцинкованная сталь (INPLAST) | скрытые защелки |
| STWS-1125х500-Z-SO | 0.338 м² | 1125 мм | 1120 мм | 500 мм | 495 мм | 50 | 113 | Оцинкованная сталь (INPLAST) | скрытые защелки |
| STWS-1125х525-Z-SO | 0.355 м² | 1125 мм | 1120 мм | 525 мм | 520 мм | 53 | 113 | Оцинкованная сталь (INPLAST) | скрытые защелки |
| STWS-1125х550-Z-SO | 0.372 м² | 1125 мм | 1120 мм | 550 мм | 545 мм | 55 | 113 | Оцинкованная сталь (INPLAST) | скрытые защелки |
| STWS-1125х600-Z-SO | 0.406 м² | 1125 мм | 1120 мм | 600 мм | 595 мм | 60 | 113 | Оцинкованная сталь (INPLAST) | скрытые защелки |
| STWS-1125х625-Z-SO | 0.423 м² | 1125 мм | 1120 мм | 625 мм | 620 мм | 63 | 113 | Оцинкованная сталь (INPLAST) | скрытые защелки |
| STWS-1125х650-Z-SO | 0.440 м² | 1125 мм | 1120 мм | 650 мм | 645 мм | 65 | 113 | Оцинкованная сталь (INPLAST) | скрытые защелки |
| STWS-1150х100-Z-SO | 0.069 м² | 1150 мм | 1145 мм | 100 мм | 95 мм | 10 | 115 | Оцинкованная сталь (INPLAST) | скрытые защелки |
| STWS-1150х125-Z-SO | 0.086 м² | 1150 мм | 1145 мм | 125 мм | 120 мм | 13 | 115 | Оцинкованная сталь (INPLAST) | скрытые защелки |
| STWS-1150х150-Z-SO | 0.104 м² | 1150 мм | 1145 мм | 150 мм | 145 мм | 15 | 115 | Оцинкованная сталь (INPLAST) | скрытые защелки |
| STWS-1150х200-Z-SO | 0.138 м² | 1150 мм | 1145 мм | 200 мм | 195 мм | 20 | 115 | Оцинкованная сталь (INPLAST) | скрытые защелки |
| STWS-1150х225-Z-SO | 0.156 м² | 1150 мм | 1145 мм | 225 мм | 220 мм | 23 | 115 | Оцинкованная сталь (INPLAST) | скрытые защелки |
| STWS-1150х250-Z-SO | 0.173 м² | 1150 мм | 1145 мм | 250 мм | 245 мм | 25 | 115 | Оцинкованная сталь (INPLAST) | скрытые защелки |
| STWS-1150х300-Z-SO | 0.208 м² | 1150 мм | 1145 мм | 300 мм | 295 мм | 30 | 115 | Оцинкованная сталь (INPLAST) | скрытые защелки |
| STWS-1150х325-Z-SO | 0.225 м² | 1150 мм | 1145 мм | 325 мм | 320 мм | 33 | 115 | Оцинкованная сталь (INPLAST) | скрытые защелки |
| STWS-1150х350-Z-SO | 0.242 м² | 1150 мм | 1145 мм | 350 мм | 345 мм | 35 | 115 | Оцинкованная сталь (INPLAST) | скрытые защелки |
| STWS-1150х400-Z-SO | 0.277 м² | 1150 мм | 1145 мм | 400 мм | 395 мм | 40 | 115 | Оцинкованная сталь (INPLAST) | скрытые защелки |
| STWS-1150х425-Z-SO | 0.294 м² | 1150 мм | 1145 мм | 425 мм | 420 мм | 43 | 115 | Оцинкованная сталь (INPLAST) | скрытые защелки |
| STWS-1150х450-Z-SO | 0.311 м² | 1150 мм | 1145 мм | 450 мм | 445 мм | 45 | 115 | Оцинкованная сталь (INPLAST) | скрытые защелки |
| STWS-1150х500-Z-SO | 0.346 м² | 1150 мм | 1145 мм | 500 мм | 495 мм | 50 | 115 | Оцинкованная сталь (INPLAST) | скрытые защелки |
| STWS-1150х525-Z-SO | 0.363 м² | 1150 мм | 1145 мм | 525 мм | 520 мм | 53 | 115 | Оцинкованная сталь (INPLAST) | скрытые защелки |
| STWS-1150х550-Z-SO | 0.381 м² | 1150 мм | 1145 мм | 550 мм | 545 мм | 55 | 115 | Оцинкованная сталь (INPLAST) | скрытые защелки |
| STWS-1150х600-Z-SO | 0.415 м² | 1150 мм | 1145 мм | 600 мм | 595 мм | 60 | 115 | Оцинкованная сталь (INPLAST) | скрытые защелки |
| STWS-1150х625-Z-SO | 0.432 м² | 1150 мм | 1145 мм | 625 мм | 620 мм | 63 | 115 | Оцинкованная сталь (INPLAST) | скрытые защелки |
| STWS-1150х650-Z-SO | 0.450 м² | 1150 мм | 1145 мм | 650 мм | 645 мм | 65 | 115 | Оцинкованная сталь (INPLAST) | скрытые защелки |
| STWS-1200х100-Z-SO | 0.072 м² | 1200 мм | 1195 мм | 100 мм | 95 мм | 10 | 120 | Оцинкованная сталь (INPLAST) | скрытые защелки |
| STWS-1200х125-Z-SO | 0.090 м² | 1200 мм | 1195 мм | 125 мм | 120 мм | 13 | 120 | Оцинкованная сталь (INPLAST) | скрытые защелки |
| STWS-1200х150-Z-SO | 0.108 м² | 1200 мм | 1195 мм | 150 мм | 145 мм | 15 | 120 | Оцинкованная сталь (INPLAST) | скрытые защелки |
| STWS-1200х200-Z-SO | 0.144 м² | 1200 мм | 1195 мм | 200 мм | 195 мм | 20 | 120 | Оцинкованная сталь (INPLAST) | скрытые защелки |
| STWS-1200х225-Z-SO | 0.162 м² | 1200 мм | 1195 мм | 225 мм | 220 мм | 23 | 120 | Оцинкованная сталь (INPLAST) | скрытые защелки |
| STWS-1200х250-Z-SO | 0.180 м² | 1200 мм | 1195 мм | 250 мм | 245 мм | 25 | 120 | Оцинкованная сталь (INPLAST) | скрытые защелки |
| STWS-1200х300-Z-SO | 0.217 м² | 1200 мм | 1195 мм | 300 мм | 295 мм | 30 | 120 | Оцинкованная сталь (INPLAST) | скрытые защелки |
| STWS-1200х325-Z-SO | 0.235 м² | 1200 мм | 1195 мм | 325 мм | 320 мм | 33 | 120 | Оцинкованная сталь (INPLAST) | скрытые защелки |
| STWS-1200х350-Z-SO | 0.253 м² | 1200 мм | 1195 мм | 350 мм | 345 мм | 35 | 120 | Оцинкованная сталь (INPLAST) | скрытые защелки |
| STWS-1200х400-Z-SO | 0.289 м² | 1200 мм | 1195 мм | 400 мм | 395 мм | 40 | 120 | Оцинкованная сталь (INPLAST) | скрытые защелки |
| STWS-1200х425-Z-SO | 0.307 м² | 1200 мм | 1195 мм | 425 мм | 420 мм | 43 | 120 | Оцинкованная сталь (INPLAST) | скрытые защелки |
| STWS-1200х450-Z-SO | 0.325 м² | 1200 мм | 1195 мм | 450 мм | 445 мм | 45 | 120 | Оцинкованная сталь (INPLAST) | скрытые защелки |
| STWS-1200х500-Z-SO | 0.361 м² | 1200 мм | 1195 мм | 500 мм | 495 мм | 50 | 120 | Оцинкованная сталь (INPLAST) | скрытые защелки |
| STWS-1200х525-Z-SO | 0.379 м² | 1200 мм | 1195 мм | 525 мм | 520 мм | 53 | 120 | Оцинкованная сталь (INPLAST) | скрытые защелки |
| STWS-1200х550-Z-SO | 0.397 м² | 1200 мм | 1195 мм | 550 мм | 545 мм | 55 | 120 | Оцинкованная сталь (INPLAST) | скрытые защелки |
| STWS-1200х600-Z-SO | 0.433 м² | 1200 мм | 1195 мм | 600 мм | 595 мм | 60 | 120 | Оцинкованная сталь (INPLAST) | скрытые защелки |
| STWS-1200х625-Z-SO | 0.451 м² | 1200 мм | 1195 мм | 625 мм | 620 мм | 63 | 120 | Оцинкованная сталь (INPLAST) | скрытые защелки |
| STWS-1200х650-Z-SO | 0.469 м² | 1200 мм | 1195 мм | 650 мм | 645 мм | 65 | 120 | Оцинкованная сталь (INPLAST) | скрытые защелки |
| STWS-1225х100-Z-SO | 0.074 м² | 1225 мм | 1220 мм | 100 мм | 95 мм | 10 | 123 | Оцинкованная сталь (INPLAST) | скрытые защелки |
| STWS-1225х125-Z-SO | 0.092 м² | 1225 мм | 1220 мм | 125 мм | 120 мм | 13 | 123 | Оцинкованная сталь (INPLAST) | скрытые защелки |
| STWS-1225х150-Z-SO | 0.111 м² | 1225 мм | 1220 мм | 150 мм | 145 мм | 15 | 123 | Оцинкованная сталь (INPLAST) | скрытые защелки |
| STWS-1225х200-Z-SO | 0.147 м² | 1225 мм | 1220 мм | 200 мм | 195 мм | 20 | 123 | Оцинкованная сталь (INPLAST) | скрытые защелки |
| STWS-1225х225-Z-SO | 0.166 м² | 1225 мм | 1220 мм | 225 мм | 220 мм | 23 | 123 | Оцинкованная сталь (INPLAST) | скрытые защелки |
| STWS-1225х250-Z-SO | 0.184 м² | 1225 мм | 1220 мм | 250 мм | 245 мм | 25 | 123 | Оцинкованная сталь (INPLAST) | скрытые защелки |
| STWS-1225х300-Z-SO | 0.221 м² | 1225 мм | 1220 мм | 300 мм | 295 мм | 30 | 123 | Оцинкованная сталь (INPLAST) | скрытые защелки |
| STWS-1225х325-Z-SO | 0.240 м² | 1225 мм | 1220 мм | 325 мм | 320 мм | 33 | 123 | Оцинкованная сталь (INPLAST) | скрытые защелки |
| STWS-1225х350-Z-SO | 0.258 м² | 1225 мм | 1220 мм | 350 мм | 345 мм | 35 | 123 | Оцинкованная сталь (INPLAST) | скрытые защелки |
| STWS-1225х400-Z-SO | 0.295 м² | 1225 мм | 1220 мм | 400 мм | 395 мм | 40 | 123 | Оцинкованная сталь (INPLAST) | скрытые защелки |
| STWS-1225х425-Z-SO | 0.313 м² | 1225 мм | 1220 мм | 425 мм | 420 мм | 43 | 123 | Оцинкованная сталь (INPLAST) | скрытые защелки |
| STWS-1225х450-Z-SO | 0.332 м² | 1225 мм | 1220 мм | 450 мм | 445 мм | 45 | 123 | Оцинкованная сталь (INPLAST) | скрытые защелки |
| STWS-1225х500-Z-SO | 0.368 м² | 1225 мм | 1220 мм | 500 мм | 495 мм | 50 | 123 | Оцинкованная сталь (INPLAST) | скрытые защелки |
| STWS-1225х525-Z-SO | 0.387 м² | 1225 мм | 1220 мм | 525 мм | 520 мм | 53 | 123 | Оцинкованная сталь (INPLAST) | скрытые защелки |
| STWS-1225х550-Z-SO | 0.405 м² | 1225 мм | 1220 мм | 550 мм | 545 мм | 55 | 123 | Оцинкованная сталь (INPLAST) | скрытые защелки |
| STWS-1225х600-Z-SO | 0.442 м² | 1225 мм | 1220 мм | 600 мм | 595 мм | 60 | 123 | Оцинкованная сталь (INPLAST) | скрытые защелки |
| STWS-1225х625-Z-SO | 0.461 м² | 1225 мм | 1220 мм | 625 мм | 620 мм | 63 | 123 | Оцинкованная сталь (INPLAST) | скрытые защелки |
| STWS-1225х650-Z-SO | 0.479 м² | 1225 мм | 1220 мм | 650 мм | 645 мм | 65 | 123 | Оцинкованная сталь (INPLAST) | скрытые защелки |
| STWS-1250х100-Z-SO | 0.075 м² | 1250 мм | 1245 мм | 100 мм | 95 мм | 10 | 125 | Оцинкованная сталь (INPLAST) | скрытые защелки |
| STWS-1250х125-Z-SO | 0.094 м² | 1250 мм | 1245 мм | 125 мм | 120 мм | 13 | 125 | Оцинкованная сталь (INPLAST) | скрытые защелки |
| STWS-1250х150-Z-SO | 0.113 м² | 1250 мм | 1245 мм | 150 мм | 145 мм | 15 | 125 | Оцинкованная сталь (INPLAST) | скрытые защелки |
| STWS-1250х200-Z-SO | 0.150 м² | 1250 мм | 1245 мм | 200 мм | 195 мм | 20 | 125 | Оцинкованная сталь (INPLAST) | скрытые защелки |
| STWS-1250х225-Z-SO | 0.169 м² | 1250 мм | 1245 мм | 225 мм | 220 мм | 23 | 125 | Оцинкованная сталь (INPLAST) | скрытые защелки |
| STWS-1250х250-Z-SO | 0.188 м² | 1250 мм | 1245 мм | 250 мм | 245 мм | 25 | 125 | Оцинкованная сталь (INPLAST) | скрытые защелки |
| STWS-1250х300-Z-SO | 0.226 м² | 1250 мм | 1245 мм | 300 мм | 295 мм | 30 | 125 | Оцинкованная сталь (INPLAST) | скрытые защелки |
| STWS-1250х325-Z-SO | 0.244 м² | 1250 мм | 1245 мм | 325 мм | 320 мм | 33 | 125 | Оцинкованная сталь (INPLAST) | скрытые защелки |
| STWS-1250х350-Z-SO | 0.263 м² | 1250 мм | 1245 мм | 350 мм | 345 мм | 35 | 125 | Оцинкованная сталь (INPLAST) | скрытые защелки |
| STWS-1250х400-Z-SO | 0.301 м² | 1250 мм | 1245 мм | 400 мм | 395 мм | 40 | 125 | Оцинкованная сталь (INPLAST) | скрытые защелки |
| STWS-1250х425-Z-SO | 0.320 м² | 1250 мм | 1245 мм | 425 мм | 420 мм | 43 | 125 | Оцинкованная сталь (INPLAST) | скрытые защелки |
| STWS-1250х450-Z-SO | 0.338 м² | 1250 мм | 1245 мм | 450 мм | 445 мм | 45 | 125 | Оцинкованная сталь (INPLAST) | скрытые защелки |
| STWS-1250х500-Z-SO | 0.376 м² | 1250 мм | 1245 мм | 500 мм | 495 мм | 50 | 125 | Оцинкованная сталь (INPLAST) | скрытые защелки |
| STWS-1250х525-Z-SO | 0.395 м² | 1250 мм | 1245 мм | 525 мм | 520 мм | 53 | 125 | Оцинкованная сталь (INPLAST) | скрытые защелки |
| STWS-1250х550-Z-SO | 0.414 м² | 1250 мм | 1245 мм | 550 мм | 545 мм | 55 | 125 | Оцинкованная сталь (INPLAST) | скрытые защелки |
| STWS-1250х600-Z-SO | 0.451 м² | 1250 мм | 1245 мм | 600 мм | 595 мм | 60 | 125 | Оцинкованная сталь (INPLAST) | скрытые защелки |
| STWS-1250х625-Z-SO | 0.470 м² | 1250 мм | 1245 мм | 625 мм | 620 мм | 63 | 125 | Оцинкованная сталь (INPLAST) | скрытые защелки |
| STWS-1250х650-Z-SO | 0.489 м² | 1250 мм | 1245 мм | 650 мм | 645 мм | 65 | 125 | Оцинкованная сталь (INPLAST) | скрытые защелки |
| STWS-1300х100-Z-SO | 0.078 м² | 1300 мм | 1295 мм | 100 мм | 95 мм | 10 | 130 | Оцинкованная сталь (INPLAST) | скрытые защелки |
| STWS-1300х125-Z-SO | 0.098 м² | 1300 мм | 1295 мм | 125 мм | 120 мм | 13 | 130 | Оцинкованная сталь (INPLAST) | скрытые защелки |
| STWS-1300х150-Z-SO | 0.117 м² | 1300 мм | 1295 мм | 150 мм | 145 мм | 15 | 130 | Оцинкованная сталь (INPLAST) | скрытые защелки |
| STWS-1300х200-Z-SO | 0.156 м² | 1300 мм | 1295 мм | 200 мм | 195 мм | 20 | 130 | Оцинкованная сталь (INPLAST) | скрытые защелки |
| STWS-1300х225-Z-SO | 0.176 м² | 1300 мм | 1295 мм | 225 мм | 220 мм | 23 | 130 | Оцинкованная сталь (INPLAST) | скрытые защелки |
| STWS-1300х250-Z-SO | 0.196 м² | 1300 мм | 1295 мм | 250 мм | 245 мм | 25 | 130 | Оцинкованная сталь (INPLAST) | скрытые защелки |
| STWS-1300х300-Z-SO | 0.235 м² | 1300 мм | 1295 мм | 300 мм | 295 мм | 30 | 130 | Оцинкованная сталь (INPLAST) | скрытые защелки |
| STWS-1300х325-Z-SO | 0.254 м² | 1300 мм | 1295 мм | 325 мм | 320 мм | 33 | 130 | Оцинкованная сталь (INPLAST) | скрытые защелки |
| STWS-1300х350-Z-SO | 0.274 м² | 1300 мм | 1295 мм | 350 мм | 345 мм | 35 | 130 | Оцинкованная сталь (INPLAST) | скрытые защелки |
| STWS-1300х400-Z-SO | 0.313 м² | 1300 мм | 1295 мм | 400 мм | 395 мм | 40 | 130 | Оцинкованная сталь (INPLAST) | скрытые защелки |
| STWS-1300х425-Z-SO | 0.332 м² | 1300 мм | 1295 мм | 425 мм | 420 мм | 43 | 130 | Оцинкованная сталь (INPLAST) | скрытые защелки |
| STWS-1300х450-Z-SO | 0.352 м² | 1300 мм | 1295 мм | 450 мм | 445 мм | 45 | 130 | Оцинкованная сталь (INPLAST) | скрытые защелки |
| STWS-1300х500-Z-SO | 0.391 м² | 1300 мм | 1295 мм | 500 мм | 495 мм | 50 | 130 | Оцинкованная сталь (INPLAST) | скрытые защелки |
| STWS-1300х525-Z-SO | 0.411 м² | 1300 мм | 1295 мм | 525 мм | 520 мм | 53 | 130 | Оцинкованная сталь (INPLAST) | скрытые защелки |
| STWS-1300х550-Z-SO | 0.430 м² | 1300 мм | 1295 мм | 550 мм | 545 мм | 55 | 130 | Оцинкованная сталь (INPLAST) | скрытые защелки |
| STWS-1300х600-Z-SO | 0.469 м² | 1300 мм | 1295 мм | 600 мм | 595 мм | 60 | 130 | Оцинкованная сталь (INPLAST) | скрытые защелки |
| STWS-1300х625-Z-SO | 0.489 м² | 1300 мм | 1295 мм | 625 мм | 620 мм | 63 | 130 | Оцинкованная сталь (INPLAST) | скрытые защелки |
| STWS-1300х650-Z-SO | 0.508 м² | 1300 мм | 1295 мм | 650 мм | 645 мм | 65 | 130 | Оцинкованная сталь (INPLAST) | скрытые защелки |
| STWS-1325х100-Z-SO | 0.080 м² | 1325 мм | 1320 мм | 100 мм | 95 мм | 10 | 133 | Оцинкованная сталь (INPLAST) | скрытые защелки |
| STWS-1325х125-Z-SO | 0.100 м² | 1325 мм | 1320 мм | 125 мм | 120 мм | 13 | 133 | Оцинкованная сталь (INPLAST) | скрытые защелки |
| STWS-1325х150-Z-SO | 0.120 м² | 1325 мм | 1320 мм | 150 мм | 145 мм | 15 | 133 | Оцинкованная сталь (INPLAST) | скрытые защелки |
| STWS-1325х200-Z-SO | 0.159 м² | 1325 мм | 1320 мм | 200 мм | 195 мм | 20 | 133 | Оцинкованная сталь (INPLAST) | скрытые защелки |
| STWS-1325х225-Z-SO | 0.179 м² | 1325 мм | 1320 мм | 225 мм | 220 мм | 23 | 133 | Оцинкованная сталь (INPLAST) | скрытые защелки |
| STWS-1325х250-Z-SO | 0.199 м² | 1325 мм | 1320 мм | 250 мм | 245 мм | 25 | 133 | Оцинкованная сталь (INPLAST) | скрытые защелки |
| STWS-1325х300-Z-SO | 0.239 м² | 1325 мм | 1320 мм | 300 мм | 295 мм | 30 | 133 | Оцинкованная сталь (INPLAST) | скрытые защелки |
| STWS-1325х325-Z-SO | 0.259 м² | 1325 мм | 1320 мм | 325 мм | 320 мм | 33 | 133 | Оцинкованная сталь (INPLAST) | скрытые защелки |
| STWS-1325х350-Z-SO | 0.279 м² | 1325 мм | 1320 мм | 350 мм | 345 мм | 35 | 133 | Оцинкованная сталь (INPLAST) | скрытые защелки |
| STWS-1325х400-Z-SO | 0.319 м² | 1325 мм | 1320 мм | 400 мм | 395 мм | 40 | 133 | Оцинкованная сталь (INPLAST) | скрытые защелки |
| STWS-1325х425-Z-SO | 0.339 м² | 1325 мм | 1320 мм | 425 мм | 420 мм | 43 | 133 | Оцинкованная сталь (INPLAST) | скрытые защелки |
| STWS-1325х450-Z-SO | 0.359 м² | 1325 мм | 1320 мм | 450 мм | 445 мм | 45 | 133 | Оцинкованная сталь (INPLAST) | скрытые защелки |
| STWS-1325х500-Z-SO | 0.399 м² | 1325 мм | 1320 мм | 500 мм | 495 мм | 50 | 133 | Оцинкованная сталь (INPLAST) | скрытые защелки |
| STWS-1325х525-Z-SO | 0.418 м² | 1325 мм | 1320 мм | 525 мм | 520 мм | 53 | 133 | Оцинкованная сталь (INPLAST) | скрытые защелки |
| STWS-1325х550-Z-SO | 0.438 м² | 1325 мм | 1320 мм | 550 мм | 545 мм | 55 | 133 | Оцинкованная сталь (INPLAST) | скрытые защелки |
| STWS-1325х600-Z-SO | 0.478 м² | 1325 мм | 1320 мм | 600 мм | 595 мм | 60 | 133 | Оцинкованная сталь (INPLAST) | скрытые защелки |
| STWS-1325х625-Z-SO | 0.498 м² | 1325 мм | 1320 мм | 625 мм | 620 мм | 63 | 133 | Оцинкованная сталь (INPLAST) | скрытые защелки |
| STWS-1325х650-Z-SO | 0.518 м² | 1325 мм | 1320 мм | 650 мм | 645 мм | 65 | 133 | Оцинкованная сталь (INPLAST) | скрытые защелки |
| STWS-1350х100-Z-SO | 0.081 м² | 1350 мм | 1345 мм | 100 мм | 95 мм | 10 | 135 | Оцинкованная сталь (INPLAST) | скрытые защелки |
| STWS-1350х125-Z-SO | 0.102 м² | 1350 мм | 1345 мм | 125 мм | 120 мм | 13 | 135 | Оцинкованная сталь (INPLAST) | скрытые защелки |
| STWS-1350х150-Z-SO | 0.122 м² | 1350 мм | 1345 мм | 150 мм | 145 мм | 15 | 135 | Оцинкованная сталь (INPLAST) | скрытые защелки |
| STWS-1350х200-Z-SO | 0.162 м² | 1350 мм | 1345 мм | 200 мм | 195 мм | 20 | 135 | Оцинкованная сталь (INPLAST) | скрытые защелки |
| STWS-1350х225-Z-SO | 0.183 м² | 1350 мм | 1345 мм | 225 мм | 220 мм | 23 | 135 | Оцинкованная сталь (INPLAST) | скрытые защелки |
| STWS-1350х250-Z-SO | 0.203 м² | 1350 мм | 1345 мм | 250 мм | 245 мм | 25 | 135 | Оцинкованная сталь (INPLAST) | скрытые защелки |
| STWS-1350х300-Z-SO | 0.244 м² | 1350 мм | 1345 мм | 300 мм | 295 мм | 30 | 135 | Оцинкованная сталь (INPLAST) | скрытые защелки |
| STWS-1350х325-Z-SO | 0.264 м² | 1350 мм | 1345 мм | 325 мм | 320 мм | 33 | 135 | Оцинкованная сталь (INPLAST) | скрытые защелки |
| STWS-1350х350-Z-SO | 0.284 м² | 1350 мм | 1345 мм | 350 мм | 345 мм | 35 | 135 | Оцинкованная сталь (INPLAST) | скрытые защелки |
| STWS-1350х400-Z-SO | 0.325 м² | 1350 мм | 1345 мм | 400 мм | 395 мм | 40 | 135 | Оцинкованная сталь (INPLAST) | скрытые защелки |
| STWS-1350х425-Z-SO | 0.345 м² | 1350 мм | 1345 мм | 425 мм | 420 мм | 43 | 135 | Оцинкованная сталь (INPLAST) | скрытые защелки |
| STWS-1350х450-Z-SO | 0.365 м² | 1350 мм | 1345 мм | 450 мм | 445 мм | 45 | 135 | Оцинкованная сталь (INPLAST) | скрытые защелки |
| STWS-1350х500-Z-SO | 0.406 м² | 1350 мм | 1345 мм | 500 мм | 495 мм | 50 | 135 | Оцинкованная сталь (INPLAST) | скрытые защелки |
| STWS-1350х525-Z-SO | 0.426 м² | 1350 мм | 1345 мм | 525 мм | 520 мм | 53 | 135 | Оцинкованная сталь (INPLAST) | скрытые защелки |
| STWS-1350х550-Z-SO | 0.447 м² | 1350 мм | 1345 мм | 550 мм | 545 мм | 55 | 135 | Оцинкованная сталь (INPLAST) | скрытые защелки |
| STWS-1350х600-Z-SO | 0.487 м² | 1350 мм | 1345 мм | 600 мм | 595 мм | 60 | 135 | Оцинкованная сталь (INPLAST) | скрытые защелки |
| STWS-1350х625-Z-SO | 0.508 м² | 1350 мм | 1345 мм | 625 мм | 620 мм | 63 | 135 | Оцинкованная сталь (INPLAST) | скрытые защелки |
| STWS-1350х650-Z-SO | 0.528 м² | 1350 мм | 1345 мм | 650 мм | 645 мм | 65 | 135 | Оцинкованная сталь (INPLAST) | скрытые защелки |
| STWS-1400х100-Z-SO | 0.084 м² | 1400 мм | 1395 мм | 100 мм | 95 мм | 10 | 140 | Оцинкованная сталь (INPLAST) | скрытые защелки |
| STWS-1400х125-Z-SO | 0.105 м² | 1400 мм | 1395 мм | 125 мм | 120 мм | 13 | 140 | Оцинкованная сталь (INPLAST) | скрытые защелки |
| STWS-1400х150-Z-SO | 0.126 м² | 1400 мм | 1395 мм | 150 мм | 145 мм | 15 | 140 | Оцинкованная сталь (INPLAST) | скрытые защелки |
| STWS-1400х200-Z-SO | 0.168 м² | 1400 мм | 1395 мм | 200 мм | 195 мм | 20 | 140 | Оцинкованная сталь (INPLAST) | скрытые защелки |
| STWS-1400х225-Z-SO | 0.190 м² | 1400 мм | 1395 мм | 225 мм | 220 мм | 23 | 140 | Оцинкованная сталь (INPLAST) | скрытые защелки |
| STWS-1400х250-Z-SO | 0.211 м² | 1400 мм | 1395 мм | 250 мм | 245 мм | 25 | 140 | Оцинкованная сталь (INPLAST) | скрытые защелки |
| STWS-1400х300-Z-SO | 0.253 м² | 1400 мм | 1395 мм | 300 мм | 295 мм | 30 | 140 | Оцинкованная сталь (INPLAST) | скрытые защелки |
| STWS-1400х325-Z-SO | 0.274 м² | 1400 мм | 1395 мм | 325 мм | 320 мм | 33 | 140 | Оцинкованная сталь (INPLAST) | скрытые защелки |
| STWS-1400х350-Z-SO | 0.295 м² | 1400 мм | 1395 мм | 350 мм | 345 мм | 35 | 140 | Оцинкованная сталь (INPLAST) | скрытые защелки |
| STWS-1400х400-Z-SO | 0.337 м² | 1400 мм | 1395 мм | 400 мм | 395 мм | 40 | 140 | Оцинкованная сталь (INPLAST) | скрытые защелки |
| STWS-1400х425-Z-SO | 0.358 м² | 1400 мм | 1395 мм | 425 мм | 420 мм | 43 | 140 | Оцинкованная сталь (INPLAST) | скрытые защелки |
| STWS-1400х450-Z-SO | 0.379 м² | 1400 мм | 1395 мм | 450 мм | 445 мм | 45 | 140 | Оцинкованная сталь (INPLAST) | скрытые защелки |
| STWS-1400х500-Z-SO | 0.421 м² | 1400 мм | 1395 мм | 500 мм | 495 мм | 50 | 140 | Оцинкованная сталь (INPLAST) | скрытые защелки |
| STWS-1400х525-Z-SO | 0.442 м² | 1400 мм | 1395 мм | 525 мм | 520 мм | 53 | 140 | Оцинкованная сталь (INPLAST) | скрытые защелки |
| STWS-1400х550-Z-SO | 0.463 м² | 1400 мм | 1395 мм | 550 мм | 545 мм | 55 | 140 | Оцинкованная сталь (INPLAST) | скрытые защелки |
| STWS-1400х600-Z-SO | 0.505 м² | 1400 мм | 1395 мм | 600 мм | 595 мм | 60 | 140 | Оцинкованная сталь (INPLAST) | скрытые защелки |
| STWS-1400х625-Z-SO | 0.526 м² | 1400 мм | 1395 мм | 625 мм | 620 мм | 63 | 140 | Оцинкованная сталь (INPLAST) | скрытые защелки |
| STWS-1400х650-Z-SO | 0.547 м² | 1400 мм | 1395 мм | 650 мм | 645 мм | 65 | 140 | Оцинкованная сталь (INPLAST) | скрытые защелки |
| STWS-1425х100-Z-SO | 0.086 м² | 1425 мм | 1420 мм | 100 мм | 95 мм | 10 | 143 | Оцинкованная сталь (INPLAST) | скрытые защелки |
| STWS-1425х125-Z-SO | 0.107 м² | 1425 мм | 1420 мм | 125 мм | 120 мм | 13 | 143 | Оцинкованная сталь (INPLAST) | скрытые защелки |
| STWS-1425х150-Z-SO | 0.129 м² | 1425 мм | 1420 мм | 150 мм | 145 мм | 15 | 143 | Оцинкованная сталь (INPLAST) | скрытые защелки |
| STWS-1425х200-Z-SO | 0.171 м² | 1425 мм | 1420 мм | 200 мм | 195 мм | 20 | 143 | Оцинкованная сталь (INPLAST) | скрытые защелки |
| STWS-1425х225-Z-SO | 0.193 м² | 1425 мм | 1420 мм | 225 мм | 220 мм | 23 | 143 | Оцинкованная сталь (INPLAST) | скрытые защелки |
| STWS-1425х250-Z-SO | 0.214 м² | 1425 мм | 1420 мм | 250 мм | 245 мм | 25 | 143 | Оцинкованная сталь (INPLAST) | скрытые защелки |
| STWS-1425х300-Z-SO | 0.257 м² | 1425 мм | 1420 мм | 300 мм | 295 мм | 30 | 143 | Оцинкованная сталь (INPLAST) | скрытые защелки |
| STWS-1425х325-Z-SO | 0.279 м² | 1425 мм | 1420 мм | 325 мм | 320 мм | 33 | 143 | Оцинкованная сталь (INPLAST) | скрытые защелки |
| STWS-1425х350-Z-SO | 0.300 м² | 1425 мм | 1420 мм | 350 мм | 345 мм | 35 | 143 | Оцинкованная сталь (INPLAST) | скрытые защелки |
| STWS-1425х400-Z-SO | 0.343 м² | 1425 мм | 1420 мм | 400 мм | 395 мм | 40 | 143 | Оцинкованная сталь (INPLAST) | скрытые защелки |
| STWS-1425х425-Z-SO | 0.364 м² | 1425 мм | 1420 мм | 425 мм | 420 мм | 43 | 143 | Оцинкованная сталь (INPLAST) | скрытые защелки |
| STWS-1425х450-Z-SO | 0.386 м² | 1425 мм | 1420 мм | 450 мм | 445 мм | 45 | 143 | Оцинкованная сталь (INPLAST) | скрытые защелки |
| STWS-1425х500-Z-SO | 0.429 м² | 1425 мм | 1420 мм | 500 мм | 495 мм | 50 | 143 | Оцинкованная сталь (INPLAST) | скрытые защелки |
| STWS-1425х525-Z-SO | 0.450 м² | 1425 мм | 1420 мм | 525 мм | 520 мм | 53 | 143 | Оцинкованная сталь (INPLAST) | скрытые защелки |
| STWS-1425х550-Z-SO | 0.472 м² | 1425 мм | 1420 мм | 550 мм | 545 мм | 55 | 143 | Оцинкованная сталь (INPLAST) | скрытые защелки |
| STWS-1425х600-Z-SO | 0.514 м² | 1425 мм | 1420 мм | 600 мм | 595 мм | 60 | 143 | Оцинкованная сталь (INPLAST) | скрытые защелки |
| STWS-1425х625-Z-SO | 0.536 м² | 1425 мм | 1420 мм | 625 мм | 620 мм | 63 | 143 | Оцинкованная сталь (INPLAST) | скрытые защелки |
| STWS-1425х650-Z-SO | 0.557 м² | 1425 мм | 1420 мм | 650 мм | 645 мм | 65 | 143 | Оцинкованная сталь (INPLAST) | скрытые защелки |
| STWS-1450х100-Z-SO | 0.087 м² | 1450 мм | 1445 мм | 100 мм | 95 мм | 10 | 145 | Оцинкованная сталь (INPLAST) | скрытые защелки |
| STWS-1450х125-Z-SO | 0.109 м² | 1450 мм | 1445 мм | 125 мм | 120 мм | 13 | 145 | Оцинкованная сталь (INPLAST) | скрытые защелки |
| STWS-1450х150-Z-SO | 0.131 м² | 1450 мм | 1445 мм | 150 мм | 145 мм | 15 | 145 | Оцинкованная сталь (INPLAST) | скрытые защелки |
| STWS-1450х200-Z-SO | 0.174 м² | 1450 мм | 1445 мм | 200 мм | 195 мм | 20 | 145 | Оцинкованная сталь (INPLAST) | скрытые защелки |
| STWS-1450х225-Z-SO | 0.196 м² | 1450 мм | 1445 мм | 225 мм | 220 мм | 23 | 145 | Оцинкованная сталь (INPLAST) | скрытые защелки |
| STWS-1450х250-Z-SO | 0.218 м² | 1450 мм | 1445 мм | 250 мм | 245 мм | 25 | 145 | Оцинкованная сталь (INPLAST) | скрытые защелки |
| STWS-1450х300-Z-SO | 0.262 м² | 1450 мм | 1445 мм | 300 мм | 295 мм | 30 | 145 | Оцинкованная сталь (INPLAST) | скрытые защелки |
| STWS-1450х325-Z-SO | 0.284 м² | 1450 мм | 1445 мм | 325 мм | 320 мм | 33 | 145 | Оцинкованная сталь (INPLAST) | скрытые защелки |
| STWS-1450х350-Z-SO | 0.305 м² | 1450 мм | 1445 мм | 350 мм | 345 мм | 35 | 145 | Оцинкованная сталь (INPLAST) | скрытые защелки |
| STWS-1450х400-Z-SO | 0.349 м² | 1450 мм | 1445 мм | 400 мм | 395 мм | 40 | 145 | Оцинкованная сталь (INPLAST) | скрытые защелки |
| STWS-1450х425-Z-SO | 0.371 м² | 1450 мм | 1445 мм | 425 мм | 420 мм | 43 | 145 | Оцинкованная сталь (INPLAST) | скрытые защелки |
| STWS-1450х450-Z-SO | 0.393 м² | 1450 мм | 1445 мм | 450 мм | 445 мм | 45 | 145 | Оцинкованная сталь (INPLAST) | скрытые защелки |
| STWS-1450х500-Z-SO | 0.436 м² | 1450 мм | 1445 мм | 500 мм | 495 мм | 50 | 145 | Оцинкованная сталь (INPLAST) | скрытые защелки |
| STWS-1450х525-Z-SO | 0.458 м² | 1450 мм | 1445 мм | 525 мм | 520 мм | 53 | 145 | Оцинкованная сталь (INPLAST) | скрытые защелки |
| STWS-1450х550-Z-SO | 0.480 м² | 1450 мм | 1445 мм | 550 мм | 545 мм | 55 | 145 | Оцинкованная сталь (INPLAST) | скрытые защелки |
| STWS-1450х600-Z-SO | 0.523 м² | 1450 мм | 1445 мм | 600 мм | 595 мм | 60 | 145 | Оцинкованная сталь (INPLAST) | скрытые защелки |
| STWS-1450х625-Z-SO | 0.545 м² | 1450 мм | 1445 мм | 625 мм | 620 мм | 63 | 145 | Оцинкованная сталь (INPLAST) | скрытые защелки |
| STWS-1450х650-Z-SO | 0.567 м² | 1450 мм | 1445 мм | 650 мм | 645 мм | 65 | 145 | Оцинкованная сталь (INPLAST) | скрытые защелки |
| STWS-1500х100-Z-SO | 0.090 м² | 1500 мм | 1495 мм | 100 мм | 95 мм | 10 | 150 | Оцинкованная сталь (INPLAST) | скрытые защелки |
| STWS-1500х125-Z-SO | 0.113 м² | 1500 мм | 1495 мм | 125 мм | 120 мм | 13 | 150 | Оцинкованная сталь (INPLAST) | скрытые защелки |
| STWS-1500х150-Z-SO | 0.135 м² | 1500 мм | 1495 мм | 150 мм | 145 мм | 15 | 150 | Оцинкованная сталь (INPLAST) | скрытые защелки |
| STWS-1500х200-Z-SO | 0.180 м² | 1500 мм | 1495 мм | 200 мм | 195 мм | 20 | 150 | Оцинкованная сталь (INPLAST) | скрытые защелки |
| STWS-1500х225-Z-SO | 0.203 м² | 1500 мм | 1495 мм | 225 мм | 220 мм | 23 | 150 | Оцинкованная сталь (INPLAST) | скрытые защелки |
| STWS-1500х250-Z-SO | 0.226 м² | 1500 мм | 1495 мм | 250 мм | 245 мм | 25 | 150 | Оцинкованная сталь (INPLAST) | скрытые защелки |
| STWS-1500х300-Z-SO | 0.271 м² | 1500 мм | 1495 мм | 300 мм | 295 мм | 30 | 150 | Оцинкованная сталь (INPLAST) | скрытые защелки |
| STWS-1500х325-Z-SO | 0.293 м² | 1500 мм | 1495 мм | 325 мм | 320 мм | 33 | 150 | Оцинкованная сталь (INPLAST) | скрытые защелки |
| STWS-1500х350-Z-SO | 0.316 м² | 1500 мм | 1495 мм | 350 мм | 345 мм | 35 | 150 | Оцинкованная сталь (INPLAST) | скрытые защелки |
| STWS-1500х400-Z-SO | 0.361 м² | 1500 мм | 1495 мм | 400 мм | 395 мм | 40 | 150 | Оцинкованная сталь (INPLAST) | скрытые защелки |
| STWS-1500х425-Z-SO | 0.384 м² | 1500 мм | 1495 мм | 425 мм | 420 мм | 43 | 150 | Оцинкованная сталь (INPLAST) | скрытые защелки |
| STWS-1500х450-Z-SO | 0.406 м² | 1500 мм | 1495 мм | 450 мм | 445 мм | 45 | 150 | Оцинкованная сталь (INPLAST) | скрытые защелки |
| STWS-1500х500-Z-SO | 0.451 м² | 1500 мм | 1495 мм | 500 мм | 495 мм | 50 | 150 | Оцинкованная сталь (INPLAST) | скрытые защелки |
| STWS-1500х525-Z-SO | 0.474 м² | 1500 мм | 1495 мм | 525 мм | 520 мм | 53 | 150 | Оцинкованная сталь (INPLAST) | скрытые защелки |
| STWS-1500х550-Z-SO | 0.496 м² | 1500 мм | 1495 мм | 550 мм | 545 мм | 55 | 150 | Оцинкованная сталь (INPLAST) | скрытые защелки |
| STWS-1500х600-Z-SO | 0.541 м² | 1500 мм | 1495 мм | 600 мм | 595 мм | 60 | 150 | Оцинкованная сталь (INPLAST) | скрытые защелки |
| STWS-1500х625-Z-SO | 0.564 м² | 1500 мм | 1495 мм | 625 мм | 620 мм | 63 | 150 | Оцинкованная сталь (INPLAST) | скрытые защелки |
| STWS-1500х650-Z-SO | 0.587 м² | 1500 мм | 1495 мм | 650 мм | 645 мм | 65 | 150 | Оцинкованная сталь (INPLAST) | скрытые защелки |

note: column(s) folded — value = type name in every type: Комментарии к типоразмеру
